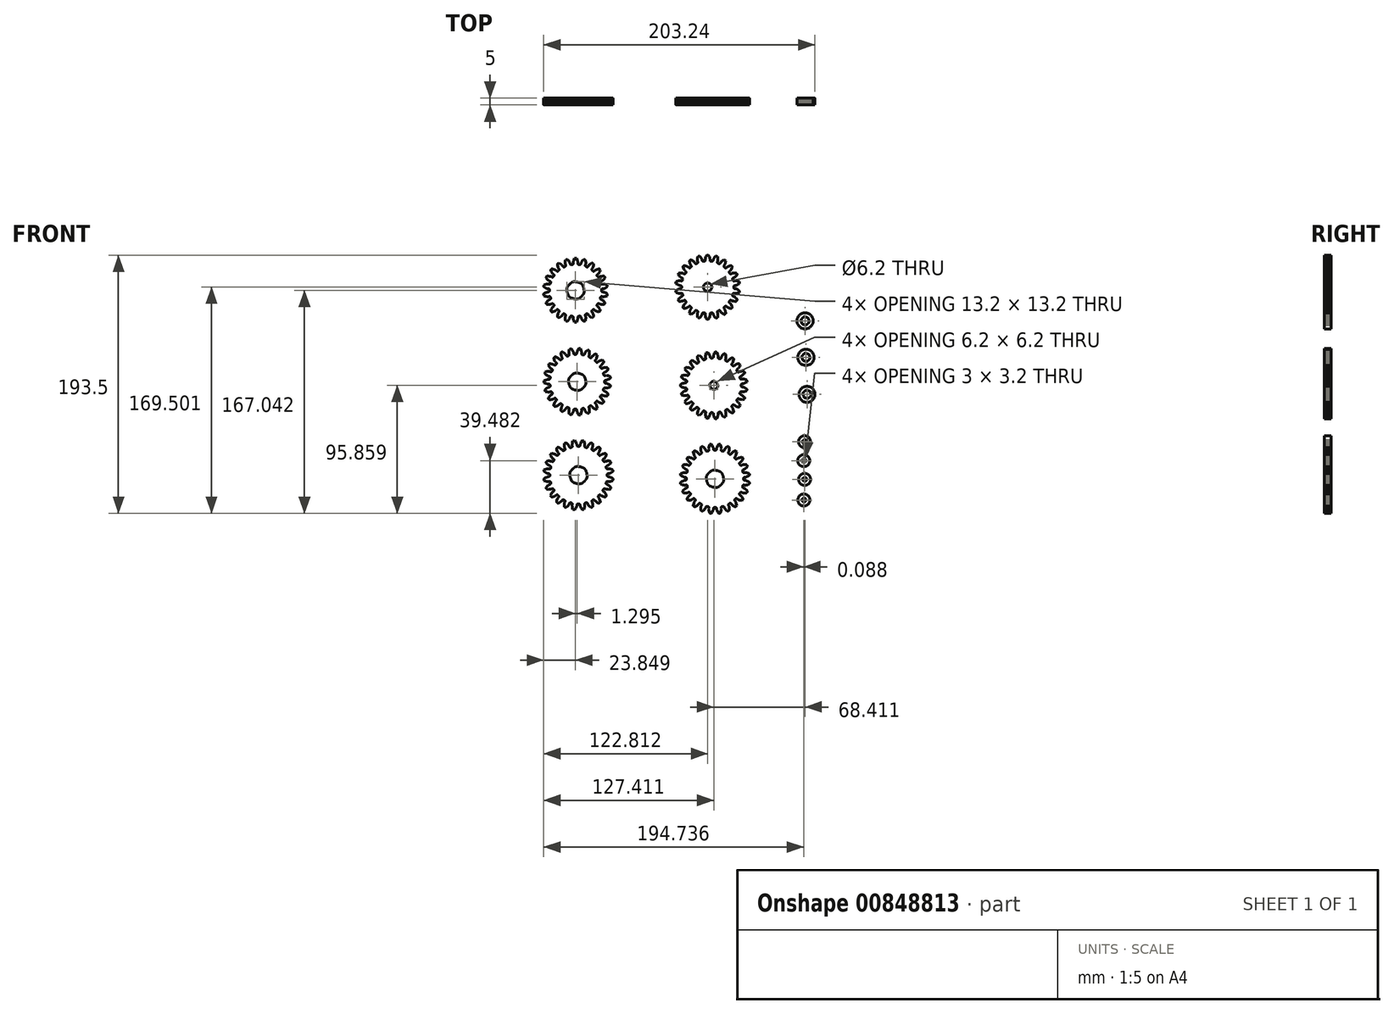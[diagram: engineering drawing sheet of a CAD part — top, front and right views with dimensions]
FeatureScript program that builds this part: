
annotation { "Feature Type Name" : "Feature", "Feature Type Description" : "" }
export const myFeature = defineFeature(function(context is Context, id is Id, definition is map)
    precondition{}
    {
        {
            var Q0;
            Q0=qCreatedBy(makeId("Front.planeOp"),FACE);
            var sketch = newSketch(context, id + "F0", { "sketchPlane" : qUnion([Q0])});
            skArc(sketch, "E0", {"start": v(8.16, 58.25) * mm, "mid": v(8.42, 58.01) * mm, "end": v(8.7, 57.79) * mm});
            skArc(sketch, "E1", {"start": v(8.16, 58.25) * mm, "mid": v(7.61, 58.45) * mm, "end": v(7.08, 58.2) * mm});
            skLineSegment(sketch, "E2", {"start": v(4.56, 56.78) * mm, "end": v(3.52, 56.5) * mm});
            skLineSegment(sketch, "E3", {"start": v(5.47, 57.12) * mm, "end": v(4.56, 56.78) * mm});
            skLineSegment(sketch, "E4", {"start": v(5.8, 57.28) * mm, "end": v(5.47, 57.12) * mm});
            skLineSegment(sketch, "E5", {"start": v(6.11, 57.44) * mm, "end": v(5.8, 57.28) * mm});
            skLineSegment(sketch, "E6", {"start": v(6.38, 57.6) * mm, "end": v(6.11, 57.44) * mm});
            skLineSegment(sketch, "E7", {"start": v(6.6, 57.75) * mm, "end": v(6.38, 57.6) * mm});
            skLineSegment(sketch, "E8", {"start": v(6.75, 57.88) * mm, "end": v(6.6, 57.75) * mm});
            skLineSegment(sketch, "E9", {"start": v(7.08, 58.2) * mm, "end": v(6.75, 57.88) * mm});
            skArc(sketch, "E10", {"start": v(2.6, 57.57) * mm, "mid": v(3.05, 57.03) * mm, "end": v(3.52, 56.5) * mm});
            skLineSegment(sketch, "E11", {"start": v(3.02, 58.56) * mm, "end": v(2.6, 57.57) * mm});
            skLineSegment(sketch, "E12", {"start": v(3.48, 59.41) * mm, "end": v(3.02, 58.56) * mm});
            skLineSegment(sketch, "E13", {"start": v(3.69, 59.72) * mm, "end": v(3.48, 59.41) * mm});
            skLineSegment(sketch, "E14", {"start": v(3.89, 60) * mm, "end": v(3.69, 59.72) * mm});
            skLineSegment(sketch, "E15", {"start": v(4.09, 60.24) * mm, "end": v(3.89, 60) * mm});
            skLineSegment(sketch, "E16", {"start": v(4.27, 60.44) * mm, "end": v(4.09, 60.24) * mm});
            skLineSegment(sketch, "E17", {"start": v(4.42, 60.58) * mm, "end": v(4.27, 60.44) * mm});
            skLineSegment(sketch, "E18", {"start": v(4.8, 60.85) * mm, "end": v(4.42, 60.58) * mm});
            skArc(sketch, "E19", {"start": v(4.8, 60.85) * mm, "mid": v(5.1, 61.35) * mm, "end": v(4.98, 61.91) * mm});
            skArc(sketch, "E20", {"start": v(4.6, 62.5) * mm, "mid": v(4.79, 62.2) * mm, "end": v(4.98, 61.92) * mm});
            skArc(sketch, "E21", {"start": v(4.6, 62.5) * mm, "mid": v(4.13, 62.85) * mm, "end": v(3.56, 62.77) * mm});
            skLineSegment(sketch, "E22", {"start": v(0.74, 62.11) * mm, "end": v(-0.34, 62.15) * mm});
            skLineSegment(sketch, "E23", {"start": v(1.7, 62.18) * mm, "end": v(0.74, 62.11) * mm});
            skLineSegment(sketch, "E24", {"start": v(2.07, 62.24) * mm, "end": v(1.7, 62.18) * mm});
            skLineSegment(sketch, "E25", {"start": v(2.4, 62.3) * mm, "end": v(2.07, 62.24) * mm});
            skLineSegment(sketch, "E26", {"start": v(2.7, 62.39) * mm, "end": v(2.4, 62.3) * mm});
            skLineSegment(sketch, "E27", {"start": v(2.97, 62.47) * mm, "end": v(2.7, 62.39) * mm});
            skLineSegment(sketch, "E28", {"start": v(3.15, 62.55) * mm, "end": v(2.97, 62.47) * mm});
            skLineSegment(sketch, "E29", {"start": v(3.56, 62.77) * mm, "end": v(3.15, 62.55) * mm});
            skArc(sketch, "E30", {"start": v(-0.92, 63.43) * mm, "mid": v(-0.64, 62.78) * mm, "end": v(-0.34, 62.15) * mm});
            skLineSegment(sketch, "E31", {"start": v(-0.24, 64.26) * mm, "end": v(-0.92, 63.43) * mm});
            skLineSegment(sketch, "E32", {"start": v(0.44, 64.94) * mm, "end": v(-0.24, 64.26) * mm});
            skLineSegment(sketch, "E33", {"start": v(0.73, 65.18) * mm, "end": v(0.44, 64.94) * mm});
            skLineSegment(sketch, "E34", {"start": v(1, 65.4) * mm, "end": v(0.73, 65.18) * mm});
            skLineSegment(sketch, "E35", {"start": v(1.26, 65.57) * mm, "end": v(1, 65.4) * mm});
            skLineSegment(sketch, "E36", {"start": v(1.49, 65.7) * mm, "end": v(1.26, 65.57) * mm});
            skLineSegment(sketch, "E37", {"start": v(1.67, 65.8) * mm, "end": v(1.49, 65.7) * mm});
            skLineSegment(sketch, "E38", {"start": v(2.1, 65.96) * mm, "end": v(1.67, 65.8) * mm});
            skArc(sketch, "E39", {"start": v(2.1, 65.96) * mm, "mid": v(2.54, 66.34) * mm, "end": v(2.58, 66.92) * mm});
            skArc(sketch, "E40", {"start": v(2.39, 67.6) * mm, "mid": v(2.48, 67.26) * mm, "end": v(2.58, 66.92) * mm});
            skArc(sketch, "E41", {"start": v(2.39, 67.6) * mm, "mid": v(2.03, 68.06) * mm, "end": v(1.46, 68.15) * mm});
            skLineSegment(sketch, "E42", {"start": v(-1.43, 68.3) * mm, "end": v(-2.45, 68.64) * mm});
            skLineSegment(sketch, "E43", {"start": v(-0.49, 68.1) * mm, "end": v(-1.43, 68.3) * mm});
            skLineSegment(sketch, "E44", {"start": v(-0.12, 68.05) * mm, "end": v(-0.49, 68.1) * mm});
            skLineSegment(sketch, "E45", {"start": v(0.23, 68.02) * mm, "end": v(-0.12, 68.05) * mm});
            skLineSegment(sketch, "E46", {"start": v(0.54, 68.02) * mm, "end": v(0.23, 68.02) * mm});
            skLineSegment(sketch, "E47", {"start": v(0.8, 68.02) * mm, "end": v(0.54, 68.02) * mm});
            skLineSegment(sketch, "E48", {"start": v(1, 68.05) * mm, "end": v(0.8, 68.02) * mm});
            skLineSegment(sketch, "E49", {"start": v(1.46, 68.15) * mm, "end": v(1, 68.05) * mm});
            skArc(sketch, "E50", {"start": v(-2.65, 70.03) * mm, "mid": v(-2.56, 69.34) * mm, "end": v(-2.45, 68.64) * mm});
            skLineSegment(sketch, "E51", {"start": v(-1.77, 70.64) * mm, "end": v(-2.65, 70.03) * mm});
            skLineSegment(sketch, "E52", {"start": v(-0.92, 71.1) * mm, "end": v(-1.77, 70.64) * mm});
            skLineSegment(sketch, "E53", {"start": v(-0.58, 71.26) * mm, "end": v(-0.92, 71.1) * mm});
            skLineSegment(sketch, "E54", {"start": v(-0.26, 71.38) * mm, "end": v(-0.58, 71.26) * mm});
            skLineSegment(sketch, "E55", {"start": v(0.04, 71.48) * mm, "end": v(-0.26, 71.38) * mm});
            skLineSegment(sketch, "E56", {"start": v(0.3, 71.54) * mm, "end": v(0.04, 71.48) * mm});
            skLineSegment(sketch, "E57", {"start": v(0.5, 71.58) * mm, "end": v(0.3, 71.54) * mm});
            skLineSegment(sketch, "E58", {"start": v(0.96, 71.6) * mm, "end": v(0.5, 71.58) * mm});
            skArc(sketch, "E59", {"start": v(0.96, 71.6) * mm, "mid": v(1.49, 71.86) * mm, "end": v(1.7, 72.4) * mm});
            skArc(sketch, "E60", {"start": v(1.7, 73.1) * mm, "mid": v(1.7, 72.75) * mm, "end": v(1.7, 72.4) * mm});
            skArc(sketch, "E61", {"start": v(1.7, 73.1) * mm, "mid": v(1.49, 73.65) * mm, "end": v(0.96, 73.9) * mm});
            skLineSegment(sketch, "E62", {"start": v(-1.77, 74.86) * mm, "end": v(-2.65, 75.47) * mm});
            skLineSegment(sketch, "E63", {"start": v(-0.92, 74.4) * mm, "end": v(-1.77, 74.86) * mm});
            skLineSegment(sketch, "E64", {"start": v(-0.58, 74.25) * mm, "end": v(-0.92, 74.4) * mm});
            skLineSegment(sketch, "E65", {"start": v(-0.26, 74.12) * mm, "end": v(-0.58, 74.25) * mm});
            skLineSegment(sketch, "E66", {"start": v(0.04, 74.03) * mm, "end": v(-0.26, 74.12) * mm});
            skLineSegment(sketch, "E67", {"start": v(0.3, 73.96) * mm, "end": v(0.04, 74.03) * mm});
            skLineSegment(sketch, "E68", {"start": v(0.5, 73.92) * mm, "end": v(0.3, 73.96) * mm});
            skLineSegment(sketch, "E69", {"start": v(0.96, 73.9) * mm, "end": v(0.5, 73.92) * mm});
            skArc(sketch, "E70", {"start": v(-2.45, 76.86) * mm, "mid": v(-2.56, 76.17) * mm, "end": v(-2.65, 75.47) * mm});
            skLineSegment(sketch, "E71", {"start": v(-1.43, 77.2) * mm, "end": v(-2.45, 76.86) * mm});
            skLineSegment(sketch, "E72", {"start": v(-0.49, 77.4) * mm, "end": v(-1.43, 77.2) * mm});
            skLineSegment(sketch, "E73", {"start": v(-0.12, 77.45) * mm, "end": v(-0.49, 77.4) * mm});
            skLineSegment(sketch, "E74", {"start": v(0.23, 77.48) * mm, "end": v(-0.12, 77.45) * mm});
            skLineSegment(sketch, "E75", {"start": v(0.54, 77.49) * mm, "end": v(0.23, 77.48) * mm});
            skLineSegment(sketch, "E76", {"start": v(0.8, 77.48) * mm, "end": v(0.54, 77.49) * mm});
            skLineSegment(sketch, "E77", {"start": v(1, 77.46) * mm, "end": v(0.8, 77.48) * mm});
            skLineSegment(sketch, "E78", {"start": v(1.46, 77.36) * mm, "end": v(1, 77.46) * mm});
            skArc(sketch, "E79", {"start": v(1.46, 77.36) * mm, "mid": v(2.03, 77.44) * mm, "end": v(2.39, 77.9) * mm});
            skArc(sketch, "E80", {"start": v(2.58, 78.58) * mm, "mid": v(2.48, 78.25) * mm, "end": v(2.39, 77.9) * mm});
            skArc(sketch, "E81", {"start": v(2.58, 78.58) * mm, "mid": v(2.54, 79.16) * mm, "end": v(2.1, 79.55) * mm});
            skLineSegment(sketch, "E82", {"start": v(-0.24, 81.24) * mm, "end": v(-0.92, 82.08) * mm});
            skLineSegment(sketch, "E83", {"start": v(0.44, 80.56) * mm, "end": v(-0.24, 81.24) * mm});
            skLineSegment(sketch, "E84", {"start": v(0.73, 80.32) * mm, "end": v(0.44, 80.56) * mm});
            skLineSegment(sketch, "E85", {"start": v(1, 80.1) * mm, "end": v(0.73, 80.32) * mm});
            skLineSegment(sketch, "E86", {"start": v(1.26, 79.93) * mm, "end": v(1, 80.1) * mm});
            skLineSegment(sketch, "E87", {"start": v(1.49, 79.8) * mm, "end": v(1.26, 79.93) * mm});
            skLineSegment(sketch, "E88", {"start": v(1.67, 79.7) * mm, "end": v(1.49, 79.8) * mm});
            skLineSegment(sketch, "E89", {"start": v(2.1, 79.55) * mm, "end": v(1.67, 79.7) * mm});
            skArc(sketch, "E90", {"start": v(-0.34, 83.36) * mm, "mid": v(-0.64, 82.72) * mm, "end": v(-0.92, 82.08) * mm});
            skLineSegment(sketch, "E91", {"start": v(0.74, 83.39) * mm, "end": v(-0.34, 83.36) * mm});
            skLineSegment(sketch, "E92", {"start": v(1.7, 83.32) * mm, "end": v(0.74, 83.39) * mm});
            skLineSegment(sketch, "E93", {"start": v(2.07, 83.26) * mm, "end": v(1.7, 83.32) * mm});
            skLineSegment(sketch, "E94", {"start": v(2.4, 83.2) * mm, "end": v(2.07, 83.26) * mm});
            skLineSegment(sketch, "E95", {"start": v(2.7, 83.11) * mm, "end": v(2.4, 83.2) * mm});
            skLineSegment(sketch, "E96", {"start": v(2.97, 83.03) * mm, "end": v(2.7, 83.11) * mm});
            skLineSegment(sketch, "E97", {"start": v(3.15, 82.95) * mm, "end": v(2.97, 83.03) * mm});
            skLineSegment(sketch, "E98", {"start": v(3.56, 82.73) * mm, "end": v(3.15, 82.95) * mm});
            skArc(sketch, "E99", {"start": v(3.56, 82.73) * mm, "mid": v(4.13, 82.65) * mm, "end": v(4.6, 83) * mm});
            skArc(sketch, "E100", {"start": v(4.98, 83.59) * mm, "mid": v(4.79, 83.3) * mm, "end": v(4.6, 83) * mm});
            skArc(sketch, "E101", {"start": v(4.98, 83.59) * mm, "mid": v(5.1, 84.16) * mm, "end": v(4.8, 84.65) * mm});
            skLineSegment(sketch, "E102", {"start": v(3.02, 86.94) * mm, "end": v(2.6, 87.93) * mm});
            skLineSegment(sketch, "E103", {"start": v(3.48, 86.1) * mm, "end": v(3.02, 86.94) * mm});
            skLineSegment(sketch, "E104", {"start": v(3.69, 85.78) * mm, "end": v(3.48, 86.1) * mm});
            skLineSegment(sketch, "E105", {"start": v(3.89, 85.5) * mm, "end": v(3.69, 85.78) * mm});
            skLineSegment(sketch, "E106", {"start": v(4.09, 85.26) * mm, "end": v(3.89, 85.5) * mm});
            skLineSegment(sketch, "E107", {"start": v(4.27, 85.06) * mm, "end": v(4.09, 85.26) * mm});
            skLineSegment(sketch, "E108", {"start": v(4.42, 84.93) * mm, "end": v(4.27, 85.06) * mm});
            skLineSegment(sketch, "E109", {"start": v(4.8, 84.65) * mm, "end": v(4.42, 84.93) * mm});
            skArc(sketch, "E110", {"start": v(3.52, 89) * mm, "mid": v(3.05, 88.47) * mm, "end": v(2.6, 87.93) * mm});
            skLineSegment(sketch, "E111", {"start": v(4.56, 88.72) * mm, "end": v(3.52, 89) * mm});
            skLineSegment(sketch, "E112", {"start": v(5.47, 88.38) * mm, "end": v(4.56, 88.72) * mm});
            skLineSegment(sketch, "E113", {"start": v(5.8, 88.23) * mm, "end": v(5.47, 88.38) * mm});
            skLineSegment(sketch, "E114", {"start": v(6.11, 88.06) * mm, "end": v(5.8, 88.23) * mm});
            skLineSegment(sketch, "E115", {"start": v(6.38, 87.9) * mm, "end": v(6.11, 88.06) * mm});
            skLineSegment(sketch, "E116", {"start": v(6.6, 87.75) * mm, "end": v(6.38, 87.9) * mm});
            skLineSegment(sketch, "E117", {"start": v(6.75, 87.62) * mm, "end": v(6.6, 87.75) * mm});
            skLineSegment(sketch, "E118", {"start": v(7.08, 87.3) * mm, "end": v(6.75, 87.62) * mm});
            skArc(sketch, "E119", {"start": v(7.08, 87.3) * mm, "mid": v(7.61, 87.06) * mm, "end": v(8.16, 87.26) * mm});
            skArc(sketch, "E120", {"start": v(8.7, 87.72) * mm, "mid": v(8.42, 87.49) * mm, "end": v(8.16, 87.26) * mm});
            skArc(sketch, "E121", {"start": v(8.7, 87.72) * mm, "mid": v(8.96, 88.23) * mm, "end": v(8.8, 88.79) * mm});
            skLineSegment(sketch, "E122", {"start": v(7.75, 91.49) * mm, "end": v(7.63, 92.55) * mm});
            skLineSegment(sketch, "E123", {"start": v(7.96, 90.54) * mm, "end": v(7.75, 91.49) * mm});
            skLineSegment(sketch, "E124", {"start": v(8.07, 90.18) * mm, "end": v(7.96, 90.54) * mm});
            skLineSegment(sketch, "E125", {"start": v(8.18, 89.86) * mm, "end": v(8.07, 90.18) * mm});
            skLineSegment(sketch, "E126", {"start": v(8.3, 89.57) * mm, "end": v(8.18, 89.86) * mm});
            skLineSegment(sketch, "E127", {"start": v(8.42, 89.33) * mm, "end": v(8.3, 89.57) * mm});
            skLineSegment(sketch, "E128", {"start": v(8.53, 89.16) * mm, "end": v(8.42, 89.33) * mm});
            skLineSegment(sketch, "E129", {"start": v(8.8, 88.79) * mm, "end": v(8.53, 89.16) * mm});
            skArc(sketch, "E130", {"start": v(8.82, 93.31) * mm, "mid": v(8.22, 92.94) * mm, "end": v(7.63, 92.55) * mm});
            skLineSegment(sketch, "E131", {"start": v(9.74, 92.76) * mm, "end": v(8.82, 93.31) * mm});
            skLineSegment(sketch, "E132", {"start": v(10.5, 92.18) * mm, "end": v(9.74, 92.76) * mm});
            skLineSegment(sketch, "E133", {"start": v(10.79, 91.93) * mm, "end": v(10.5, 92.18) * mm});
            skLineSegment(sketch, "E134", {"start": v(11.04, 91.7) * mm, "end": v(10.79, 91.93) * mm});
            skLineSegment(sketch, "E135", {"start": v(11.25, 91.46) * mm, "end": v(11.04, 91.7) * mm});
            skLineSegment(sketch, "E136", {"start": v(11.42, 91.25) * mm, "end": v(11.25, 91.46) * mm});
            skLineSegment(sketch, "E137", {"start": v(11.53, 91.09) * mm, "end": v(11.42, 91.25) * mm});
            skLineSegment(sketch, "E138", {"start": v(11.75, 90.68) * mm, "end": v(11.53, 91.09) * mm});
            skArc(sketch, "E139", {"start": v(11.75, 90.68) * mm, "mid": v(12.2, 90.3) * mm, "end": v(12.77, 90.34) * mm});
            skArc(sketch, "E140", {"start": v(13.41, 90.63) * mm, "mid": v(13.1, 90.49) * mm, "end": v(12.77, 90.34) * mm});
            skArc(sketch, "E141", {"start": v(13.41, 90.63) * mm, "mid": v(13.82, 91.05) * mm, "end": v(13.83, 91.63) * mm});
            skLineSegment(sketch, "E142", {"start": v(13.57, 94.51) * mm, "end": v(13.76, 95.57) * mm});
            skLineSegment(sketch, "E143", {"start": v(13.5, 93.55) * mm, "end": v(13.57, 94.51) * mm});
            skLineSegment(sketch, "E144", {"start": v(13.5, 93.18) * mm, "end": v(13.5, 93.55) * mm});
            skLineSegment(sketch, "E145", {"start": v(13.53, 92.83) * mm, "end": v(13.5, 93.18) * mm});
            skLineSegment(sketch, "E146", {"start": v(13.57, 92.52) * mm, "end": v(13.53, 92.83) * mm});
            skLineSegment(sketch, "E147", {"start": v(13.61, 92.26) * mm, "end": v(13.57, 92.52) * mm});
            skLineSegment(sketch, "E148", {"start": v(13.66, 92.06) * mm, "end": v(13.61, 92.26) * mm});
            skLineSegment(sketch, "E149", {"start": v(13.83, 91.63) * mm, "end": v(13.66, 92.06) * mm});
            skArc(sketch, "E150", {"start": v(15.1, 95.97) * mm, "mid": v(14.43, 95.78) * mm, "end": v(13.76, 95.57) * mm});
            skLineSegment(sketch, "E151", {"start": v(15.84, 95.18) * mm, "end": v(15.1, 95.97) * mm});
            skLineSegment(sketch, "E152", {"start": v(16.42, 94.4) * mm, "end": v(15.84, 95.18) * mm});
            skLineSegment(sketch, "E153", {"start": v(16.61, 94.09) * mm, "end": v(16.42, 94.4) * mm});
            skLineSegment(sketch, "E154", {"start": v(16.78, 93.79) * mm, "end": v(16.61, 94.09) * mm});
            skLineSegment(sketch, "E155", {"start": v(16.92, 93.5) * mm, "end": v(16.78, 93.79) * mm});
            skLineSegment(sketch, "E156", {"start": v(17.02, 93.26) * mm, "end": v(16.92, 93.5) * mm});
            skLineSegment(sketch, "E157", {"start": v(17.09, 93.07) * mm, "end": v(17.02, 93.26) * mm});
            skLineSegment(sketch, "E158", {"start": v(17.18, 92.61) * mm, "end": v(17.09, 93.07) * mm});
            skArc(sketch, "E159", {"start": v(17.18, 92.61) * mm, "mid": v(17.5, 92.13) * mm, "end": v(18.07, 92) * mm});
            skArc(sketch, "E160", {"start": v(18.77, 92.1) * mm, "mid": v(18.42, 92.05) * mm, "end": v(18.07, 92) * mm});
            skArc(sketch, "E161", {"start": v(18.77, 92.1) * mm, "mid": v(19.27, 92.38) * mm, "end": v(19.44, 92.94) * mm});
            skLineSegment(sketch, "E162", {"start": v(20.01, 95.78) * mm, "end": v(20.49, 96.74) * mm});
            skLineSegment(sketch, "E163", {"start": v(19.68, 94.87) * mm, "end": v(20.01, 95.78) * mm});
            skLineSegment(sketch, "E164", {"start": v(19.57, 94.51) * mm, "end": v(19.68, 94.87) * mm});
            skLineSegment(sketch, "E165", {"start": v(19.5, 94.18) * mm, "end": v(19.57, 94.51) * mm});
            skLineSegment(sketch, "E166", {"start": v(19.44, 93.87) * mm, "end": v(19.5, 94.18) * mm});
            skLineSegment(sketch, "E167", {"start": v(19.42, 93.6) * mm, "end": v(19.44, 93.87) * mm});
            skLineSegment(sketch, "E168", {"start": v(19.4, 93.4) * mm, "end": v(19.42, 93.6) * mm});
            skLineSegment(sketch, "E169", {"start": v(19.44, 92.94) * mm, "end": v(19.4, 93.4) * mm});
            skArc(sketch, "E170", {"start": v(21.9, 96.74) * mm, "mid": v(21.2, 96.75) * mm, "end": v(20.49, 96.74) * mm});
            skLineSegment(sketch, "E171", {"start": v(22.37, 95.78) * mm, "end": v(21.9, 96.74) * mm});
            skLineSegment(sketch, "E172", {"start": v(22.7, 94.87) * mm, "end": v(22.37, 95.78) * mm});
            skLineSegment(sketch, "E173", {"start": v(22.81, 94.51) * mm, "end": v(22.7, 94.87) * mm});
            skLineSegment(sketch, "E174", {"start": v(22.89, 94.18) * mm, "end": v(22.81, 94.51) * mm});
            skLineSegment(sketch, "E175", {"start": v(22.94, 93.87) * mm, "end": v(22.89, 94.18) * mm});
            skLineSegment(sketch, "E176", {"start": v(22.97, 93.6) * mm, "end": v(22.94, 93.87) * mm});
            skLineSegment(sketch, "E177", {"start": v(22.98, 93.4) * mm, "end": v(22.97, 93.6) * mm});
            skLineSegment(sketch, "E178", {"start": v(22.94, 92.94) * mm, "end": v(22.98, 93.4) * mm});
            skArc(sketch, "E179", {"start": v(22.94, 92.94) * mm, "mid": v(23.11, 92.38) * mm, "end": v(23.62, 92.1) * mm});
            skArc(sketch, "E180", {"start": v(24.32, 92) * mm, "mid": v(23.97, 92.05) * mm, "end": v(23.62, 92.1) * mm});
            skArc(sketch, "E181", {"start": v(24.32, 92) * mm, "mid": v(24.88, 92.13) * mm, "end": v(25.2, 92.61) * mm});
            skLineSegment(sketch, "E182", {"start": v(26.55, 95.18) * mm, "end": v(27.28, 95.97) * mm});
            skLineSegment(sketch, "E183", {"start": v(25.97, 94.4) * mm, "end": v(26.55, 95.18) * mm});
            skLineSegment(sketch, "E184", {"start": v(25.77, 94.09) * mm, "end": v(25.97, 94.4) * mm});
            skLineSegment(sketch, "E185", {"start": v(25.6, 93.79) * mm, "end": v(25.77, 94.09) * mm});
            skLineSegment(sketch, "E186", {"start": v(25.46, 93.5) * mm, "end": v(25.6, 93.79) * mm});
            skLineSegment(sketch, "E187", {"start": v(25.36, 93.26) * mm, "end": v(25.46, 93.5) * mm});
            skLineSegment(sketch, "E188", {"start": v(25.3, 93.07) * mm, "end": v(25.36, 93.26) * mm});
            skLineSegment(sketch, "E189", {"start": v(25.2, 92.61) * mm, "end": v(25.3, 93.07) * mm});
            skArc(sketch, "E190", {"start": v(28.63, 95.57) * mm, "mid": v(27.95, 95.78) * mm, "end": v(27.28, 95.97) * mm});
            skLineSegment(sketch, "E191", {"start": v(28.81, 94.51) * mm, "end": v(28.63, 95.57) * mm});
            skLineSegment(sketch, "E192", {"start": v(28.88, 93.55) * mm, "end": v(28.81, 94.51) * mm});
            skLineSegment(sketch, "E193", {"start": v(28.88, 93.18) * mm, "end": v(28.88, 93.55) * mm});
            skLineSegment(sketch, "E194", {"start": v(28.86, 92.83) * mm, "end": v(28.88, 93.18) * mm});
            skLineSegment(sketch, "E195", {"start": v(28.82, 92.52) * mm, "end": v(28.86, 92.83) * mm});
            skLineSegment(sketch, "E196", {"start": v(28.77, 92.26) * mm, "end": v(28.82, 92.52) * mm});
            skLineSegment(sketch, "E197", {"start": v(28.72, 92.06) * mm, "end": v(28.77, 92.26) * mm});
            skLineSegment(sketch, "E198", {"start": v(28.56, 91.63) * mm, "end": v(28.72, 92.06) * mm});
            skArc(sketch, "E199", {"start": v(28.56, 91.63) * mm, "mid": v(28.56, 91.05) * mm, "end": v(28.97, 90.63) * mm});
            skArc(sketch, "E200", {"start": v(29.61, 90.34) * mm, "mid": v(29.3, 90.49) * mm, "end": v(28.97, 90.63) * mm});
            skArc(sketch, "E201", {"start": v(29.61, 90.34) * mm, "mid": v(30.2, 90.3) * mm, "end": v(30.64, 90.68) * mm});
            skLineSegment(sketch, "E202", {"start": v(32.65, 92.76) * mm, "end": v(33.57, 93.31) * mm});
            skLineSegment(sketch, "E203", {"start": v(31.88, 92.18) * mm, "end": v(32.65, 92.76) * mm});
            skLineSegment(sketch, "E204", {"start": v(31.6, 91.93) * mm, "end": v(31.88, 92.18) * mm});
            skLineSegment(sketch, "E205", {"start": v(31.35, 91.7) * mm, "end": v(31.6, 91.93) * mm});
            skLineSegment(sketch, "E206", {"start": v(31.14, 91.46) * mm, "end": v(31.35, 91.7) * mm});
            skLineSegment(sketch, "E207", {"start": v(30.97, 91.25) * mm, "end": v(31.14, 91.46) * mm});
            skLineSegment(sketch, "E208", {"start": v(30.86, 91.09) * mm, "end": v(30.97, 91.25) * mm});
            skLineSegment(sketch, "E209", {"start": v(30.64, 90.68) * mm, "end": v(30.86, 91.09) * mm});
            skArc(sketch, "E210", {"start": v(34.75, 92.55) * mm, "mid": v(34.17, 92.94) * mm, "end": v(33.57, 93.31) * mm});
            skLineSegment(sketch, "E211", {"start": v(34.63, 91.49) * mm, "end": v(34.75, 92.55) * mm});
            skLineSegment(sketch, "E212", {"start": v(34.43, 90.54) * mm, "end": v(34.63, 91.49) * mm});
            skLineSegment(sketch, "E213", {"start": v(34.32, 90.18) * mm, "end": v(34.43, 90.54) * mm});
            skLineSegment(sketch, "E214", {"start": v(34.2, 89.86) * mm, "end": v(34.32, 90.18) * mm});
            skLineSegment(sketch, "E215", {"start": v(34.08, 89.57) * mm, "end": v(34.2, 89.86) * mm});
            skLineSegment(sketch, "E216", {"start": v(33.96, 89.33) * mm, "end": v(34.08, 89.57) * mm});
            skLineSegment(sketch, "E217", {"start": v(33.86, 89.16) * mm, "end": v(33.96, 89.33) * mm});
            skLineSegment(sketch, "E218", {"start": v(33.58, 88.79) * mm, "end": v(33.86, 89.16) * mm});
            skArc(sketch, "E219", {"start": v(33.58, 88.79) * mm, "mid": v(33.42, 88.23) * mm, "end": v(33.7, 87.72) * mm});
            skArc(sketch, "E220", {"start": v(34.23, 87.26) * mm, "mid": v(33.96, 87.49) * mm, "end": v(33.7, 87.72) * mm});
            skArc(sketch, "E221", {"start": v(34.23, 87.26) * mm, "mid": v(34.77, 87.06) * mm, "end": v(35.3, 87.3) * mm});
            skLineSegment(sketch, "E222", {"start": v(37.82, 88.72) * mm, "end": v(38.86, 89) * mm});
            skLineSegment(sketch, "E223", {"start": v(36.92, 88.38) * mm, "end": v(37.82, 88.72) * mm});
            skLineSegment(sketch, "E224", {"start": v(36.58, 88.23) * mm, "end": v(36.92, 88.38) * mm});
            skLineSegment(sketch, "E225", {"start": v(36.27, 88.06) * mm, "end": v(36.58, 88.23) * mm});
            skLineSegment(sketch, "E226", {"start": v(36, 87.9) * mm, "end": v(36.27, 88.06) * mm});
            skLineSegment(sketch, "E227", {"start": v(35.79, 87.75) * mm, "end": v(36, 87.9) * mm});
            skLineSegment(sketch, "E228", {"start": v(35.63, 87.62) * mm, "end": v(35.79, 87.75) * mm});
            skLineSegment(sketch, "E229", {"start": v(35.3, 87.3) * mm, "end": v(35.63, 87.62) * mm});
            skArc(sketch, "E230", {"start": v(39.78, 87.93) * mm, "mid": v(39.33, 88.47) * mm, "end": v(38.86, 89) * mm});
            skLineSegment(sketch, "E231", {"start": v(39.37, 86.94) * mm, "end": v(39.78, 87.93) * mm});
            skLineSegment(sketch, "E232", {"start": v(38.9, 86.1) * mm, "end": v(39.37, 86.94) * mm});
            skLineSegment(sketch, "E233", {"start": v(38.7, 85.78) * mm, "end": v(38.9, 86.1) * mm});
            skLineSegment(sketch, "E234", {"start": v(38.5, 85.5) * mm, "end": v(38.7, 85.78) * mm});
            skLineSegment(sketch, "E235", {"start": v(38.3, 85.26) * mm, "end": v(38.5, 85.5) * mm});
            skLineSegment(sketch, "E236", {"start": v(38.11, 85.06) * mm, "end": v(38.3, 85.26) * mm});
            skLineSegment(sketch, "E237", {"start": v(37.97, 84.93) * mm, "end": v(38.11, 85.06) * mm});
            skLineSegment(sketch, "E238", {"start": v(37.6, 84.65) * mm, "end": v(37.97, 84.93) * mm});
            skArc(sketch, "E239", {"start": v(37.6, 84.65) * mm, "mid": v(37.29, 84.16) * mm, "end": v(37.4, 83.59) * mm});
            skArc(sketch, "E240", {"start": v(37.78, 83) * mm, "mid": v(37.6, 83.3) * mm, "end": v(37.4, 83.59) * mm});
            skArc(sketch, "E241", {"start": v(37.78, 83) * mm, "mid": v(38.25, 82.65) * mm, "end": v(38.83, 82.73) * mm});
            skLineSegment(sketch, "E242", {"start": v(41.65, 83.39) * mm, "end": v(42.72, 83.36) * mm});
            skLineSegment(sketch, "E243", {"start": v(40.68, 83.32) * mm, "end": v(41.65, 83.39) * mm});
            skLineSegment(sketch, "E244", {"start": v(40.31, 83.26) * mm, "end": v(40.68, 83.32) * mm});
            skLineSegment(sketch, "E245", {"start": v(39.98, 83.2) * mm, "end": v(40.31, 83.26) * mm});
            skLineSegment(sketch, "E246", {"start": v(39.68, 83.11) * mm, "end": v(39.98, 83.2) * mm});
            skLineSegment(sketch, "E247", {"start": v(39.42, 83.03) * mm, "end": v(39.68, 83.11) * mm});
            skLineSegment(sketch, "E248", {"start": v(39.24, 82.95) * mm, "end": v(39.42, 83.03) * mm});
            skLineSegment(sketch, "E249", {"start": v(38.83, 82.73) * mm, "end": v(39.24, 82.95) * mm});
            skArc(sketch, "E250", {"start": v(43.3, 82.08) * mm, "mid": v(43.02, 82.72) * mm, "end": v(42.72, 83.36) * mm});
            skLineSegment(sketch, "E251", {"start": v(42.63, 81.24) * mm, "end": v(43.3, 82.08) * mm});
            skLineSegment(sketch, "E252", {"start": v(41.94, 80.56) * mm, "end": v(42.63, 81.24) * mm});
            skLineSegment(sketch, "E253", {"start": v(41.66, 80.32) * mm, "end": v(41.94, 80.56) * mm});
            skLineSegment(sketch, "E254", {"start": v(41.39, 80.1) * mm, "end": v(41.66, 80.32) * mm});
            skLineSegment(sketch, "E255", {"start": v(41.13, 79.93) * mm, "end": v(41.39, 80.1) * mm});
            skLineSegment(sketch, "E256", {"start": v(40.9, 79.8) * mm, "end": v(41.13, 79.93) * mm});
            skLineSegment(sketch, "E257", {"start": v(40.72, 79.7) * mm, "end": v(40.9, 79.8) * mm});
            skLineSegment(sketch, "E258", {"start": v(40.28, 79.55) * mm, "end": v(40.72, 79.7) * mm});
            skArc(sketch, "E259", {"start": v(40.28, 79.55) * mm, "mid": v(39.85, 79.16) * mm, "end": v(39.8, 78.58) * mm});
            skArc(sketch, "E260", {"start": v(40, 77.9) * mm, "mid": v(39.9, 78.25) * mm, "end": v(39.8, 78.58) * mm});
            skArc(sketch, "E261", {"start": v(40, 77.9) * mm, "mid": v(40.35, 77.44) * mm, "end": v(40.93, 77.36) * mm});
            skLineSegment(sketch, "E262", {"start": v(43.82, 77.2) * mm, "end": v(44.84, 76.86) * mm});
            skLineSegment(sketch, "E263", {"start": v(42.87, 77.4) * mm, "end": v(43.82, 77.2) * mm});
            skLineSegment(sketch, "E264", {"start": v(42.5, 77.45) * mm, "end": v(42.87, 77.4) * mm});
            skLineSegment(sketch, "E265", {"start": v(42.16, 77.48) * mm, "end": v(42.5, 77.45) * mm});
            skLineSegment(sketch, "E266", {"start": v(41.85, 77.49) * mm, "end": v(42.16, 77.48) * mm});
            skLineSegment(sketch, "E267", {"start": v(41.58, 77.48) * mm, "end": v(41.85, 77.49) * mm});
            skLineSegment(sketch, "E268", {"start": v(41.38, 77.46) * mm, "end": v(41.58, 77.48) * mm});
            skLineSegment(sketch, "E269", {"start": v(40.93, 77.36) * mm, "end": v(41.38, 77.46) * mm});
            skArc(sketch, "E270", {"start": v(45.04, 75.47) * mm, "mid": v(44.95, 76.17) * mm, "end": v(44.84, 76.86) * mm});
            skLineSegment(sketch, "E271", {"start": v(44.15, 74.86) * mm, "end": v(45.04, 75.47) * mm});
            skLineSegment(sketch, "E272", {"start": v(43.3, 74.4) * mm, "end": v(44.15, 74.86) * mm});
            skLineSegment(sketch, "E273", {"start": v(42.96, 74.25) * mm, "end": v(43.3, 74.4) * mm});
            skLineSegment(sketch, "E274", {"start": v(42.64, 74.12) * mm, "end": v(42.96, 74.25) * mm});
            skLineSegment(sketch, "E275", {"start": v(42.34, 74.03) * mm, "end": v(42.64, 74.12) * mm});
            skLineSegment(sketch, "E276", {"start": v(42.08, 73.96) * mm, "end": v(42.34, 74.03) * mm});
            skLineSegment(sketch, "E277", {"start": v(41.89, 73.92) * mm, "end": v(42.08, 73.96) * mm});
            skLineSegment(sketch, "E278", {"start": v(41.42, 73.9) * mm, "end": v(41.89, 73.92) * mm});
            skArc(sketch, "E279", {"start": v(41.42, 73.9) * mm, "mid": v(40.9, 73.65) * mm, "end": v(40.69, 73.1) * mm});
            skArc(sketch, "E280", {"start": v(40.69, 72.4) * mm, "mid": v(40.7, 72.75) * mm, "end": v(40.69, 73.1) * mm});
            skArc(sketch, "E281", {"start": v(40.69, 72.4) * mm, "mid": v(40.9, 71.86) * mm, "end": v(41.42, 71.6) * mm});
            skLineSegment(sketch, "E282", {"start": v(44.15, 70.64) * mm, "end": v(45.04, 70.03) * mm});
            skLineSegment(sketch, "E283", {"start": v(43.3, 71.1) * mm, "end": v(44.15, 70.64) * mm});
            skLineSegment(sketch, "E284", {"start": v(42.96, 71.26) * mm, "end": v(43.3, 71.1) * mm});
            skLineSegment(sketch, "E285", {"start": v(42.64, 71.38) * mm, "end": v(42.96, 71.26) * mm});
            skLineSegment(sketch, "E286", {"start": v(42.08, 71.54) * mm, "end": v(42.34, 71.48) * mm});
            skLineSegment(sketch, "E287", {"start": v(41.89, 71.58) * mm, "end": v(42.08, 71.54) * mm});
            skLineSegment(sketch, "E288", {"start": v(41.42, 71.6) * mm, "end": v(41.89, 71.58) * mm});
            skArc(sketch, "E289", {"start": v(44.84, 68.64) * mm, "mid": v(44.95, 69.34) * mm, "end": v(45.04, 70.03) * mm});
            skLineSegment(sketch, "E290", {"start": v(43.82, 68.3) * mm, "end": v(44.84, 68.64) * mm});
            skLineSegment(sketch, "E291", {"start": v(42.87, 68.1) * mm, "end": v(43.82, 68.3) * mm});
            skLineSegment(sketch, "E292", {"start": v(42.5, 68.05) * mm, "end": v(42.87, 68.1) * mm});
            skLineSegment(sketch, "E293", {"start": v(42.16, 68.02) * mm, "end": v(42.5, 68.05) * mm});
            skLineSegment(sketch, "E294", {"start": v(41.85, 68.02) * mm, "end": v(42.16, 68.02) * mm});
            skLineSegment(sketch, "E295", {"start": v(41.58, 68.02) * mm, "end": v(41.85, 68.02) * mm});
            skLineSegment(sketch, "E296", {"start": v(41.38, 68.05) * mm, "end": v(41.58, 68.02) * mm});
            skLineSegment(sketch, "E297", {"start": v(40.93, 68.15) * mm, "end": v(41.38, 68.05) * mm});
            skArc(sketch, "E298", {"start": v(40.93, 68.15) * mm, "mid": v(40.35, 68.06) * mm, "end": v(40, 67.6) * mm});
            skArc(sketch, "E299", {"start": v(39.8, 66.92) * mm, "mid": v(39.9, 67.26) * mm, "end": v(40, 67.6) * mm});
            skArc(sketch, "E300", {"start": v(39.8, 66.92) * mm, "mid": v(39.85, 66.34) * mm, "end": v(40.28, 65.96) * mm});
            skLineSegment(sketch, "E301", {"start": v(42.63, 64.26) * mm, "end": v(43.3, 63.43) * mm});
            skLineSegment(sketch, "E302", {"start": v(41.94, 64.94) * mm, "end": v(42.63, 64.26) * mm});
            skLineSegment(sketch, "E303", {"start": v(41.66, 65.18) * mm, "end": v(41.94, 64.94) * mm});
            skLineSegment(sketch, "E304", {"start": v(41.39, 65.4) * mm, "end": v(41.66, 65.18) * mm});
            skLineSegment(sketch, "E305", {"start": v(41.13, 65.57) * mm, "end": v(41.39, 65.4) * mm});
            skLineSegment(sketch, "E306", {"start": v(40.9, 65.7) * mm, "end": v(41.13, 65.57) * mm});
            skLineSegment(sketch, "E307", {"start": v(40.72, 65.8) * mm, "end": v(40.9, 65.7) * mm});
            skLineSegment(sketch, "E308", {"start": v(40.28, 65.96) * mm, "end": v(40.72, 65.8) * mm});
            skArc(sketch, "E309", {"start": v(42.72, 62.15) * mm, "mid": v(43.02, 62.78) * mm, "end": v(43.3, 63.43) * mm});
            skLineSegment(sketch, "E310", {"start": v(41.65, 62.11) * mm, "end": v(42.72, 62.15) * mm});
            skLineSegment(sketch, "E311", {"start": v(40.68, 62.18) * mm, "end": v(41.65, 62.11) * mm});
            skLineSegment(sketch, "E312", {"start": v(40.31, 62.24) * mm, "end": v(40.68, 62.18) * mm});
            skLineSegment(sketch, "E313", {"start": v(39.98, 62.3) * mm, "end": v(40.31, 62.24) * mm});
            skLineSegment(sketch, "E314", {"start": v(39.68, 62.39) * mm, "end": v(39.98, 62.3) * mm});
            skLineSegment(sketch, "E315", {"start": v(39.42, 62.47) * mm, "end": v(39.68, 62.39) * mm});
            skLineSegment(sketch, "E316", {"start": v(39.24, 62.55) * mm, "end": v(39.42, 62.47) * mm});
            skLineSegment(sketch, "E317", {"start": v(38.83, 62.77) * mm, "end": v(39.24, 62.55) * mm});
            skArc(sketch, "E318", {"start": v(38.83, 62.77) * mm, "mid": v(38.25, 62.85) * mm, "end": v(37.78, 62.5) * mm});
            skArc(sketch, "E319", {"start": v(37.4, 61.91) * mm, "mid": v(37.6, 62.2) * mm, "end": v(37.78, 62.5) * mm});
            skArc(sketch, "E320", {"start": v(37.4, 61.91) * mm, "mid": v(37.29, 61.35) * mm, "end": v(37.6, 60.85) * mm});
            skLineSegment(sketch, "E321", {"start": v(39.37, 58.56) * mm, "end": v(39.78, 57.57) * mm});
            skLineSegment(sketch, "E322", {"start": v(38.9, 59.41) * mm, "end": v(39.37, 58.56) * mm});
            skLineSegment(sketch, "E323", {"start": v(38.7, 59.72) * mm, "end": v(38.9, 59.41) * mm});
            skLineSegment(sketch, "E324", {"start": v(38.5, 60) * mm, "end": v(38.7, 59.72) * mm});
            skLineSegment(sketch, "E325", {"start": v(38.3, 60.24) * mm, "end": v(38.5, 60) * mm});
            skLineSegment(sketch, "E326", {"start": v(38.11, 60.44) * mm, "end": v(38.3, 60.24) * mm});
            skLineSegment(sketch, "E327", {"start": v(37.97, 60.58) * mm, "end": v(38.11, 60.44) * mm});
            skLineSegment(sketch, "E328", {"start": v(37.6, 60.85) * mm, "end": v(37.97, 60.58) * mm});
            skArc(sketch, "E329", {"start": v(38.86, 56.5) * mm, "mid": v(39.33, 57.03) * mm, "end": v(39.78, 57.57) * mm});
            skLineSegment(sketch, "E330", {"start": v(37.82, 56.78) * mm, "end": v(38.86, 56.5) * mm});
            skLineSegment(sketch, "E331", {"start": v(36.92, 57.12) * mm, "end": v(37.82, 56.78) * mm});
            skLineSegment(sketch, "E332", {"start": v(36.58, 57.28) * mm, "end": v(36.92, 57.12) * mm});
            skLineSegment(sketch, "E333", {"start": v(36.27, 57.44) * mm, "end": v(36.58, 57.28) * mm});
            skLineSegment(sketch, "E334", {"start": v(36, 57.6) * mm, "end": v(36.27, 57.44) * mm});
            skLineSegment(sketch, "E335", {"start": v(35.79, 57.75) * mm, "end": v(36, 57.6) * mm});
            skLineSegment(sketch, "E336", {"start": v(35.63, 57.88) * mm, "end": v(35.79, 57.75) * mm});
            skLineSegment(sketch, "E337", {"start": v(35.3, 58.2) * mm, "end": v(35.63, 57.88) * mm});
            skArc(sketch, "E338", {"start": v(35.3, 58.2) * mm, "mid": v(34.77, 58.45) * mm, "end": v(34.23, 58.25) * mm});
            skArc(sketch, "E339", {"start": v(33.7, 57.79) * mm, "mid": v(33.96, 58.01) * mm, "end": v(34.23, 58.25) * mm});
            skArc(sketch, "E340", {"start": v(33.7, 57.79) * mm, "mid": v(33.42, 57.27) * mm, "end": v(33.58, 56.71) * mm});
            skLineSegment(sketch, "E341", {"start": v(34.63, 54.02) * mm, "end": v(34.75, 52.95) * mm});
            skLineSegment(sketch, "E342", {"start": v(34.43, 54.96) * mm, "end": v(34.63, 54.02) * mm});
            skLineSegment(sketch, "E343", {"start": v(34.32, 55.32) * mm, "end": v(34.43, 54.96) * mm});
            skLineSegment(sketch, "E344", {"start": v(34.2, 55.64) * mm, "end": v(34.32, 55.32) * mm});
            skLineSegment(sketch, "E345", {"start": v(34.08, 55.93) * mm, "end": v(34.2, 55.64) * mm});
            skLineSegment(sketch, "E346", {"start": v(33.96, 56.17) * mm, "end": v(34.08, 55.93) * mm});
            skLineSegment(sketch, "E347", {"start": v(33.86, 56.34) * mm, "end": v(33.96, 56.17) * mm});
            skLineSegment(sketch, "E348", {"start": v(33.58, 56.71) * mm, "end": v(33.86, 56.34) * mm});
            skArc(sketch, "E349", {"start": v(33.57, 52.19) * mm, "mid": v(34.17, 52.56) * mm, "end": v(34.75, 52.95) * mm});
            skLineSegment(sketch, "E350", {"start": v(32.65, 52.74) * mm, "end": v(33.57, 52.19) * mm});
            skLineSegment(sketch, "E351", {"start": v(31.88, 53.32) * mm, "end": v(32.65, 52.74) * mm});
            skLineSegment(sketch, "E352", {"start": v(31.6, 53.57) * mm, "end": v(31.88, 53.32) * mm});
            skLineSegment(sketch, "E353", {"start": v(31.35, 53.81) * mm, "end": v(31.6, 53.57) * mm});
            skLineSegment(sketch, "E354", {"start": v(31.14, 54.04) * mm, "end": v(31.35, 53.81) * mm});
            skLineSegment(sketch, "E355", {"start": v(30.97, 54.25) * mm, "end": v(31.14, 54.04) * mm});
            skLineSegment(sketch, "E356", {"start": v(30.86, 54.41) * mm, "end": v(30.97, 54.25) * mm});
            skLineSegment(sketch, "E357", {"start": v(30.64, 54.82) * mm, "end": v(30.86, 54.41) * mm});
            skArc(sketch, "E358", {"start": v(30.64, 54.82) * mm, "mid": v(30.2, 55.2) * mm, "end": v(29.61, 55.16) * mm});
            skArc(sketch, "E359", {"start": v(28.97, 54.87) * mm, "mid": v(29.3, 55.01) * mm, "end": v(29.61, 55.16) * mm});
            skArc(sketch, "E360", {"start": v(28.97, 54.87) * mm, "mid": v(28.56, 54.46) * mm, "end": v(28.56, 53.87) * mm});
            skLineSegment(sketch, "E361", {"start": v(28.81, 50.99) * mm, "end": v(28.63, 49.93) * mm});
            skLineSegment(sketch, "E362", {"start": v(28.88, 51.96) * mm, "end": v(28.81, 50.99) * mm});
            skLineSegment(sketch, "E363", {"start": v(28.88, 52.33) * mm, "end": v(28.88, 51.96) * mm});
            skLineSegment(sketch, "E364", {"start": v(28.86, 52.67) * mm, "end": v(28.88, 52.33) * mm});
            skLineSegment(sketch, "E365", {"start": v(28.82, 52.98) * mm, "end": v(28.86, 52.67) * mm});
            skLineSegment(sketch, "E366", {"start": v(28.77, 53.25) * mm, "end": v(28.82, 52.98) * mm});
            skLineSegment(sketch, "E367", {"start": v(28.72, 53.44) * mm, "end": v(28.77, 53.25) * mm});
            skLineSegment(sketch, "E368", {"start": v(28.56, 53.87) * mm, "end": v(28.72, 53.44) * mm});
            skArc(sketch, "E369", {"start": v(27.28, 49.54) * mm, "mid": v(27.95, 49.72) * mm, "end": v(28.63, 49.93) * mm});
            skLineSegment(sketch, "E370", {"start": v(26.55, 50.33) * mm, "end": v(27.28, 49.54) * mm});
            skLineSegment(sketch, "E371", {"start": v(25.97, 51.1) * mm, "end": v(26.55, 50.33) * mm});
            skLineSegment(sketch, "E372", {"start": v(25.77, 51.42) * mm, "end": v(25.97, 51.1) * mm});
            skLineSegment(sketch, "E373", {"start": v(25.6, 51.72) * mm, "end": v(25.77, 51.42) * mm});
            skLineSegment(sketch, "E374", {"start": v(25.46, 52) * mm, "end": v(25.6, 51.72) * mm});
            skLineSegment(sketch, "E375", {"start": v(25.36, 52.25) * mm, "end": v(25.46, 52) * mm});
            skLineSegment(sketch, "E376", {"start": v(25.3, 52.43) * mm, "end": v(25.36, 52.25) * mm});
            skLineSegment(sketch, "E377", {"start": v(25.2, 52.89) * mm, "end": v(25.3, 52.43) * mm});
            skArc(sketch, "E378", {"start": v(25.2, 52.89) * mm, "mid": v(24.88, 53.37) * mm, "end": v(24.32, 53.5) * mm});
            skArc(sketch, "E379", {"start": v(23.62, 53.4) * mm, "mid": v(23.97, 53.45) * mm, "end": v(24.32, 53.5) * mm});
            skArc(sketch, "E380", {"start": v(23.62, 53.4) * mm, "mid": v(23.11, 53.12) * mm, "end": v(22.94, 52.56) * mm});
            skLineSegment(sketch, "E381", {"start": v(22.37, 49.72) * mm, "end": v(21.9, 48.76) * mm});
            skLineSegment(sketch, "E382", {"start": v(22.7, 50.63) * mm, "end": v(22.37, 49.72) * mm});
            skLineSegment(sketch, "E383", {"start": v(22.81, 51) * mm, "end": v(22.7, 50.63) * mm});
            skLineSegment(sketch, "E384", {"start": v(22.89, 51.33) * mm, "end": v(22.81, 51) * mm});
            skLineSegment(sketch, "E385", {"start": v(22.94, 51.63) * mm, "end": v(22.89, 51.33) * mm});
            skLineSegment(sketch, "E386", {"start": v(22.97, 51.9) * mm, "end": v(22.94, 51.63) * mm});
            skLineSegment(sketch, "E387", {"start": v(22.98, 52.1) * mm, "end": v(22.97, 51.9) * mm});
            skLineSegment(sketch, "E388", {"start": v(22.94, 52.56) * mm, "end": v(22.98, 52.1) * mm});
            skArc(sketch, "E389", {"start": v(20.49, 48.76) * mm, "mid": v(21.2, 48.75) * mm, "end": v(21.9, 48.76) * mm});
            skLineSegment(sketch, "E390", {"start": v(20.01, 49.72) * mm, "end": v(20.49, 48.76) * mm});
            skLineSegment(sketch, "E391", {"start": v(19.68, 50.63) * mm, "end": v(20.01, 49.72) * mm});
            skLineSegment(sketch, "E392", {"start": v(19.57, 51) * mm, "end": v(19.68, 50.63) * mm});
            skLineSegment(sketch, "E393", {"start": v(19.5, 51.33) * mm, "end": v(19.57, 51) * mm});
            skLineSegment(sketch, "E394", {"start": v(19.44, 51.63) * mm, "end": v(19.5, 51.33) * mm});
            skLineSegment(sketch, "E395", {"start": v(19.42, 51.9) * mm, "end": v(19.44, 51.63) * mm});
            skLineSegment(sketch, "E396", {"start": v(19.4, 52.1) * mm, "end": v(19.42, 51.9) * mm});
            skLineSegment(sketch, "E397", {"start": v(19.44, 52.56) * mm, "end": v(19.4, 52.1) * mm});
            skArc(sketch, "E398", {"start": v(19.44, 52.56) * mm, "mid": v(19.27, 53.12) * mm, "end": v(18.77, 53.4) * mm});
            skArc(sketch, "E399", {"start": v(18.07, 53.5) * mm, "mid": v(18.42, 53.45) * mm, "end": v(18.77, 53.4) * mm});
            skArc(sketch, "E400", {"start": v(18.07, 53.5) * mm, "mid": v(17.5, 53.37) * mm, "end": v(17.18, 52.89) * mm});
            skLineSegment(sketch, "E401", {"start": v(15.84, 50.33) * mm, "end": v(15.1, 49.54) * mm});
            skLineSegment(sketch, "E402", {"start": v(16.42, 51.1) * mm, "end": v(15.84, 50.33) * mm});
            skLineSegment(sketch, "E403", {"start": v(16.61, 51.42) * mm, "end": v(16.42, 51.1) * mm});
            skLineSegment(sketch, "E404", {"start": v(16.78, 51.72) * mm, "end": v(16.61, 51.42) * mm});
            skLineSegment(sketch, "E405", {"start": v(16.92, 52) * mm, "end": v(16.78, 51.72) * mm});
            skLineSegment(sketch, "E406", {"start": v(17.02, 52.25) * mm, "end": v(16.92, 52) * mm});
            skLineSegment(sketch, "E407", {"start": v(17.09, 52.43) * mm, "end": v(17.02, 52.25) * mm});
            skLineSegment(sketch, "E408", {"start": v(17.18, 52.89) * mm, "end": v(17.09, 52.43) * mm});
            skArc(sketch, "E409", {"start": v(13.76, 49.93) * mm, "mid": v(14.43, 49.72) * mm, "end": v(15.1, 49.54) * mm});
            skLineSegment(sketch, "E410", {"start": v(13.57, 50.99) * mm, "end": v(13.76, 49.93) * mm});
            skLineSegment(sketch, "E411", {"start": v(13.5, 51.96) * mm, "end": v(13.57, 50.99) * mm});
            skLineSegment(sketch, "E412", {"start": v(13.5, 52.33) * mm, "end": v(13.5, 51.96) * mm});
            skLineSegment(sketch, "E413", {"start": v(13.53, 52.67) * mm, "end": v(13.5, 52.33) * mm});
            skLineSegment(sketch, "E414", {"start": v(13.57, 52.98) * mm, "end": v(13.53, 52.67) * mm});
            skLineSegment(sketch, "E415", {"start": v(13.61, 53.25) * mm, "end": v(13.57, 52.98) * mm});
            skLineSegment(sketch, "E416", {"start": v(13.66, 53.44) * mm, "end": v(13.61, 53.25) * mm});
            skLineSegment(sketch, "E417", {"start": v(13.83, 53.87) * mm, "end": v(13.66, 53.44) * mm});
            skArc(sketch, "E418", {"start": v(13.83, 53.87) * mm, "mid": v(13.82, 54.46) * mm, "end": v(13.41, 54.87) * mm});
            skArc(sketch, "E419", {"start": v(12.77, 55.16) * mm, "mid": v(13.1, 55.01) * mm, "end": v(13.41, 54.87) * mm});
            skArc(sketch, "E420", {"start": v(12.77, 55.16) * mm, "mid": v(12.2, 55.2) * mm, "end": v(11.75, 54.82) * mm});
            skLineSegment(sketch, "E421", {"start": v(9.74, 52.74) * mm, "end": v(8.82, 52.19) * mm});
            skLineSegment(sketch, "E422", {"start": v(10.5, 53.32) * mm, "end": v(9.74, 52.74) * mm});
            skLineSegment(sketch, "E423", {"start": v(10.79, 53.57) * mm, "end": v(10.5, 53.32) * mm});
            skLineSegment(sketch, "E424", {"start": v(11.04, 53.81) * mm, "end": v(10.79, 53.57) * mm});
            skLineSegment(sketch, "E425", {"start": v(11.25, 54.04) * mm, "end": v(11.04, 53.81) * mm});
            skLineSegment(sketch, "E426", {"start": v(11.42, 54.25) * mm, "end": v(11.25, 54.04) * mm});
            skLineSegment(sketch, "E427", {"start": v(11.53, 54.41) * mm, "end": v(11.42, 54.25) * mm});
            skLineSegment(sketch, "E428", {"start": v(11.75, 54.82) * mm, "end": v(11.53, 54.41) * mm});
            skArc(sketch, "E429", {"start": v(7.63, 52.95) * mm, "mid": v(8.22, 52.56) * mm, "end": v(8.82, 52.19) * mm});
            skLineSegment(sketch, "E430", {"start": v(7.75, 54.02) * mm, "end": v(7.63, 52.95) * mm});
            skLineSegment(sketch, "E431", {"start": v(7.96, 54.96) * mm, "end": v(7.75, 54.02) * mm});
            skLineSegment(sketch, "E432", {"start": v(8.07, 55.32) * mm, "end": v(7.96, 54.96) * mm});
            skLineSegment(sketch, "E433", {"start": v(8.18, 55.64) * mm, "end": v(8.07, 55.32) * mm});
            skLineSegment(sketch, "E434", {"start": v(8.3, 55.93) * mm, "end": v(8.18, 55.64) * mm});
            skLineSegment(sketch, "E435", {"start": v(8.42, 56.17) * mm, "end": v(8.3, 55.93) * mm});
            skLineSegment(sketch, "E436", {"start": v(8.53, 56.34) * mm, "end": v(8.42, 56.17) * mm});
            skLineSegment(sketch, "E437", {"start": v(8.8, 56.71) * mm, "end": v(8.53, 56.34) * mm});
            skArc(sketch, "E438", {"start": v(8.8, 56.71) * mm, "mid": v(8.96, 57.27) * mm, "end": v(8.7, 57.79) * mm});
            skArc(sketch, "E439", {"start": v(94.83, 23.2) * mm, "mid": v(94.03, 23.09) * mm, "end": v(93.28, 22.78) * mm});
            skArc(sketch, "E440", {"start": v(97.52, 21.64) * mm, "mid": v(97.03, 22.29) * mm, "end": v(96.38, 22.78) * mm});
            skArc(sketch, "E441", {"start": v(97.52, 18.54) * mm, "mid": v(97.83, 19.3) * mm, "end": v(97.93, 20.1) * mm});
            skArc(sketch, "E442", {"start": v(94.83, 17) * mm, "mid": v(95.64, 17.1) * mm, "end": v(96.38, 17.41) * mm});
            skArc(sketch, "E443", {"start": v(92.15, 18.54) * mm, "mid": v(92.64, 17.9) * mm, "end": v(93.28, 17.41) * mm});
            skArc(sketch, "E444", {"start": v(91.93, 20.1) * mm, "mid": v(92.03, 19.34) * mm, "end": v(92.32, 18.64) * mm});
            skArc(sketch, "E445", {"start": v(93.38, 17.58) * mm, "mid": v(94.08, 17.3) * mm, "end": v(94.83, 17.2) * mm});
            skArc(sketch, "E446", {"start": v(96.28, 17.58) * mm, "mid": v(96.88, 18.04) * mm, "end": v(97.35, 18.64) * mm});
            skArc(sketch, "E447", {"start": v(97.73, 20.1) * mm, "mid": v(97.64, 20.85) * mm, "end": v(97.35, 21.54) * mm});
            skArc(sketch, "E448", {"start": v(96.28, 22.6) * mm, "mid": v(95.58, 22.9) * mm, "end": v(94.83, 23) * mm});
            skLineSegment(sketch, "E449", {"start": v(96.28, 22.6) * mm, "end": v(96.38, 22.78) * mm});
            skLineSegment(sketch, "E450", {"start": v(97.35, 21.54) * mm, "end": v(97.52, 21.64) * mm});
            skLineSegment(sketch, "E451", {"start": v(97.73, 20.1) * mm, "end": v(97.93, 20.1) * mm});
            skLineSegment(sketch, "E452", {"start": v(97.35, 18.64) * mm, "end": v(97.52, 18.54) * mm});
            skLineSegment(sketch, "E453", {"start": v(96.28, 17.58) * mm, "end": v(96.38, 17.41) * mm});
            skLineSegment(sketch, "E454", {"start": v(94.83, 17.2) * mm, "end": v(94.83, 17) * mm});
            skLineSegment(sketch, "E455", {"start": v(93.38, 17.58) * mm, "end": v(93.28, 17.41) * mm});
            skLineSegment(sketch, "E456", {"start": v(92.32, 18.64) * mm, "end": v(92.15, 18.54) * mm});
            skLineSegment(sketch, "E457", {"start": v(91.93, 20.1) * mm, "end": v(91.73, 20.1) * mm});
            skLineSegment(sketch, "E458", {"start": v(92.32, 21.54) * mm, "end": v(92.15, 21.64) * mm});
            skLineSegment(sketch, "E459", {"start": v(93.38, 22.6) * mm, "end": v(93.28, 22.78) * mm});
            skLineSegment(sketch, "E460", {"start": v(94.83, 23) * mm, "end": v(94.83, 23.2) * mm});
            skArc(sketch, "E461", {"start": v(93.38, 22.6) * mm, "mid": v(92.78, 22.15) * mm, "end": v(92.32, 21.54) * mm});
            skArc(sketch, "E462", {"start": v(92.15, 21.64) * mm, "mid": v(91.84, 20.9) * mm, "end": v(91.73, 20.1) * mm});
            skLineSegment(sketch, "E463", {"start": v(42.34, 71.48) * mm, "end": v(42.64, 71.38) * mm});
            skCircle(sketch, "E464", {"center": v(94.83, 20.1) * mm, "radius": 6 * mm});
            skArc(sketch, "E465", {"start": v(95.62, -4.48) * mm, "mid": v(94.81, -4.58) * mm, "end": v(94.07, -4.9) * mm});
            skArc(sketch, "E466", {"start": v(98.3, -6.03) * mm, "mid": v(97.8, -5.38) * mm, "end": v(97.17, -4.9) * mm});
            skArc(sketch, "E467", {"start": v(98.3, -9.13) * mm, "mid": v(98.61, -8.38) * mm, "end": v(98.72, -7.58) * mm});
            skArc(sketch, "E468", {"start": v(95.62, -10.68) * mm, "mid": v(96.42, -10.57) * mm, "end": v(97.17, -10.26) * mm});
            skArc(sketch, "E469", {"start": v(92.93, -9.13) * mm, "mid": v(93.43, -9.77) * mm, "end": v(94.07, -10.26) * mm});
            skArc(sketch, "E470", {"start": v(92.72, -7.58) * mm, "mid": v(92.82, -8.33) * mm, "end": v(93.1, -9.03) * mm});
            skArc(sketch, "E471", {"start": v(94.17, -10.09) * mm, "mid": v(94.87, -10.38) * mm, "end": v(95.62, -10.48) * mm});
            skArc(sketch, "E472", {"start": v(97.07, -10.09) * mm, "mid": v(97.67, -9.63) * mm, "end": v(98.13, -9.03) * mm});
            skArc(sketch, "E473", {"start": v(98.52, -7.58) * mm, "mid": v(98.42, -6.83) * mm, "end": v(98.13, -6.13) * mm});
            skArc(sketch, "E474", {"start": v(97.07, -5.07) * mm, "mid": v(96.37, -4.78) * mm, "end": v(95.62, -4.68) * mm});
            skLineSegment(sketch, "E475", {"start": v(97.07, -5.07) * mm, "end": v(97.17, -4.9) * mm});
            skLineSegment(sketch, "E476", {"start": v(98.13, -6.13) * mm, "end": v(98.3, -6.03) * mm});
            skLineSegment(sketch, "E477", {"start": v(98.52, -7.58) * mm, "end": v(98.72, -7.58) * mm});
            skLineSegment(sketch, "E478", {"start": v(98.13, -9.03) * mm, "end": v(98.3, -9.13) * mm});
            skLineSegment(sketch, "E479", {"start": v(97.07, -10.09) * mm, "end": v(97.17, -10.26) * mm});
            skLineSegment(sketch, "E480", {"start": v(95.62, -10.48) * mm, "end": v(95.62, -10.68) * mm});
            skLineSegment(sketch, "E481", {"start": v(94.17, -10.09) * mm, "end": v(94.07, -10.26) * mm});
            skLineSegment(sketch, "E482", {"start": v(93.1, -9.03) * mm, "end": v(92.93, -9.13) * mm});
            skLineSegment(sketch, "E483", {"start": v(92.72, -7.58) * mm, "end": v(92.52, -7.58) * mm});
            skLineSegment(sketch, "E484", {"start": v(93.1, -6.13) * mm, "end": v(92.93, -6.03) * mm});
            skLineSegment(sketch, "E485", {"start": v(94.17, -5.07) * mm, "end": v(94.07, -4.9) * mm});
            skLineSegment(sketch, "E486", {"start": v(95.62, -4.68) * mm, "end": v(95.62, -4.48) * mm});
            skArc(sketch, "E487", {"start": v(94.17, -5.07) * mm, "mid": v(93.57, -5.53) * mm, "end": v(93.1, -6.13) * mm});
            skArc(sketch, "E488", {"start": v(92.93, -6.03) * mm, "mid": v(92.62, -6.77) * mm, "end": v(92.52, -7.58) * mm});
            skCircle(sketch, "E489", {"center": v(95.62, -7.58) * mm, "radius": 6 * mm});
            skArc(sketch, "E490", {"start": v(26.72, -64.3) * mm, "mid": v(25.01, -64.52) * mm, "end": v(23.42, -65.17) * mm});
            skArc(sketch, "E491", {"start": v(32.43, -67.6) * mm, "mid": v(31.39, -66.22) * mm, "end": v(30.02, -65.17) * mm});
            skArc(sketch, "E492", {"start": v(32.43, -74.2) * mm, "mid": v(33.1, -72.6) * mm, "end": v(33.32, -70.9) * mm});
            skArc(sketch, "E493", {"start": v(26.72, -77.5) * mm, "mid": v(28.43, -77.27) * mm, "end": v(30.02, -76.6) * mm});
            skArc(sketch, "E494", {"start": v(21, -74.2) * mm, "mid": v(22.05, -75.56) * mm, "end": v(23.42, -76.6) * mm});
            skArc(sketch, "E495", {"start": v(20.32, -70.9) * mm, "mid": v(20.54, -72.55) * mm, "end": v(21.18, -74.1) * mm});
            skArc(sketch, "E496", {"start": v(23.52, -76.43) * mm, "mid": v(25.06, -77.07) * mm, "end": v(26.72, -77.3) * mm});
            skArc(sketch, "E497", {"start": v(29.92, -76.43) * mm, "mid": v(31.24, -75.42) * mm, "end": v(32.26, -74.1) * mm});
            skArc(sketch, "E498", {"start": v(33.12, -70.9) * mm, "mid": v(32.9, -69.23) * mm, "end": v(32.26, -67.7) * mm});
            skArc(sketch, "E499", {"start": v(29.92, -65.35) * mm, "mid": v(28.37, -64.7) * mm, "end": v(26.72, -64.5) * mm});
            skLineSegment(sketch, "E500", {"start": v(29.92, -65.35) * mm, "end": v(30.02, -65.17) * mm});
            skLineSegment(sketch, "E501", {"start": v(32.26, -67.7) * mm, "end": v(32.43, -67.6) * mm});
            skLineSegment(sketch, "E502", {"start": v(33.12, -70.9) * mm, "end": v(33.32, -70.9) * mm});
            skLineSegment(sketch, "E503", {"start": v(32.26, -74.1) * mm, "end": v(32.43, -74.2) * mm});
            skLineSegment(sketch, "E504", {"start": v(29.92, -76.43) * mm, "end": v(30.02, -76.6) * mm});
            skLineSegment(sketch, "E505", {"start": v(26.72, -77.3) * mm, "end": v(26.72, -77.5) * mm});
            skLineSegment(sketch, "E506", {"start": v(23.52, -76.43) * mm, "end": v(23.42, -76.6) * mm});
            skLineSegment(sketch, "E507", {"start": v(21.18, -74.1) * mm, "end": v(21, -74.2) * mm});
            skLineSegment(sketch, "E508", {"start": v(20.32, -70.9) * mm, "end": v(20.12, -70.9) * mm});
            skLineSegment(sketch, "E509", {"start": v(21.18, -67.7) * mm, "end": v(21, -67.6) * mm});
            skLineSegment(sketch, "E510", {"start": v(23.52, -65.35) * mm, "end": v(23.42, -65.17) * mm});
            skLineSegment(sketch, "E511", {"start": v(26.72, -64.5) * mm, "end": v(26.72, -64.3) * mm});
            skArc(sketch, "E512", {"start": v(23.52, -65.35) * mm, "mid": v(22.2, -66.37) * mm, "end": v(21.18, -67.7) * mm});
            skArc(sketch, "E513", {"start": v(21, -67.6) * mm, "mid": v(20.34, -69.18) * mm, "end": v(20.12, -70.9) * mm});
            skArc(sketch, "E514", {"start": v(-75.55, -61.56) * mm, "mid": v(-77.26, -61.78) * mm, "end": v(-78.85, -62.44) * mm});
            skArc(sketch, "E515", {"start": v(-69.83, -64.86) * mm, "mid": v(-70.88, -63.5) * mm, "end": v(-72.25, -62.44) * mm});
            skArc(sketch, "E516", {"start": v(-69.83, -71.46) * mm, "mid": v(-69.17, -69.87) * mm, "end": v(-68.95, -68.16) * mm});
            skArc(sketch, "E517", {"start": v(-75.55, -74.76) * mm, "mid": v(-73.84, -74.53) * mm, "end": v(-72.25, -73.87) * mm});
            skArc(sketch, "E518", {"start": v(-81.27, -71.46) * mm, "mid": v(-80.22, -72.82) * mm, "end": v(-78.85, -73.87) * mm});
            skArc(sketch, "E519", {"start": v(-81.95, -68.16) * mm, "mid": v(-81.73, -69.81) * mm, "end": v(-81.1, -71.36) * mm});
            skArc(sketch, "E520", {"start": v(-78.75, -73.7) * mm, "mid": v(-77.2, -74.34) * mm, "end": v(-75.55, -74.56) * mm});
            skArc(sketch, "E521", {"start": v(-72.35, -73.7) * mm, "mid": v(-71.02, -72.68) * mm, "end": v(-70, -71.36) * mm});
            skArc(sketch, "E522", {"start": v(-69.15, -68.16) * mm, "mid": v(-69.37, -66.5) * mm, "end": v(-70, -64.96) * mm});
            skArc(sketch, "E523", {"start": v(-72.35, -62.62) * mm, "mid": v(-73.9, -61.98) * mm, "end": v(-75.55, -61.76) * mm});
            skLineSegment(sketch, "E524", {"start": v(-72.35, -62.62) * mm, "end": v(-72.25, -62.44) * mm});
            skLineSegment(sketch, "E525", {"start": v(-70, -64.96) * mm, "end": v(-69.83, -64.86) * mm});
            skLineSegment(sketch, "E526", {"start": v(-69.15, -68.16) * mm, "end": v(-68.95, -68.16) * mm});
            skLineSegment(sketch, "E527", {"start": v(-70, -71.36) * mm, "end": v(-69.83, -71.46) * mm});
            skLineSegment(sketch, "E528", {"start": v(-72.35, -73.7) * mm, "end": v(-72.25, -73.87) * mm});
            skLineSegment(sketch, "E529", {"start": v(-75.55, -74.56) * mm, "end": v(-75.55, -74.76) * mm});
            skLineSegment(sketch, "E530", {"start": v(-78.75, -73.7) * mm, "end": v(-78.85, -73.87) * mm});
            skLineSegment(sketch, "E531", {"start": v(-81.1, -71.36) * mm, "end": v(-81.27, -71.46) * mm});
            skLineSegment(sketch, "E532", {"start": v(-81.95, -68.16) * mm, "end": v(-82.15, -68.16) * mm});
            skLineSegment(sketch, "E533", {"start": v(-81.1, -64.96) * mm, "end": v(-81.27, -64.86) * mm});
            skLineSegment(sketch, "E534", {"start": v(-78.75, -62.62) * mm, "end": v(-78.85, -62.44) * mm});
            skLineSegment(sketch, "E535", {"start": v(-75.55, -61.76) * mm, "end": v(-75.55, -61.56) * mm});
            skArc(sketch, "E536", {"start": v(-78.75, -62.62) * mm, "mid": v(-80.08, -63.63) * mm, "end": v(-81.1, -64.96) * mm});
            skArc(sketch, "E537", {"start": v(-81.27, -64.86) * mm, "mid": v(-81.92, -66.45) * mm, "end": v(-82.15, -68.16) * mm});
            skArc(sketch, "E538", {"start": v(25.8, 2.2) * mm, "mid": v(24.99, 2.1) * mm, "end": v(24.24, 1.8) * mm});
            skArc(sketch, "E539", {"start": v(28.48, 0.66) * mm, "mid": v(27.98, 1.3) * mm, "end": v(27.34, 1.8) * mm});
            skArc(sketch, "E540", {"start": v(28.48, -2.44) * mm, "mid": v(28.79, -1.7) * mm, "end": v(28.9, -0.9) * mm});
            skArc(sketch, "E541", {"start": v(25.8, -4) * mm, "mid": v(26.6, -3.88) * mm, "end": v(27.34, -3.58) * mm});
            skArc(sketch, "E542", {"start": v(23.1, -2.44) * mm, "mid": v(23.6, -3.08) * mm, "end": v(24.24, -3.58) * mm});
            skArc(sketch, "E543", {"start": v(22.9, -0.9) * mm, "mid": v(23, -1.64) * mm, "end": v(23.28, -2.34) * mm});
            skArc(sketch, "E544", {"start": v(24.34, -3.4) * mm, "mid": v(25.04, -3.7) * mm, "end": v(25.8, -3.8) * mm});
            skArc(sketch, "E545", {"start": v(27.24, -3.4) * mm, "mid": v(27.84, -2.94) * mm, "end": v(28.3, -2.34) * mm});
            skArc(sketch, "E546", {"start": v(28.7, -0.9) * mm, "mid": v(28.6, -0.14) * mm, "end": v(28.3, 0.56) * mm});
            skArc(sketch, "E547", {"start": v(27.24, 1.62) * mm, "mid": v(26.54, 1.91) * mm, "end": v(25.8, 2) * mm});
            skLineSegment(sketch, "E548", {"start": v(27.24, 1.62) * mm, "end": v(27.34, 1.8) * mm});
            skLineSegment(sketch, "E549", {"start": v(28.3, 0.56) * mm, "end": v(28.48, 0.66) * mm});
            skLineSegment(sketch, "E550", {"start": v(28.7, -0.9) * mm, "end": v(28.9, -0.9) * mm});
            skLineSegment(sketch, "E551", {"start": v(28.3, -2.34) * mm, "end": v(28.48, -2.44) * mm});
            skLineSegment(sketch, "E552", {"start": v(27.24, -3.4) * mm, "end": v(27.34, -3.58) * mm});
            skLineSegment(sketch, "E553", {"start": v(25.8, -3.8) * mm, "end": v(25.8, -4) * mm});
            skLineSegment(sketch, "E554", {"start": v(24.34, -3.4) * mm, "end": v(24.24, -3.58) * mm});
            skLineSegment(sketch, "E555", {"start": v(23.28, -2.34) * mm, "end": v(23.1, -2.44) * mm});
            skLineSegment(sketch, "E556", {"start": v(22.9, -0.9) * mm, "end": v(22.7, -0.9) * mm});
            skLineSegment(sketch, "E557", {"start": v(23.28, 0.56) * mm, "end": v(23.1, 0.66) * mm});
            skLineSegment(sketch, "E558", {"start": v(24.34, 1.62) * mm, "end": v(24.24, 1.8) * mm});
            skLineSegment(sketch, "E559", {"start": v(25.8, 2) * mm, "end": v(25.8, 2.2) * mm});
            skArc(sketch, "E560", {"start": v(24.34, 1.62) * mm, "mid": v(23.74, 1.16) * mm, "end": v(23.28, 0.56) * mm});
            skArc(sketch, "E561", {"start": v(23.1, 0.66) * mm, "mid": v(22.8, -0.09) * mm, "end": v(22.7, -0.9) * mm});
            skArc(sketch, "E562", {"start": v(-76.48, 8.44) * mm, "mid": v(-78.18, 8.22) * mm, "end": v(-79.78, 7.56) * mm});
            skArc(sketch, "E563", {"start": v(-70.76, 5.14) * mm, "mid": v(-71.8, 6.5) * mm, "end": v(-73.18, 7.56) * mm});
            skArc(sketch, "E564", {"start": v(-70.76, -1.46) * mm, "mid": v(-70.1, 0.13) * mm, "end": v(-69.88, 1.84) * mm});
            skArc(sketch, "E565", {"start": v(-76.48, -4.76) * mm, "mid": v(-74.77, -4.53) * mm, "end": v(-73.18, -3.87) * mm});
            skArc(sketch, "E566", {"start": v(-82.2, -1.46) * mm, "mid": v(-81.14, -2.82) * mm, "end": v(-79.78, -3.87) * mm});
            skArc(sketch, "E567", {"start": v(-82.88, 1.84) * mm, "mid": v(-82.66, 0.19) * mm, "end": v(-82.02, -1.36) * mm});
            skArc(sketch, "E568", {"start": v(-79.68, -3.7) * mm, "mid": v(-78.13, -4.34) * mm, "end": v(-76.48, -4.56) * mm});
            skArc(sketch, "E569", {"start": v(-73.28, -3.7) * mm, "mid": v(-71.95, -2.68) * mm, "end": v(-70.93, -1.36) * mm});
            skArc(sketch, "E570", {"start": v(-70.08, 1.84) * mm, "mid": v(-70.3, 3.5) * mm, "end": v(-70.93, 5.04) * mm});
            skArc(sketch, "E571", {"start": v(-73.28, 7.38) * mm, "mid": v(-74.82, 8.02) * mm, "end": v(-76.48, 8.24) * mm});
            skLineSegment(sketch, "E572", {"start": v(-73.28, 7.38) * mm, "end": v(-73.18, 7.56) * mm});
            skLineSegment(sketch, "E573", {"start": v(-70.93, 5.04) * mm, "end": v(-70.76, 5.14) * mm});
            skLineSegment(sketch, "E574", {"start": v(-70.08, 1.84) * mm, "end": v(-69.88, 1.84) * mm});
            skCircle(sketch, "E575", {"center": v(21.2, 72.75) * mm, "radius": 3.1 * mm});
            skLineSegment(sketch, "E576", {"start": v(-70.93, -1.36) * mm, "end": v(-70.76, -1.46) * mm});
            skLineSegment(sketch, "E577", {"start": v(-73.28, -3.7) * mm, "end": v(-73.18, -3.87) * mm});
            skLineSegment(sketch, "E578", {"start": v(-76.48, -4.56) * mm, "end": v(-76.48, -4.76) * mm});
            skLineSegment(sketch, "E579", {"start": v(-79.68, -3.7) * mm, "end": v(-79.78, -3.87) * mm});
            skLineSegment(sketch, "E580", {"start": v(-82.02, -1.36) * mm, "end": v(-82.2, -1.46) * mm});
            skLineSegment(sketch, "E581", {"start": v(-82.88, 1.84) * mm, "end": v(-83.08, 1.84) * mm});
            skLineSegment(sketch, "E582", {"start": v(-82.02, 5.04) * mm, "end": v(-82.2, 5.14) * mm});
            skLineSegment(sketch, "E583", {"start": v(-79.68, 7.38) * mm, "end": v(-79.78, 7.56) * mm});
            skLineSegment(sketch, "E584", {"start": v(-76.48, 8.24) * mm, "end": v(-76.48, 8.44) * mm});
            skArc(sketch, "E585", {"start": v(-79.68, 7.38) * mm, "mid": v(-81, 6.37) * mm, "end": v(-82.02, 5.04) * mm});
            skArc(sketch, "E586", {"start": v(-82.2, 5.14) * mm, "mid": v(-82.85, 3.55) * mm, "end": v(-83.08, 1.84) * mm});
            skArc(sketch, "E587", {"start": v(-77.77, 76.9) * mm, "mid": v(-79.48, 76.67) * mm, "end": v(-81.07, 76) * mm});
            skArc(sketch, "E588", {"start": v(-72.06, 73.6) * mm, "mid": v(-73.1, 74.96) * mm, "end": v(-74.47, 76) * mm});
            skArc(sketch, "E589", {"start": v(-72.06, 67) * mm, "mid": v(-71.4, 68.58) * mm, "end": v(-71.17, 70.3) * mm});
            skArc(sketch, "E590", {"start": v(-77.77, 63.7) * mm, "mid": v(-76.06, 63.92) * mm, "end": v(-74.47, 64.58) * mm});
            skArc(sketch, "E591", {"start": v(-83.49, 67) * mm, "mid": v(-82.44, 65.63) * mm, "end": v(-81.07, 64.58) * mm});
            skArc(sketch, "E592", {"start": v(-84.17, 70.3) * mm, "mid": v(-83.95, 68.64) * mm, "end": v(-83.31, 67.1) * mm});
            skArc(sketch, "E593", {"start": v(-80.97, 64.75) * mm, "mid": v(-79.43, 64.11) * mm, "end": v(-77.77, 63.9) * mm});
            skArc(sketch, "E594", {"start": v(-74.57, 64.75) * mm, "mid": v(-73.25, 65.77) * mm, "end": v(-72.23, 67.1) * mm});
            skArc(sketch, "E595", {"start": v(-71.37, 70.3) * mm, "mid": v(-71.59, 71.95) * mm, "end": v(-72.23, 73.5) * mm});
            skArc(sketch, "E596", {"start": v(-74.57, 75.83) * mm, "mid": v(-76.11, 76.47) * mm, "end": v(-77.77, 76.7) * mm});
            skLineSegment(sketch, "E597", {"start": v(-74.57, 75.83) * mm, "end": v(-74.47, 76) * mm});
            skLineSegment(sketch, "E598", {"start": v(-72.23, 73.5) * mm, "end": v(-72.06, 73.6) * mm});
            skLineSegment(sketch, "E599", {"start": v(-71.37, 70.3) * mm, "end": v(-71.17, 70.3) * mm});
            skLineSegment(sketch, "E600", {"start": v(-72.23, 67.1) * mm, "end": v(-72.06, 67) * mm});
            skLineSegment(sketch, "E601", {"start": v(-74.57, 64.75) * mm, "end": v(-74.47, 64.58) * mm});
            skLineSegment(sketch, "E602", {"start": v(-77.77, 63.9) * mm, "end": v(-77.77, 63.7) * mm});
            skLineSegment(sketch, "E603", {"start": v(-80.97, 64.75) * mm, "end": v(-81.07, 64.58) * mm});
            skLineSegment(sketch, "E604", {"start": v(-83.31, 67.1) * mm, "end": v(-83.49, 67) * mm});
            skLineSegment(sketch, "E605", {"start": v(-84.17, 70.3) * mm, "end": v(-84.37, 70.3) * mm});
            skLineSegment(sketch, "E606", {"start": v(-83.31, 73.5) * mm, "end": v(-83.49, 73.6) * mm});
            skLineSegment(sketch, "E607", {"start": v(-80.97, 75.83) * mm, "end": v(-81.07, 76) * mm});
            skLineSegment(sketch, "E608", {"start": v(-77.77, 76.7) * mm, "end": v(-77.77, 76.9) * mm});
            skArc(sketch, "E609", {"start": v(-80.97, 75.83) * mm, "mid": v(-82.3, 74.82) * mm, "end": v(-83.31, 73.5) * mm});
            skArc(sketch, "E610", {"start": v(-83.49, 73.6) * mm, "mid": v(-84.15, 72) * mm, "end": v(-84.37, 70.3) * mm});
            skArc(sketch, "E611", {"start": v(5.86, -76.12) * mm, "mid": v(5.95, -76.46) * mm, "end": v(6.04, -76.79) * mm});
            skArc(sketch, "E612", {"start": v(5.86, -76.12) * mm, "mid": v(5.53, -75.66) * mm, "end": v(4.96, -75.56) * mm});
            skLineSegment(sketch, "E613", {"start": v(2.08, -75.33) * mm, "end": v(1.04, -75) * mm});
            skLineSegment(sketch, "E614", {"start": v(3.04, -75.55) * mm, "end": v(2.08, -75.33) * mm});
            skLineSegment(sketch, "E615", {"start": v(3.5, -75.61) * mm, "end": v(3.04, -75.55) * mm});
            skLineSegment(sketch, "E616", {"start": v(3.9, -75.65) * mm, "end": v(3.5, -75.61) * mm});
            skLineSegment(sketch, "E617", {"start": v(4.27, -75.65) * mm, "end": v(3.9, -75.65) * mm});
            skLineSegment(sketch, "E618", {"start": v(4.56, -75.64) * mm, "end": v(4.27, -75.65) * mm});
            skLineSegment(sketch, "E619", {"start": v(4.96, -75.56) * mm, "end": v(4.56, -75.64) * mm});
            skArc(sketch, "E620", {"start": v(0.86, -73.58) * mm, "mid": v(0.94, -74.28) * mm, "end": v(1.04, -75) * mm});
            skLineSegment(sketch, "E621", {"start": v(1.77, -72.98) * mm, "end": v(0.86, -73.58) * mm});
            skLineSegment(sketch, "E622", {"start": v(2.64, -72.52) * mm, "end": v(1.77, -72.98) * mm});
            skLineSegment(sketch, "E623", {"start": v(3.06, -72.34) * mm, "end": v(2.64, -72.52) * mm});
            skLineSegment(sketch, "E624", {"start": v(3.45, -72.2) * mm, "end": v(3.06, -72.34) * mm});
            skLineSegment(sketch, "E625", {"start": v(3.8, -72.1) * mm, "end": v(3.45, -72.2) * mm});
            skLineSegment(sketch, "E626", {"start": v(4.08, -72.04) * mm, "end": v(3.8, -72.1) * mm});
            skLineSegment(sketch, "E627", {"start": v(4.5, -72.01) * mm, "end": v(4.08, -72.04) * mm});
            skArc(sketch, "E628", {"start": v(4.5, -72.01) * mm, "mid": v(5.02, -71.77) * mm, "end": v(5.22, -71.24) * mm});
            skArc(sketch, "E629", {"start": v(5.22, -70.54) * mm, "mid": v(5.22, -70.9) * mm, "end": v(5.22, -71.24) * mm});
            skArc(sketch, "E630", {"start": v(5.22, -70.54) * mm, "mid": v(5.02, -70) * mm, "end": v(4.5, -69.77) * mm});
            skLineSegment(sketch, "E631", {"start": v(1.77, -68.8) * mm, "end": v(0.86, -68.2) * mm});
            skLineSegment(sketch, "E632", {"start": v(2.64, -69.26) * mm, "end": v(1.77, -68.8) * mm});
            skLineSegment(sketch, "E633", {"start": v(3.06, -69.44) * mm, "end": v(2.64, -69.26) * mm});
            skLineSegment(sketch, "E634", {"start": v(3.45, -69.58) * mm, "end": v(3.06, -69.44) * mm});
            skLineSegment(sketch, "E635", {"start": v(3.8, -69.68) * mm, "end": v(3.45, -69.58) * mm});
            skLineSegment(sketch, "E636", {"start": v(4.08, -69.74) * mm, "end": v(3.8, -69.68) * mm});
            skLineSegment(sketch, "E637", {"start": v(4.5, -69.77) * mm, "end": v(4.08, -69.74) * mm});
            skArc(sketch, "E638", {"start": v(1.04, -66.8) * mm, "mid": v(0.94, -67.5) * mm, "end": v(0.86, -68.2) * mm});
            skLineSegment(sketch, "E639", {"start": v(2.08, -66.45) * mm, "end": v(1.04, -66.8) * mm});
            skLineSegment(sketch, "E640", {"start": v(3.04, -66.23) * mm, "end": v(2.08, -66.45) * mm});
            skLineSegment(sketch, "E641", {"start": v(3.5, -66.17) * mm, "end": v(3.04, -66.23) * mm});
            skLineSegment(sketch, "E642", {"start": v(3.9, -66.13) * mm, "end": v(3.5, -66.17) * mm});
            skLineSegment(sketch, "E643", {"start": v(4.27, -66.13) * mm, "end": v(3.9, -66.13) * mm});
            skLineSegment(sketch, "E644", {"start": v(4.56, -66.15) * mm, "end": v(4.27, -66.13) * mm});
            skLineSegment(sketch, "E645", {"start": v(4.96, -66.22) * mm, "end": v(4.56, -66.15) * mm});
            skArc(sketch, "E646", {"start": v(4.96, -66.22) * mm, "mid": v(5.53, -66.12) * mm, "end": v(5.86, -65.66) * mm});
            skArc(sketch, "E647", {"start": v(6.04, -65) * mm, "mid": v(5.95, -65.33) * mm, "end": v(5.86, -65.66) * mm});
            skArc(sketch, "E648", {"start": v(6.04, -65) * mm, "mid": v(5.98, -64.42) * mm, "end": v(5.54, -64.06) * mm});
            skLineSegment(sketch, "E649", {"start": v(3.16, -62.42) * mm, "end": v(2.43, -61.6) * mm});
            skLineSegment(sketch, "E650", {"start": v(3.89, -63.09) * mm, "end": v(3.16, -62.42) * mm});
            skLineSegment(sketch, "E651", {"start": v(4.24, -63.37) * mm, "end": v(3.89, -63.09) * mm});
            skLineSegment(sketch, "E652", {"start": v(4.58, -63.6) * mm, "end": v(4.24, -63.37) * mm});
            skLineSegment(sketch, "E653", {"start": v(4.9, -63.79) * mm, "end": v(4.58, -63.6) * mm});
            skLineSegment(sketch, "E654", {"start": v(5.15, -63.92) * mm, "end": v(4.9, -63.79) * mm});
            skLineSegment(sketch, "E655", {"start": v(5.54, -64.06) * mm, "end": v(5.15, -63.92) * mm});
            skArc(sketch, "E656", {"start": v(2.98, -60.29) * mm, "mid": v(2.7, -60.94) * mm, "end": v(2.43, -61.6) * mm});
            skLineSegment(sketch, "E657", {"start": v(4.07, -60.22) * mm, "end": v(2.98, -60.29) * mm});
            skLineSegment(sketch, "E658", {"start": v(5.06, -60.26) * mm, "end": v(4.07, -60.22) * mm});
            skLineSegment(sketch, "E659", {"start": v(5.5, -60.32) * mm, "end": v(5.06, -60.26) * mm});
            skLineSegment(sketch, "E660", {"start": v(5.91, -60.4) * mm, "end": v(5.5, -60.32) * mm});
            skLineSegment(sketch, "E661", {"start": v(6.26, -60.48) * mm, "end": v(5.91, -60.4) * mm});
            skLineSegment(sketch, "E662", {"start": v(6.54, -60.57) * mm, "end": v(6.26, -60.48) * mm});
            skLineSegment(sketch, "E663", {"start": v(6.91, -60.75) * mm, "end": v(6.54, -60.57) * mm});
            skArc(sketch, "E664", {"start": v(6.91, -60.75) * mm, "mid": v(7.48, -60.8) * mm, "end": v(7.93, -60.44) * mm});
            skArc(sketch, "E665", {"start": v(8.27, -59.84) * mm, "mid": v(8.1, -60.14) * mm, "end": v(7.93, -60.44) * mm});
            skArc(sketch, "E666", {"start": v(8.27, -59.84) * mm, "mid": v(8.36, -59.28) * mm, "end": v(8.03, -58.8) * mm});
            skLineSegment(sketch, "E667", {"start": v(6.16, -56.61) * mm, "end": v(5.66, -55.63) * mm});
            skLineSegment(sketch, "E668", {"start": v(6.68, -57.45) * mm, "end": v(6.16, -56.61) * mm});
            skLineSegment(sketch, "E669", {"start": v(6.96, -57.8) * mm, "end": v(6.68, -57.45) * mm});
            skLineSegment(sketch, "E670", {"start": v(7.22, -58.12) * mm, "end": v(6.96, -57.8) * mm});
            skLineSegment(sketch, "E671", {"start": v(7.47, -58.38) * mm, "end": v(7.22, -58.12) * mm});
            skLineSegment(sketch, "E672", {"start": v(7.7, -58.58) * mm, "end": v(7.47, -58.38) * mm});
            skLineSegment(sketch, "E673", {"start": v(8.03, -58.8) * mm, "end": v(7.7, -58.58) * mm});
            skArc(sketch, "E674", {"start": v(6.53, -54.5) * mm, "mid": v(6.1, -55.06) * mm, "end": v(5.66, -55.63) * mm});
            skLineSegment(sketch, "E675", {"start": v(7.6, -54.72) * mm, "end": v(6.53, -54.5) * mm});
            skLineSegment(sketch, "E676", {"start": v(8.55, -55.02) * mm, "end": v(7.6, -54.72) * mm});
            skLineSegment(sketch, "E677", {"start": v(8.97, -55.19) * mm, "end": v(8.55, -55.02) * mm});
            skLineSegment(sketch, "E678", {"start": v(9.34, -55.36) * mm, "end": v(8.97, -55.19) * mm});
            skLineSegment(sketch, "E679", {"start": v(9.66, -55.54) * mm, "end": v(9.34, -55.36) * mm});
            skLineSegment(sketch, "E680", {"start": v(9.9, -55.7) * mm, "end": v(9.66, -55.54) * mm});
            skLineSegment(sketch, "E681", {"start": v(10.21, -55.97) * mm, "end": v(9.9, -55.7) * mm});
            skArc(sketch, "E682", {"start": v(10.21, -55.97) * mm, "mid": v(10.75, -56.17) * mm, "end": v(11.27, -55.93) * mm});
            skArc(sketch, "E683", {"start": v(11.76, -55.44) * mm, "mid": v(11.52, -55.69) * mm, "end": v(11.27, -55.93) * mm});
            skArc(sketch, "E684", {"start": v(11.76, -55.44) * mm, "mid": v(12, -54.92) * mm, "end": v(11.8, -54.38) * mm});
            skLineSegment(sketch, "E685", {"start": v(10.55, -51.78) * mm, "end": v(10.33, -50.7) * mm});
            skLineSegment(sketch, "E686", {"start": v(10.85, -52.72) * mm, "end": v(10.55, -51.78) * mm});
            skLineSegment(sketch, "E687", {"start": v(11.01, -53.14) * mm, "end": v(10.85, -52.72) * mm});
            skLineSegment(sketch, "E688", {"start": v(11.2, -53.51) * mm, "end": v(11.01, -53.14) * mm});
            skLineSegment(sketch, "E689", {"start": v(11.37, -53.83) * mm, "end": v(11.2, -53.51) * mm});
            skLineSegment(sketch, "E690", {"start": v(11.53, -54.07) * mm, "end": v(11.37, -53.83) * mm});
            skLineSegment(sketch, "E691", {"start": v(11.8, -54.38) * mm, "end": v(11.53, -54.07) * mm});
            skArc(sketch, "E692", {"start": v(11.46, -49.84) * mm, "mid": v(10.9, -50.26) * mm, "end": v(10.33, -50.7) * mm});
            skLineSegment(sketch, "E693", {"start": v(12.44, -50.33) * mm, "end": v(11.46, -49.84) * mm});
            skLineSegment(sketch, "E694", {"start": v(13.27, -50.85) * mm, "end": v(12.44, -50.33) * mm});
            skLineSegment(sketch, "E695", {"start": v(13.64, -51.13) * mm, "end": v(13.27, -50.85) * mm});
            skLineSegment(sketch, "E696", {"start": v(13.95, -51.4) * mm, "end": v(13.64, -51.13) * mm});
            skLineSegment(sketch, "E697", {"start": v(14.21, -51.65) * mm, "end": v(13.95, -51.4) * mm});
            skLineSegment(sketch, "E698", {"start": v(14.4, -51.87) * mm, "end": v(14.21, -51.65) * mm});
            skLineSegment(sketch, "E699", {"start": v(14.64, -52.2) * mm, "end": v(14.4, -51.87) * mm});
            skArc(sketch, "E700", {"start": v(14.64, -52.2) * mm, "mid": v(15.1, -52.54) * mm, "end": v(15.67, -52.45) * mm});
            skArc(sketch, "E701", {"start": v(16.27, -52.1) * mm, "mid": v(15.97, -52.27) * mm, "end": v(15.67, -52.45) * mm});
            skArc(sketch, "E702", {"start": v(16.27, -52.1) * mm, "mid": v(16.63, -51.65) * mm, "end": v(16.58, -51.09) * mm});
            skLineSegment(sketch, "E703", {"start": v(16.05, -48.24) * mm, "end": v(16.11, -47.15) * mm});
            skLineSegment(sketch, "E704", {"start": v(16.09, -49.23) * mm, "end": v(16.05, -48.24) * mm});
            skLineSegment(sketch, "E705", {"start": v(16.14, -49.68) * mm, "end": v(16.09, -49.23) * mm});
            skLineSegment(sketch, "E706", {"start": v(16.22, -50.09) * mm, "end": v(16.14, -49.68) * mm});
            skLineSegment(sketch, "E707", {"start": v(16.3, -50.44) * mm, "end": v(16.22, -50.09) * mm});
            skLineSegment(sketch, "E708", {"start": v(16.4, -50.71) * mm, "end": v(16.3, -50.44) * mm});
            skLineSegment(sketch, "E709", {"start": v(16.58, -51.09) * mm, "end": v(16.4, -50.71) * mm});
            skArc(sketch, "E710", {"start": v(17.43, -46.6) * mm, "mid": v(16.77, -46.87) * mm, "end": v(16.11, -47.15) * mm});
            skLineSegment(sketch, "E711", {"start": v(18.25, -47.33) * mm, "end": v(17.43, -46.6) * mm});
            skLineSegment(sketch, "E712", {"start": v(18.92, -48.06) * mm, "end": v(18.25, -47.33) * mm});
            skLineSegment(sketch, "E713", {"start": v(19.2, -48.41) * mm, "end": v(18.92, -48.06) * mm});
            skLineSegment(sketch, "E714", {"start": v(19.43, -48.75) * mm, "end": v(19.2, -48.41) * mm});
            skLineSegment(sketch, "E715", {"start": v(19.62, -49.07) * mm, "end": v(19.43, -48.75) * mm});
            skLineSegment(sketch, "E716", {"start": v(19.75, -49.33) * mm, "end": v(19.62, -49.07) * mm});
            skLineSegment(sketch, "E717", {"start": v(19.88, -49.72) * mm, "end": v(19.75, -49.33) * mm});
            skArc(sketch, "E718", {"start": v(19.88, -49.72) * mm, "mid": v(20.25, -50.16) * mm, "end": v(20.82, -50.22) * mm});
            skArc(sketch, "E719", {"start": v(21.49, -50.04) * mm, "mid": v(21.15, -50.12) * mm, "end": v(20.82, -50.22) * mm});
            skArc(sketch, "E720", {"start": v(21.49, -50.04) * mm, "mid": v(21.95, -49.7) * mm, "end": v(22.05, -49.14) * mm});
            skLineSegment(sketch, "E721", {"start": v(22.28, -46.25) * mm, "end": v(22.62, -45.22) * mm});
            skLineSegment(sketch, "E722", {"start": v(22.06, -47.22) * mm, "end": v(22.28, -46.25) * mm});
            skLineSegment(sketch, "E723", {"start": v(22, -47.67) * mm, "end": v(22.06, -47.22) * mm});
            skLineSegment(sketch, "E724", {"start": v(21.96, -48.08) * mm, "end": v(22, -47.67) * mm});
            skLineSegment(sketch, "E725", {"start": v(21.95, -48.44) * mm, "end": v(21.96, -48.08) * mm});
            skLineSegment(sketch, "E726", {"start": v(21.97, -48.73) * mm, "end": v(21.95, -48.44) * mm});
            skLineSegment(sketch, "E727", {"start": v(22.05, -49.14) * mm, "end": v(21.97, -48.73) * mm});
            skArc(sketch, "E728", {"start": v(24.03, -45.03) * mm, "mid": v(23.32, -45.11) * mm, "end": v(22.62, -45.22) * mm});
            skLineSegment(sketch, "E729", {"start": v(24.63, -45.94) * mm, "end": v(24.03, -45.03) * mm});
            skLineSegment(sketch, "E730", {"start": v(25.1, -46.82) * mm, "end": v(24.63, -45.94) * mm});
            skLineSegment(sketch, "E731", {"start": v(25.27, -47.23) * mm, "end": v(25.1, -46.82) * mm});
            skLineSegment(sketch, "E732", {"start": v(25.4, -47.62) * mm, "end": v(25.27, -47.23) * mm});
            skLineSegment(sketch, "E733", {"start": v(25.5, -47.97) * mm, "end": v(25.4, -47.62) * mm});
            skLineSegment(sketch, "E734", {"start": v(25.57, -48.26) * mm, "end": v(25.5, -47.97) * mm});
            skLineSegment(sketch, "E735", {"start": v(25.6, -48.67) * mm, "end": v(25.57, -48.26) * mm});
            skArc(sketch, "E736", {"start": v(25.6, -48.67) * mm, "mid": v(25.84, -49.19) * mm, "end": v(26.37, -49.4) * mm});
            skArc(sketch, "E737", {"start": v(27.07, -49.4) * mm, "mid": v(26.72, -49.4) * mm, "end": v(26.37, -49.4) * mm});
            skArc(sketch, "E738", {"start": v(27.07, -49.4) * mm, "mid": v(27.6, -49.19) * mm, "end": v(27.84, -48.67) * mm});
            skLineSegment(sketch, "E739", {"start": v(28.8, -45.94) * mm, "end": v(29.4, -45.03) * mm});
            skLineSegment(sketch, "E740", {"start": v(28.34, -46.82) * mm, "end": v(28.8, -45.94) * mm});
            skLineSegment(sketch, "E741", {"start": v(28.17, -47.23) * mm, "end": v(28.34, -46.82) * mm});
            skLineSegment(sketch, "E742", {"start": v(28.03, -47.62) * mm, "end": v(28.17, -47.23) * mm});
            skLineSegment(sketch, "E743", {"start": v(27.93, -47.97) * mm, "end": v(28.03, -47.62) * mm});
            skLineSegment(sketch, "E744", {"start": v(27.87, -48.26) * mm, "end": v(27.93, -47.97) * mm});
            skLineSegment(sketch, "E745", {"start": v(27.84, -48.67) * mm, "end": v(27.87, -48.26) * mm});
            skArc(sketch, "E746", {"start": v(30.82, -45.22) * mm, "mid": v(30.11, -45.11) * mm, "end": v(29.4, -45.03) * mm});
            skLineSegment(sketch, "E747", {"start": v(31.16, -46.25) * mm, "end": v(30.82, -45.22) * mm});
            skLineSegment(sketch, "E748", {"start": v(31.38, -47.22) * mm, "end": v(31.16, -46.25) * mm});
            skLineSegment(sketch, "E749", {"start": v(31.44, -47.67) * mm, "end": v(31.38, -47.22) * mm});
            skLineSegment(sketch, "E750", {"start": v(31.48, -48.08) * mm, "end": v(31.44, -47.67) * mm});
            skLineSegment(sketch, "E751", {"start": v(31.48, -48.44) * mm, "end": v(31.48, -48.08) * mm});
            skLineSegment(sketch, "E752", {"start": v(31.46, -48.73) * mm, "end": v(31.48, -48.44) * mm});
            skLineSegment(sketch, "E753", {"start": v(31.39, -49.14) * mm, "end": v(31.46, -48.73) * mm});
            skArc(sketch, "E754", {"start": v(31.39, -49.14) * mm, "mid": v(31.48, -49.7) * mm, "end": v(31.95, -50.04) * mm});
            skArc(sketch, "E755", {"start": v(32.62, -50.22) * mm, "mid": v(32.28, -50.12) * mm, "end": v(31.95, -50.04) * mm});
            skArc(sketch, "E756", {"start": v(32.62, -50.22) * mm, "mid": v(33.19, -50.16) * mm, "end": v(33.55, -49.72) * mm});
            skLineSegment(sketch, "E757", {"start": v(35.19, -47.33) * mm, "end": v(36, -46.6) * mm});
            skLineSegment(sketch, "E758", {"start": v(34.52, -48.06) * mm, "end": v(35.19, -47.33) * mm});
            skLineSegment(sketch, "E759", {"start": v(34.24, -48.41) * mm, "end": v(34.52, -48.06) * mm});
            skLineSegment(sketch, "E760", {"start": v(34, -48.75) * mm, "end": v(34.24, -48.41) * mm});
            skLineSegment(sketch, "E761", {"start": v(33.82, -49.07) * mm, "end": v(34, -48.75) * mm});
            skLineSegment(sketch, "E762", {"start": v(33.69, -49.33) * mm, "end": v(33.82, -49.07) * mm});
            skLineSegment(sketch, "E763", {"start": v(33.55, -49.72) * mm, "end": v(33.69, -49.33) * mm});
            skArc(sketch, "E764", {"start": v(37.32, -47.15) * mm, "mid": v(36.67, -46.87) * mm, "end": v(36, -46.6) * mm});
            skLineSegment(sketch, "E765", {"start": v(37.39, -48.24) * mm, "end": v(37.32, -47.15) * mm});
            skLineSegment(sketch, "E766", {"start": v(37.35, -49.23) * mm, "end": v(37.39, -48.24) * mm});
            skLineSegment(sketch, "E767", {"start": v(37.3, -49.68) * mm, "end": v(37.35, -49.23) * mm});
            skLineSegment(sketch, "E768", {"start": v(37.22, -50.09) * mm, "end": v(37.3, -49.68) * mm});
            skLineSegment(sketch, "E769", {"start": v(37.13, -50.44) * mm, "end": v(37.22, -50.09) * mm});
            skLineSegment(sketch, "E770", {"start": v(37.04, -50.71) * mm, "end": v(37.13, -50.44) * mm});
            skLineSegment(sketch, "E771", {"start": v(36.86, -51.09) * mm, "end": v(37.04, -50.71) * mm});
            skArc(sketch, "E772", {"start": v(36.86, -51.09) * mm, "mid": v(36.8, -51.65) * mm, "end": v(37.17, -52.1) * mm});
            skArc(sketch, "E773", {"start": v(37.77, -52.45) * mm, "mid": v(37.47, -52.27) * mm, "end": v(37.17, -52.1) * mm});
            skArc(sketch, "E774", {"start": v(37.77, -52.45) * mm, "mid": v(38.33, -52.54) * mm, "end": v(38.8, -52.2) * mm});
            skLineSegment(sketch, "E775", {"start": v(41, -50.33) * mm, "end": v(41.97, -49.84) * mm});
            skLineSegment(sketch, "E776", {"start": v(40.16, -50.85) * mm, "end": v(41, -50.33) * mm});
            skLineSegment(sketch, "E777", {"start": v(39.8, -51.13) * mm, "end": v(40.16, -50.85) * mm});
            skLineSegment(sketch, "E778", {"start": v(39.49, -51.4) * mm, "end": v(39.8, -51.13) * mm});
            skLineSegment(sketch, "E779", {"start": v(39.23, -51.65) * mm, "end": v(39.49, -51.4) * mm});
            skLineSegment(sketch, "E780", {"start": v(39.03, -51.87) * mm, "end": v(39.23, -51.65) * mm});
            skLineSegment(sketch, "E781", {"start": v(38.8, -52.2) * mm, "end": v(39.03, -51.87) * mm});
            skArc(sketch, "E782", {"start": v(43.1, -50.7) * mm, "mid": v(42.55, -50.26) * mm, "end": v(41.97, -49.84) * mm});
            skLineSegment(sketch, "E783", {"start": v(42.88, -51.78) * mm, "end": v(43.1, -50.7) * mm});
            skLineSegment(sketch, "E784", {"start": v(42.6, -52.72) * mm, "end": v(42.88, -51.78) * mm});
            skLineSegment(sketch, "E785", {"start": v(42.42, -53.14) * mm, "end": v(42.6, -52.72) * mm});
            skLineSegment(sketch, "E786", {"start": v(42.25, -53.51) * mm, "end": v(42.42, -53.14) * mm});
            skLineSegment(sketch, "E787", {"start": v(42.07, -53.83) * mm, "end": v(42.25, -53.51) * mm});
            skLineSegment(sketch, "E788", {"start": v(41.9, -54.07) * mm, "end": v(42.07, -53.83) * mm});
            skLineSegment(sketch, "E789", {"start": v(41.64, -54.38) * mm, "end": v(41.9, -54.07) * mm});
            skArc(sketch, "E790", {"start": v(41.64, -54.38) * mm, "mid": v(41.44, -54.92) * mm, "end": v(41.67, -55.44) * mm});
            skArc(sketch, "E791", {"start": v(42.16, -55.93) * mm, "mid": v(41.92, -55.69) * mm, "end": v(41.67, -55.44) * mm});
            skArc(sketch, "E792", {"start": v(42.16, -55.93) * mm, "mid": v(42.69, -56.17) * mm, "end": v(43.22, -55.97) * mm});
            skLineSegment(sketch, "E793", {"start": v(45.83, -54.72) * mm, "end": v(46.9, -54.5) * mm});
            skLineSegment(sketch, "E794", {"start": v(44.9, -55.02) * mm, "end": v(45.83, -54.72) * mm});
            skLineSegment(sketch, "E795", {"start": v(44.47, -55.19) * mm, "end": v(44.9, -55.02) * mm});
            skLineSegment(sketch, "E796", {"start": v(44.1, -55.36) * mm, "end": v(44.47, -55.19) * mm});
            skLineSegment(sketch, "E797", {"start": v(43.78, -55.54) * mm, "end": v(44.1, -55.36) * mm});
            skLineSegment(sketch, "E798", {"start": v(43.54, -55.7) * mm, "end": v(43.78, -55.54) * mm});
            skLineSegment(sketch, "E799", {"start": v(43.22, -55.97) * mm, "end": v(43.54, -55.7) * mm});
            skArc(sketch, "E800", {"start": v(47.77, -55.63) * mm, "mid": v(47.35, -55.06) * mm, "end": v(46.9, -54.5) * mm});
            skLineSegment(sketch, "E801", {"start": v(47.28, -56.61) * mm, "end": v(47.77, -55.63) * mm});
            skLineSegment(sketch, "E802", {"start": v(46.75, -57.45) * mm, "end": v(47.28, -56.61) * mm});
            skLineSegment(sketch, "E803", {"start": v(46.48, -57.8) * mm, "end": v(46.75, -57.45) * mm});
            skLineSegment(sketch, "E804", {"start": v(46.21, -58.12) * mm, "end": v(46.48, -57.8) * mm});
            skLineSegment(sketch, "E805", {"start": v(45.96, -58.38) * mm, "end": v(46.21, -58.12) * mm});
            skLineSegment(sketch, "E806", {"start": v(45.74, -58.58) * mm, "end": v(45.96, -58.38) * mm});
            skLineSegment(sketch, "E807", {"start": v(45.4, -58.8) * mm, "end": v(45.74, -58.58) * mm});
            skArc(sketch, "E808", {"start": v(45.4, -58.8) * mm, "mid": v(45.07, -59.28) * mm, "end": v(45.16, -59.84) * mm});
            skArc(sketch, "E809", {"start": v(45.5, -60.44) * mm, "mid": v(45.34, -60.14) * mm, "end": v(45.16, -59.84) * mm});
            skArc(sketch, "E810", {"start": v(45.5, -60.44) * mm, "mid": v(45.95, -60.8) * mm, "end": v(46.52, -60.75) * mm});
            skLineSegment(sketch, "E811", {"start": v(49.37, -60.22) * mm, "end": v(50.46, -60.29) * mm});
            skLineSegment(sketch, "E812", {"start": v(48.38, -60.26) * mm, "end": v(49.37, -60.22) * mm});
            skLineSegment(sketch, "E813", {"start": v(47.93, -60.32) * mm, "end": v(48.38, -60.26) * mm});
            skLineSegment(sketch, "E814", {"start": v(47.52, -60.4) * mm, "end": v(47.93, -60.32) * mm});
            skLineSegment(sketch, "E815", {"start": v(47.17, -60.48) * mm, "end": v(47.52, -60.4) * mm});
            skLineSegment(sketch, "E816", {"start": v(46.9, -60.57) * mm, "end": v(47.17, -60.48) * mm});
            skLineSegment(sketch, "E817", {"start": v(46.52, -60.75) * mm, "end": v(46.9, -60.57) * mm});
            skArc(sketch, "E818", {"start": v(51, -61.6) * mm, "mid": v(50.74, -60.94) * mm, "end": v(50.46, -60.29) * mm});
            skLineSegment(sketch, "E819", {"start": v(50.28, -62.42) * mm, "end": v(51, -61.6) * mm});
            skLineSegment(sketch, "E820", {"start": v(49.55, -63.09) * mm, "end": v(50.28, -62.42) * mm});
            skLineSegment(sketch, "E821", {"start": v(49.2, -63.37) * mm, "end": v(49.55, -63.09) * mm});
            skLineSegment(sketch, "E822", {"start": v(48.85, -63.6) * mm, "end": v(49.2, -63.37) * mm});
            skLineSegment(sketch, "E823", {"start": v(48.54, -63.79) * mm, "end": v(48.85, -63.6) * mm});
            skLineSegment(sketch, "E824", {"start": v(48.28, -63.92) * mm, "end": v(48.54, -63.79) * mm});
            skLineSegment(sketch, "E825", {"start": v(47.9, -64.06) * mm, "end": v(48.28, -63.92) * mm});
            skArc(sketch, "E826", {"start": v(47.9, -64.06) * mm, "mid": v(47.45, -64.42) * mm, "end": v(47.4, -65) * mm});
            skArc(sketch, "E827", {"start": v(47.57, -65.66) * mm, "mid": v(47.49, -65.33) * mm, "end": v(47.4, -65) * mm});
            skArc(sketch, "E828", {"start": v(47.57, -65.66) * mm, "mid": v(47.9, -66.12) * mm, "end": v(48.47, -66.22) * mm});
            skLineSegment(sketch, "E829", {"start": v(51.36, -66.45) * mm, "end": v(52.4, -66.8) * mm});
            skLineSegment(sketch, "E830", {"start": v(50.4, -66.23) * mm, "end": v(51.36, -66.45) * mm});
            skLineSegment(sketch, "E831", {"start": v(49.94, -66.17) * mm, "end": v(50.4, -66.23) * mm});
            skLineSegment(sketch, "E832", {"start": v(49.53, -66.13) * mm, "end": v(49.94, -66.17) * mm});
            skLineSegment(sketch, "E833", {"start": v(49.17, -66.13) * mm, "end": v(49.53, -66.13) * mm});
            skLineSegment(sketch, "E834", {"start": v(48.88, -66.15) * mm, "end": v(49.17, -66.13) * mm});
            skLineSegment(sketch, "E835", {"start": v(48.47, -66.22) * mm, "end": v(48.88, -66.15) * mm});
            skArc(sketch, "E836", {"start": v(52.58, -68.2) * mm, "mid": v(52.5, -67.5) * mm, "end": v(52.4, -66.8) * mm});
            skLineSegment(sketch, "E837", {"start": v(51.67, -68.8) * mm, "end": v(52.58, -68.2) * mm});
            skLineSegment(sketch, "E838", {"start": v(50.8, -69.26) * mm, "end": v(51.67, -68.8) * mm});
            skLineSegment(sketch, "E839", {"start": v(50.37, -69.44) * mm, "end": v(50.8, -69.26) * mm});
            skLineSegment(sketch, "E840", {"start": v(49.99, -69.58) * mm, "end": v(50.37, -69.44) * mm});
            skLineSegment(sketch, "E841", {"start": v(49.64, -69.68) * mm, "end": v(49.99, -69.58) * mm});
            skLineSegment(sketch, "E842", {"start": v(49.35, -69.74) * mm, "end": v(49.64, -69.68) * mm});
            skLineSegment(sketch, "E843", {"start": v(48.94, -69.77) * mm, "end": v(49.35, -69.74) * mm});
            skArc(sketch, "E844", {"start": v(48.94, -69.77) * mm, "mid": v(48.42, -70) * mm, "end": v(48.22, -70.54) * mm});
            skArc(sketch, "E845", {"start": v(48.22, -71.24) * mm, "mid": v(48.22, -70.9) * mm, "end": v(48.22, -70.54) * mm});
            skArc(sketch, "E846", {"start": v(48.22, -71.24) * mm, "mid": v(48.42, -71.77) * mm, "end": v(48.94, -72.01) * mm});
            skLineSegment(sketch, "E847", {"start": v(51.67, -72.98) * mm, "end": v(52.58, -73.58) * mm});
            skLineSegment(sketch, "E848", {"start": v(50.8, -72.52) * mm, "end": v(51.67, -72.98) * mm});
            skLineSegment(sketch, "E849", {"start": v(50.37, -72.34) * mm, "end": v(50.8, -72.52) * mm});
            skLineSegment(sketch, "E850", {"start": v(49.99, -72.2) * mm, "end": v(50.37, -72.34) * mm});
            skLineSegment(sketch, "E851", {"start": v(49.64, -72.1) * mm, "end": v(49.99, -72.2) * mm});
            skLineSegment(sketch, "E852", {"start": v(49.35, -72.04) * mm, "end": v(49.64, -72.1) * mm});
            skLineSegment(sketch, "E853", {"start": v(48.94, -72.01) * mm, "end": v(49.35, -72.04) * mm});
            skArc(sketch, "E854", {"start": v(52.4, -75) * mm, "mid": v(52.5, -74.28) * mm, "end": v(52.58, -73.58) * mm});
            skLineSegment(sketch, "E855", {"start": v(51.36, -75.33) * mm, "end": v(52.4, -75) * mm});
            skLineSegment(sketch, "E856", {"start": v(50.4, -75.55) * mm, "end": v(51.36, -75.33) * mm});
            skLineSegment(sketch, "E857", {"start": v(49.94, -75.61) * mm, "end": v(50.4, -75.55) * mm});
            skLineSegment(sketch, "E858", {"start": v(49.53, -75.65) * mm, "end": v(49.94, -75.61) * mm});
            skLineSegment(sketch, "E859", {"start": v(49.17, -75.65) * mm, "end": v(49.53, -75.65) * mm});
            skLineSegment(sketch, "E860", {"start": v(48.88, -75.64) * mm, "end": v(49.17, -75.65) * mm});
            skLineSegment(sketch, "E861", {"start": v(48.47, -75.56) * mm, "end": v(48.88, -75.64) * mm});
            skArc(sketch, "E862", {"start": v(48.47, -75.56) * mm, "mid": v(47.9, -75.66) * mm, "end": v(47.57, -76.12) * mm});
            skArc(sketch, "E863", {"start": v(47.4, -76.79) * mm, "mid": v(47.49, -76.46) * mm, "end": v(47.57, -76.12) * mm});
            skArc(sketch, "E864", {"start": v(47.4, -76.79) * mm, "mid": v(47.45, -77.36) * mm, "end": v(47.9, -77.73) * mm});
            skLineSegment(sketch, "E865", {"start": v(50.28, -79.36) * mm, "end": v(51, -80.18) * mm});
            skLineSegment(sketch, "E866", {"start": v(49.55, -78.7) * mm, "end": v(50.28, -79.36) * mm});
            skLineSegment(sketch, "E867", {"start": v(49.2, -78.41) * mm, "end": v(49.55, -78.7) * mm});
            skLineSegment(sketch, "E868", {"start": v(48.85, -78.18) * mm, "end": v(49.2, -78.41) * mm});
            skLineSegment(sketch, "E869", {"start": v(48.54, -78) * mm, "end": v(48.85, -78.18) * mm});
            skLineSegment(sketch, "E870", {"start": v(48.28, -77.86) * mm, "end": v(48.54, -78) * mm});
            skLineSegment(sketch, "E871", {"start": v(47.9, -77.73) * mm, "end": v(48.28, -77.86) * mm});
            skArc(sketch, "E872", {"start": v(50.46, -81.5) * mm, "mid": v(50.74, -80.84) * mm, "end": v(51, -80.18) * mm});
            skLineSegment(sketch, "E873", {"start": v(49.37, -81.56) * mm, "end": v(50.46, -81.5) * mm});
            skLineSegment(sketch, "E874", {"start": v(48.38, -81.52) * mm, "end": v(49.37, -81.56) * mm});
            skLineSegment(sketch, "E875", {"start": v(47.93, -81.46) * mm, "end": v(48.38, -81.52) * mm});
            skLineSegment(sketch, "E876", {"start": v(47.52, -81.4) * mm, "end": v(47.93, -81.46) * mm});
            skLineSegment(sketch, "E877", {"start": v(47.17, -81.3) * mm, "end": v(47.52, -81.4) * mm});
            skLineSegment(sketch, "E878", {"start": v(46.9, -81.2) * mm, "end": v(47.17, -81.3) * mm});
            skLineSegment(sketch, "E879", {"start": v(46.52, -81.03) * mm, "end": v(46.9, -81.2) * mm});
            skArc(sketch, "E880", {"start": v(46.52, -81.03) * mm, "mid": v(45.95, -80.98) * mm, "end": v(45.5, -81.34) * mm});
            skArc(sketch, "E881", {"start": v(45.16, -81.94) * mm, "mid": v(45.34, -81.64) * mm, "end": v(45.5, -81.34) * mm});
            skArc(sketch, "E882", {"start": v(45.16, -81.94) * mm, "mid": v(45.07, -82.5) * mm, "end": v(45.4, -82.97) * mm});
            skLineSegment(sketch, "E883", {"start": v(47.28, -85.17) * mm, "end": v(47.77, -86.15) * mm});
            skLineSegment(sketch, "E884", {"start": v(46.75, -84.34) * mm, "end": v(47.28, -85.17) * mm});
            skLineSegment(sketch, "E885", {"start": v(46.48, -83.97) * mm, "end": v(46.75, -84.34) * mm});
            skLineSegment(sketch, "E886", {"start": v(46.21, -83.66) * mm, "end": v(46.48, -83.97) * mm});
            skLineSegment(sketch, "E887", {"start": v(45.96, -83.4) * mm, "end": v(46.21, -83.66) * mm});
            skLineSegment(sketch, "E888", {"start": v(45.74, -83.2) * mm, "end": v(45.96, -83.4) * mm});
            skLineSegment(sketch, "E889", {"start": v(45.4, -82.97) * mm, "end": v(45.74, -83.2) * mm});
            skArc(sketch, "E890", {"start": v(46.9, -87.28) * mm, "mid": v(47.35, -86.72) * mm, "end": v(47.77, -86.15) * mm});
            skLineSegment(sketch, "E891", {"start": v(45.83, -87.06) * mm, "end": v(46.9, -87.28) * mm});
            skLineSegment(sketch, "E892", {"start": v(44.9, -86.76) * mm, "end": v(45.83, -87.06) * mm});
            skLineSegment(sketch, "E893", {"start": v(44.47, -86.6) * mm, "end": v(44.9, -86.76) * mm});
            skLineSegment(sketch, "E894", {"start": v(44.1, -86.42) * mm, "end": v(44.47, -86.6) * mm});
            skLineSegment(sketch, "E895", {"start": v(43.78, -86.24) * mm, "end": v(44.1, -86.42) * mm});
            skLineSegment(sketch, "E896", {"start": v(43.54, -86.08) * mm, "end": v(43.78, -86.24) * mm});
            skLineSegment(sketch, "E897", {"start": v(43.22, -85.81) * mm, "end": v(43.54, -86.08) * mm});
            skArc(sketch, "E898", {"start": v(43.22, -85.81) * mm, "mid": v(42.69, -85.61) * mm, "end": v(42.16, -85.85) * mm});
            skArc(sketch, "E899", {"start": v(41.67, -86.34) * mm, "mid": v(41.92, -86.1) * mm, "end": v(42.16, -85.85) * mm});
            skArc(sketch, "E900", {"start": v(41.67, -86.34) * mm, "mid": v(41.44, -86.86) * mm, "end": v(41.64, -87.4) * mm});
            skLineSegment(sketch, "E901", {"start": v(42.88, -90) * mm, "end": v(43.1, -91.08) * mm});
            skLineSegment(sketch, "E902", {"start": v(42.6, -89.06) * mm, "end": v(42.88, -90) * mm});
            skLineSegment(sketch, "E903", {"start": v(42.42, -88.64) * mm, "end": v(42.6, -89.06) * mm});
            skLineSegment(sketch, "E904", {"start": v(42.25, -88.27) * mm, "end": v(42.42, -88.64) * mm});
            skLineSegment(sketch, "E905", {"start": v(42.07, -87.95) * mm, "end": v(42.25, -88.27) * mm});
            skLineSegment(sketch, "E906", {"start": v(41.9, -87.7) * mm, "end": v(42.07, -87.95) * mm});
            skLineSegment(sketch, "E907", {"start": v(41.64, -87.4) * mm, "end": v(41.9, -87.7) * mm});
            skArc(sketch, "E908", {"start": v(41.97, -91.94) * mm, "mid": v(42.55, -91.52) * mm, "end": v(43.1, -91.08) * mm});
            skLineSegment(sketch, "E909", {"start": v(41, -91.45) * mm, "end": v(41.97, -91.94) * mm});
            skLineSegment(sketch, "E910", {"start": v(40.16, -90.93) * mm, "end": v(41, -91.45) * mm});
            skLineSegment(sketch, "E911", {"start": v(39.8, -90.65) * mm, "end": v(40.16, -90.93) * mm});
            skLineSegment(sketch, "E912", {"start": v(39.49, -90.39) * mm, "end": v(39.8, -90.65) * mm});
            skLineSegment(sketch, "E913", {"start": v(39.23, -90.13) * mm, "end": v(39.49, -90.39) * mm});
            skLineSegment(sketch, "E914", {"start": v(39.03, -89.92) * mm, "end": v(39.23, -90.13) * mm});
            skLineSegment(sketch, "E915", {"start": v(38.8, -89.57) * mm, "end": v(39.03, -89.92) * mm});
            skArc(sketch, "E916", {"start": v(38.8, -89.57) * mm, "mid": v(38.33, -89.25) * mm, "end": v(37.77, -89.33) * mm});
            skArc(sketch, "E917", {"start": v(37.17, -89.68) * mm, "mid": v(37.47, -89.51) * mm, "end": v(37.77, -89.33) * mm});
            skArc(sketch, "E918", {"start": v(37.17, -89.68) * mm, "mid": v(36.8, -90.13) * mm, "end": v(36.86, -90.7) * mm});
            skLineSegment(sketch, "E919", {"start": v(37.39, -93.54) * mm, "end": v(37.32, -94.63) * mm});
            skLineSegment(sketch, "E920", {"start": v(37.35, -92.55) * mm, "end": v(37.39, -93.54) * mm});
            skLineSegment(sketch, "E921", {"start": v(37.3, -92.1) * mm, "end": v(37.35, -92.55) * mm});
            skLineSegment(sketch, "E922", {"start": v(37.22, -91.7) * mm, "end": v(37.3, -92.1) * mm});
            skLineSegment(sketch, "E923", {"start": v(37.13, -91.34) * mm, "end": v(37.22, -91.7) * mm});
            skLineSegment(sketch, "E924", {"start": v(37.04, -91.07) * mm, "end": v(37.13, -91.34) * mm});
            skLineSegment(sketch, "E925", {"start": v(36.86, -90.7) * mm, "end": v(37.04, -91.07) * mm});
            skArc(sketch, "E926", {"start": v(36, -95.18) * mm, "mid": v(36.67, -94.91) * mm, "end": v(37.32, -94.63) * mm});
            skLineSegment(sketch, "E927", {"start": v(35.19, -94.45) * mm, "end": v(36, -95.18) * mm});
            skLineSegment(sketch, "E928", {"start": v(34.52, -93.72) * mm, "end": v(35.19, -94.45) * mm});
            skLineSegment(sketch, "E929", {"start": v(34.24, -93.37) * mm, "end": v(34.52, -93.72) * mm});
            skLineSegment(sketch, "E930", {"start": v(34, -93.03) * mm, "end": v(34.24, -93.37) * mm});
            skLineSegment(sketch, "E931", {"start": v(33.82, -92.72) * mm, "end": v(34, -93.03) * mm});
            skLineSegment(sketch, "E932", {"start": v(33.69, -92.45) * mm, "end": v(33.82, -92.72) * mm});
            skLineSegment(sketch, "E933", {"start": v(33.55, -92.06) * mm, "end": v(33.69, -92.45) * mm});
            skArc(sketch, "E934", {"start": v(33.55, -92.06) * mm, "mid": v(33.19, -91.63) * mm, "end": v(32.62, -91.57) * mm});
            skArc(sketch, "E935", {"start": v(31.95, -91.74) * mm, "mid": v(32.28, -91.66) * mm, "end": v(32.62, -91.57) * mm});
            skArc(sketch, "E936", {"start": v(31.95, -91.74) * mm, "mid": v(31.48, -92.08) * mm, "end": v(31.39, -92.65) * mm});
            skLineSegment(sketch, "E937", {"start": v(31.16, -95.53) * mm, "end": v(30.82, -96.57) * mm});
            skLineSegment(sketch, "E938", {"start": v(31.38, -94.57) * mm, "end": v(31.16, -95.53) * mm});
            skLineSegment(sketch, "E939", {"start": v(31.44, -94.12) * mm, "end": v(31.38, -94.57) * mm});
            skLineSegment(sketch, "E940", {"start": v(31.48, -93.7) * mm, "end": v(31.44, -94.12) * mm});
            skLineSegment(sketch, "E941", {"start": v(31.48, -93.34) * mm, "end": v(31.48, -93.7) * mm});
            skLineSegment(sketch, "E942", {"start": v(31.46, -93.05) * mm, "end": v(31.48, -93.34) * mm});
            skLineSegment(sketch, "E943", {"start": v(31.39, -92.65) * mm, "end": v(31.46, -93.05) * mm});
            skArc(sketch, "E944", {"start": v(29.4, -96.75) * mm, "mid": v(30.11, -96.67) * mm, "end": v(30.82, -96.57) * mm});
            skLineSegment(sketch, "E945", {"start": v(28.8, -95.84) * mm, "end": v(29.4, -96.75) * mm});
            skLineSegment(sketch, "E946", {"start": v(28.34, -94.96) * mm, "end": v(28.8, -95.84) * mm});
            skLineSegment(sketch, "E947", {"start": v(28.17, -94.55) * mm, "end": v(28.34, -94.96) * mm});
            skLineSegment(sketch, "E948", {"start": v(28.03, -94.16) * mm, "end": v(28.17, -94.55) * mm});
            skLineSegment(sketch, "E949", {"start": v(27.93, -93.8) * mm, "end": v(28.03, -94.16) * mm});
            skLineSegment(sketch, "E950", {"start": v(27.87, -93.52) * mm, "end": v(27.93, -93.8) * mm});
            skLineSegment(sketch, "E951", {"start": v(27.84, -93.11) * mm, "end": v(27.87, -93.52) * mm});
            skArc(sketch, "E952", {"start": v(27.84, -93.11) * mm, "mid": v(27.6, -92.6) * mm, "end": v(27.07, -92.39) * mm});
            skArc(sketch, "E953", {"start": v(26.37, -92.39) * mm, "mid": v(26.72, -92.4) * mm, "end": v(27.07, -92.39) * mm});
            skArc(sketch, "E954", {"start": v(26.37, -92.39) * mm, "mid": v(25.84, -92.6) * mm, "end": v(25.6, -93.11) * mm});
            skLineSegment(sketch, "E955", {"start": v(24.63, -95.84) * mm, "end": v(24.03, -96.75) * mm});
            skLineSegment(sketch, "E956", {"start": v(25.1, -94.96) * mm, "end": v(24.63, -95.84) * mm});
            skLineSegment(sketch, "E957", {"start": v(25.27, -94.55) * mm, "end": v(25.1, -94.96) * mm});
            skLineSegment(sketch, "E958", {"start": v(25.4, -94.16) * mm, "end": v(25.27, -94.55) * mm});
            skLineSegment(sketch, "E959", {"start": v(25.5, -93.8) * mm, "end": v(25.4, -94.16) * mm});
            skLineSegment(sketch, "E960", {"start": v(25.57, -93.52) * mm, "end": v(25.5, -93.8) * mm});
            skLineSegment(sketch, "E961", {"start": v(25.6, -93.11) * mm, "end": v(25.57, -93.52) * mm});
            skArc(sketch, "E962", {"start": v(22.62, -96.57) * mm, "mid": v(23.32, -96.67) * mm, "end": v(24.03, -96.75) * mm});
            skLineSegment(sketch, "E963", {"start": v(22.28, -95.53) * mm, "end": v(22.62, -96.57) * mm});
            skLineSegment(sketch, "E964", {"start": v(22.06, -94.57) * mm, "end": v(22.28, -95.53) * mm});
            skLineSegment(sketch, "E965", {"start": v(22, -94.12) * mm, "end": v(22.06, -94.57) * mm});
            skLineSegment(sketch, "E966", {"start": v(21.96, -93.7) * mm, "end": v(22, -94.12) * mm});
            skLineSegment(sketch, "E967", {"start": v(21.95, -93.34) * mm, "end": v(21.96, -93.7) * mm});
            skLineSegment(sketch, "E968", {"start": v(21.97, -93.05) * mm, "end": v(21.95, -93.34) * mm});
            skLineSegment(sketch, "E969", {"start": v(22.05, -92.65) * mm, "end": v(21.97, -93.05) * mm});
            skArc(sketch, "E970", {"start": v(22.05, -92.65) * mm, "mid": v(21.95, -92.08) * mm, "end": v(21.49, -91.74) * mm});
            skArc(sketch, "E971", {"start": v(20.82, -91.57) * mm, "mid": v(21.15, -91.66) * mm, "end": v(21.49, -91.74) * mm});
            skArc(sketch, "E972", {"start": v(20.82, -91.57) * mm, "mid": v(20.25, -91.63) * mm, "end": v(19.88, -92.06) * mm});
            skLineSegment(sketch, "E973", {"start": v(18.25, -94.45) * mm, "end": v(17.43, -95.18) * mm});
            skLineSegment(sketch, "E974", {"start": v(18.92, -93.72) * mm, "end": v(18.25, -94.45) * mm});
            skLineSegment(sketch, "E975", {"start": v(19.2, -93.37) * mm, "end": v(18.92, -93.72) * mm});
            skLineSegment(sketch, "E976", {"start": v(19.43, -93.03) * mm, "end": v(19.2, -93.37) * mm});
            skLineSegment(sketch, "E977", {"start": v(19.62, -92.72) * mm, "end": v(19.43, -93.03) * mm});
            skLineSegment(sketch, "E978", {"start": v(19.75, -92.45) * mm, "end": v(19.62, -92.72) * mm});
            skLineSegment(sketch, "E979", {"start": v(19.88, -92.06) * mm, "end": v(19.75, -92.45) * mm});
            skArc(sketch, "E980", {"start": v(16.11, -94.63) * mm, "mid": v(16.77, -94.91) * mm, "end": v(17.43, -95.18) * mm});
            skLineSegment(sketch, "E981", {"start": v(16.05, -93.54) * mm, "end": v(16.11, -94.63) * mm});
            skLineSegment(sketch, "E982", {"start": v(16.09, -92.55) * mm, "end": v(16.05, -93.54) * mm});
            skLineSegment(sketch, "E983", {"start": v(16.14, -92.1) * mm, "end": v(16.09, -92.55) * mm});
            skLineSegment(sketch, "E984", {"start": v(16.22, -91.7) * mm, "end": v(16.14, -92.1) * mm});
            skLineSegment(sketch, "E985", {"start": v(16.3, -91.34) * mm, "end": v(16.22, -91.7) * mm});
            skLineSegment(sketch, "E986", {"start": v(16.4, -91.07) * mm, "end": v(16.3, -91.34) * mm});
            skLineSegment(sketch, "E987", {"start": v(16.58, -90.7) * mm, "end": v(16.4, -91.07) * mm});
            skArc(sketch, "E988", {"start": v(16.58, -90.7) * mm, "mid": v(16.63, -90.13) * mm, "end": v(16.27, -89.68) * mm});
            skArc(sketch, "E989", {"start": v(15.67, -89.33) * mm, "mid": v(15.97, -89.51) * mm, "end": v(16.27, -89.68) * mm});
            skArc(sketch, "E990", {"start": v(15.67, -89.33) * mm, "mid": v(15.1, -89.25) * mm, "end": v(14.64, -89.57) * mm});
            skLineSegment(sketch, "E991", {"start": v(12.44, -91.45) * mm, "end": v(11.46, -91.94) * mm});
            skLineSegment(sketch, "E992", {"start": v(13.27, -90.93) * mm, "end": v(12.44, -91.45) * mm});
            skLineSegment(sketch, "E993", {"start": v(13.64, -90.65) * mm, "end": v(13.27, -90.93) * mm});
            skLineSegment(sketch, "E994", {"start": v(13.95, -90.39) * mm, "end": v(13.64, -90.65) * mm});
            skLineSegment(sketch, "E995", {"start": v(14.21, -90.13) * mm, "end": v(13.95, -90.39) * mm});
            skLineSegment(sketch, "E996", {"start": v(14.4, -89.92) * mm, "end": v(14.21, -90.13) * mm});
            skLineSegment(sketch, "E997", {"start": v(14.64, -89.57) * mm, "end": v(14.4, -89.92) * mm});
            skArc(sketch, "E998", {"start": v(10.33, -91.08) * mm, "mid": v(10.9, -91.52) * mm, "end": v(11.46, -91.94) * mm});
            skLineSegment(sketch, "E999", {"start": v(10.55, -90) * mm, "end": v(10.33, -91.08) * mm});
            skLineSegment(sketch, "E1000", {"start": v(10.85, -89.06) * mm, "end": v(10.55, -90) * mm});
            skLineSegment(sketch, "E1001", {"start": v(11.01, -88.64) * mm, "end": v(10.85, -89.06) * mm});
            skLineSegment(sketch, "E1002", {"start": v(11.2, -88.27) * mm, "end": v(11.01, -88.64) * mm});
            skLineSegment(sketch, "E1003", {"start": v(11.37, -87.95) * mm, "end": v(11.2, -88.27) * mm});
            skLineSegment(sketch, "E1004", {"start": v(11.53, -87.7) * mm, "end": v(11.37, -87.95) * mm});
            skLineSegment(sketch, "E1005", {"start": v(11.8, -87.4) * mm, "end": v(11.53, -87.7) * mm});
            skArc(sketch, "E1006", {"start": v(11.8, -87.4) * mm, "mid": v(12, -86.86) * mm, "end": v(11.76, -86.34) * mm});
            skArc(sketch, "E1007", {"start": v(11.27, -85.85) * mm, "mid": v(11.52, -86.1) * mm, "end": v(11.76, -86.34) * mm});
            skArc(sketch, "E1008", {"start": v(11.27, -85.85) * mm, "mid": v(10.75, -85.61) * mm, "end": v(10.21, -85.81) * mm});
            skLineSegment(sketch, "E1009", {"start": v(7.6, -87.06) * mm, "end": v(6.53, -87.28) * mm});
            skLineSegment(sketch, "E1010", {"start": v(8.55, -86.76) * mm, "end": v(7.6, -87.06) * mm});
            skLineSegment(sketch, "E1011", {"start": v(8.97, -86.6) * mm, "end": v(8.55, -86.76) * mm});
            skLineSegment(sketch, "E1012", {"start": v(9.34, -86.42) * mm, "end": v(8.97, -86.6) * mm});
            skLineSegment(sketch, "E1013", {"start": v(9.66, -86.24) * mm, "end": v(9.34, -86.42) * mm});
            skLineSegment(sketch, "E1014", {"start": v(9.9, -86.08) * mm, "end": v(9.66, -86.24) * mm});
            skLineSegment(sketch, "E1015", {"start": v(10.21, -85.81) * mm, "end": v(9.9, -86.08) * mm});
            skArc(sketch, "E1016", {"start": v(5.66, -86.15) * mm, "mid": v(6.1, -86.72) * mm, "end": v(6.53, -87.28) * mm});
            skLineSegment(sketch, "E1017", {"start": v(6.16, -85.17) * mm, "end": v(5.66, -86.15) * mm});
            skLineSegment(sketch, "E1018", {"start": v(6.68, -84.34) * mm, "end": v(6.16, -85.17) * mm});
            skLineSegment(sketch, "E1019", {"start": v(6.96, -83.97) * mm, "end": v(6.68, -84.34) * mm});
            skLineSegment(sketch, "E1020", {"start": v(7.22, -83.66) * mm, "end": v(6.96, -83.97) * mm});
            skLineSegment(sketch, "E1021", {"start": v(7.47, -83.4) * mm, "end": v(7.22, -83.66) * mm});
            skLineSegment(sketch, "E1022", {"start": v(7.7, -83.2) * mm, "end": v(7.47, -83.4) * mm});
            skLineSegment(sketch, "E1023", {"start": v(8.03, -82.97) * mm, "end": v(7.7, -83.2) * mm});
            skArc(sketch, "E1024", {"start": v(8.03, -82.97) * mm, "mid": v(8.36, -82.5) * mm, "end": v(8.27, -81.94) * mm});
            skArc(sketch, "E1025", {"start": v(7.93, -81.34) * mm, "mid": v(8.1, -81.64) * mm, "end": v(8.27, -81.94) * mm});
            skArc(sketch, "E1026", {"start": v(7.93, -81.34) * mm, "mid": v(7.48, -80.98) * mm, "end": v(6.91, -81.03) * mm});
            skLineSegment(sketch, "E1027", {"start": v(4.07, -81.56) * mm, "end": v(2.98, -81.5) * mm});
            skLineSegment(sketch, "E1028", {"start": v(5.06, -81.52) * mm, "end": v(4.07, -81.56) * mm});
            skLineSegment(sketch, "E1029", {"start": v(5.5, -81.46) * mm, "end": v(5.06, -81.52) * mm});
            skLineSegment(sketch, "E1030", {"start": v(5.91, -81.4) * mm, "end": v(5.5, -81.46) * mm});
            skLineSegment(sketch, "E1031", {"start": v(6.26, -81.3) * mm, "end": v(5.91, -81.4) * mm});
            skLineSegment(sketch, "E1032", {"start": v(6.54, -81.2) * mm, "end": v(6.26, -81.3) * mm});
            skLineSegment(sketch, "E1033", {"start": v(6.91, -81.03) * mm, "end": v(6.54, -81.2) * mm});
            skArc(sketch, "E1034", {"start": v(2.43, -80.18) * mm, "mid": v(2.7, -80.84) * mm, "end": v(2.98, -81.5) * mm});
            skLineSegment(sketch, "E1035", {"start": v(3.16, -79.36) * mm, "end": v(2.43, -80.18) * mm});
            skLineSegment(sketch, "E1036", {"start": v(3.89, -78.7) * mm, "end": v(3.16, -79.36) * mm});
            skLineSegment(sketch, "E1037", {"start": v(4.24, -78.41) * mm, "end": v(3.89, -78.7) * mm});
            skLineSegment(sketch, "E1038", {"start": v(4.58, -78.18) * mm, "end": v(4.24, -78.41) * mm});
            skLineSegment(sketch, "E1039", {"start": v(4.9, -78) * mm, "end": v(4.58, -78.18) * mm});
            skLineSegment(sketch, "E1040", {"start": v(5.15, -77.86) * mm, "end": v(4.9, -78) * mm});
            skLineSegment(sketch, "E1041", {"start": v(5.54, -77.73) * mm, "end": v(5.15, -77.86) * mm});
            skArc(sketch, "E1042", {"start": v(5.54, -77.73) * mm, "mid": v(5.98, -77.36) * mm, "end": v(6.04, -76.79) * mm});
            skArc(sketch, "E1043", {"start": v(9.67, -13.55) * mm, "mid": v(9.89, -13.83) * mm, "end": v(10.11, -14.1) * mm});
            skArc(sketch, "E1044", {"start": v(9.67, -13.55) * mm, "mid": v(9.17, -13.27) * mm, "end": v(8.61, -13.4) * mm});
            skLineSegment(sketch, "E1045", {"start": v(5.89, -14.38) * mm, "end": v(4.8, -14.48) * mm});
            skLineSegment(sketch, "E1046", {"start": v(6.85, -14.2) * mm, "end": v(5.89, -14.38) * mm});
            skLineSegment(sketch, "E1047", {"start": v(7.2, -14.1) * mm, "end": v(6.85, -14.2) * mm});
            skLineSegment(sketch, "E1048", {"start": v(7.54, -13.98) * mm, "end": v(7.2, -14.1) * mm});
            skLineSegment(sketch, "E1049", {"start": v(7.84, -13.87) * mm, "end": v(7.54, -13.98) * mm});
            skLineSegment(sketch, "E1050", {"start": v(8.09, -13.75) * mm, "end": v(7.84, -13.87) * mm});
            skLineSegment(sketch, "E1051", {"start": v(8.27, -13.65) * mm, "end": v(8.09, -13.75) * mm});
            skLineSegment(sketch, "E1052", {"start": v(8.61, -13.4) * mm, "end": v(8.27, -13.65) * mm});
            skArc(sketch, "E1053", {"start": v(4.07, -13.27) * mm, "mid": v(4.43, -13.88) * mm, "end": v(4.8, -14.48) * mm});
            skLineSegment(sketch, "E1054", {"start": v(4.66, -12.36) * mm, "end": v(4.07, -13.27) * mm});
            skLineSegment(sketch, "E1055", {"start": v(5.26, -11.6) * mm, "end": v(4.66, -12.36) * mm});
            skLineSegment(sketch, "E1056", {"start": v(5.52, -11.31) * mm, "end": v(5.26, -11.6) * mm});
            skLineSegment(sketch, "E1057", {"start": v(5.77, -11.07) * mm, "end": v(5.52, -11.31) * mm});
            skLineSegment(sketch, "E1058", {"start": v(6, -10.86) * mm, "end": v(5.77, -11.07) * mm});
            skLineSegment(sketch, "E1059", {"start": v(6.22, -10.7) * mm, "end": v(6, -10.86) * mm});
            skLineSegment(sketch, "E1060", {"start": v(6.4, -10.58) * mm, "end": v(6.22, -10.7) * mm});
            skLineSegment(sketch, "E1061", {"start": v(6.77, -10.39) * mm, "end": v(6.4, -10.58) * mm});
            skArc(sketch, "E1062", {"start": v(6.77, -10.39) * mm, "mid": v(7.16, -9.95) * mm, "end": v(7.13, -9.38) * mm});
            skArc(sketch, "E1063", {"start": v(6.85, -8.74) * mm, "mid": v(6.99, -9.06) * mm, "end": v(7.13, -9.38) * mm});
            skArc(sketch, "E1064", {"start": v(6.85, -8.74) * mm, "mid": v(6.45, -8.32) * mm, "end": v(5.87, -8.3) * mm});
            skLineSegment(sketch, "E1065", {"start": v(2.99, -8.51) * mm, "end": v(1.92, -8.32) * mm});
            skLineSegment(sketch, "E1066", {"start": v(3.96, -8.59) * mm, "end": v(2.99, -8.51) * mm});
            skLineSegment(sketch, "E1067", {"start": v(4.34, -8.6) * mm, "end": v(3.96, -8.59) * mm});
            skLineSegment(sketch, "E1068", {"start": v(4.69, -8.58) * mm, "end": v(4.34, -8.6) * mm});
            skLineSegment(sketch, "E1069", {"start": v(5, -8.54) * mm, "end": v(4.69, -8.58) * mm});
            skLineSegment(sketch, "E1070", {"start": v(5.27, -8.5) * mm, "end": v(5, -8.54) * mm});
            skLineSegment(sketch, "E1071", {"start": v(5.47, -8.45) * mm, "end": v(5.27, -8.5) * mm});
            skLineSegment(sketch, "E1072", {"start": v(5.87, -8.3) * mm, "end": v(5.47, -8.45) * mm});
            skArc(sketch, "E1073", {"start": v(1.54, -6.95) * mm, "mid": v(1.72, -7.64) * mm, "end": v(1.92, -8.32) * mm});
            skLineSegment(sketch, "E1074", {"start": v(2.35, -6.23) * mm, "end": v(1.54, -6.95) * mm});
            skLineSegment(sketch, "E1075", {"start": v(3.14, -5.66) * mm, "end": v(2.35, -6.23) * mm});
            skLineSegment(sketch, "E1076", {"start": v(3.46, -5.46) * mm, "end": v(3.14, -5.66) * mm});
            skLineSegment(sketch, "E1077", {"start": v(3.77, -5.3) * mm, "end": v(3.46, -5.46) * mm});
            skLineSegment(sketch, "E1078", {"start": v(4.05, -5.15) * mm, "end": v(3.77, -5.3) * mm});
            skLineSegment(sketch, "E1079", {"start": v(4.3, -5.05) * mm, "end": v(4.05, -5.15) * mm});
            skLineSegment(sketch, "E1080", {"start": v(4.5, -4.99) * mm, "end": v(4.3, -5.05) * mm});
            skLineSegment(sketch, "E1081", {"start": v(4.92, -4.9) * mm, "end": v(4.5, -4.99) * mm});
            skArc(sketch, "E1082", {"start": v(4.92, -4.9) * mm, "mid": v(5.4, -4.59) * mm, "end": v(5.53, -4.03) * mm});
            skArc(sketch, "E1083", {"start": v(5.44, -3.34) * mm, "mid": v(5.48, -3.68) * mm, "end": v(5.53, -4.03) * mm});
            skArc(sketch, "E1084", {"start": v(5.44, -3.34) * mm, "mid": v(5.16, -2.83) * mm, "end": v(4.6, -2.66) * mm});
            skLineSegment(sketch, "E1085", {"start": v(1.78, -2.07) * mm, "end": v(0.8, -1.6) * mm});
            skLineSegment(sketch, "E1086", {"start": v(2.7, -2.41) * mm, "end": v(1.78, -2.07) * mm});
            skLineSegment(sketch, "E1087", {"start": v(3.05, -2.52) * mm, "end": v(2.7, -2.41) * mm});
            skLineSegment(sketch, "E1088", {"start": v(3.4, -2.6) * mm, "end": v(3.05, -2.52) * mm});
            skLineSegment(sketch, "E1089", {"start": v(3.7, -2.65) * mm, "end": v(3.4, -2.6) * mm});
            skLineSegment(sketch, "E1090", {"start": v(3.98, -2.68) * mm, "end": v(3.7, -2.65) * mm});
            skLineSegment(sketch, "E1091", {"start": v(4.19, -2.69) * mm, "end": v(3.98, -2.68) * mm});
            skLineSegment(sketch, "E1092", {"start": v(4.6, -2.66) * mm, "end": v(4.19, -2.69) * mm});
            skArc(sketch, "E1093", {"start": v(0.8, -0.18) * mm, "mid": v(0.8, -0.9) * mm, "end": v(0.8, -1.6) * mm});
            skLineSegment(sketch, "E1094", {"start": v(1.78, 0.3) * mm, "end": v(0.8, -0.18) * mm});
            skLineSegment(sketch, "E1095", {"start": v(-58.58, 14.08) * mm, "end": v(-58.43, 14.22) * mm});
            skLineSegment(sketch, "E1096", {"start": v(-58.43, 14.22) * mm, "end": v(-58.24, 14.41) * mm});
            skLineSegment(sketch, "E1097", {"start": v(-58.24, 14.41) * mm, "end": v(-58.03, 14.65) * mm});
            skLineSegment(sketch, "E1098", {"start": v(-58.03, 14.65) * mm, "end": v(-57.81, 14.93) * mm});
            skLineSegment(sketch, "E1099", {"start": v(-57.81, 14.93) * mm, "end": v(-57.6, 15.24) * mm});
            skLineSegment(sketch, "E1100", {"start": v(-57.6, 15.24) * mm, "end": v(-57.1, 16.08) * mm});
            skLineSegment(sketch, "E1101", {"start": v(-57.1, 16.08) * mm, "end": v(-56.64, 17.06) * mm});
            skArc(sketch, "E1102", {"start": v(-56.64, 17.06) * mm, "mid": v(-57.08, 17.62) * mm, "end": v(-57.54, 18.16) * mm});
            skLineSegment(sketch, "E1103", {"start": v(-61.16, 16.58) * mm, "end": v(-60.85, 16.87) * mm});
            skLineSegment(sketch, "E1104", {"start": v(-60.85, 16.87) * mm, "end": v(-60.69, 17) * mm});
            skLineSegment(sketch, "E1105", {"start": v(-60.69, 17) * mm, "end": v(-60.46, 17.14) * mm});
            skLineSegment(sketch, "E1106", {"start": v(-60.46, 17.14) * mm, "end": v(-60.18, 17.3) * mm});
            skLineSegment(sketch, "E1107", {"start": v(-60.18, 17.3) * mm, "end": v(-59.87, 17.45) * mm});
            skLineSegment(sketch, "E1108", {"start": v(-59.87, 17.45) * mm, "end": v(-59.52, 17.6) * mm});
            skLineSegment(sketch, "E1109", {"start": v(-59.52, 17.6) * mm, "end": v(-58.6, 17.92) * mm});
            skLineSegment(sketch, "E1110", {"start": v(-58.6, 17.92) * mm, "end": v(-57.54, 18.16) * mm});
            skArc(sketch, "E1111", {"start": v(-62.23, 16.58) * mm, "mid": v(-61.7, 16.37) * mm, "end": v(-61.16, 16.58) * mm});
            skArc(sketch, "E1112", {"start": v(-62.23, 16.58) * mm, "mid": v(-62.48, 16.82) * mm, "end": v(-62.74, 17.06) * mm});
            skArc(sketch, "E1113", {"start": v(-62.82, 18.13) * mm, "mid": v(-63, 17.58) * mm, "end": v(-62.74, 17.06) * mm});
            skLineSegment(sketch, "E1114", {"start": v(-62.82, 18.13) * mm, "end": v(-62.55, 18.46) * mm});
            skLineSegment(sketch, "E1115", {"start": v(-62.55, 18.46) * mm, "end": v(-62.44, 18.63) * mm});
            skLineSegment(sketch, "E1116", {"start": v(-62.44, 18.63) * mm, "end": v(-62.3, 18.87) * mm});
            skLineSegment(sketch, "E1117", {"start": v(-62.3, 18.87) * mm, "end": v(-62.17, 19.16) * mm});
            skLineSegment(sketch, "E1118", {"start": v(-91.13, 19.76) * mm, "end": v(-92, 20.2) * mm});
            skLineSegment(sketch, "E1119", {"start": v(-92, 20.2) * mm, "end": v(-93.02, 20.59) * mm});
            skArc(sketch, "E1120", {"start": v(-93.02, 20.59) * mm, "mid": v(-93.54, 20.11) * mm, "end": v(-94.05, 19.62) * mm});
            skLineSegment(sketch, "E1121", {"start": v(-92.23, 16.12) * mm, "end": v(-92.54, 16.4) * mm});
            skLineSegment(sketch, "E1122", {"start": v(-92.54, 16.4) * mm, "end": v(-92.67, 16.56) * mm});
            skLineSegment(sketch, "E1123", {"start": v(-92.67, 16.56) * mm, "end": v(-92.84, 16.78) * mm});
            skLineSegment(sketch, "E1124", {"start": v(-92.84, 16.78) * mm, "end": v(-93, 17.05) * mm});
            skLineSegment(sketch, "E1125", {"start": v(-93, 17.05) * mm, "end": v(-93.18, 17.35) * mm});
            skLineSegment(sketch, "E1126", {"start": v(-93.18, 17.35) * mm, "end": v(-93.36, 17.68) * mm});
            skLineSegment(sketch, "E1127", {"start": v(-93.36, 17.68) * mm, "end": v(-93.73, 18.59) * mm});
            skLineSegment(sketch, "E1128", {"start": v(-93.73, 18.59) * mm, "end": v(-94.05, 19.62) * mm});
            skArc(sketch, "E1129", {"start": v(-92.16, 15.05) * mm, "mid": v(-91.98, 15.6) * mm, "end": v(-92.23, 16.12) * mm});
            skArc(sketch, "E1130", {"start": v(-92.16, 15.05) * mm, "mid": v(-92.38, 14.78) * mm, "end": v(-92.6, 14.5) * mm});
            skArc(sketch, "E1131", {"start": v(-93.66, 14.36) * mm, "mid": v(-93.1, 14.22) * mm, "end": v(-92.6, 14.5) * mm});
            skLineSegment(sketch, "E1132", {"start": v(-93.66, 14.36) * mm, "end": v(-94, 14.6) * mm});
            skLineSegment(sketch, "E1133", {"start": v(-94, 14.6) * mm, "end": v(-94.18, 14.7) * mm});
            skLineSegment(sketch, "E1134", {"start": v(-94.18, 14.7) * mm, "end": v(-94.43, 14.82) * mm});
            skLineSegment(sketch, "E1135", {"start": v(-94.43, 14.82) * mm, "end": v(-94.73, 14.94) * mm});
            skLineSegment(sketch, "E1136", {"start": v(-94.73, 14.94) * mm, "end": v(-95.06, 15.05) * mm});
            skLineSegment(sketch, "E1137", {"start": v(-95.06, 15.05) * mm, "end": v(-95.42, 15.15) * mm});
            skLineSegment(sketch, "E1138", {"start": v(-95.42, 15.15) * mm, "end": v(-96.38, 15.33) * mm});
            skLineSegment(sketch, "E1139", {"start": v(-96.38, 15.33) * mm, "end": v(-97.46, 15.43) * mm});
            skArc(sketch, "E1140", {"start": v(-97.46, 15.43) * mm, "mid": v(-97.84, 14.83) * mm, "end": v(-98.2, 14.22) * mm});
            skLineSegment(sketch, "E1141", {"start": v(-95.5, 11.34) * mm, "end": v(-95.87, 11.53) * mm});
            skLineSegment(sketch, "E1142", {"start": v(-95.87, 11.53) * mm, "end": v(-96.04, 11.65) * mm});
            skLineSegment(sketch, "E1143", {"start": v(-96.04, 11.65) * mm, "end": v(-96.26, 11.81) * mm});
            skLineSegment(sketch, "E1144", {"start": v(-96.26, 11.81) * mm, "end": v(-96.5, 12.02) * mm});
            skLineSegment(sketch, "E1145", {"start": v(-96.5, 12.02) * mm, "end": v(-96.75, 12.27) * mm});
            skLineSegment(sketch, "E1146", {"start": v(-96.75, 12.27) * mm, "end": v(-97, 12.54) * mm});
            skLineSegment(sketch, "E1147", {"start": v(-97, 12.54) * mm, "end": v(-97.61, 13.3) * mm});
            skLineSegment(sketch, "E1148", {"start": v(-97.61, 13.3) * mm, "end": v(-98.2, 14.22) * mm});
            skArc(sketch, "E1149", {"start": v(-95.14, 10.33) * mm, "mid": v(-95.11, 10.9) * mm, "end": v(-95.5, 11.34) * mm});
            skArc(sketch, "E1150", {"start": v(-95.14, 10.33) * mm, "mid": v(-95.28, 10) * mm, "end": v(-95.42, 9.69) * mm});
            skArc(sketch, "E1151", {"start": v(-96.4, 9.26) * mm, "mid": v(-95.82, 9.28) * mm, "end": v(-95.42, 9.69) * mm});
            skLineSegment(sketch, "E1152", {"start": v(-96.4, 9.26) * mm, "end": v(-96.8, 9.4) * mm});
            skLineSegment(sketch, "E1153", {"start": v(-96.8, 9.4) * mm, "end": v(-97, 9.45) * mm});
            skLineSegment(sketch, "E1154", {"start": v(-97, 9.45) * mm, "end": v(-97.27, 9.5) * mm});
            skArc(sketch, "E1155", {"start": v(-90.16, 54.26) * mm, "mid": v(-90, 54.81) * mm, "end": v(-90.27, 55.33) * mm});
            skLineSegment(sketch, "E1156", {"start": v(-97.27, 9.5) * mm, "end": v(-97.58, 9.53) * mm});
            skLineSegment(sketch, "E1157", {"start": v(-90.16, 54.26) * mm, "end": v(-90.44, 53.88) * mm});
            skLineSegment(sketch, "E1158", {"start": v(-97.58, 9.53) * mm, "end": v(-97.93, 9.54) * mm});
            skLineSegment(sketch, "E1159", {"start": v(-90.44, 53.88) * mm, "end": v(-90.54, 53.71) * mm});
            skLineSegment(sketch, "E1160", {"start": v(-97.93, 9.54) * mm, "end": v(-98.3, 9.54) * mm});
            skLineSegment(sketch, "E1161", {"start": v(-90.54, 53.71) * mm, "end": v(-90.66, 53.47) * mm});
            skLineSegment(sketch, "E1162", {"start": v(-98.3, 9.54) * mm, "end": v(-99.28, 9.46) * mm});
            skLineSegment(sketch, "E1163", {"start": v(-90.66, 53.47) * mm, "end": v(-90.78, 53.19) * mm});
            skLineSegment(sketch, "E1164", {"start": v(-99.28, 9.46) * mm, "end": v(-100.35, 9.27) * mm});
            skLineSegment(sketch, "E1165", {"start": v(-90.78, 53.19) * mm, "end": v(-90.9, 52.86) * mm});
            skArc(sketch, "E1166", {"start": v(-100.35, 9.27) * mm, "mid": v(-100.55, 8.59) * mm, "end": v(-100.73, 7.9) * mm});
            skLineSegment(sketch, "E1167", {"start": v(-90.9, 52.86) * mm, "end": v(-91, 52.5) * mm});
            skLineSegment(sketch, "E1168", {"start": v(-97.35, 5.85) * mm, "end": v(-97.77, 5.94) * mm});
            skLineSegment(sketch, "E1169", {"start": v(-91, 52.5) * mm, "end": v(-91.21, 51.56) * mm});
            skLineSegment(sketch, "E1170", {"start": v(-97.77, 5.94) * mm, "end": v(-97.96, 6) * mm});
            skLineSegment(sketch, "E1171", {"start": v(-91.21, 51.56) * mm, "end": v(-91.33, 50.5) * mm});
            skLineSegment(sketch, "E1172", {"start": v(-97.96, 6) * mm, "end": v(-98.22, 6.1) * mm});
            skArc(sketch, "E1173", {"start": v(-91.33, 50.5) * mm, "mid": v(-90.75, 50.1) * mm, "end": v(-90.15, 49.73) * mm});
            skLineSegment(sketch, "E1174", {"start": v(-98.22, 6.1) * mm, "end": v(-98.5, 6.24) * mm});
            skLineSegment(sketch, "E1175", {"start": v(-87.21, 52.36) * mm, "end": v(-87.43, 51.96) * mm});
            skLineSegment(sketch, "E1176", {"start": v(-98.5, 6.24) * mm, "end": v(-98.8, 6.41) * mm});
            skLineSegment(sketch, "E1177", {"start": v(-87.43, 51.96) * mm, "end": v(-87.55, 51.8) * mm});
            skLineSegment(sketch, "E1178", {"start": v(-98.8, 6.41) * mm, "end": v(-99.13, 6.6) * mm});
            skLineSegment(sketch, "E1179", {"start": v(-87.55, 51.8) * mm, "end": v(-87.72, 51.58) * mm});
            skLineSegment(sketch, "E1180", {"start": v(-99.13, 6.6) * mm, "end": v(-99.92, 7.18) * mm});
            skLineSegment(sketch, "E1181", {"start": v(-87.72, 51.58) * mm, "end": v(-87.93, 51.35) * mm});
            skLineSegment(sketch, "E1182", {"start": v(-99.92, 7.18) * mm, "end": v(-100.73, 7.9) * mm});
            skLineSegment(sketch, "E1183", {"start": v(-87.93, 51.35) * mm, "end": v(-88.17, 51.11) * mm});
            skArc(sketch, "E1184", {"start": v(-96.74, 4.98) * mm, "mid": v(-96.87, 5.54) * mm, "end": v(-97.35, 5.85) * mm});
            skLineSegment(sketch, "E1185", {"start": v(-88.17, 51.11) * mm, "end": v(-88.45, 50.86) * mm});
            skArc(sketch, "E1186", {"start": v(-96.74, 4.98) * mm, "mid": v(-96.79, 4.63) * mm, "end": v(-96.83, 4.29) * mm});
            skLineSegment(sketch, "E1187", {"start": v(-88.45, 50.86) * mm, "end": v(-89.23, 50.28) * mm});
            skArc(sketch, "E1188", {"start": v(-97.66, 3.61) * mm, "mid": v(-97.1, 3.78) * mm, "end": v(-96.83, 4.29) * mm});
            skLineSegment(sketch, "E1189", {"start": v(-89.23, 50.28) * mm, "end": v(-90.15, 49.73) * mm});
            skLineSegment(sketch, "E1190", {"start": v(-97.66, 3.61) * mm, "end": v(-98.08, 3.64) * mm});
            skArc(sketch, "E1191", {"start": v(-86.2, 52.7) * mm, "mid": v(-86.77, 52.74) * mm, "end": v(-87.21, 52.36) * mm});
            skLineSegment(sketch, "E1192", {"start": v(-98.08, 3.64) * mm, "end": v(-98.29, 3.63) * mm});
            skArc(sketch, "E1193", {"start": v(-86.2, 52.7) * mm, "mid": v(-85.87, 52.55) * mm, "end": v(-85.55, 52.41) * mm});
            skLineSegment(sketch, "E1194", {"start": v(-98.29, 3.63) * mm, "end": v(-98.56, 3.6) * mm});
            skArc(sketch, "E1195", {"start": v(-85.14, 51.42) * mm, "mid": v(-85.14, 52) * mm, "end": v(-85.55, 52.41) * mm});
            skLineSegment(sketch, "E1196", {"start": v(-98.56, 3.6) * mm, "end": v(-98.87, 3.55) * mm});
            skLineSegment(sketch, "E1197", {"start": v(-85.14, 51.42) * mm, "end": v(-85.3, 50.98) * mm});
            skLineSegment(sketch, "E1198", {"start": v(-98.87, 3.55) * mm, "end": v(-99.21, 3.47) * mm});
            skLineSegment(sketch, "E1199", {"start": v(-85.3, 50.98) * mm, "end": v(-85.35, 50.79) * mm});
            skLineSegment(sketch, "E1200", {"start": v(-99.21, 3.47) * mm, "end": v(-99.58, 3.37) * mm});
            skLineSegment(sketch, "E1201", {"start": v(-85.35, 50.79) * mm, "end": v(-85.4, 50.52) * mm});
            skLineSegment(sketch, "E1202", {"start": v(-99.58, 3.37) * mm, "end": v(-100.5, 3.03) * mm});
            skLineSegment(sketch, "E1203", {"start": v(-85.4, 50.52) * mm, "end": v(-85.44, 50.21) * mm});
            skLineSegment(sketch, "E1204", {"start": v(-100.5, 3.03) * mm, "end": v(-101.47, 2.55) * mm});
            skLineSegment(sketch, "E1205", {"start": v(-85.44, 50.21) * mm, "end": v(-85.46, 49.87) * mm});
            skArc(sketch, "E1206", {"start": v(-101.47, 2.55) * mm, "mid": v(-101.48, 1.84) * mm, "end": v(-101.47, 1.13) * mm});
            skLineSegment(sketch, "E1207", {"start": v(-85.46, 49.87) * mm, "end": v(-85.46, 49.5) * mm});
            skLineSegment(sketch, "E1208", {"start": v(-97.66, 0.07) * mm, "end": v(-98.08, 0.04) * mm});
            skLineSegment(sketch, "E1209", {"start": v(-85.46, 49.5) * mm, "end": v(-85.4, 48.53) * mm});
            skLineSegment(sketch, "E1210", {"start": v(-98.08, 0.04) * mm, "end": v(-98.29, 0.05) * mm});
            skLineSegment(sketch, "E1211", {"start": v(-85.4, 48.53) * mm, "end": v(-85.2, 47.47) * mm});
            skLineSegment(sketch, "E1212", {"start": v(-98.29, 0.05) * mm, "end": v(-98.56, 0.08) * mm});
            skArc(sketch, "E1213", {"start": v(-85.2, 47.47) * mm, "mid": v(-84.53, 47.26) * mm, "end": v(-83.85, 47.08) * mm});
            skLineSegment(sketch, "E1214", {"start": v(-98.56, 0.08) * mm, "end": v(-98.87, 0.14) * mm});
            skLineSegment(sketch, "E1215", {"start": v(-81.78, 50.43) * mm, "end": v(-81.88, 49.98) * mm});
            skLineSegment(sketch, "E1216", {"start": v(-98.87, 0.14) * mm, "end": v(-99.21, 0.22) * mm});
            skLineSegment(sketch, "E1217", {"start": v(-81.88, 49.98) * mm, "end": v(-81.94, 49.79) * mm});
            skLineSegment(sketch, "E1218", {"start": v(-99.21, 0.22) * mm, "end": v(-99.58, 0.32) * mm});
            skLineSegment(sketch, "E1219", {"start": v(-81.94, 49.79) * mm, "end": v(-82.04, 49.54) * mm});
            skLineSegment(sketch, "E1220", {"start": v(-99.58, 0.32) * mm, "end": v(-100.5, 0.66) * mm});
            skLineSegment(sketch, "E1221", {"start": v(-82.04, 49.54) * mm, "end": v(-82.18, 49.26) * mm});
            skLineSegment(sketch, "E1222", {"start": v(-100.5, 0.66) * mm, "end": v(-101.47, 1.13) * mm});
            skLineSegment(sketch, "E1223", {"start": v(-82.18, 49.26) * mm, "end": v(-82.35, 48.96) * mm});
            skArc(sketch, "E1224", {"start": v(-96.83, -0.6) * mm, "mid": v(-97.1, -0.1) * mm, "end": v(-97.66, 0.07) * mm});
            skLineSegment(sketch, "E1225", {"start": v(-82.35, 48.96) * mm, "end": v(-82.55, 48.64) * mm});
            skArc(sketch, "E1226", {"start": v(-96.83, -0.6) * mm, "mid": v(-96.79, -0.95) * mm, "end": v(-96.74, -1.3) * mm});
            skLineSegment(sketch, "E1227", {"start": v(-82.55, 48.64) * mm, "end": v(-83.13, 47.87) * mm});
            skArc(sketch, "E1228", {"start": v(-97.35, -2.17) * mm, "mid": v(-96.87, -1.86) * mm, "end": v(-96.74, -1.3) * mm});
            skLineSegment(sketch, "E1229", {"start": v(-83.13, 47.87) * mm, "end": v(-83.85, 47.08) * mm});
            skLineSegment(sketch, "E1230", {"start": v(-97.35, -2.17) * mm, "end": v(-97.77, -2.25) * mm});
            skArc(sketch, "E1231", {"start": v(-80.9, 51.04) * mm, "mid": v(-81.46, 50.92) * mm, "end": v(-81.78, 50.43) * mm});
            skLineSegment(sketch, "E1232", {"start": v(-97.77, -2.25) * mm, "end": v(-97.96, -2.32) * mm});
            skArc(sketch, "E1233", {"start": v(-80.9, 51.04) * mm, "mid": v(-80.55, 51) * mm, "end": v(-80.2, 50.94) * mm});
            skLineSegment(sketch, "E1234", {"start": v(-97.96, -2.32) * mm, "end": v(-98.22, -2.42) * mm});
            skArc(sketch, "E1235", {"start": v(-79.52, 50.1) * mm, "mid": v(-79.7, 50.66) * mm, "end": v(-80.2, 50.94) * mm});
            skLineSegment(sketch, "E1236", {"start": v(-98.22, -2.42) * mm, "end": v(-98.5, -2.56) * mm});
            skLineSegment(sketch, "E1237", {"start": v(-79.52, 50.1) * mm, "end": v(-79.56, 49.64) * mm});
            skLineSegment(sketch, "E1238", {"start": v(-98.5, -2.56) * mm, "end": v(-98.8, -2.73) * mm});
            skLineSegment(sketch, "E1239", {"start": v(-79.56, 49.64) * mm, "end": v(-79.55, 49.44) * mm});
            skLineSegment(sketch, "E1240", {"start": v(-98.8, -2.73) * mm, "end": v(-99.13, -2.92) * mm});
            skLineSegment(sketch, "E1241", {"start": v(-79.55, 49.44) * mm, "end": v(-79.52, 49.18) * mm});
            skLineSegment(sketch, "E1242", {"start": v(-99.13, -2.92) * mm, "end": v(-99.92, -3.5) * mm});
            skLineSegment(sketch, "E1243", {"start": v(-79.52, 49.18) * mm, "end": v(-79.47, 48.87) * mm});
            skLineSegment(sketch, "E1244", {"start": v(-99.92, -3.5) * mm, "end": v(-100.73, -4.22) * mm});
            skLineSegment(sketch, "E1245", {"start": v(-79.47, 48.87) * mm, "end": v(-79.4, 48.53) * mm});
            skArc(sketch, "E1246", {"start": v(-100.73, -4.22) * mm, "mid": v(-100.55, -4.9) * mm, "end": v(-100.35, -5.58) * mm});
            skLineSegment(sketch, "E1247", {"start": v(-79.4, 48.53) * mm, "end": v(-79.29, 48.17) * mm});
            skLineSegment(sketch, "E1248", {"start": v(-96.4, -5.58) * mm, "end": v(-96.8, -5.72) * mm});
            skLineSegment(sketch, "E1249", {"start": v(-79.29, 48.17) * mm, "end": v(-78.95, 47.27) * mm});
            skLineSegment(sketch, "E1250", {"start": v(-96.8, -5.72) * mm, "end": v(-97, -5.77) * mm});
            skLineSegment(sketch, "E1251", {"start": v(-78.95, 47.27) * mm, "end": v(-78.48, 46.3) * mm});
            skLineSegment(sketch, "E1252", {"start": v(-97, -5.77) * mm, "end": v(-97.27, -5.81) * mm});
            skArc(sketch, "E1253", {"start": v(-78.48, 46.3) * mm, "mid": v(-77.77, 46.3) * mm, "end": v(-77.07, 46.3) * mm});
            skLineSegment(sketch, "E1254", {"start": v(-97.27, -5.81) * mm, "end": v(-97.58, -5.84) * mm});
            skLineSegment(sketch, "E1255", {"start": v(-76.02, 50.1) * mm, "end": v(-75.99, 49.64) * mm});
            skLineSegment(sketch, "E1256", {"start": v(-97.58, -5.84) * mm, "end": v(-97.93, -5.86) * mm});
            skLineSegment(sketch, "E1257", {"start": v(-75.99, 49.64) * mm, "end": v(-76, 49.44) * mm});
            skLineSegment(sketch, "E1258", {"start": v(-97.93, -5.86) * mm, "end": v(-98.3, -5.86) * mm});
            skLineSegment(sketch, "E1259", {"start": v(-76, 49.44) * mm, "end": v(-76.02, 49.18) * mm});
            skLineSegment(sketch, "E1260", {"start": v(-98.3, -5.86) * mm, "end": v(-99.28, -5.78) * mm});
            skLineSegment(sketch, "E1261", {"start": v(-76.02, 49.18) * mm, "end": v(-76.08, 48.87) * mm});
            skLineSegment(sketch, "E1262", {"start": v(-99.28, -5.78) * mm, "end": v(-100.35, -5.58) * mm});
            skLineSegment(sketch, "E1263", {"start": v(-76.08, 48.87) * mm, "end": v(-76.15, 48.53) * mm});
            skArc(sketch, "E1264", {"start": v(-95.42, -6) * mm, "mid": v(-95.82, -5.6) * mm, "end": v(-96.4, -5.58) * mm});
            skLineSegment(sketch, "E1265", {"start": v(-76.15, 48.53) * mm, "end": v(-76.25, 48.17) * mm});
            skArc(sketch, "E1266", {"start": v(-95.42, -6) * mm, "mid": v(-95.28, -6.33) * mm, "end": v(-95.14, -6.64) * mm});
            skLineSegment(sketch, "E1267", {"start": v(-76.25, 48.17) * mm, "end": v(-76.6, 47.27) * mm});
            skArc(sketch, "E1268", {"start": v(-95.5, -7.65) * mm, "mid": v(-95.11, -7.22) * mm, "end": v(-95.14, -6.64) * mm});
            skLineSegment(sketch, "E1269", {"start": v(-76.6, 47.27) * mm, "end": v(-77.07, 46.3) * mm});
            skLineSegment(sketch, "E1270", {"start": v(-95.5, -7.65) * mm, "end": v(-95.87, -7.85) * mm});
            skArc(sketch, "E1271", {"start": v(-75.34, 50.94) * mm, "mid": v(-75.85, 50.66) * mm, "end": v(-76.02, 50.1) * mm});
            skLineSegment(sketch, "E1272", {"start": v(-95.87, -7.85) * mm, "end": v(-96.04, -7.96) * mm});
            skArc(sketch, "E1273", {"start": v(-75.34, 50.94) * mm, "mid": v(-75, 51) * mm, "end": v(-74.65, 51.04) * mm});
            skLineSegment(sketch, "E1274", {"start": v(-96.04, -7.96) * mm, "end": v(-96.26, -8.13) * mm});
            skArc(sketch, "E1275", {"start": v(-73.76, 50.43) * mm, "mid": v(-74.08, 50.92) * mm, "end": v(-74.65, 51.04) * mm});
            skLineSegment(sketch, "E1276", {"start": v(-96.26, -8.13) * mm, "end": v(-96.5, -8.34) * mm});
            skLineSegment(sketch, "E1277", {"start": v(-73.76, 50.43) * mm, "end": v(-73.67, 49.98) * mm});
            skLineSegment(sketch, "E1278", {"start": v(-96.5, -8.34) * mm, "end": v(-96.75, -8.58) * mm});
            skLineSegment(sketch, "E1279", {"start": v(-73.67, 49.98) * mm, "end": v(-73.6, 49.79) * mm});
            skLineSegment(sketch, "E1280", {"start": v(-96.75, -8.58) * mm, "end": v(-97, -8.86) * mm});
            skLineSegment(sketch, "E1281", {"start": v(-73.6, 49.79) * mm, "end": v(-73.5, 49.54) * mm});
            skLineSegment(sketch, "E1282", {"start": v(-97, -8.86) * mm, "end": v(-97.61, -9.62) * mm});
            skLineSegment(sketch, "E1283", {"start": v(-73.5, 49.54) * mm, "end": v(-73.36, 49.26) * mm});
            skLineSegment(sketch, "E1284", {"start": v(-97.61, -9.62) * mm, "end": v(-98.2, -10.54) * mm});
            skLineSegment(sketch, "E1285", {"start": v(-73.36, 49.26) * mm, "end": v(-73.2, 48.96) * mm});
            skArc(sketch, "E1286", {"start": v(-98.2, -10.54) * mm, "mid": v(-97.84, -11.15) * mm, "end": v(-97.46, -11.75) * mm});
            skLineSegment(sketch, "E1287", {"start": v(-73.2, 48.96) * mm, "end": v(-73, 48.64) * mm});
            skLineSegment(sketch, "E1288", {"start": v(-93.66, -10.68) * mm, "end": v(-94, -10.92) * mm});
            skLineSegment(sketch, "E1289", {"start": v(-73, 48.64) * mm, "end": v(-72.42, 47.87) * mm});
            skLineSegment(sketch, "E1290", {"start": v(-94, -10.92) * mm, "end": v(-94.18, -11.02) * mm});
            skLineSegment(sketch, "E1291", {"start": v(-72.42, 47.87) * mm, "end": v(-71.69, 47.08) * mm});
            skLineSegment(sketch, "E1292", {"start": v(-94.18, -11.02) * mm, "end": v(-94.43, -11.14) * mm});
            skArc(sketch, "E1293", {"start": v(-71.69, 47.08) * mm, "mid": v(-71, 47.26) * mm, "end": v(-70.34, 47.47) * mm});
            skLineSegment(sketch, "E1294", {"start": v(-94.43, -11.14) * mm, "end": v(-94.73, -11.25) * mm});
            skLineSegment(sketch, "E1295", {"start": v(-70.4, 51.42) * mm, "end": v(-70.24, 50.98) * mm});
            skLineSegment(sketch, "E1296", {"start": v(-94.73, -11.25) * mm, "end": v(-95.06, -11.36) * mm});
            skLineSegment(sketch, "E1297", {"start": v(-70.24, 50.98) * mm, "end": v(-70.2, 50.79) * mm});
            skLineSegment(sketch, "E1298", {"start": v(-95.06, -11.36) * mm, "end": v(-95.42, -11.46) * mm});
            skLineSegment(sketch, "E1299", {"start": v(-70.2, 50.79) * mm, "end": v(-70.14, 50.52) * mm});
            skLineSegment(sketch, "E1300", {"start": v(-95.42, -11.46) * mm, "end": v(-96.38, -11.65) * mm});
            skLineSegment(sketch, "E1301", {"start": v(-70.14, 50.52) * mm, "end": v(-70.1, 50.21) * mm});
            skLineSegment(sketch, "E1302", {"start": v(-96.38, -11.65) * mm, "end": v(-97.46, -11.75) * mm});
            skLineSegment(sketch, "E1303", {"start": v(-70.1, 50.21) * mm, "end": v(-70.09, 49.87) * mm});
            skArc(sketch, "E1304", {"start": v(-92.6, -10.82) * mm, "mid": v(-93.1, -10.53) * mm, "end": v(-93.66, -10.68) * mm});
            skLineSegment(sketch, "E1305", {"start": v(-70.09, 49.87) * mm, "end": v(-70.08, 49.5) * mm});
            skArc(sketch, "E1306", {"start": v(-92.6, -10.82) * mm, "mid": v(-92.38, -11.1) * mm, "end": v(-92.16, -11.36) * mm});
            skLineSegment(sketch, "E1307", {"start": v(-70.08, 49.5) * mm, "end": v(-70.15, 48.53) * mm});
            skArc(sketch, "E1308", {"start": v(-96.72, -75) * mm, "mid": v(-96.29, -74.63) * mm, "end": v(-96.22, -74.06) * mm});
            skLineSegment(sketch, "E1309", {"start": v(-70.15, 48.53) * mm, "end": v(-70.34, 47.47) * mm});
            skLineSegment(sketch, "E1310", {"start": v(-96.72, -75) * mm, "end": v(-97.11, -75.13) * mm});
            skArc(sketch, "E1311", {"start": v(-70, 52.41) * mm, "mid": v(-70.4, 52) * mm, "end": v(-70.4, 51.42) * mm});
            skLineSegment(sketch, "E1312", {"start": v(-97.11, -75.13) * mm, "end": v(-97.37, -75.26) * mm});
            skArc(sketch, "E1313", {"start": v(-70, 52.41) * mm, "mid": v(-69.67, 52.55) * mm, "end": v(-69.35, 52.7) * mm});
            skLineSegment(sketch, "E1314", {"start": v(-97.37, -75.26) * mm, "end": v(-97.69, -75.44) * mm});
            skArc(sketch, "E1315", {"start": v(-68.33, 52.36) * mm, "mid": v(-68.77, 52.74) * mm, "end": v(-69.35, 52.7) * mm});
            skLineSegment(sketch, "E1316", {"start": v(-97.69, -75.44) * mm, "end": v(-98.03, -75.68) * mm});
            skLineSegment(sketch, "E1317", {"start": v(-68.33, 52.36) * mm, "end": v(-68.1, 51.96) * mm});
            skLineSegment(sketch, "E1318", {"start": v(-98.03, -75.68) * mm, "end": v(-98.38, -75.96) * mm});
            skLineSegment(sketch, "E1319", {"start": v(-68.1, 51.96) * mm, "end": v(-68, 51.8) * mm});
            skLineSegment(sketch, "E1320", {"start": v(-98.38, -75.96) * mm, "end": v(-99.1, -76.63) * mm});
            skLineSegment(sketch, "E1321", {"start": v(-68, 51.8) * mm, "end": v(-67.83, 51.58) * mm});
            skLineSegment(sketch, "E1322", {"start": v(-99.1, -76.63) * mm, "end": v(-99.83, -77.44) * mm});
            skLineSegment(sketch, "E1323", {"start": v(-67.83, 51.58) * mm, "end": v(-67.61, 51.35) * mm});
            skArc(sketch, "E1324", {"start": v(-99.83, -77.44) * mm, "mid": v(-99.57, -78.1) * mm, "end": v(-99.29, -78.76) * mm});
            skLineSegment(sketch, "E1325", {"start": v(-67.61, 51.35) * mm, "end": v(-67.37, 51.11) * mm});
            skLineSegment(sketch, "E1326", {"start": v(-95.36, -78.3) * mm, "end": v(-95.73, -78.48) * mm});
            skLineSegment(sketch, "E1327", {"start": v(-67.37, 51.11) * mm, "end": v(-67.09, 50.86) * mm});
            skLineSegment(sketch, "E1328", {"start": v(-95.73, -78.48) * mm, "end": v(-96, -78.57) * mm});
            skLineSegment(sketch, "E1329", {"start": v(-67.09, 50.86) * mm, "end": v(-66.31, 50.28) * mm});
            skLineSegment(sketch, "E1330", {"start": v(-96, -78.57) * mm, "end": v(-96.35, -78.66) * mm});
            skLineSegment(sketch, "E1331", {"start": v(-66.31, 50.28) * mm, "end": v(-65.4, 49.73) * mm});
            skLineSegment(sketch, "E1332", {"start": v(-96.35, -78.66) * mm, "end": v(-96.76, -78.73) * mm});
            skArc(sketch, "E1333", {"start": v(-65.4, 49.73) * mm, "mid": v(-64.8, 50.1) * mm, "end": v(-64.2, 50.5) * mm});
            skLineSegment(sketch, "E1334", {"start": v(-96.76, -78.73) * mm, "end": v(-97.21, -78.79) * mm});
            skLineSegment(sketch, "E1335", {"start": v(-65.39, 54.26) * mm, "end": v(-65.1, 53.88) * mm});
            skLineSegment(sketch, "E1336", {"start": v(-97.21, -78.79) * mm, "end": v(-98.2, -78.83) * mm});
            skLineSegment(sketch, "E1337", {"start": v(-65.1, 53.88) * mm, "end": v(-65, 53.71) * mm});
            skLineSegment(sketch, "E1338", {"start": v(-98.2, -78.83) * mm, "end": v(-99.29, -78.76) * mm});
            skLineSegment(sketch, "E1339", {"start": v(-65, 53.71) * mm, "end": v(-64.88, 53.47) * mm});
            skArc(sketch, "E1340", {"start": v(-94.34, -78.6) * mm, "mid": v(-94.79, -78.25) * mm, "end": v(-95.36, -78.3) * mm});
            skLineSegment(sketch, "E1341", {"start": v(-64.88, 53.47) * mm, "end": v(-64.76, 53.19) * mm});
            skArc(sketch, "E1342", {"start": v(-94.34, -78.6) * mm, "mid": v(-94.17, -78.9) * mm, "end": v(-94, -79.2) * mm});
            skLineSegment(sketch, "E1343", {"start": v(-64.76, 53.19) * mm, "end": v(-64.64, 52.86) * mm});
            skArc(sketch, "E1344", {"start": v(-94.23, -80.24) * mm, "mid": v(-93.9, -79.77) * mm, "end": v(-94, -79.2) * mm});
            skLineSegment(sketch, "E1345", {"start": v(-64.64, 52.86) * mm, "end": v(-64.54, 52.5) * mm});
            skLineSegment(sketch, "E1346", {"start": v(-94.23, -80.24) * mm, "end": v(-94.58, -80.47) * mm});
            skLineSegment(sketch, "E1347", {"start": v(-64.54, 52.5) * mm, "end": v(-64.33, 51.56) * mm});
            skLineSegment(sketch, "E1348", {"start": v(-94.58, -80.47) * mm, "end": v(-94.8, -80.67) * mm});
            skLineSegment(sketch, "E1349", {"start": v(-64.33, 51.56) * mm, "end": v(-64.2, 50.5) * mm});
            skLineSegment(sketch, "E1350", {"start": v(-94.8, -80.67) * mm, "end": v(-95.05, -80.93) * mm});
            skArc(sketch, "E1351", {"start": v(-65.27, 55.33) * mm, "mid": v(-65.54, 54.81) * mm, "end": v(-65.39, 54.26) * mm});
            skLineSegment(sketch, "E1352", {"start": v(-95.05, -80.93) * mm, "end": v(-95.31, -81.24) * mm});
            skArc(sketch, "E1353", {"start": v(-65.27, 55.33) * mm, "mid": v(-65, 55.56) * mm, "end": v(-64.74, 55.79) * mm});
            skLineSegment(sketch, "E1354", {"start": v(-95.31, -81.24) * mm, "end": v(-95.59, -81.6) * mm});
            skArc(sketch, "E1355", {"start": v(-63.66, 55.75) * mm, "mid": v(-64.2, 55.99) * mm, "end": v(-64.74, 55.79) * mm});
            skLineSegment(sketch, "E1356", {"start": v(-95.59, -81.6) * mm, "end": v(-96.11, -82.44) * mm});
            skLineSegment(sketch, "E1357", {"start": v(-63.66, 55.75) * mm, "end": v(-63.33, 55.42) * mm});
            skLineSegment(sketch, "E1358", {"start": v(-96.11, -82.44) * mm, "end": v(-96.6, -83.41) * mm});
            skLineSegment(sketch, "E1359", {"start": v(-63.33, 55.42) * mm, "end": v(-63.18, 55.3) * mm});
            skArc(sketch, "E1360", {"start": v(-96.6, -83.41) * mm, "mid": v(-96.18, -83.99) * mm, "end": v(-95.73, -84.55) * mm});
            skLineSegment(sketch, "E1361", {"start": v(-63.18, 55.3) * mm, "end": v(-62.96, 55.14) * mm});
            skLineSegment(sketch, "E1362", {"start": v(-92.06, -83.08) * mm, "end": v(-92.37, -83.35) * mm});
            skLineSegment(sketch, "E1363", {"start": v(-62.96, 55.14) * mm, "end": v(-62.69, 54.98) * mm});
            skLineSegment(sketch, "E1364", {"start": v(-92.37, -83.35) * mm, "end": v(-92.61, -83.5) * mm});
            skLineSegment(sketch, "E1365", {"start": v(-62.69, 54.98) * mm, "end": v(-62.39, 54.82) * mm});
            skLineSegment(sketch, "E1366", {"start": v(-92.61, -83.5) * mm, "end": v(-92.93, -83.68) * mm});
            skLineSegment(sketch, "E1367", {"start": v(-62.39, 54.82) * mm, "end": v(-62.05, 54.66) * mm});
            skLineSegment(sketch, "E1368", {"start": v(-92.93, -83.68) * mm, "end": v(-93.3, -83.86) * mm});
            skLineSegment(sketch, "E1369", {"start": v(-62.05, 54.66) * mm, "end": v(-61.14, 54.32) * mm});
            skLineSegment(sketch, "E1370", {"start": v(-93.3, -83.86) * mm, "end": v(-93.72, -84.03) * mm});
            skLineSegment(sketch, "E1371", {"start": v(-61.14, 54.32) * mm, "end": v(-60.1, 54.05) * mm});
            skLineSegment(sketch, "E1372", {"start": v(-93.72, -84.03) * mm, "end": v(-94.66, -84.32) * mm});
            skArc(sketch, "E1373", {"start": v(-60.1, 54.05) * mm, "mid": v(-59.63, 54.58) * mm, "end": v(-59.18, 55.11) * mm});
            skLineSegment(sketch, "E1374", {"start": v(-94.66, -84.32) * mm, "end": v(-95.73, -84.55) * mm});
            skLineSegment(sketch, "E1375", {"start": v(-61.37, 58.4) * mm, "end": v(-61, 58.12) * mm});
            skArc(sketch, "E1376", {"start": v(-91, -83.11) * mm, "mid": v(-91.52, -82.88) * mm, "end": v(-92.06, -83.08) * mm});
            skLineSegment(sketch, "E1377", {"start": v(-61, 58.12) * mm, "end": v(-60.85, 57.98) * mm});
            skArc(sketch, "E1378", {"start": v(-91, -83.11) * mm, "mid": v(-90.75, -83.36) * mm, "end": v(-90.5, -83.6) * mm});
            skLineSegment(sketch, "E1379", {"start": v(-60.85, 57.98) * mm, "end": v(-60.67, 57.78) * mm});
            skArc(sketch, "E1380", {"start": v(-90.47, -84.66) * mm, "mid": v(-90.27, -84.13) * mm, "end": v(-90.5, -83.6) * mm});
            skLineSegment(sketch, "E1381", {"start": v(-60.67, 57.78) * mm, "end": v(-60.47, 57.54) * mm});
            skLineSegment(sketch, "E1382", {"start": v(-90.47, -84.66) * mm, "end": v(-90.74, -84.98) * mm});
            skLineSegment(sketch, "E1383", {"start": v(-60.47, 57.54) * mm, "end": v(-60.27, 57.27) * mm});
            skLineSegment(sketch, "E1384", {"start": v(-90.74, -84.98) * mm, "end": v(-90.9, -85.22) * mm});
            skLineSegment(sketch, "E1385", {"start": v(-60.27, 57.27) * mm, "end": v(-60.06, 56.95) * mm});
            skLineSegment(sketch, "E1386", {"start": v(-90.9, -85.22) * mm, "end": v(-91.08, -85.54) * mm});
            skLineSegment(sketch, "E1387", {"start": v(-60.06, 56.95) * mm, "end": v(-59.6, 56.1) * mm});
            skLineSegment(sketch, "E1388", {"start": v(-91.08, -85.54) * mm, "end": v(-91.25, -85.9) * mm});
            skLineSegment(sketch, "E1389", {"start": v(-59.6, 56.1) * mm, "end": v(-59.18, 55.11) * mm});
            skLineSegment(sketch, "E1390", {"start": v(-91.25, -85.9) * mm, "end": v(-91.42, -86.33) * mm});
            skArc(sketch, "E1391", {"start": v(-61.56, 59.46) * mm, "mid": v(-61.68, 58.89) * mm, "end": v(-61.37, 58.4) * mm});
            skLineSegment(sketch, "E1392", {"start": v(-91.42, -86.33) * mm, "end": v(-91.72, -87.27) * mm});
            skArc(sketch, "E1393", {"start": v(-61.56, 59.46) * mm, "mid": v(-61.37, 59.75) * mm, "end": v(-61.18, 60.05) * mm});
            skLineSegment(sketch, "E1394", {"start": v(-91.72, -87.27) * mm, "end": v(-91.94, -88.34) * mm});
            skArc(sketch, "E1395", {"start": v(-60.14, 60.32) * mm, "mid": v(-60.71, 60.4) * mm, "end": v(-61.18, 60.05) * mm});
            skArc(sketch, "E1396", {"start": v(-91.94, -88.34) * mm, "mid": v(-91.38, -88.78) * mm, "end": v(-90.8, -89.21) * mm});
            skLineSegment(sketch, "E1397", {"start": v(-60.14, 60.32) * mm, "end": v(-59.73, 60.1) * mm});
            skLineSegment(sketch, "E1398", {"start": v(-87.63, -86.84) * mm, "end": v(-87.86, -87.18) * mm});
            skLineSegment(sketch, "E1399", {"start": v(-59.73, 60.1) * mm, "end": v(-59.54, 60.01) * mm});
            skLineSegment(sketch, "E1400", {"start": v(-87.86, -87.18) * mm, "end": v(-88.06, -87.4) * mm});
            skLineSegment(sketch, "E1401", {"start": v(-59.54, 60.01) * mm, "end": v(-59.29, 59.93) * mm});
            skLineSegment(sketch, "E1402", {"start": v(-88.06, -87.4) * mm, "end": v(-88.32, -87.65) * mm});
            skLineSegment(sketch, "E1403", {"start": v(-59.29, 59.93) * mm, "end": v(-58.99, 59.85) * mm});
            skLineSegment(sketch, "E1404", {"start": v(-88.32, -87.65) * mm, "end": v(-88.63, -87.92) * mm});
            skLineSegment(sketch, "E1405", {"start": v(-58.99, 59.85) * mm, "end": v(-58.65, 59.78) * mm});
            skLineSegment(sketch, "E1406", {"start": v(-88.63, -87.92) * mm, "end": v(-89, -88.2) * mm});
            skLineSegment(sketch, "E1407", {"start": v(-58.65, 59.78) * mm, "end": v(-58.28, 59.72) * mm});
            skLineSegment(sketch, "E1408", {"start": v(-89, -88.2) * mm, "end": v(-89.83, -88.72) * mm});
            skLineSegment(sketch, "E1409", {"start": v(-58.28, 59.72) * mm, "end": v(-57.32, 59.65) * mm});
            skLineSegment(sketch, "E1410", {"start": v(-89.83, -88.72) * mm, "end": v(-90.8, -89.21) * mm});
            skLineSegment(sketch, "E1411", {"start": v(-57.32, 59.65) * mm, "end": v(-56.24, 59.69) * mm});
            skArc(sketch, "E1412", {"start": v(-86.6, -86.6) * mm, "mid": v(-87.16, -86.51) * mm, "end": v(-87.63, -86.84) * mm});
            skArc(sketch, "E1413", {"start": v(-56.24, 59.69) * mm, "mid": v(-55.94, 60.32) * mm, "end": v(-55.66, 60.97) * mm});
            skArc(sketch, "E1414", {"start": v(-86.6, -86.6) * mm, "mid": v(-86.3, -86.78) * mm, "end": v(-86, -86.95) * mm});
            skLineSegment(sketch, "E1415", {"start": v(-58.68, 63.5) * mm, "end": v(-58.25, 63.34) * mm});
            skArc(sketch, "E1416", {"start": v(-85.69, -87.96) * mm, "mid": v(-85.64, -87.4) * mm, "end": v(-86, -86.95) * mm});
            skLineSegment(sketch, "E1417", {"start": v(-58.25, 63.34) * mm, "end": v(-58.07, 63.25) * mm});
            skLineSegment(sketch, "E1418", {"start": v(-85.69, -87.96) * mm, "end": v(-85.87, -88.34) * mm});
            skLineSegment(sketch, "E1419", {"start": v(-58.07, 63.25) * mm, "end": v(-57.84, 63.11) * mm});
            skLineSegment(sketch, "E1420", {"start": v(-85.87, -88.34) * mm, "end": v(-85.96, -88.61) * mm});
            skLineSegment(sketch, "E1421", {"start": v(-57.84, 63.11) * mm, "end": v(-57.58, 62.93) * mm});
            skLineSegment(sketch, "E1422", {"start": v(-85.96, -88.61) * mm, "end": v(-86.05, -88.96) * mm});
            skLineSegment(sketch, "E1423", {"start": v(-57.58, 62.93) * mm, "end": v(-57.3, 62.72) * mm});
            skLineSegment(sketch, "E1424", {"start": v(-86.05, -88.96) * mm, "end": v(-86.12, -89.37) * mm});
            skLineSegment(sketch, "E1425", {"start": v(-57.3, 62.72) * mm, "end": v(-57.02, 62.48) * mm});
            skLineSegment(sketch, "E1426", {"start": v(-86.12, -89.37) * mm, "end": v(-86.18, -89.82) * mm});
            skLineSegment(sketch, "E1427", {"start": v(-57.02, 62.48) * mm, "end": v(-56.34, 61.8) * mm});
            skLineSegment(sketch, "E1428", {"start": v(-86.18, -89.82) * mm, "end": v(-86.22, -90.8) * mm});
            skLineSegment(sketch, "E1429", {"start": v(-56.34, 61.8) * mm, "end": v(-55.66, 60.97) * mm});
            skLineSegment(sketch, "E1430", {"start": v(-86.22, -90.8) * mm, "end": v(-86.16, -91.9) * mm});
            skArc(sketch, "E1431", {"start": v(-59.16, 64.46) * mm, "mid": v(-59.12, 63.88) * mm, "end": v(-58.68, 63.5) * mm});
            skArc(sketch, "E1432", {"start": v(-86.16, -91.9) * mm, "mid": v(-85.5, -92.18) * mm, "end": v(-84.84, -92.44) * mm});
            skArc(sketch, "E1433", {"start": v(-59.16, 64.46) * mm, "mid": v(-59.06, 64.8) * mm, "end": v(-58.97, 65.14) * mm});
            skLineSegment(sketch, "E1434", {"start": v(-82.38, -89.33) * mm, "end": v(-82.52, -89.72) * mm});
            skArc(sketch, "E1435", {"start": v(-58.04, 65.69) * mm, "mid": v(-58.61, 65.6) * mm, "end": v(-58.97, 65.14) * mm});
            skLineSegment(sketch, "E1436", {"start": v(-82.52, -89.72) * mm, "end": v(-82.65, -89.98) * mm});
            skLineSegment(sketch, "E1437", {"start": v(-58.04, 65.69) * mm, "end": v(-57.59, 65.59) * mm});
            skLineSegment(sketch, "E1438", {"start": v(-82.65, -89.98) * mm, "end": v(-82.84, -90.3) * mm});
            skLineSegment(sketch, "E1439", {"start": v(-57.59, 65.59) * mm, "end": v(-57.39, 65.57) * mm});
            skLineSegment(sketch, "E1440", {"start": v(-82.84, -90.3) * mm, "end": v(-83.07, -90.63) * mm});
            skLineSegment(sketch, "E1441", {"start": v(-57.39, 65.57) * mm, "end": v(-57.12, 65.56) * mm});
            skLineSegment(sketch, "E1442", {"start": v(-83.07, -90.63) * mm, "end": v(-83.35, -91) * mm});
            skLineSegment(sketch, "E1443", {"start": v(-57.12, 65.56) * mm, "end": v(-56.8, 65.56) * mm});
            skLineSegment(sketch, "E1444", {"start": v(-83.35, -91) * mm, "end": v(-84.02, -91.72) * mm});
            skLineSegment(sketch, "E1445", {"start": v(-56.8, 65.56) * mm, "end": v(-56.46, 65.6) * mm});
            skLineSegment(sketch, "E1446", {"start": v(-84.02, -91.72) * mm, "end": v(-84.84, -92.44) * mm});
            skLineSegment(sketch, "E1447", {"start": v(-56.46, 65.6) * mm, "end": v(-56.1, 65.64) * mm});
            skArc(sketch, "E1448", {"start": v(-81.45, -88.83) * mm, "mid": v(-82.02, -88.9) * mm, "end": v(-82.38, -89.33) * mm});
            skLineSegment(sketch, "E1449", {"start": v(-56.1, 65.64) * mm, "end": v(-55.15, 65.85) * mm});
            skArc(sketch, "E1450", {"start": v(-81.45, -88.83) * mm, "mid": v(-81.11, -88.93) * mm, "end": v(-80.78, -89.01) * mm});
            skLineSegment(sketch, "E1451", {"start": v(-55.15, 65.85) * mm, "end": v(-54.13, 66.18) * mm});
            skArc(sketch, "E1452", {"start": v(-80.22, -89.91) * mm, "mid": v(-80.32, -89.35) * mm, "end": v(-80.78, -89.01) * mm});
            skArc(sketch, "E1453", {"start": v(-54.13, 66.18) * mm, "mid": v(-54.02, 66.88) * mm, "end": v(-53.93, 67.58) * mm});
            skLineSegment(sketch, "E1454", {"start": v(-80.22, -89.91) * mm, "end": v(-80.3, -90.32) * mm});
            skLineSegment(sketch, "E1455", {"start": v(-57.54, 69.15) * mm, "end": v(-57.08, 69.12) * mm});
            skLineSegment(sketch, "E1456", {"start": v(-80.3, -90.32) * mm, "end": v(-80.31, -90.6) * mm});
            skLineSegment(sketch, "E1457", {"start": v(-57.08, 69.12) * mm, "end": v(-56.88, 69.08) * mm});
            skLineSegment(sketch, "E1458", {"start": v(-80.31, -90.6) * mm, "end": v(-80.3, -90.97) * mm});
            skLineSegment(sketch, "E1459", {"start": v(-56.88, 69.08) * mm, "end": v(-56.62, 69.02) * mm});
            skLineSegment(sketch, "E1460", {"start": v(-80.3, -90.97) * mm, "end": v(-80.27, -91.38) * mm});
            skLineSegment(sketch, "E1461", {"start": v(-56.62, 69.02) * mm, "end": v(-56.32, 68.92) * mm});
            skLineSegment(sketch, "E1462", {"start": v(-80.27, -91.38) * mm, "end": v(-80.2, -91.83) * mm});
            skLineSegment(sketch, "E1463", {"start": v(-56.32, 68.92) * mm, "end": v(-56, 68.8) * mm});
            skLineSegment(sketch, "E1464", {"start": v(-80.2, -91.83) * mm, "end": v(-80, -92.8) * mm});
            skLineSegment(sketch, "E1465", {"start": v(-56, 68.8) * mm, "end": v(-55.66, 68.65) * mm});
            skLineSegment(sketch, "E1466", {"start": v(-80, -92.8) * mm, "end": v(-79.65, -93.83) * mm});
            skLineSegment(sketch, "E1467", {"start": v(-55.66, 68.65) * mm, "end": v(-54.81, 68.18) * mm});
            skArc(sketch, "E1468", {"start": v(-79.65, -93.83) * mm, "mid": v(-78.94, -93.94) * mm, "end": v(-78.23, -94.02) * mm});
            skLineSegment(sketch, "E1469", {"start": v(-54.81, 68.18) * mm, "end": v(-53.93, 67.58) * mm});
            skLineSegment(sketch, "E1470", {"start": v(-76.67, -90.38) * mm, "end": v(-76.7, -90.8) * mm});
            skArc(sketch, "E1471", {"start": v(-58.27, 69.94) * mm, "mid": v(-58.07, 69.4) * mm, "end": v(-57.54, 69.15) * mm});
            skLineSegment(sketch, "E1472", {"start": v(-76.7, -90.8) * mm, "end": v(-76.76, -91.08) * mm});
            skArc(sketch, "E1473", {"start": v(-58.27, 69.94) * mm, "mid": v(-58.27, 70.3) * mm, "end": v(-58.27, 70.64) * mm});
            skLineSegment(sketch, "E1474", {"start": v(-76.76, -91.08) * mm, "end": v(-76.86, -91.43) * mm});
            skArc(sketch, "E1475", {"start": v(-57.54, 71.43) * mm, "mid": v(-58.07, 71.19) * mm, "end": v(-58.27, 70.64) * mm});
            skLineSegment(sketch, "E1476", {"start": v(-76.86, -91.43) * mm, "end": v(-77, -91.81) * mm});
            skLineSegment(sketch, "E1477", {"start": v(-57.54, 71.43) * mm, "end": v(-57.08, 71.46) * mm});
            skLineSegment(sketch, "E1478", {"start": v(-77, -91.81) * mm, "end": v(-77.18, -92.23) * mm});
            skLineSegment(sketch, "E1479", {"start": v(-57.08, 71.46) * mm, "end": v(-56.88, 71.5) * mm});
            skLineSegment(sketch, "E1480", {"start": v(-77.18, -92.23) * mm, "end": v(-77.63, -93.1) * mm});
            skLineSegment(sketch, "E1481", {"start": v(-56.88, 71.5) * mm, "end": v(-56.62, 71.57) * mm});
            skLineSegment(sketch, "E1482", {"start": v(-77.63, -93.1) * mm, "end": v(-78.23, -94.02) * mm});
            skLineSegment(sketch, "E1483", {"start": v(-56.62, 71.57) * mm, "end": v(-56.32, 71.66) * mm});
            skArc(sketch, "E1484", {"start": v(-75.9, -89.66) * mm, "mid": v(-76.43, -89.86) * mm, "end": v(-76.67, -90.38) * mm});
            skLineSegment(sketch, "E1485", {"start": v(-56.32, 71.66) * mm, "end": v(-56, 71.79) * mm});
            skArc(sketch, "E1486", {"start": v(-75.9, -89.66) * mm, "mid": v(-75.55, -89.66) * mm, "end": v(-75.2, -89.66) * mm});
            skLineSegment(sketch, "E1487", {"start": v(-56, 71.79) * mm, "end": v(-55.66, 71.94) * mm});
            skArc(sketch, "E1488", {"start": v(-74.43, -90.38) * mm, "mid": v(-74.67, -89.86) * mm, "end": v(-75.2, -89.66) * mm});
            skLineSegment(sketch, "E1489", {"start": v(-55.66, 71.94) * mm, "end": v(-54.81, 72.4) * mm});
            skLineSegment(sketch, "E1490", {"start": v(-74.43, -90.38) * mm, "end": v(-74.4, -90.8) * mm});
            skLineSegment(sketch, "E1491", {"start": v(-54.81, 72.4) * mm, "end": v(-53.93, 73) * mm});
            skLineSegment(sketch, "E1492", {"start": v(-74.4, -90.8) * mm, "end": v(-74.34, -91.08) * mm});
            skArc(sketch, "E1493", {"start": v(-53.93, 73) * mm, "mid": v(-54.02, 73.7) * mm, "end": v(-54.13, 74.4) * mm});
            skLineSegment(sketch, "E1494", {"start": v(-74.34, -91.08) * mm, "end": v(-74.24, -91.43) * mm});
            skLineSegment(sketch, "E1495", {"start": v(-58.04, 74.9) * mm, "end": v(-57.59, 75) * mm});
            skLineSegment(sketch, "E1496", {"start": v(-74.24, -91.43) * mm, "end": v(-74.1, -91.81) * mm});
            skLineSegment(sketch, "E1497", {"start": v(-57.59, 75) * mm, "end": v(-57.39, 75.02) * mm});
            skLineSegment(sketch, "E1498", {"start": v(-74.1, -91.81) * mm, "end": v(-73.92, -92.23) * mm});
            skLineSegment(sketch, "E1499", {"start": v(-57.39, 75.02) * mm, "end": v(-57.12, 75.03) * mm});
            skLineSegment(sketch, "E1500", {"start": v(-73.92, -92.23) * mm, "end": v(-73.46, -93.1) * mm});
            skLineSegment(sketch, "E1501", {"start": v(-57.12, 75.03) * mm, "end": v(-56.8, 75.02) * mm});
            skLineSegment(sketch, "E1502", {"start": v(-56.8, 75.02) * mm, "end": v(-56.46, 75) * mm});
            skLineSegment(sketch, "E1503", {"start": v(-56.46, 75) * mm, "end": v(-56.1, 74.94) * mm});
            skLineSegment(sketch, "E1504", {"start": v(-56.1, 74.94) * mm, "end": v(-55.15, 74.74) * mm});
            skLineSegment(sketch, "E1505", {"start": v(-55.15, 74.74) * mm, "end": v(-54.13, 74.4) * mm});
            skArc(sketch, "E1506", {"start": v(-58.97, 75.45) * mm, "mid": v(-58.61, 74.99) * mm, "end": v(-58.04, 74.9) * mm});
            skArc(sketch, "E1507", {"start": v(-58.97, 75.45) * mm, "mid": v(-59.06, 75.79) * mm, "end": v(-59.16, 76.12) * mm});
            skArc(sketch, "E1508", {"start": v(-58.68, 77.09) * mm, "mid": v(-59.12, 76.7) * mm, "end": v(-59.16, 76.12) * mm});
            skLineSegment(sketch, "E1509", {"start": v(-97.96, 65.59) * mm, "end": v(-98.16, 65.57) * mm});
            skLineSegment(sketch, "E1510", {"start": v(-98.16, 65.57) * mm, "end": v(-98.42, 65.56) * mm});
            skLineSegment(sketch, "E1511", {"start": v(-98.42, 65.56) * mm, "end": v(-98.74, 65.56) * mm});
            skLineSegment(sketch, "E1512", {"start": v(-98.74, 65.56) * mm, "end": v(-99.08, 65.6) * mm});
            skLineSegment(sketch, "E1513", {"start": v(-99.08, 65.6) * mm, "end": v(-99.45, 65.64) * mm});
            skLineSegment(sketch, "E1514", {"start": v(-99.45, 65.64) * mm, "end": v(-100.4, 65.85) * mm});
            skLineSegment(sketch, "E1515", {"start": v(-100.4, 65.85) * mm, "end": v(-101.42, 66.18) * mm});
            skArc(sketch, "E1516", {"start": v(-96.58, 65.14) * mm, "mid": v(-96.93, 65.6) * mm, "end": v(-97.5, 65.69) * mm});
            skArc(sketch, "E1517", {"start": v(-96.58, 65.14) * mm, "mid": v(-96.48, 64.8) * mm, "end": v(-96.38, 64.46) * mm});
            skArc(sketch, "E1518", {"start": v(-96.86, 63.5) * mm, "mid": v(-96.43, 63.88) * mm, "end": v(-96.38, 64.46) * mm});
            skLineSegment(sketch, "E1519", {"start": v(-96.86, 63.5) * mm, "end": v(-97.3, 63.34) * mm});
            skLineSegment(sketch, "E1520", {"start": v(-97.3, 63.34) * mm, "end": v(-97.48, 63.25) * mm});
            skLineSegment(sketch, "E1521", {"start": v(-97.48, 63.25) * mm, "end": v(-97.7, 63.11) * mm});
            skLineSegment(sketch, "E1522", {"start": v(-97.7, 63.11) * mm, "end": v(-97.97, 62.93) * mm});
            skLineSegment(sketch, "E1523", {"start": v(-97.97, 62.93) * mm, "end": v(-98.24, 62.72) * mm});
            skLineSegment(sketch, "E1524", {"start": v(-98.24, 62.72) * mm, "end": v(-98.52, 62.48) * mm});
            skLineSegment(sketch, "E1525", {"start": v(-98.52, 62.48) * mm, "end": v(-99.2, 61.8) * mm});
            skLineSegment(sketch, "E1526", {"start": v(-99.2, 61.8) * mm, "end": v(-99.89, 60.97) * mm});
            skArc(sketch, "E1527", {"start": v(-99.89, 60.97) * mm, "mid": v(-99.6, 60.32) * mm, "end": v(-99.3, 59.69) * mm});
            skLineSegment(sketch, "E1528", {"start": v(-95.4, 60.32) * mm, "end": v(-95.81, 60.1) * mm});
            skLineSegment(sketch, "E1529", {"start": v(-95.81, 60.1) * mm, "end": v(-96, 60.01) * mm});
            skLineSegment(sketch, "E1530", {"start": v(-96, 60.01) * mm, "end": v(-96.25, 59.93) * mm});
            skLineSegment(sketch, "E1531", {"start": v(-96.25, 59.93) * mm, "end": v(-96.56, 59.85) * mm});
            skLineSegment(sketch, "E1532", {"start": v(-96.56, 59.85) * mm, "end": v(-96.9, 59.78) * mm});
            skLineSegment(sketch, "E1533", {"start": v(-96.9, 59.78) * mm, "end": v(-97.26, 59.72) * mm});
            skLineSegment(sketch, "E1534", {"start": v(-97.26, 59.72) * mm, "end": v(-98.23, 59.65) * mm});
            skLineSegment(sketch, "E1535", {"start": v(-98.23, 59.65) * mm, "end": v(-99.3, 59.69) * mm});
            skArc(sketch, "E1536", {"start": v(-94.36, 60.05) * mm, "mid": v(-94.83, 60.4) * mm, "end": v(-95.4, 60.32) * mm});
            skArc(sketch, "E1537", {"start": v(-94.36, 60.05) * mm, "mid": v(-94.18, 59.75) * mm, "end": v(-93.98, 59.46) * mm});
            skArc(sketch, "E1538", {"start": v(-94.17, 58.4) * mm, "mid": v(-93.86, 58.89) * mm, "end": v(-93.98, 59.46) * mm});
            skLineSegment(sketch, "E1539", {"start": v(-94.17, 58.4) * mm, "end": v(-94.55, 58.12) * mm});
            skLineSegment(sketch, "E1540", {"start": v(-94.55, 58.12) * mm, "end": v(-94.7, 57.98) * mm});
            skLineSegment(sketch, "E1541", {"start": v(-94.7, 57.98) * mm, "end": v(-94.88, 57.78) * mm});
            skLineSegment(sketch, "E1542", {"start": v(-94.88, 57.78) * mm, "end": v(-95.07, 57.54) * mm});
            skLineSegment(sketch, "E1543", {"start": v(-95.07, 57.54) * mm, "end": v(-95.28, 57.27) * mm});
            skLineSegment(sketch, "E1544", {"start": v(-95.28, 57.27) * mm, "end": v(-95.48, 56.95) * mm});
            skLineSegment(sketch, "E1545", {"start": v(-95.48, 56.95) * mm, "end": v(-95.95, 56.1) * mm});
            skLineSegment(sketch, "E1546", {"start": v(-95.95, 56.1) * mm, "end": v(-96.36, 55.11) * mm});
            skArc(sketch, "E1547", {"start": v(-96.36, 55.11) * mm, "mid": v(-95.9, 54.58) * mm, "end": v(-95.44, 54.05) * mm});
            skLineSegment(sketch, "E1548", {"start": v(-91.88, 55.75) * mm, "end": v(-92.2, 55.42) * mm});
            skLineSegment(sketch, "E1549", {"start": v(-92.2, 55.42) * mm, "end": v(-92.36, 55.3) * mm});
            skLineSegment(sketch, "E1550", {"start": v(-92.36, 55.3) * mm, "end": v(-92.59, 55.14) * mm});
            skLineSegment(sketch, "E1551", {"start": v(-92.59, 55.14) * mm, "end": v(-92.85, 54.98) * mm});
            skLineSegment(sketch, "E1552", {"start": v(-92.85, 54.98) * mm, "end": v(-93.16, 54.82) * mm});
            skLineSegment(sketch, "E1553", {"start": v(-93.16, 54.82) * mm, "end": v(-93.5, 54.66) * mm});
            skLineSegment(sketch, "E1554", {"start": v(-93.5, 54.66) * mm, "end": v(-94.4, 54.32) * mm});
            skLineSegment(sketch, "E1555", {"start": v(-94.4, 54.32) * mm, "end": v(-95.44, 54.05) * mm});
            skArc(sketch, "E1556", {"start": v(-90.8, 55.79) * mm, "mid": v(-91.35, 55.99) * mm, "end": v(-91.88, 55.75) * mm});
            skArc(sketch, "E1557", {"start": v(-90.8, 55.79) * mm, "mid": v(-90.54, 55.56) * mm, "end": v(-90.27, 55.33) * mm});
            skArc(sketch, "E1558", {"start": v(-92.23, -12.43) * mm, "mid": v(-91.98, -11.91) * mm, "end": v(-92.16, -11.36) * mm});
            skLineSegment(sketch, "E1559", {"start": v(-92.23, -12.43) * mm, "end": v(-92.54, -12.72) * mm});
            skLineSegment(sketch, "E1560", {"start": v(-92.54, -12.72) * mm, "end": v(-92.67, -12.88) * mm});
            skLineSegment(sketch, "E1561", {"start": v(-92.67, -12.88) * mm, "end": v(-92.84, -13.1) * mm});
            skLineSegment(sketch, "E1562", {"start": v(-92.84, -13.1) * mm, "end": v(-93, -13.36) * mm});
            skLineSegment(sketch, "E1563", {"start": v(-93, -13.36) * mm, "end": v(-93.18, -13.66) * mm});
            skLineSegment(sketch, "E1564", {"start": v(-93.18, -13.66) * mm, "end": v(-93.36, -14) * mm});
            skLineSegment(sketch, "E1565", {"start": v(-93.36, -14) * mm, "end": v(-93.73, -14.9) * mm});
            skLineSegment(sketch, "E1566", {"start": v(-93.73, -14.9) * mm, "end": v(-94.05, -15.94) * mm});
            skArc(sketch, "E1567", {"start": v(-94.05, -15.94) * mm, "mid": v(-93.54, -16.43) * mm, "end": v(-93.02, -16.9) * mm});
            skLineSegment(sketch, "E1568", {"start": v(-89.64, -14.85) * mm, "end": v(-89.9, -15.18) * mm});
            skLineSegment(sketch, "E1569", {"start": v(-89.9, -15.18) * mm, "end": v(-90.06, -15.32) * mm});
            skLineSegment(sketch, "E1570", {"start": v(-90.06, -15.32) * mm, "end": v(-90.26, -15.5) * mm});
            skLineSegment(sketch, "E1571", {"start": v(-90.26, -15.5) * mm, "end": v(-90.52, -15.7) * mm});
            skLineSegment(sketch, "E1572", {"start": v(-90.52, -15.7) * mm, "end": v(-90.8, -15.89) * mm});
            skLineSegment(sketch, "E1573", {"start": v(-90.8, -15.89) * mm, "end": v(-91.13, -16.08) * mm});
            skLineSegment(sketch, "E1574", {"start": v(-91.13, -16.08) * mm, "end": v(-92, -16.52) * mm});
            skLineSegment(sketch, "E1575", {"start": v(-92, -16.52) * mm, "end": v(-93.02, -16.9) * mm});
            skArc(sketch, "E1576", {"start": v(-88.58, -14.7) * mm, "mid": v(-89.14, -14.56) * mm, "end": v(-89.64, -14.85) * mm});
            skArc(sketch, "E1577", {"start": v(-88.58, -14.7) * mm, "mid": v(-88.3, -14.9) * mm, "end": v(-88.01, -15.1) * mm});
            skArc(sketch, "E1578", {"start": v(-87.8, -16.15) * mm, "mid": v(-87.7, -15.58) * mm, "end": v(-88.01, -15.1) * mm});
            skLineSegment(sketch, "E1579", {"start": v(-87.8, -16.15) * mm, "end": v(-88.01, -16.51) * mm});
            skLineSegment(sketch, "E1580", {"start": v(-88.01, -16.51) * mm, "end": v(-88.1, -16.7) * mm});
            skLineSegment(sketch, "E1581", {"start": v(-88.1, -16.7) * mm, "end": v(-88.2, -16.96) * mm});
            skLineSegment(sketch, "E1582", {"start": v(-88.2, -16.96) * mm, "end": v(-88.3, -17.26) * mm});
            skLineSegment(sketch, "E1583", {"start": v(-88.3, -17.26) * mm, "end": v(-88.38, -17.6) * mm});
            skLineSegment(sketch, "E1584", {"start": v(-88.38, -17.6) * mm, "end": v(-88.46, -17.97) * mm});
            skLineSegment(sketch, "E1585", {"start": v(-88.46, -17.97) * mm, "end": v(-88.58, -18.94) * mm});
            skLineSegment(sketch, "E1586", {"start": v(-88.58, -18.94) * mm, "end": v(-88.6, -20.02) * mm});
            skArc(sketch, "E1587", {"start": v(-88.6, -20.02) * mm, "mid": v(-87.98, -20.35) * mm, "end": v(-87.34, -20.67) * mm});
            skLineSegment(sketch, "E1588", {"start": v(-84.65, -17.78) * mm, "end": v(-84.82, -18.17) * mm});
            skLineSegment(sketch, "E1589", {"start": v(-84.82, -18.17) * mm, "end": v(-84.92, -18.35) * mm});
            skLineSegment(sketch, "E1590", {"start": v(-84.92, -18.35) * mm, "end": v(-85.07, -18.58) * mm});
            skLineSegment(sketch, "E1591", {"start": v(-85.07, -18.58) * mm, "end": v(-85.27, -18.83) * mm});
            skLineSegment(sketch, "E1592", {"start": v(-85.27, -18.83) * mm, "end": v(-85.5, -19.1) * mm});
            skLineSegment(sketch, "E1593", {"start": v(-85.5, -19.1) * mm, "end": v(-85.75, -19.37) * mm});
            skLineSegment(sketch, "E1594", {"start": v(-85.75, -19.37) * mm, "end": v(-86.47, -20.03) * mm});
            skLineSegment(sketch, "E1595", {"start": v(-86.47, -20.03) * mm, "end": v(-87.34, -20.67) * mm});
            skArc(sketch, "E1596", {"start": v(-83.67, -17.35) * mm, "mid": v(-84.25, -17.37) * mm, "end": v(-84.65, -17.78) * mm});
            skArc(sketch, "E1597", {"start": v(-83.67, -17.35) * mm, "mid": v(-83.34, -17.47) * mm, "end": v(-83.01, -17.59) * mm});
            skArc(sketch, "E1598", {"start": v(-82.52, -18.54) * mm, "mid": v(-82.57, -17.96) * mm, "end": v(-83.01, -17.59) * mm});
            skLineSegment(sketch, "E1599", {"start": v(-82.52, -18.54) * mm, "end": v(-82.63, -18.95) * mm});
            skLineSegment(sketch, "E1600", {"start": v(-82.63, -18.95) * mm, "end": v(-82.67, -19.15) * mm});
            skLineSegment(sketch, "E1601", {"start": v(-82.67, -19.15) * mm, "end": v(-82.7, -19.42) * mm});
            skLineSegment(sketch, "E1602", {"start": v(-82.7, -19.42) * mm, "end": v(-82.7, -19.74) * mm});
            skLineSegment(sketch, "E1603", {"start": v(-82.7, -19.74) * mm, "end": v(-82.7, -20.09) * mm});
            skLineSegment(sketch, "E1604", {"start": v(-82.7, -20.09) * mm, "end": v(-82.67, -20.46) * mm});
            skLineSegment(sketch, "E1605", {"start": v(-82.67, -20.46) * mm, "end": v(-82.52, -21.43) * mm});
            skLineSegment(sketch, "E1606", {"start": v(-82.52, -21.43) * mm, "end": v(-82.26, -22.48) * mm});
            skArc(sketch, "E1607", {"start": v(-82.26, -22.48) * mm, "mid": v(-81.56, -22.63) * mm, "end": v(-80.87, -22.77) * mm});
            skLineSegment(sketch, "E1608", {"start": v(-79.05, -19.26) * mm, "end": v(-79.11, -19.68) * mm});
            skLineSegment(sketch, "E1609", {"start": v(-79.11, -19.68) * mm, "end": v(-79.16, -19.88) * mm});
            skLineSegment(sketch, "E1610", {"start": v(-79.16, -19.88) * mm, "end": v(-79.25, -20.14) * mm});
            skLineSegment(sketch, "E1611", {"start": v(-65.36, -17) * mm, "end": v(-65.18, -17.21) * mm});
            skLineSegment(sketch, "E1612", {"start": v(-65.18, -17.21) * mm, "end": v(-64.95, -17.44) * mm});
            skLineSegment(sketch, "E1613", {"start": v(-64.95, -17.44) * mm, "end": v(-64.7, -17.67) * mm});
            skLineSegment(sketch, "E1614", {"start": v(-64.7, -17.67) * mm, "end": v(-64.4, -17.9) * mm});
            skLineSegment(sketch, "E1615", {"start": v(-64.4, -17.9) * mm, "end": v(-63.6, -18.46) * mm});
            skLineSegment(sketch, "E1616", {"start": v(-63.6, -18.46) * mm, "end": v(-62.64, -18.98) * mm});
            skArc(sketch, "E1617", {"start": v(-62.64, -18.98) * mm, "mid": v(-62.06, -18.58) * mm, "end": v(-61.49, -18.16) * mm});
            skLineSegment(sketch, "E1618", {"start": v(-62.82, -14.44) * mm, "end": v(-62.55, -14.77) * mm});
            skLineSegment(sketch, "E1619", {"start": v(-62.55, -14.77) * mm, "end": v(-62.44, -14.95) * mm});
            skLineSegment(sketch, "E1620", {"start": v(-62.44, -14.95) * mm, "end": v(-62.3, -15.19) * mm});
            skLineSegment(sketch, "E1621", {"start": v(-62.3, -15.19) * mm, "end": v(-62.17, -15.47) * mm});
            skLineSegment(sketch, "E1622", {"start": v(-62.17, -15.47) * mm, "end": v(-62.04, -15.8) * mm});
            skLineSegment(sketch, "E1623", {"start": v(-62.04, -15.8) * mm, "end": v(-61.91, -16.15) * mm});
            skLineSegment(sketch, "E1624", {"start": v(-61.91, -16.15) * mm, "end": v(-61.66, -17.1) * mm});
            skLineSegment(sketch, "E1625", {"start": v(-61.66, -17.1) * mm, "end": v(-61.49, -18.16) * mm});
            skArc(sketch, "E1626", {"start": v(-62.74, -13.38) * mm, "mid": v(-63, -13.9) * mm, "end": v(-62.82, -14.44) * mm});
            skArc(sketch, "E1627", {"start": v(-62.74, -13.38) * mm, "mid": v(-62.48, -13.14) * mm, "end": v(-62.23, -12.9) * mm});
            skArc(sketch, "E1628", {"start": v(-61.16, -12.9) * mm, "mid": v(-61.7, -12.68) * mm, "end": v(-62.23, -12.9) * mm});
            skLineSegment(sketch, "E1629", {"start": v(-61.16, -12.9) * mm, "end": v(-60.85, -13.19) * mm});
            skLineSegment(sketch, "E1630", {"start": v(-60.85, -13.19) * mm, "end": v(-60.69, -13.31) * mm});
            skLineSegment(sketch, "E1631", {"start": v(-60.69, -13.31) * mm, "end": v(-60.46, -13.46) * mm});
            skLineSegment(sketch, "E1632", {"start": v(-60.46, -13.46) * mm, "end": v(-60.18, -13.61) * mm});
            skLineSegment(sketch, "E1633", {"start": v(-60.18, -13.61) * mm, "end": v(-59.87, -13.77) * mm});
            skLineSegment(sketch, "E1634", {"start": v(-59.87, -13.77) * mm, "end": v(-59.52, -13.92) * mm});
            skArc(sketch, "E1635", {"start": v(-59.15, -9.1) * mm, "mid": v(-58.96, -8.8) * mm, "end": v(-58.78, -8.5) * mm});
            skArc(sketch, "E1636", {"start": v(-57.75, -8.22) * mm, "mid": v(-58.33, -8.16) * mm, "end": v(-58.78, -8.5) * mm});
            skLineSegment(sketch, "E1637", {"start": v(-57.75, -8.22) * mm, "end": v(-57.38, -8.42) * mm});
            skLineSegment(sketch, "E1638", {"start": v(-57.38, -8.42) * mm, "end": v(-57.18, -8.49) * mm});
            skLineSegment(sketch, "E1639", {"start": v(-57.18, -8.49) * mm, "end": v(-56.92, -8.57) * mm});
            skLineSegment(sketch, "E1640", {"start": v(-56.92, -8.57) * mm, "end": v(-56.61, -8.64) * mm});
            skLineSegment(sketch, "E1641", {"start": v(-54.92, -8.81) * mm, "end": v(-53.84, -8.76) * mm});
            skLineSegment(sketch, "E1642", {"start": v(-55.9, -8.76) * mm, "end": v(-54.92, -8.81) * mm});
            skLineSegment(sketch, "E1643", {"start": v(-56.27, -8.7) * mm, "end": v(-55.9, -8.76) * mm});
            skLineSegment(sketch, "E1644", {"start": v(-56.61, -8.64) * mm, "end": v(-56.27, -8.7) * mm});
            skArc(sketch, "E1645", {"start": v(-59.15, -9.1) * mm, "mid": v(-59.25, -9.67) * mm, "end": v(-58.93, -10.15) * mm});
            skLineSegment(sketch, "E1646", {"start": v(-57.1, -12.4) * mm, "end": v(-56.64, -13.38) * mm});
            skLineSegment(sketch, "E1647", {"start": v(-57.6, -11.55) * mm, "end": v(-57.1, -12.4) * mm});
            skLineSegment(sketch, "E1648", {"start": v(-57.81, -11.24) * mm, "end": v(-57.6, -11.55) * mm});
            skLineSegment(sketch, "E1649", {"start": v(-58.03, -10.97) * mm, "end": v(-57.81, -11.24) * mm});
            skLineSegment(sketch, "E1650", {"start": v(-58.24, -10.73) * mm, "end": v(-58.03, -10.97) * mm});
            skLineSegment(sketch, "E1651", {"start": v(-58.43, -10.53) * mm, "end": v(-58.24, -10.73) * mm});
            skLineSegment(sketch, "E1652", {"start": v(-58.58, -10.4) * mm, "end": v(-58.43, -10.53) * mm});
            skLineSegment(sketch, "E1653", {"start": v(-58.93, -10.15) * mm, "end": v(-58.58, -10.4) * mm});
            skArc(sketch, "E1654", {"start": v(-57.54, -14.48) * mm, "mid": v(-57.08, -13.93) * mm, "end": v(-56.64, -13.38) * mm});
            skLineSegment(sketch, "E1655", {"start": v(-58.6, -14.23) * mm, "end": v(-57.54, -14.48) * mm});
            skLineSegment(sketch, "E1656", {"start": v(-59.52, -13.92) * mm, "end": v(-58.6, -14.23) * mm});
            skLineSegment(sketch, "E1657", {"start": v(-65.49, -16.85) * mm, "end": v(-65.36, -17) * mm});
            skLineSegment(sketch, "E1658", {"start": v(-65.7, -16.48) * mm, "end": v(-65.49, -16.85) * mm});
            skArc(sketch, "E1659", {"start": v(-65.7, -16.48) * mm, "mid": v(-66.16, -16.13) * mm, "end": v(-66.74, -16.2) * mm});
            skArc(sketch, "E1660", {"start": v(-67.36, -16.52) * mm, "mid": v(-67.05, -16.36) * mm, "end": v(-66.74, -16.2) * mm});
            skArc(sketch, "E1661", {"start": v(-67.36, -16.52) * mm, "mid": v(-67.74, -16.95) * mm, "end": v(-67.72, -17.53) * mm});
            skLineSegment(sketch, "E1662", {"start": v(-67.32, -20.4) * mm, "end": v(-67.44, -21.47) * mm});
            skLineSegment(sketch, "E1663", {"start": v(-67.3, -19.41) * mm, "end": v(-67.32, -20.4) * mm});
            skLineSegment(sketch, "E1664", {"start": v(-67.33, -19.04) * mm, "end": v(-67.3, -19.41) * mm});
            skLineSegment(sketch, "E1665", {"start": v(-67.37, -18.7) * mm, "end": v(-67.33, -19.04) * mm});
            skLineSegment(sketch, "E1666", {"start": v(-67.42, -18.38) * mm, "end": v(-67.37, -18.7) * mm});
            skLineSegment(sketch, "E1667", {"start": v(-67.49, -18.11) * mm, "end": v(-67.42, -18.38) * mm});
            skLineSegment(sketch, "E1668", {"start": v(-67.55, -17.91) * mm, "end": v(-67.49, -18.11) * mm});
            skLineSegment(sketch, "E1669", {"start": v(-67.72, -17.53) * mm, "end": v(-67.55, -17.91) * mm});
            skArc(sketch, "E1670", {"start": v(-68.78, -21.94) * mm, "mid": v(-68.1, -21.71) * mm, "end": v(-67.44, -21.47) * mm});
            skLineSegment(sketch, "E1671", {"start": v(-69.55, -21.18) * mm, "end": v(-68.78, -21.94) * mm});
            skLineSegment(sketch, "E1672", {"start": v(-70.18, -20.43) * mm, "end": v(-69.55, -21.18) * mm});
            skLineSegment(sketch, "E1673", {"start": v(-70.4, -20.13) * mm, "end": v(-70.18, -20.43) * mm});
            skLineSegment(sketch, "E1674", {"start": v(-70.58, -19.83) * mm, "end": v(-70.4, -20.13) * mm});
            skLineSegment(sketch, "E1675", {"start": v(-70.74, -19.56) * mm, "end": v(-70.58, -19.83) * mm});
            skLineSegment(sketch, "E1676", {"start": v(-70.86, -19.3) * mm, "end": v(-70.74, -19.56) * mm});
            skLineSegment(sketch, "E1677", {"start": v(-70.94, -19.12) * mm, "end": v(-70.86, -19.3) * mm});
            skLineSegment(sketch, "E1678", {"start": v(-71.05, -18.7) * mm, "end": v(-70.94, -19.12) * mm});
            skArc(sketch, "E1679", {"start": v(-71.05, -18.7) * mm, "mid": v(-71.4, -18.25) * mm, "end": v(-71.96, -18.15) * mm});
            skArc(sketch, "E1680", {"start": v(-72.65, -18.3) * mm, "mid": v(-72.3, -18.23) * mm, "end": v(-71.96, -18.15) * mm});
            skArc(sketch, "E1681", {"start": v(-72.65, -18.3) * mm, "mid": v(-73.13, -18.6) * mm, "end": v(-73.27, -19.17) * mm});
            skLineSegment(sketch, "E1682", {"start": v(-73.66, -22.04) * mm, "end": v(-74.06, -23.04) * mm});
            skLineSegment(sketch, "E1683", {"start": v(-73.38, -21.1) * mm, "end": v(-73.66, -22.04) * mm});
            skLineSegment(sketch, "E1684", {"start": v(-73.3, -20.73) * mm, "end": v(-73.38, -21.1) * mm});
            skLineSegment(sketch, "E1685", {"start": v(-73.25, -20.39) * mm, "end": v(-73.3, -20.73) * mm});
            skLineSegment(sketch, "E1686", {"start": v(-73.21, -20.07) * mm, "end": v(-73.25, -20.39) * mm});
            skLineSegment(sketch, "E1687", {"start": v(-73.2, -19.8) * mm, "end": v(-73.21, -20.07) * mm});
            skLineSegment(sketch, "E1688", {"start": v(-73.2, -19.6) * mm, "end": v(-73.2, -19.8) * mm});
            skLineSegment(sketch, "E1689", {"start": v(-73.27, -19.17) * mm, "end": v(-73.2, -19.6) * mm});
            skArc(sketch, "E1690", {"start": v(-75.48, -23.14) * mm, "mid": v(-74.77, -23.1) * mm, "end": v(-74.06, -23.04) * mm});
            skLineSegment(sketch, "E1691", {"start": v(-76.02, -22.2) * mm, "end": v(-75.48, -23.14) * mm});
            skLineSegment(sketch, "E1692", {"start": v(-76.42, -21.3) * mm, "end": v(-76.02, -22.2) * mm});
            skLineSegment(sketch, "E1693", {"start": v(-76.55, -20.95) * mm, "end": v(-76.42, -21.3) * mm});
            skLineSegment(sketch, "E1694", {"start": v(-76.65, -20.62) * mm, "end": v(-76.55, -20.95) * mm});
            skLineSegment(sketch, "E1695", {"start": v(-76.72, -20.31) * mm, "end": v(-76.65, -20.62) * mm});
            skLineSegment(sketch, "E1696", {"start": v(-76.77, -20.04) * mm, "end": v(-76.72, -20.31) * mm});
            skLineSegment(sketch, "E1697", {"start": v(-76.8, -19.84) * mm, "end": v(-76.77, -20.04) * mm});
            skLineSegment(sketch, "E1698", {"start": v(-76.8, -19.41) * mm, "end": v(-76.8, -19.84) * mm});
            skArc(sketch, "E1699", {"start": v(-76.8, -19.41) * mm, "mid": v(-77, -18.87) * mm, "end": v(-77.53, -18.63) * mm});
            skArc(sketch, "E1700", {"start": v(-78.22, -18.58) * mm, "mid": v(-77.88, -18.6) * mm, "end": v(-77.53, -18.63) * mm});
            skArc(sketch, "E1701", {"start": v(-78.22, -18.58) * mm, "mid": v(-78.78, -18.75) * mm, "end": v(-79.05, -19.26) * mm});
            skLineSegment(sketch, "E1702", {"start": v(-80.2, -21.91) * mm, "end": v(-80.87, -22.77) * mm});
            skLineSegment(sketch, "E1703", {"start": v(-79.68, -21.08) * mm, "end": v(-80.2, -21.91) * mm});
            skLineSegment(sketch, "E1704", {"start": v(-79.5, -20.75) * mm, "end": v(-79.68, -21.08) * mm});
            skLineSegment(sketch, "E1705", {"start": v(-79.36, -20.43) * mm, "end": v(-79.5, -20.75) * mm});
            skLineSegment(sketch, "E1706", {"start": v(-79.25, -20.14) * mm, "end": v(-79.36, -20.43) * mm});
            skLineSegment(sketch, "E1707", {"start": v(-97.5, 65.69) * mm, "end": v(-97.96, 65.59) * mm});
            skArc(sketch, "E1708", {"start": v(-101.62, 67.58) * mm, "mid": v(-101.53, 66.88) * mm, "end": v(-101.42, 66.18) * mm});
            skLineSegment(sketch, "E1709", {"start": v(-100.73, 68.18) * mm, "end": v(-101.62, 67.58) * mm});
            skLineSegment(sketch, "E1710", {"start": v(-99.88, 68.65) * mm, "end": v(-100.73, 68.18) * mm});
            skLineSegment(sketch, "E1711", {"start": v(-99.54, 68.8) * mm, "end": v(-99.88, 68.65) * mm});
            skLineSegment(sketch, "E1712", {"start": v(-99.22, 68.92) * mm, "end": v(-99.54, 68.8) * mm});
            skLineSegment(sketch, "E1713", {"start": v(-98.92, 69.02) * mm, "end": v(-99.22, 68.92) * mm});
            skLineSegment(sketch, "E1714", {"start": v(-98.66, 69.08) * mm, "end": v(-98.92, 69.02) * mm});
            skLineSegment(sketch, "E1715", {"start": v(-98.47, 69.12) * mm, "end": v(-98.66, 69.08) * mm});
            skLineSegment(sketch, "E1716", {"start": v(-98, 69.15) * mm, "end": v(-98.47, 69.12) * mm});
            skArc(sketch, "E1717", {"start": v(-98, 69.15) * mm, "mid": v(-97.48, 69.4) * mm, "end": v(-97.27, 69.94) * mm});
            skArc(sketch, "E1718", {"start": v(-97.27, 70.64) * mm, "mid": v(-97.27, 70.3) * mm, "end": v(-97.27, 69.94) * mm});
            skArc(sketch, "E1719", {"start": v(-97.27, 70.64) * mm, "mid": v(-97.48, 71.19) * mm, "end": v(-98, 71.43) * mm});
            skLineSegment(sketch, "E1720", {"start": v(-100.73, 72.4) * mm, "end": v(-101.62, 73) * mm});
            skLineSegment(sketch, "E1721", {"start": v(-99.88, 71.94) * mm, "end": v(-100.73, 72.4) * mm});
            skLineSegment(sketch, "E1722", {"start": v(-99.54, 71.79) * mm, "end": v(-99.88, 71.94) * mm});
            skLineSegment(sketch, "E1723", {"start": v(-99.22, 71.66) * mm, "end": v(-99.54, 71.79) * mm});
            skLineSegment(sketch, "E1724", {"start": v(-98.92, 71.57) * mm, "end": v(-99.22, 71.66) * mm});
            skLineSegment(sketch, "E1725", {"start": v(-98.66, 71.5) * mm, "end": v(-98.92, 71.57) * mm});
            skLineSegment(sketch, "E1726", {"start": v(-98.47, 71.46) * mm, "end": v(-98.66, 71.5) * mm});
            skLineSegment(sketch, "E1727", {"start": v(-98, 71.43) * mm, "end": v(-98.47, 71.46) * mm});
            skArc(sketch, "E1728", {"start": v(-101.42, 74.4) * mm, "mid": v(-101.53, 73.7) * mm, "end": v(-101.62, 73) * mm});
            skLineSegment(sketch, "E1729", {"start": v(-100.4, 74.74) * mm, "end": v(-101.42, 74.4) * mm});
            skLineSegment(sketch, "E1730", {"start": v(-99.45, 74.94) * mm, "end": v(-100.4, 74.74) * mm});
            skLineSegment(sketch, "E1731", {"start": v(-99.08, 75) * mm, "end": v(-99.45, 74.94) * mm});
            skLineSegment(sketch, "E1732", {"start": v(-98.74, 75.02) * mm, "end": v(-99.08, 75) * mm});
            skLineSegment(sketch, "E1733", {"start": v(-98.42, 75.03) * mm, "end": v(-98.74, 75.02) * mm});
            skLineSegment(sketch, "E1734", {"start": v(-98.16, 75.02) * mm, "end": v(-98.42, 75.03) * mm});
            skLineSegment(sketch, "E1735", {"start": v(-97.96, 75) * mm, "end": v(-98.16, 75.02) * mm});
            skLineSegment(sketch, "E1736", {"start": v(-97.5, 74.9) * mm, "end": v(-97.96, 75) * mm});
            skArc(sketch, "E1737", {"start": v(-97.5, 74.9) * mm, "mid": v(-96.93, 74.99) * mm, "end": v(-96.58, 75.45) * mm});
            skArc(sketch, "E1738", {"start": v(-96.38, 76.12) * mm, "mid": v(-96.48, 75.79) * mm, "end": v(-96.58, 75.45) * mm});
            skArc(sketch, "E1739", {"start": v(-96.38, 76.12) * mm, "mid": v(-96.43, 76.7) * mm, "end": v(-96.86, 77.09) * mm});
            skLineSegment(sketch, "E1740", {"start": v(-99.2, 78.79) * mm, "end": v(-99.89, 79.62) * mm});
            skLineSegment(sketch, "E1741", {"start": v(-98.52, 78.1) * mm, "end": v(-99.2, 78.79) * mm});
            skLineSegment(sketch, "E1742", {"start": v(-98.24, 77.86) * mm, "end": v(-98.52, 78.1) * mm});
            skLineSegment(sketch, "E1743", {"start": v(-97.97, 77.65) * mm, "end": v(-98.24, 77.86) * mm});
            skLineSegment(sketch, "E1744", {"start": v(-97.7, 77.47) * mm, "end": v(-97.97, 77.65) * mm});
            skLineSegment(sketch, "E1745", {"start": v(-97.48, 77.34) * mm, "end": v(-97.7, 77.47) * mm});
            skLineSegment(sketch, "E1746", {"start": v(-97.3, 77.25) * mm, "end": v(-97.48, 77.34) * mm});
            skLineSegment(sketch, "E1747", {"start": v(-96.86, 77.09) * mm, "end": v(-97.3, 77.25) * mm});
            skArc(sketch, "E1748", {"start": v(-99.3, 80.9) * mm, "mid": v(-99.6, 80.26) * mm, "end": v(-99.89, 79.62) * mm});
            skLineSegment(sketch, "E1749", {"start": v(-98.23, 80.93) * mm, "end": v(-99.3, 80.9) * mm});
            skLineSegment(sketch, "E1750", {"start": v(-97.26, 80.86) * mm, "end": v(-98.23, 80.93) * mm});
            skLineSegment(sketch, "E1751", {"start": v(-96.9, 80.8) * mm, "end": v(-97.26, 80.86) * mm});
            skLineSegment(sketch, "E1752", {"start": v(-96.56, 80.74) * mm, "end": v(-96.9, 80.8) * mm});
            skLineSegment(sketch, "E1753", {"start": v(-96.25, 80.66) * mm, "end": v(-96.56, 80.74) * mm});
            skLineSegment(sketch, "E1754", {"start": v(-96, 80.57) * mm, "end": v(-96.25, 80.66) * mm});
            skLineSegment(sketch, "E1755", {"start": v(-95.81, 80.5) * mm, "end": v(-96, 80.57) * mm});
            skLineSegment(sketch, "E1756", {"start": v(-95.4, 80.27) * mm, "end": v(-95.81, 80.5) * mm});
            skArc(sketch, "E1757", {"start": v(-95.4, 80.27) * mm, "mid": v(-94.83, 80.2) * mm, "end": v(-94.36, 80.54) * mm});
            skArc(sketch, "E1758", {"start": v(-93.98, 81.13) * mm, "mid": v(-94.18, 80.83) * mm, "end": v(-94.36, 80.54) * mm});
            skArc(sketch, "E1759", {"start": v(-93.98, 81.13) * mm, "mid": v(-93.86, 81.7) * mm, "end": v(-94.17, 82.2) * mm});
            skLineSegment(sketch, "E1760", {"start": v(-95.95, 84.48) * mm, "end": v(-96.36, 85.47) * mm});
            skLineSegment(sketch, "E1761", {"start": v(-95.48, 83.63) * mm, "end": v(-95.95, 84.48) * mm});
            skLineSegment(sketch, "E1762", {"start": v(-95.28, 83.32) * mm, "end": v(-95.48, 83.63) * mm});
            skLineSegment(sketch, "E1763", {"start": v(-95.07, 83.04) * mm, "end": v(-95.28, 83.32) * mm});
            skLineSegment(sketch, "E1764", {"start": v(-94.88, 82.8) * mm, "end": v(-95.07, 83.04) * mm});
            skLineSegment(sketch, "E1765", {"start": v(-94.7, 82.6) * mm, "end": v(-94.88, 82.8) * mm});
            skLineSegment(sketch, "E1766", {"start": v(-94.55, 82.47) * mm, "end": v(-94.7, 82.6) * mm});
            skLineSegment(sketch, "E1767", {"start": v(-94.17, 82.2) * mm, "end": v(-94.55, 82.47) * mm});
            skArc(sketch, "E1768", {"start": v(-95.44, 86.53) * mm, "mid": v(-95.9, 86) * mm, "end": v(-96.36, 85.47) * mm});
            skLineSegment(sketch, "E1769", {"start": v(-94.4, 86.26) * mm, "end": v(-95.44, 86.53) * mm});
            skLineSegment(sketch, "E1770", {"start": v(-93.5, 85.92) * mm, "end": v(-94.4, 86.26) * mm});
            skLineSegment(sketch, "E1771", {"start": v(-93.16, 85.77) * mm, "end": v(-93.5, 85.92) * mm});
            skLineSegment(sketch, "E1772", {"start": v(-92.85, 85.6) * mm, "end": v(-93.16, 85.77) * mm});
            skLineSegment(sketch, "E1773", {"start": v(-92.59, 85.44) * mm, "end": v(-92.85, 85.6) * mm});
            skLineSegment(sketch, "E1774", {"start": v(-92.36, 85.29) * mm, "end": v(-92.59, 85.44) * mm});
            skLineSegment(sketch, "E1775", {"start": v(-92.2, 85.16) * mm, "end": v(-92.36, 85.29) * mm});
            skLineSegment(sketch, "E1776", {"start": v(-91.88, 84.83) * mm, "end": v(-92.2, 85.16) * mm});
            skArc(sketch, "E1777", {"start": v(-91.88, 84.83) * mm, "mid": v(-91.35, 84.6) * mm, "end": v(-90.8, 84.8) * mm});
            skArc(sketch, "E1778", {"start": v(-90.27, 85.26) * mm, "mid": v(-90.54, 85.03) * mm, "end": v(-90.8, 84.8) * mm});
            skArc(sketch, "E1779", {"start": v(-90.27, 85.26) * mm, "mid": v(-90, 85.77) * mm, "end": v(-90.16, 86.33) * mm});
            skLineSegment(sketch, "E1780", {"start": v(-91.21, 89.03) * mm, "end": v(-91.33, 90.1) * mm});
            skLineSegment(sketch, "E1781", {"start": v(-91, 88.08) * mm, "end": v(-91.21, 89.03) * mm});
            skLineSegment(sketch, "E1782", {"start": v(-90.9, 87.72) * mm, "end": v(-91, 88.08) * mm});
            skLineSegment(sketch, "E1783", {"start": v(-90.78, 87.4) * mm, "end": v(-90.9, 87.72) * mm});
            skLineSegment(sketch, "E1784", {"start": v(-90.66, 87.11) * mm, "end": v(-90.78, 87.4) * mm});
            skLineSegment(sketch, "E1785", {"start": v(-90.54, 86.87) * mm, "end": v(-90.66, 87.11) * mm});
            skLineSegment(sketch, "E1786", {"start": v(-90.44, 86.7) * mm, "end": v(-90.54, 86.87) * mm});
            skLineSegment(sketch, "E1787", {"start": v(-90.16, 86.33) * mm, "end": v(-90.44, 86.7) * mm});
            skArc(sketch, "E1788", {"start": v(-90.15, 90.85) * mm, "mid": v(-90.75, 90.48) * mm, "end": v(-91.33, 90.1) * mm});
            skLineSegment(sketch, "E1789", {"start": v(-89.23, 90.3) * mm, "end": v(-90.15, 90.85) * mm});
            skLineSegment(sketch, "E1790", {"start": v(-88.45, 89.72) * mm, "end": v(-89.23, 90.3) * mm});
            skLineSegment(sketch, "E1791", {"start": v(-88.17, 89.47) * mm, "end": v(-88.45, 89.72) * mm});
            skLineSegment(sketch, "E1792", {"start": v(-87.93, 89.23) * mm, "end": v(-88.17, 89.47) * mm});
            skLineSegment(sketch, "E1793", {"start": v(-87.72, 89) * mm, "end": v(-87.93, 89.23) * mm});
            skLineSegment(sketch, "E1794", {"start": v(-87.55, 88.8) * mm, "end": v(-87.72, 89) * mm});
            skLineSegment(sketch, "E1795", {"start": v(-87.43, 88.63) * mm, "end": v(-87.55, 88.8) * mm});
            skLineSegment(sketch, "E1796", {"start": v(-87.21, 88.22) * mm, "end": v(-87.43, 88.63) * mm});
            skArc(sketch, "E1797", {"start": v(-87.21, 88.22) * mm, "mid": v(-86.77, 87.84) * mm, "end": v(-86.2, 87.88) * mm});
            skArc(sketch, "E1798", {"start": v(-85.55, 88.17) * mm, "mid": v(-85.87, 88.03) * mm, "end": v(-86.2, 87.88) * mm});
            skArc(sketch, "E1799", {"start": v(-85.55, 88.17) * mm, "mid": v(-85.14, 88.59) * mm, "end": v(-85.14, 89.17) * mm});
            skLineSegment(sketch, "E1800", {"start": v(-85.4, 92.05) * mm, "end": v(-85.2, 93.11) * mm});
            skLineSegment(sketch, "E1801", {"start": v(-85.46, 91.09) * mm, "end": v(-85.4, 92.05) * mm});
            skLineSegment(sketch, "E1802", {"start": v(-85.46, 90.72) * mm, "end": v(-85.46, 91.09) * mm});
            skLineSegment(sketch, "E1803", {"start": v(-85.44, 90.37) * mm, "end": v(-85.46, 90.72) * mm});
            skLineSegment(sketch, "E1804", {"start": v(-85.4, 90.06) * mm, "end": v(-85.44, 90.37) * mm});
            skLineSegment(sketch, "E1805", {"start": v(-85.35, 89.8) * mm, "end": v(-85.4, 90.06) * mm});
            skLineSegment(sketch, "E1806", {"start": v(-85.3, 89.6) * mm, "end": v(-85.35, 89.8) * mm});
            skLineSegment(sketch, "E1807", {"start": v(-85.14, 89.17) * mm, "end": v(-85.3, 89.6) * mm});
            skArc(sketch, "E1808", {"start": v(-83.85, 93.5) * mm, "mid": v(-84.53, 93.32) * mm, "end": v(-85.2, 93.11) * mm});
            skLineSegment(sketch, "E1809", {"start": v(-83.13, 92.72) * mm, "end": v(-83.85, 93.5) * mm});
            skLineSegment(sketch, "E1810", {"start": v(-82.55, 91.94) * mm, "end": v(-83.13, 92.72) * mm});
            skLineSegment(sketch, "E1811", {"start": v(-82.35, 91.63) * mm, "end": v(-82.55, 91.94) * mm});
            skLineSegment(sketch, "E1812", {"start": v(-82.18, 91.33) * mm, "end": v(-82.35, 91.63) * mm});
            skLineSegment(sketch, "E1813", {"start": v(-82.04, 91.05) * mm, "end": v(-82.18, 91.33) * mm});
            skLineSegment(sketch, "E1814", {"start": v(-81.94, 90.8) * mm, "end": v(-82.04, 91.05) * mm});
            skLineSegment(sketch, "E1815", {"start": v(-81.88, 90.6) * mm, "end": v(-81.94, 90.8) * mm});
            skLineSegment(sketch, "E1816", {"start": v(-81.78, 90.15) * mm, "end": v(-81.88, 90.6) * mm});
            skArc(sketch, "E1817", {"start": v(-81.78, 90.15) * mm, "mid": v(-81.46, 89.67) * mm, "end": v(-80.9, 89.54) * mm});
            skArc(sketch, "E1818", {"start": v(-80.2, 89.64) * mm, "mid": v(-80.55, 89.6) * mm, "end": v(-80.9, 89.54) * mm});
            skArc(sketch, "E1819", {"start": v(-80.2, 89.64) * mm, "mid": v(-79.7, 89.92) * mm, "end": v(-79.52, 90.48) * mm});
            skLineSegment(sketch, "E1820", {"start": v(-78.95, 93.32) * mm, "end": v(-78.48, 94.28) * mm});
            skLineSegment(sketch, "E1821", {"start": v(-79.29, 92.41) * mm, "end": v(-78.95, 93.32) * mm});
            skLineSegment(sketch, "E1822", {"start": v(-79.4, 92.05) * mm, "end": v(-79.29, 92.41) * mm});
            skLineSegment(sketch, "E1823", {"start": v(-79.47, 91.72) * mm, "end": v(-79.4, 92.05) * mm});
            skLineSegment(sketch, "E1824", {"start": v(-79.52, 91.4) * mm, "end": v(-79.47, 91.72) * mm});
            skLineSegment(sketch, "E1825", {"start": v(-79.55, 91.14) * mm, "end": v(-79.52, 91.4) * mm});
            skLineSegment(sketch, "E1826", {"start": v(-79.56, 90.94) * mm, "end": v(-79.55, 91.14) * mm});
            skLineSegment(sketch, "E1827", {"start": v(-79.52, 90.48) * mm, "end": v(-79.56, 90.94) * mm});
            skArc(sketch, "E1828", {"start": v(-77.07, 94.28) * mm, "mid": v(-77.77, 94.3) * mm, "end": v(-78.48, 94.28) * mm});
            skLineSegment(sketch, "E1829", {"start": v(-76.6, 93.32) * mm, "end": v(-77.07, 94.28) * mm});
            skLineSegment(sketch, "E1830", {"start": v(-76.25, 92.41) * mm, "end": v(-76.6, 93.32) * mm});
            skLineSegment(sketch, "E1831", {"start": v(-76.15, 92.05) * mm, "end": v(-76.25, 92.41) * mm});
            skLineSegment(sketch, "E1832", {"start": v(-76.08, 91.72) * mm, "end": v(-76.15, 92.05) * mm});
            skLineSegment(sketch, "E1833", {"start": v(-76.02, 91.4) * mm, "end": v(-76.08, 91.72) * mm});
            skLineSegment(sketch, "E1834", {"start": v(-76, 91.14) * mm, "end": v(-76.02, 91.4) * mm});
            skLineSegment(sketch, "E1835", {"start": v(-75.99, 90.94) * mm, "end": v(-76, 91.14) * mm});
            skLineSegment(sketch, "E1836", {"start": v(-76.02, 90.48) * mm, "end": v(-75.99, 90.94) * mm});
            skArc(sketch, "E1837", {"start": v(-76.02, 90.48) * mm, "mid": v(-75.85, 89.92) * mm, "end": v(-75.34, 89.64) * mm});
            skArc(sketch, "E1838", {"start": v(-74.65, 89.54) * mm, "mid": v(-75, 89.6) * mm, "end": v(-75.34, 89.64) * mm});
            skArc(sketch, "E1839", {"start": v(-74.65, 89.54) * mm, "mid": v(-74.08, 89.67) * mm, "end": v(-73.76, 90.15) * mm});
            skLineSegment(sketch, "E1840", {"start": v(-72.42, 92.72) * mm, "end": v(-71.69, 93.5) * mm});
            skLineSegment(sketch, "E1841", {"start": v(-73, 91.94) * mm, "end": v(-72.42, 92.72) * mm});
            skLineSegment(sketch, "E1842", {"start": v(-73.2, 91.63) * mm, "end": v(-73, 91.94) * mm});
            skLineSegment(sketch, "E1843", {"start": v(-73.36, 91.33) * mm, "end": v(-73.2, 91.63) * mm});
            skLineSegment(sketch, "E1844", {"start": v(-73.5, 91.05) * mm, "end": v(-73.36, 91.33) * mm});
            skLineSegment(sketch, "E1845", {"start": v(-73.6, 90.8) * mm, "end": v(-73.5, 91.05) * mm});
            skLineSegment(sketch, "E1846", {"start": v(-73.67, 90.6) * mm, "end": v(-73.6, 90.8) * mm});
            skLineSegment(sketch, "E1847", {"start": v(-73.76, 90.15) * mm, "end": v(-73.67, 90.6) * mm});
            skArc(sketch, "E1848", {"start": v(-70.34, 93.11) * mm, "mid": v(-71, 93.32) * mm, "end": v(-71.69, 93.5) * mm});
            skLineSegment(sketch, "E1849", {"start": v(-70.15, 92.05) * mm, "end": v(-70.34, 93.11) * mm});
            skLineSegment(sketch, "E1850", {"start": v(-70.08, 91.09) * mm, "end": v(-70.15, 92.05) * mm});
            skLineSegment(sketch, "E1851", {"start": v(-70.09, 90.72) * mm, "end": v(-70.08, 91.09) * mm});
            skLineSegment(sketch, "E1852", {"start": v(-70.1, 90.37) * mm, "end": v(-70.09, 90.72) * mm});
            skLineSegment(sketch, "E1853", {"start": v(-70.14, 90.06) * mm, "end": v(-70.1, 90.37) * mm});
            skLineSegment(sketch, "E1854", {"start": v(-70.2, 89.8) * mm, "end": v(-70.14, 90.06) * mm});
            skLineSegment(sketch, "E1855", {"start": v(-70.24, 89.6) * mm, "end": v(-70.2, 89.8) * mm});
            skLineSegment(sketch, "E1856", {"start": v(-70.4, 89.17) * mm, "end": v(-70.24, 89.6) * mm});
            skArc(sketch, "E1857", {"start": v(-70.4, 89.17) * mm, "mid": v(-70.4, 88.59) * mm, "end": v(-70, 88.17) * mm});
            skArc(sketch, "E1858", {"start": v(-69.35, 87.88) * mm, "mid": v(-69.67, 88.03) * mm, "end": v(-70, 88.17) * mm});
            skArc(sketch, "E1859", {"start": v(-69.35, 87.88) * mm, "mid": v(-68.77, 87.84) * mm, "end": v(-68.33, 88.22) * mm});
            skLineSegment(sketch, "E1860", {"start": v(-66.31, 90.3) * mm, "end": v(-65.4, 90.85) * mm});
            skLineSegment(sketch, "E1861", {"start": v(-67.09, 89.72) * mm, "end": v(-66.31, 90.3) * mm});
            skLineSegment(sketch, "E1862", {"start": v(-67.37, 89.47) * mm, "end": v(-67.09, 89.72) * mm});
            skLineSegment(sketch, "E1863", {"start": v(-67.61, 89.23) * mm, "end": v(-67.37, 89.47) * mm});
            skLineSegment(sketch, "E1864", {"start": v(-67.83, 89) * mm, "end": v(-67.61, 89.23) * mm});
            skLineSegment(sketch, "E1865", {"start": v(-68, 88.8) * mm, "end": v(-67.83, 89) * mm});
            skLineSegment(sketch, "E1866", {"start": v(-68.1, 88.63) * mm, "end": v(-68, 88.8) * mm});
            skLineSegment(sketch, "E1867", {"start": v(-68.33, 88.22) * mm, "end": v(-68.1, 88.63) * mm});
            skArc(sketch, "E1868", {"start": v(-64.2, 90.1) * mm, "mid": v(-64.8, 90.48) * mm, "end": v(-65.4, 90.85) * mm});
            skLineSegment(sketch, "E1869", {"start": v(-64.33, 89.03) * mm, "end": v(-64.2, 90.1) * mm});
            skLineSegment(sketch, "E1870", {"start": v(-64.54, 88.08) * mm, "end": v(-64.33, 89.03) * mm});
            skLineSegment(sketch, "E1871", {"start": v(-64.64, 87.72) * mm, "end": v(-64.54, 88.08) * mm});
            skLineSegment(sketch, "E1872", {"start": v(-64.76, 87.4) * mm, "end": v(-64.64, 87.72) * mm});
            skLineSegment(sketch, "E1873", {"start": v(-64.88, 87.11) * mm, "end": v(-64.76, 87.4) * mm});
            skLineSegment(sketch, "E1874", {"start": v(-65, 86.87) * mm, "end": v(-64.88, 87.11) * mm});
            skLineSegment(sketch, "E1875", {"start": v(-65.1, 86.7) * mm, "end": v(-65, 86.87) * mm});
            skLineSegment(sketch, "E1876", {"start": v(-65.39, 86.33) * mm, "end": v(-65.1, 86.7) * mm});
            skArc(sketch, "E1877", {"start": v(-65.39, 86.33) * mm, "mid": v(-65.54, 85.77) * mm, "end": v(-65.27, 85.26) * mm});
            skArc(sketch, "E1878", {"start": v(-64.74, 84.8) * mm, "mid": v(-65, 85.03) * mm, "end": v(-65.27, 85.26) * mm});
            skArc(sketch, "E1879", {"start": v(-64.74, 84.8) * mm, "mid": v(-64.2, 84.6) * mm, "end": v(-63.66, 84.83) * mm});
            skLineSegment(sketch, "E1880", {"start": v(-61.14, 86.26) * mm, "end": v(-60.1, 86.53) * mm});
            skLineSegment(sketch, "E1881", {"start": v(-62.05, 85.92) * mm, "end": v(-61.14, 86.26) * mm});
            skLineSegment(sketch, "E1882", {"start": v(-62.39, 85.77) * mm, "end": v(-62.05, 85.92) * mm});
            skLineSegment(sketch, "E1883", {"start": v(-62.69, 85.6) * mm, "end": v(-62.39, 85.77) * mm});
            skLineSegment(sketch, "E1884", {"start": v(-62.96, 85.44) * mm, "end": v(-62.69, 85.6) * mm});
            skLineSegment(sketch, "E1885", {"start": v(-63.18, 85.29) * mm, "end": v(-62.96, 85.44) * mm});
            skLineSegment(sketch, "E1886", {"start": v(-63.33, 85.16) * mm, "end": v(-63.18, 85.29) * mm});
            skLineSegment(sketch, "E1887", {"start": v(-63.66, 84.83) * mm, "end": v(-63.33, 85.16) * mm});
            skArc(sketch, "E1888", {"start": v(-59.18, 85.47) * mm, "mid": v(-59.63, 86) * mm, "end": v(-60.1, 86.53) * mm});
            skLineSegment(sketch, "E1889", {"start": v(-59.6, 84.48) * mm, "end": v(-59.18, 85.47) * mm});
            skLineSegment(sketch, "E1890", {"start": v(-60.06, 83.63) * mm, "end": v(-59.6, 84.48) * mm});
            skLineSegment(sketch, "E1891", {"start": v(-60.27, 83.32) * mm, "end": v(-60.06, 83.63) * mm});
            skLineSegment(sketch, "E1892", {"start": v(-60.47, 83.04) * mm, "end": v(-60.27, 83.32) * mm});
            skLineSegment(sketch, "E1893", {"start": v(-60.67, 82.8) * mm, "end": v(-60.47, 83.04) * mm});
            skLineSegment(sketch, "E1894", {"start": v(-60.85, 82.6) * mm, "end": v(-60.67, 82.8) * mm});
            skLineSegment(sketch, "E1895", {"start": v(-61, 82.47) * mm, "end": v(-60.85, 82.6) * mm});
            skLineSegment(sketch, "E1896", {"start": v(-61.37, 82.2) * mm, "end": v(-61, 82.47) * mm});
            skArc(sketch, "E1897", {"start": v(-61.37, 82.2) * mm, "mid": v(-61.68, 81.7) * mm, "end": v(-61.56, 81.13) * mm});
            skArc(sketch, "E1898", {"start": v(-61.18, 80.54) * mm, "mid": v(-61.37, 80.83) * mm, "end": v(-61.56, 81.13) * mm});
            skArc(sketch, "E1899", {"start": v(-61.18, 80.54) * mm, "mid": v(-60.71, 80.2) * mm, "end": v(-60.14, 80.27) * mm});
            skLineSegment(sketch, "E1900", {"start": v(-57.32, 80.93) * mm, "end": v(-56.24, 80.9) * mm});
            skLineSegment(sketch, "E1901", {"start": v(-58.28, 80.86) * mm, "end": v(-57.32, 80.93) * mm});
            skLineSegment(sketch, "E1902", {"start": v(-58.65, 80.8) * mm, "end": v(-58.28, 80.86) * mm});
            skLineSegment(sketch, "E1903", {"start": v(-58.99, 80.74) * mm, "end": v(-58.65, 80.8) * mm});
            skLineSegment(sketch, "E1904", {"start": v(-59.29, 80.66) * mm, "end": v(-58.99, 80.74) * mm});
            skLineSegment(sketch, "E1905", {"start": v(-59.54, 80.57) * mm, "end": v(-59.29, 80.66) * mm});
            skLineSegment(sketch, "E1906", {"start": v(-59.73, 80.5) * mm, "end": v(-59.54, 80.57) * mm});
            skLineSegment(sketch, "E1907", {"start": v(-60.14, 80.27) * mm, "end": v(-59.73, 80.5) * mm});
            skArc(sketch, "E1908", {"start": v(-55.66, 79.62) * mm, "mid": v(-55.94, 80.26) * mm, "end": v(-56.24, 80.9) * mm});
            skLineSegment(sketch, "E1909", {"start": v(-56.34, 78.79) * mm, "end": v(-55.66, 79.62) * mm});
            skLineSegment(sketch, "E1910", {"start": v(-57.02, 78.1) * mm, "end": v(-56.34, 78.79) * mm});
            skLineSegment(sketch, "E1911", {"start": v(-57.3, 77.86) * mm, "end": v(-57.02, 78.1) * mm});
            skLineSegment(sketch, "E1912", {"start": v(-57.58, 77.65) * mm, "end": v(-57.3, 77.86) * mm});
            skLineSegment(sketch, "E1913", {"start": v(-57.84, 77.47) * mm, "end": v(-57.58, 77.65) * mm});
            skLineSegment(sketch, "E1914", {"start": v(-58.07, 77.34) * mm, "end": v(-57.84, 77.47) * mm});
            skLineSegment(sketch, "E1915", {"start": v(-58.25, 77.25) * mm, "end": v(-58.07, 77.34) * mm});
            skLineSegment(sketch, "E1916", {"start": v(-58.68, 77.09) * mm, "end": v(-58.25, 77.25) * mm});
            skLineSegment(sketch, "E1917", {"start": v(-58.93, 13.84) * mm, "end": v(-58.58, 14.08) * mm});
            skArc(sketch, "E1918", {"start": v(-58.93, 13.84) * mm, "mid": v(-59.25, 13.36) * mm, "end": v(-59.15, 12.8) * mm});
            skArc(sketch, "E1919", {"start": v(-58.78, 12.2) * mm, "mid": v(-58.96, 12.5) * mm, "end": v(-59.15, 12.8) * mm});
            skArc(sketch, "E1920", {"start": v(-58.78, 12.2) * mm, "mid": v(-58.33, 11.84) * mm, "end": v(-57.75, 11.9) * mm});
            skLineSegment(sketch, "E1921", {"start": v(-54.92, 12.5) * mm, "end": v(-53.84, 12.45) * mm});
            skLineSegment(sketch, "E1922", {"start": v(-55.9, 12.44) * mm, "end": v(-54.92, 12.5) * mm});
            skLineSegment(sketch, "E1923", {"start": v(-56.27, 12.4) * mm, "end": v(-55.9, 12.44) * mm});
            skLineSegment(sketch, "E1924", {"start": v(-56.61, 12.33) * mm, "end": v(-56.27, 12.4) * mm});
            skLineSegment(sketch, "E1925", {"start": v(-56.92, 12.25) * mm, "end": v(-56.61, 12.33) * mm});
            skLineSegment(sketch, "E1926", {"start": v(-57.18, 12.17) * mm, "end": v(-56.92, 12.25) * mm});
            skLineSegment(sketch, "E1927", {"start": v(-57.38, 12.1) * mm, "end": v(-57.18, 12.17) * mm});
            skLineSegment(sketch, "E1928", {"start": v(-57.75, 11.9) * mm, "end": v(-57.38, 12.1) * mm});
            skArc(sketch, "E1929", {"start": v(-53.27, 11.15) * mm, "mid": v(-53.55, 11.8) * mm, "end": v(-53.84, 12.45) * mm});
            skLineSegment(sketch, "E1930", {"start": v(-53.98, 10.32) * mm, "end": v(-53.27, 11.15) * mm});
            skLineSegment(sketch, "E1931", {"start": v(-54.68, 9.65) * mm, "end": v(-53.98, 10.32) * mm});
            skLineSegment(sketch, "E1932", {"start": v(-54.97, 9.4) * mm, "end": v(-54.68, 9.65) * mm});
            skLineSegment(sketch, "E1933", {"start": v(-55.25, 9.2) * mm, "end": v(-54.97, 9.4) * mm});
            skLineSegment(sketch, "E1934", {"start": v(-55.52, 9.03) * mm, "end": v(-55.25, 9.2) * mm});
            skLineSegment(sketch, "E1935", {"start": v(-55.76, 8.9) * mm, "end": v(-55.52, 9.03) * mm});
            skLineSegment(sketch, "E1936", {"start": v(-55.94, 8.8) * mm, "end": v(-55.76, 8.9) * mm});
            skLineSegment(sketch, "E1937", {"start": v(-56.34, 8.66) * mm, "end": v(-55.94, 8.8) * mm});
            skArc(sketch, "E1938", {"start": v(-56.34, 8.66) * mm, "mid": v(-56.78, 8.28) * mm, "end": v(-56.83, 7.7) * mm});
            skArc(sketch, "E1939", {"start": v(-56.65, 7.04) * mm, "mid": v(-56.74, 7.37) * mm, "end": v(-56.83, 7.7) * mm});
            skArc(sketch, "E1940", {"start": v(-56.65, 7.04) * mm, "mid": v(-56.3, 6.57) * mm, "end": v(-55.73, 6.48) * mm});
            skLineSegment(sketch, "E1941", {"start": v(-52.85, 6.29) * mm, "end": v(-51.82, 5.95) * mm});
            skLineSegment(sketch, "E1942", {"start": v(-53.8, 6.5) * mm, "end": v(-52.85, 6.29) * mm});
            skLineSegment(sketch, "E1943", {"start": v(-54.17, 6.55) * mm, "end": v(-53.8, 6.5) * mm});
            skLineSegment(sketch, "E1944", {"start": v(-55.25, 0.71) * mm, "end": v(-54.83, 0.68) * mm});
            skArc(sketch, "E1945", {"start": v(-51.82, -2.26) * mm, "mid": v(-51.7, -1.56) * mm, "end": v(-51.62, -0.86) * mm});
            skLineSegment(sketch, "E1946", {"start": v(-52.85, -2.6) * mm, "end": v(-51.82, -2.26) * mm});
            skLineSegment(sketch, "E1947", {"start": v(-53.8, -2.81) * mm, "end": v(-52.85, -2.6) * mm});
            skLineSegment(sketch, "E1948", {"start": v(-54.17, -2.87) * mm, "end": v(-53.8, -2.81) * mm});
            skLineSegment(sketch, "E1949", {"start": v(-54.52, -2.9) * mm, "end": v(-54.17, -2.87) * mm});
            skLineSegment(sketch, "E1950", {"start": v(-54.84, -2.9) * mm, "end": v(-54.52, -2.9) * mm});
            skLineSegment(sketch, "E1951", {"start": v(-55.11, -2.9) * mm, "end": v(-54.84, -2.9) * mm});
            skLineSegment(sketch, "E1952", {"start": v(-55.32, -2.88) * mm, "end": v(-55.11, -2.9) * mm});
            skLineSegment(sketch, "E1953", {"start": v(-55.73, -2.8) * mm, "end": v(-55.32, -2.88) * mm});
            skArc(sketch, "E1954", {"start": v(-55.73, -2.8) * mm, "mid": v(-56.3, -2.89) * mm, "end": v(-56.65, -3.35) * mm});
            skArc(sketch, "E1955", {"start": v(-56.83, -4.02) * mm, "mid": v(-56.74, -3.69) * mm, "end": v(-56.65, -3.35) * mm});
            skLineSegment(sketch, "E1956", {"start": v(-55.76, -5.2) * mm, "end": v(-55.52, -5.34) * mm});
            skLineSegment(sketch, "E1957", {"start": v(-55.94, -5.12) * mm, "end": v(-55.76, -5.2) * mm});
            skLineSegment(sketch, "E1958", {"start": v(-56.34, -4.97) * mm, "end": v(-55.94, -5.12) * mm});
            skArc(sketch, "E1959", {"start": v(-53.84, -8.76) * mm, "mid": v(-53.55, -8.12) * mm, "end": v(-53.27, -7.46) * mm});
            skLineSegment(sketch, "E1960", {"start": v(-55.52, -5.34) * mm, "end": v(-55.25, -5.52) * mm});
            skLineSegment(sketch, "E1961", {"start": v(-55.25, -5.52) * mm, "end": v(-54.97, -5.72) * mm});
            skLineSegment(sketch, "E1962", {"start": v(-54.97, -5.72) * mm, "end": v(-54.68, -5.96) * mm});
            skLineSegment(sketch, "E1963", {"start": v(-54.68, -5.96) * mm, "end": v(-53.98, -6.64) * mm});
            skLineSegment(sketch, "E1964", {"start": v(-53.98, -6.64) * mm, "end": v(-53.27, -7.46) * mm});
            skArc(sketch, "E1965", {"start": v(-56.83, -4.02) * mm, "mid": v(-56.78, -4.6) * mm, "end": v(-56.34, -4.97) * mm});
            skLineSegment(sketch, "E1966", {"start": v(-54.83, 0.68) * mm, "end": v(-54.62, 0.65) * mm});
            skLineSegment(sketch, "E1967", {"start": v(-54.62, 0.65) * mm, "end": v(-54.36, 0.58) * mm});
            skLineSegment(sketch, "E1968", {"start": v(-54.36, 0.58) * mm, "end": v(-54.06, 0.48) * mm});
            skLineSegment(sketch, "E1969", {"start": v(-54.06, 0.48) * mm, "end": v(-53.73, 0.36) * mm});
            skLineSegment(sketch, "E1970", {"start": v(-53.73, 0.36) * mm, "end": v(-53.38, 0.2) * mm});
            skLineSegment(sketch, "E1971", {"start": v(-53.38, 0.2) * mm, "end": v(-52.52, -0.25) * mm});
            skLineSegment(sketch, "E1972", {"start": v(-52.52, -0.25) * mm, "end": v(-51.62, -0.86) * mm});
            skArc(sketch, "E1973", {"start": v(-55.98, 1.5) * mm, "mid": v(-55.77, 0.95) * mm, "end": v(-55.25, 0.71) * mm});
            skArc(sketch, "E1974", {"start": v(-55.98, 1.5) * mm, "mid": v(-55.98, 1.84) * mm, "end": v(-55.98, 2.2) * mm});
            skArc(sketch, "E1975", {"start": v(-55.25, 2.97) * mm, "mid": v(-55.77, 2.73) * mm, "end": v(-55.98, 2.2) * mm});
            skLineSegment(sketch, "E1976", {"start": v(-55.25, 2.97) * mm, "end": v(-54.83, 3) * mm});
            skLineSegment(sketch, "E1977", {"start": v(-54.83, 3) * mm, "end": v(-54.62, 3.04) * mm});
            skLineSegment(sketch, "E1978", {"start": v(-54.62, 3.04) * mm, "end": v(-54.36, 3.1) * mm});
            skLineSegment(sketch, "E1979", {"start": v(-54.36, 3.1) * mm, "end": v(-54.06, 3.2) * mm});
            skLineSegment(sketch, "E1980", {"start": v(-54.06, 3.2) * mm, "end": v(-53.73, 3.33) * mm});
            skLineSegment(sketch, "E1981", {"start": v(-53.73, 3.33) * mm, "end": v(-53.38, 3.48) * mm});
            skLineSegment(sketch, "E1982", {"start": v(-53.38, 3.48) * mm, "end": v(-52.52, 3.94) * mm});
            skLineSegment(sketch, "E1983", {"start": v(-52.52, 3.94) * mm, "end": v(-51.62, 4.54) * mm});
            skArc(sketch, "E1984", {"start": v(-51.62, 4.54) * mm, "mid": v(-51.7, 5.25) * mm, "end": v(-51.82, 5.95) * mm});
            skLineSegment(sketch, "E1985", {"start": v(-55.73, 6.48) * mm, "end": v(-55.32, 6.57) * mm});
            skLineSegment(sketch, "E1986", {"start": v(-55.32, 6.57) * mm, "end": v(-55.11, 6.59) * mm});
            skLineSegment(sketch, "E1987", {"start": v(-55.11, 6.59) * mm, "end": v(-54.84, 6.6) * mm});
            skLineSegment(sketch, "E1988", {"start": v(-54.84, 6.6) * mm, "end": v(-54.52, 6.58) * mm});
            skLineSegment(sketch, "E1989", {"start": v(-54.52, 6.58) * mm, "end": v(-54.17, 6.55) * mm});
            skLineSegment(sketch, "E1990", {"start": v(-62.17, 19.16) * mm, "end": v(-62.04, 19.48) * mm});
            skLineSegment(sketch, "E1991", {"start": v(-62.04, 19.48) * mm, "end": v(-61.91, 19.83) * mm});
            skLineSegment(sketch, "E1992", {"start": v(-61.91, 19.83) * mm, "end": v(-61.66, 20.78) * mm});
            skLineSegment(sketch, "E1993", {"start": v(-61.66, 20.78) * mm, "end": v(-61.49, 21.85) * mm});
            skArc(sketch, "E1994", {"start": v(-61.49, 21.85) * mm, "mid": v(-62.06, 22.27) * mm, "end": v(-62.64, 22.67) * mm});
            skLineSegment(sketch, "E1995", {"start": v(-65.7, 20.17) * mm, "end": v(-65.49, 20.53) * mm});
            skLineSegment(sketch, "E1996", {"start": v(-65.49, 20.53) * mm, "end": v(-65.36, 20.7) * mm});
            skLineSegment(sketch, "E1997", {"start": v(-65.36, 20.7) * mm, "end": v(-65.18, 20.9) * mm});
            skLineSegment(sketch, "E1998", {"start": v(-65.18, 20.9) * mm, "end": v(-64.95, 21.12) * mm});
            skLineSegment(sketch, "E1999", {"start": v(-64.95, 21.12) * mm, "end": v(-64.7, 21.36) * mm});
            skLineSegment(sketch, "E2000", {"start": v(-64.7, 21.36) * mm, "end": v(-64.4, 21.6) * mm});
            skLineSegment(sketch, "E2001", {"start": v(-64.4, 21.6) * mm, "end": v(-63.6, 22.15) * mm});
            skLineSegment(sketch, "E2002", {"start": v(-63.6, 22.15) * mm, "end": v(-62.64, 22.67) * mm});
            skArc(sketch, "E2003", {"start": v(-66.74, 19.88) * mm, "mid": v(-66.16, 19.82) * mm, "end": v(-65.7, 20.17) * mm});
            skArc(sketch, "E2004", {"start": v(-66.74, 19.88) * mm, "mid": v(-67.05, 20.04) * mm, "end": v(-67.36, 20.2) * mm});
            skArc(sketch, "E2005", {"start": v(-67.72, 21.2) * mm, "mid": v(-67.74, 20.63) * mm, "end": v(-67.36, 20.2) * mm});
            skLineSegment(sketch, "E2006", {"start": v(-67.72, 21.2) * mm, "end": v(-67.55, 21.6) * mm});
            skLineSegment(sketch, "E2007", {"start": v(-67.55, 21.6) * mm, "end": v(-67.49, 21.8) * mm});
            skLineSegment(sketch, "E2008", {"start": v(-67.49, 21.8) * mm, "end": v(-67.42, 22.06) * mm});
            skLineSegment(sketch, "E2009", {"start": v(-67.42, 22.06) * mm, "end": v(-67.37, 22.37) * mm});
            skLineSegment(sketch, "E2010", {"start": v(-67.37, 22.37) * mm, "end": v(-67.33, 22.72) * mm});
            skLineSegment(sketch, "E2011", {"start": v(-67.33, 22.72) * mm, "end": v(-67.3, 23.1) * mm});
            skLineSegment(sketch, "E2012", {"start": v(-67.3, 23.1) * mm, "end": v(-67.32, 24.08) * mm});
            skLineSegment(sketch, "E2013", {"start": v(-67.32, 24.08) * mm, "end": v(-67.44, 25.15) * mm});
            skArc(sketch, "E2014", {"start": v(-67.44, 25.15) * mm, "mid": v(-68.1, 25.4) * mm, "end": v(-68.78, 25.63) * mm});
            skLineSegment(sketch, "E2015", {"start": v(-71.05, 22.4) * mm, "end": v(-70.94, 22.8) * mm});
            skLineSegment(sketch, "E2016", {"start": v(-70.94, 22.8) * mm, "end": v(-70.86, 23) * mm});
            skLineSegment(sketch, "E2017", {"start": v(-70.86, 23) * mm, "end": v(-70.74, 23.24) * mm});
            skLineSegment(sketch, "E2018", {"start": v(-70.74, 23.24) * mm, "end": v(-70.58, 23.52) * mm});
            skLineSegment(sketch, "E2019", {"start": v(-70.58, 23.52) * mm, "end": v(-70.4, 23.81) * mm});
            skLineSegment(sketch, "E2020", {"start": v(-70.4, 23.81) * mm, "end": v(-70.18, 24.12) * mm});
            skLineSegment(sketch, "E2021", {"start": v(-70.18, 24.12) * mm, "end": v(-69.55, 24.87) * mm});
            skLineSegment(sketch, "E2022", {"start": v(-69.55, 24.87) * mm, "end": v(-68.78, 25.63) * mm});
            skArc(sketch, "E2023", {"start": v(-71.96, 21.84) * mm, "mid": v(-71.4, 21.93) * mm, "end": v(-71.05, 22.4) * mm});
            skArc(sketch, "E2024", {"start": v(-71.96, 21.84) * mm, "mid": v(-72.3, 21.91) * mm, "end": v(-72.65, 21.98) * mm});
            skArc(sketch, "E2025", {"start": v(-73.27, 22.85) * mm, "mid": v(-73.13, 22.3) * mm, "end": v(-72.65, 21.98) * mm});
            skLineSegment(sketch, "E2026", {"start": v(-73.27, 22.85) * mm, "end": v(-73.2, 23.27) * mm});
            skLineSegment(sketch, "E2027", {"start": v(-73.2, 23.27) * mm, "end": v(-73.2, 23.48) * mm});
            skLineSegment(sketch, "E2028", {"start": v(-73.2, 23.48) * mm, "end": v(-73.21, 23.75) * mm});
            skLineSegment(sketch, "E2029", {"start": v(-73.21, 23.75) * mm, "end": v(-73.25, 24.07) * mm});
            skLineSegment(sketch, "E2030", {"start": v(-73.25, 24.07) * mm, "end": v(-73.3, 24.42) * mm});
            skLineSegment(sketch, "E2031", {"start": v(-73.3, 24.42) * mm, "end": v(-73.38, 24.78) * mm});
            skLineSegment(sketch, "E2032", {"start": v(-73.38, 24.78) * mm, "end": v(-73.66, 25.72) * mm});
            skLineSegment(sketch, "E2033", {"start": v(-73.66, 25.72) * mm, "end": v(-74.06, 26.73) * mm});
            skArc(sketch, "E2034", {"start": v(-74.06, 26.73) * mm, "mid": v(-74.77, 26.78) * mm, "end": v(-75.48, 26.82) * mm});
            skLineSegment(sketch, "E2035", {"start": v(-76.8, 23.1) * mm, "end": v(-76.8, 23.52) * mm});
            skLineSegment(sketch, "E2036", {"start": v(-76.8, 23.52) * mm, "end": v(-76.77, 23.73) * mm});
            skLineSegment(sketch, "E2037", {"start": v(-76.77, 23.73) * mm, "end": v(-76.72, 24) * mm});
            skLineSegment(sketch, "E2038", {"start": v(-76.72, 24) * mm, "end": v(-76.65, 24.3) * mm});
            skLineSegment(sketch, "E2039", {"start": v(-76.65, 24.3) * mm, "end": v(-76.55, 24.64) * mm});
            skLineSegment(sketch, "E2040", {"start": v(-76.55, 24.64) * mm, "end": v(-76.42, 25) * mm});
            skLineSegment(sketch, "E2041", {"start": v(-76.42, 25) * mm, "end": v(-76.02, 25.88) * mm});
            skLineSegment(sketch, "E2042", {"start": v(-76.02, 25.88) * mm, "end": v(-75.48, 26.82) * mm});
            skArc(sketch, "E2043", {"start": v(-77.53, 22.32) * mm, "mid": v(-77, 22.56) * mm, "end": v(-76.8, 23.1) * mm});
            skArc(sketch, "E2044", {"start": v(-77.53, 22.32) * mm, "mid": v(-77.88, 22.3) * mm, "end": v(-78.22, 22.27) * mm});
            skArc(sketch, "E2045", {"start": v(-79.05, 22.94) * mm, "mid": v(-78.78, 22.44) * mm, "end": v(-78.22, 22.27) * mm});
            skLineSegment(sketch, "E2046", {"start": v(-79.05, 22.94) * mm, "end": v(-79.11, 23.36) * mm});
            skLineSegment(sketch, "E2047", {"start": v(-79.11, 23.36) * mm, "end": v(-79.16, 23.56) * mm});
            skLineSegment(sketch, "E2048", {"start": v(-79.16, 23.56) * mm, "end": v(-79.25, 23.82) * mm});
            skLineSegment(sketch, "E2049", {"start": v(-79.25, 23.82) * mm, "end": v(-79.36, 24.12) * mm});
            skLineSegment(sketch, "E2050", {"start": v(-79.36, 24.12) * mm, "end": v(-79.5, 24.43) * mm});
            skLineSegment(sketch, "E2051", {"start": v(-79.5, 24.43) * mm, "end": v(-79.68, 24.77) * mm});
            skLineSegment(sketch, "E2052", {"start": v(-79.68, 24.77) * mm, "end": v(-80.2, 25.6) * mm});
            skLineSegment(sketch, "E2053", {"start": v(-80.2, 25.6) * mm, "end": v(-80.87, 26.45) * mm});
            skArc(sketch, "E2054", {"start": v(-80.87, 26.45) * mm, "mid": v(-81.56, 26.32) * mm, "end": v(-82.26, 26.17) * mm});
            skLineSegment(sketch, "E2055", {"start": v(-82.52, 22.22) * mm, "end": v(-82.63, 22.63) * mm});
            skLineSegment(sketch, "E2056", {"start": v(-82.63, 22.63) * mm, "end": v(-82.67, 22.83) * mm});
            skLineSegment(sketch, "E2057", {"start": v(-82.67, 22.83) * mm, "end": v(-82.7, 23.1) * mm});
            skLineSegment(sketch, "E2058", {"start": v(-82.7, 23.1) * mm, "end": v(-82.7, 23.42) * mm});
            skLineSegment(sketch, "E2059", {"start": v(-82.7, 23.42) * mm, "end": v(-82.7, 23.77) * mm});
            skLineSegment(sketch, "E2060", {"start": v(-82.7, 23.77) * mm, "end": v(-82.67, 24.15) * mm});
            skLineSegment(sketch, "E2061", {"start": v(-82.67, 24.15) * mm, "end": v(-82.52, 25.12) * mm});
            skLineSegment(sketch, "E2062", {"start": v(-82.52, 25.12) * mm, "end": v(-82.26, 26.17) * mm});
            skArc(sketch, "E2063", {"start": v(-83.01, 21.27) * mm, "mid": v(-82.57, 21.65) * mm, "end": v(-82.52, 22.22) * mm});
            skArc(sketch, "E2064", {"start": v(-83.01, 21.27) * mm, "mid": v(-83.34, 21.16) * mm, "end": v(-83.67, 21.04) * mm});
            skArc(sketch, "E2065", {"start": v(-84.65, 21.46) * mm, "mid": v(-84.25, 21.05) * mm, "end": v(-83.67, 21.04) * mm});
            skLineSegment(sketch, "E2066", {"start": v(-84.65, 21.46) * mm, "end": v(-84.82, 21.85) * mm});
            skLineSegment(sketch, "E2067", {"start": v(-84.82, 21.85) * mm, "end": v(-84.92, 22.03) * mm});
            skLineSegment(sketch, "E2068", {"start": v(-84.92, 22.03) * mm, "end": v(-85.07, 22.26) * mm});
            skLineSegment(sketch, "E2069", {"start": v(-85.07, 22.26) * mm, "end": v(-85.27, 22.51) * mm});
            skLineSegment(sketch, "E2070", {"start": v(-85.27, 22.51) * mm, "end": v(-85.5, 22.78) * mm});
            skLineSegment(sketch, "E2071", {"start": v(-85.5, 22.78) * mm, "end": v(-85.75, 23.05) * mm});
            skLineSegment(sketch, "E2072", {"start": v(-85.75, 23.05) * mm, "end": v(-86.47, 23.71) * mm});
            skLineSegment(sketch, "E2073", {"start": v(-86.47, 23.71) * mm, "end": v(-87.34, 24.36) * mm});
            skArc(sketch, "E2074", {"start": v(-87.34, 24.36) * mm, "mid": v(-87.98, 24.04) * mm, "end": v(-88.6, 23.7) * mm});
            skLineSegment(sketch, "E2075", {"start": v(-87.8, 19.84) * mm, "end": v(-88.01, 20.2) * mm});
            skLineSegment(sketch, "E2076", {"start": v(-88.01, 20.2) * mm, "end": v(-88.1, 20.39) * mm});
            skLineSegment(sketch, "E2077", {"start": v(-88.1, 20.39) * mm, "end": v(-88.2, 20.64) * mm});
            skLineSegment(sketch, "E2078", {"start": v(-88.2, 20.64) * mm, "end": v(-88.3, 20.94) * mm});
            skLineSegment(sketch, "E2079", {"start": v(-88.3, 20.94) * mm, "end": v(-88.38, 21.28) * mm});
            skLineSegment(sketch, "E2080", {"start": v(-88.38, 21.28) * mm, "end": v(-88.46, 21.65) * mm});
            skLineSegment(sketch, "E2081", {"start": v(-88.46, 21.65) * mm, "end": v(-88.58, 22.62) * mm});
            skLineSegment(sketch, "E2082", {"start": v(-88.58, 22.62) * mm, "end": v(-88.6, 23.7) * mm});
            skArc(sketch, "E2083", {"start": v(-88.01, 18.79) * mm, "mid": v(-87.7, 19.27) * mm, "end": v(-87.8, 19.84) * mm});
            skArc(sketch, "E2084", {"start": v(-88.01, 18.79) * mm, "mid": v(-88.3, 18.6) * mm, "end": v(-88.58, 18.39) * mm});
            skArc(sketch, "E2085", {"start": v(-89.64, 18.53) * mm, "mid": v(-89.14, 18.24) * mm, "end": v(-88.58, 18.39) * mm});
            skLineSegment(sketch, "E2086", {"start": v(-89.64, 18.53) * mm, "end": v(-89.9, 18.86) * mm});
            skLineSegment(sketch, "E2087", {"start": v(-89.9, 18.86) * mm, "end": v(-90.06, 19) * mm});
            skLineSegment(sketch, "E2088", {"start": v(-90.06, 19) * mm, "end": v(-90.26, 19.18) * mm});
            skLineSegment(sketch, "E2089", {"start": v(-90.26, 19.18) * mm, "end": v(-90.52, 19.37) * mm});
            skLineSegment(sketch, "E2090", {"start": v(-90.52, 19.37) * mm, "end": v(-90.8, 19.57) * mm});
            skLineSegment(sketch, "E2091", {"start": v(-90.8, 19.57) * mm, "end": v(-91.13, 19.76) * mm});
            skLineSegment(sketch, "E2092", {"start": v(-73.46, -93.1) * mm, "end": v(-72.87, -94.02) * mm});
            skArc(sketch, "E2093", {"start": v(-72.87, -94.02) * mm, "mid": v(-72.16, -93.94) * mm, "end": v(-71.45, -93.83) * mm});
            skLineSegment(sketch, "E2094", {"start": v(-70.88, -89.91) * mm, "end": v(-70.8, -90.32) * mm});
            skLineSegment(sketch, "E2095", {"start": v(-70.8, -90.32) * mm, "end": v(-70.79, -90.6) * mm});
            skLineSegment(sketch, "E2096", {"start": v(-70.79, -90.6) * mm, "end": v(-70.8, -90.97) * mm});
            skLineSegment(sketch, "E2097", {"start": v(-70.8, -90.97) * mm, "end": v(-70.83, -91.38) * mm});
            skLineSegment(sketch, "E2098", {"start": v(-70.83, -91.38) * mm, "end": v(-70.89, -91.83) * mm});
            skLineSegment(sketch, "E2099", {"start": v(-70.89, -91.83) * mm, "end": v(-71.1, -92.8) * mm});
            skLineSegment(sketch, "E2100", {"start": v(-71.1, -92.8) * mm, "end": v(-71.45, -93.83) * mm});
            skArc(sketch, "E2101", {"start": v(-70.32, -89.01) * mm, "mid": v(-70.78, -89.35) * mm, "end": v(-70.88, -89.91) * mm});
            skArc(sketch, "E2102", {"start": v(-70.32, -89.01) * mm, "mid": v(-69.99, -88.93) * mm, "end": v(-69.65, -88.83) * mm});
            skArc(sketch, "E2103", {"start": v(-68.71, -89.33) * mm, "mid": v(-69.08, -88.9) * mm, "end": v(-69.65, -88.83) * mm});
            skLineSegment(sketch, "E2104", {"start": v(-68.71, -89.33) * mm, "end": v(-68.58, -89.72) * mm});
            skLineSegment(sketch, "E2105", {"start": v(-68.58, -89.72) * mm, "end": v(-68.45, -89.98) * mm});
            skLineSegment(sketch, "E2106", {"start": v(-68.45, -89.98) * mm, "end": v(-68.26, -90.3) * mm});
            skLineSegment(sketch, "E2107", {"start": v(-68.26, -90.3) * mm, "end": v(-68.03, -90.63) * mm});
            skLineSegment(sketch, "E2108", {"start": v(-68.03, -90.63) * mm, "end": v(-67.75, -91) * mm});
            skLineSegment(sketch, "E2109", {"start": v(-67.75, -91) * mm, "end": v(-67.08, -91.72) * mm});
            skLineSegment(sketch, "E2110", {"start": v(-67.08, -91.72) * mm, "end": v(-66.26, -92.44) * mm});
            skArc(sketch, "E2111", {"start": v(-66.26, -92.44) * mm, "mid": v(-65.6, -92.18) * mm, "end": v(-64.94, -91.9) * mm});
            skLineSegment(sketch, "E2112", {"start": v(-65.41, -87.96) * mm, "end": v(-65.23, -88.34) * mm});
            skLineSegment(sketch, "E2113", {"start": v(-65.23, -88.34) * mm, "end": v(-65.14, -88.61) * mm});
            skLineSegment(sketch, "E2114", {"start": v(-65.14, -88.61) * mm, "end": v(-65.05, -88.96) * mm});
            skLineSegment(sketch, "E2115", {"start": v(-65.05, -88.96) * mm, "end": v(-64.98, -89.37) * mm});
            skLineSegment(sketch, "E2116", {"start": v(-64.98, -89.37) * mm, "end": v(-64.92, -89.82) * mm});
            skLineSegment(sketch, "E2117", {"start": v(-64.92, -89.82) * mm, "end": v(-64.88, -90.8) * mm});
            skLineSegment(sketch, "E2118", {"start": v(-64.88, -90.8) * mm, "end": v(-64.94, -91.9) * mm});
            skArc(sketch, "E2119", {"start": v(-65.1, -86.95) * mm, "mid": v(-65.46, -87.4) * mm, "end": v(-65.41, -87.96) * mm});
            skArc(sketch, "E2120", {"start": v(-65.1, -86.95) * mm, "mid": v(-64.8, -86.78) * mm, "end": v(-64.5, -86.6) * mm});
            skArc(sketch, "E2121", {"start": v(-63.47, -86.84) * mm, "mid": v(-63.94, -86.51) * mm, "end": v(-64.5, -86.6) * mm});
            skLineSegment(sketch, "E2122", {"start": v(-63.47, -86.84) * mm, "end": v(-63.23, -87.18) * mm});
            skLineSegment(sketch, "E2123", {"start": v(-63.23, -87.18) * mm, "end": v(-63.04, -87.4) * mm});
            skLineSegment(sketch, "E2124", {"start": v(-63.04, -87.4) * mm, "end": v(-62.78, -87.65) * mm});
            skLineSegment(sketch, "E2125", {"start": v(-62.78, -87.65) * mm, "end": v(-62.47, -87.92) * mm});
            skLineSegment(sketch, "E2126", {"start": v(-62.47, -87.92) * mm, "end": v(-62.1, -88.2) * mm});
            skLineSegment(sketch, "E2127", {"start": v(-62.1, -88.2) * mm, "end": v(-61.27, -88.72) * mm});
            skLineSegment(sketch, "E2128", {"start": v(-61.27, -88.72) * mm, "end": v(-60.3, -89.21) * mm});
            skArc(sketch, "E2129", {"start": v(-60.3, -89.21) * mm, "mid": v(-59.72, -88.78) * mm, "end": v(-59.16, -88.34) * mm});
            skLineSegment(sketch, "E2130", {"start": v(-60.63, -84.66) * mm, "end": v(-60.36, -84.98) * mm});
            skLineSegment(sketch, "E2131", {"start": v(-60.36, -84.98) * mm, "end": v(-60.2, -85.22) * mm});
            skLineSegment(sketch, "E2132", {"start": v(-60.2, -85.22) * mm, "end": v(-60.02, -85.54) * mm});
            skLineSegment(sketch, "E2133", {"start": v(-60.02, -85.54) * mm, "end": v(-59.85, -85.9) * mm});
            skLineSegment(sketch, "E2134", {"start": v(-59.85, -85.9) * mm, "end": v(-59.68, -86.33) * mm});
            skLineSegment(sketch, "E2135", {"start": v(-59.68, -86.33) * mm, "end": v(-59.38, -87.27) * mm});
            skLineSegment(sketch, "E2136", {"start": v(-59.38, -87.27) * mm, "end": v(-59.16, -88.34) * mm});
            skArc(sketch, "E2137", {"start": v(-60.6, -83.6) * mm, "mid": v(-60.83, -84.13) * mm, "end": v(-60.63, -84.66) * mm});
            skArc(sketch, "E2138", {"start": v(-60.6, -83.6) * mm, "mid": v(-60.35, -83.36) * mm, "end": v(-60.1, -83.11) * mm});
            skArc(sketch, "E2139", {"start": v(-59.04, -83.08) * mm, "mid": v(-59.58, -82.88) * mm, "end": v(-60.1, -83.11) * mm});
            skLineSegment(sketch, "E2140", {"start": v(-59.04, -83.08) * mm, "end": v(-58.73, -83.35) * mm});
            skLineSegment(sketch, "E2141", {"start": v(-58.73, -83.35) * mm, "end": v(-58.49, -83.5) * mm});
            skLineSegment(sketch, "E2142", {"start": v(-58.49, -83.5) * mm, "end": v(-58.17, -83.68) * mm});
            skLineSegment(sketch, "E2143", {"start": v(-58.17, -83.68) * mm, "end": v(-57.8, -83.86) * mm});
            skLineSegment(sketch, "E2144", {"start": v(-57.8, -83.86) * mm, "end": v(-57.38, -84.03) * mm});
            skLineSegment(sketch, "E2145", {"start": v(-57.38, -84.03) * mm, "end": v(-56.43, -84.32) * mm});
            skLineSegment(sketch, "E2146", {"start": v(-56.43, -84.32) * mm, "end": v(-55.36, -84.55) * mm});
            skArc(sketch, "E2147", {"start": v(-55.36, -84.55) * mm, "mid": v(-54.92, -83.99) * mm, "end": v(-54.5, -83.41) * mm});
            skLineSegment(sketch, "E2148", {"start": v(-56.87, -80.24) * mm, "end": v(-56.52, -80.47) * mm});
            skLineSegment(sketch, "E2149", {"start": v(-56.52, -80.47) * mm, "end": v(-56.3, -80.67) * mm});
            skLineSegment(sketch, "E2150", {"start": v(-56.3, -80.67) * mm, "end": v(-56.05, -80.93) * mm});
            skLineSegment(sketch, "E2151", {"start": v(-56.05, -80.93) * mm, "end": v(-55.79, -81.24) * mm});
            skLineSegment(sketch, "E2152", {"start": v(-55.79, -81.24) * mm, "end": v(-55.51, -81.6) * mm});
            skLineSegment(sketch, "E2153", {"start": v(-55.51, -81.6) * mm, "end": v(-54.99, -82.44) * mm});
            skLineSegment(sketch, "E2154", {"start": v(-54.99, -82.44) * mm, "end": v(-54.5, -83.41) * mm});
            skArc(sketch, "E2155", {"start": v(-57.1, -79.2) * mm, "mid": v(-57.2, -79.77) * mm, "end": v(-56.87, -80.24) * mm});
            skArc(sketch, "E2156", {"start": v(-57.1, -79.2) * mm, "mid": v(-56.93, -78.9) * mm, "end": v(-56.76, -78.6) * mm});
            skArc(sketch, "E2157", {"start": v(-55.74, -78.3) * mm, "mid": v(-56.31, -78.25) * mm, "end": v(-56.76, -78.6) * mm});
            skLineSegment(sketch, "E2158", {"start": v(-55.74, -78.3) * mm, "end": v(-55.37, -78.48) * mm});
            skLineSegment(sketch, "E2159", {"start": v(-55.37, -78.48) * mm, "end": v(-55.1, -78.57) * mm});
            skLineSegment(sketch, "E2160", {"start": v(-55.1, -78.57) * mm, "end": v(-54.74, -78.66) * mm});
            skLineSegment(sketch, "E2161", {"start": v(-54.74, -78.66) * mm, "end": v(-54.34, -78.73) * mm});
            skLineSegment(sketch, "E2162", {"start": v(-54.34, -78.73) * mm, "end": v(-53.89, -78.79) * mm});
            skLineSegment(sketch, "E2163", {"start": v(-53.89, -78.79) * mm, "end": v(-52.9, -78.83) * mm});
            skLineSegment(sketch, "E2164", {"start": v(-52.9, -78.83) * mm, "end": v(-51.81, -78.76) * mm});
            skArc(sketch, "E2165", {"start": v(-51.81, -78.76) * mm, "mid": v(-51.53, -78.1) * mm, "end": v(-51.26, -77.44) * mm});
            skLineSegment(sketch, "E2166", {"start": v(-54.38, -75) * mm, "end": v(-53.99, -75.13) * mm});
            skLineSegment(sketch, "E2167", {"start": v(-53.99, -75.13) * mm, "end": v(-53.72, -75.26) * mm});
            skLineSegment(sketch, "E2168", {"start": v(-53.72, -75.26) * mm, "end": v(-53.41, -75.44) * mm});
            skLineSegment(sketch, "E2169", {"start": v(-53.41, -75.44) * mm, "end": v(-53.07, -75.68) * mm});
            skLineSegment(sketch, "E2170", {"start": v(-53.07, -75.68) * mm, "end": v(-52.72, -75.96) * mm});
            skLineSegment(sketch, "E2171", {"start": v(-52.72, -75.96) * mm, "end": v(-52, -76.63) * mm});
            skLineSegment(sketch, "E2172", {"start": v(-52, -76.63) * mm, "end": v(-51.26, -77.44) * mm});
            skArc(sketch, "E2173", {"start": v(-54.87, -74.06) * mm, "mid": v(-54.81, -74.63) * mm, "end": v(-54.38, -75) * mm});
            skArc(sketch, "E2174", {"start": v(-54.87, -74.06) * mm, "mid": v(-54.78, -73.72) * mm, "end": v(-54.7, -73.39) * mm});
            skArc(sketch, "E2175", {"start": v(-53.8, -72.83) * mm, "mid": v(-54.36, -72.92) * mm, "end": v(-54.7, -73.39) * mm});
            skLineSegment(sketch, "E2176", {"start": v(-53.8, -72.83) * mm, "end": v(-53.39, -72.9) * mm});
            skLineSegment(sketch, "E2177", {"start": v(-53.39, -72.9) * mm, "end": v(-53.1, -72.92) * mm});
            skLineSegment(sketch, "E2178", {"start": v(-53.1, -72.92) * mm, "end": v(-52.74, -72.92) * mm});
            skLineSegment(sketch, "E2179", {"start": v(-52.74, -72.92) * mm, "end": v(-52.32, -72.88) * mm});
            skLineSegment(sketch, "E2180", {"start": v(-52.32, -72.88) * mm, "end": v(-51.88, -72.82) * mm});
            skLineSegment(sketch, "E2181", {"start": v(-51.88, -72.82) * mm, "end": v(-50.91, -72.6) * mm});
            skLineSegment(sketch, "E2182", {"start": v(-50.91, -72.6) * mm, "end": v(-49.88, -72.26) * mm});
            skArc(sketch, "E2183", {"start": v(-49.88, -72.26) * mm, "mid": v(-49.77, -71.55) * mm, "end": v(-49.69, -70.84) * mm});
            skLineSegment(sketch, "E2184", {"start": v(-53.33, -69.28) * mm, "end": v(-52.92, -69.31) * mm});
            skLineSegment(sketch, "E2185", {"start": v(-52.92, -69.31) * mm, "end": v(-52.63, -69.37) * mm});
            skLineSegment(sketch, "E2186", {"start": v(-52.63, -69.37) * mm, "end": v(-52.28, -69.47) * mm});
            skLineSegment(sketch, "E2187", {"start": v(-52.28, -69.47) * mm, "end": v(-51.9, -69.6) * mm});
            skLineSegment(sketch, "E2188", {"start": v(-51.9, -69.6) * mm, "end": v(-51.48, -69.78) * mm});
            skLineSegment(sketch, "E2189", {"start": v(-51.48, -69.78) * mm, "end": v(-50.6, -70.24) * mm});
            skLineSegment(sketch, "E2190", {"start": v(-50.6, -70.24) * mm, "end": v(-49.69, -70.84) * mm});
            skArc(sketch, "E2191", {"start": v(-54.05, -68.5) * mm, "mid": v(-53.85, -69.04) * mm, "end": v(-53.33, -69.28) * mm});
            skArc(sketch, "E2192", {"start": v(-54.05, -68.5) * mm, "mid": v(-54.05, -68.16) * mm, "end": v(-54.05, -67.81) * mm});
            skArc(sketch, "E2193", {"start": v(-53.33, -67.04) * mm, "mid": v(-53.85, -67.28) * mm, "end": v(-54.05, -67.81) * mm});
            skLineSegment(sketch, "E2194", {"start": v(-53.33, -67.04) * mm, "end": v(-52.92, -67) * mm});
            skLineSegment(sketch, "E2195", {"start": v(-52.92, -67) * mm, "end": v(-52.63, -66.95) * mm});
            skLineSegment(sketch, "E2196", {"start": v(-52.63, -66.95) * mm, "end": v(-52.28, -66.85) * mm});
            skLineSegment(sketch, "E2197", {"start": v(-52.28, -66.85) * mm, "end": v(-51.9, -66.7) * mm});
            skLineSegment(sketch, "E2198", {"start": v(-51.9, -66.7) * mm, "end": v(-51.48, -66.53) * mm});
            skLineSegment(sketch, "E2199", {"start": v(-51.48, -66.53) * mm, "end": v(-50.6, -66.07) * mm});
            skLineSegment(sketch, "E2200", {"start": v(-50.6, -66.07) * mm, "end": v(-49.69, -65.47) * mm});
            skArc(sketch, "E2201", {"start": v(-49.69, -65.47) * mm, "mid": v(-49.77, -64.76) * mm, "end": v(-49.88, -64.06) * mm});
            skLineSegment(sketch, "E2202", {"start": v(-53.8, -63.5) * mm, "end": v(-53.39, -63.41) * mm});
            skLineSegment(sketch, "E2203", {"start": v(-53.39, -63.41) * mm, "end": v(-53.1, -63.4) * mm});
            skLineSegment(sketch, "E2204", {"start": v(-53.1, -63.4) * mm, "end": v(-52.74, -63.4) * mm});
            skLineSegment(sketch, "E2205", {"start": v(-52.74, -63.4) * mm, "end": v(-52.32, -63.43) * mm});
            skLineSegment(sketch, "E2206", {"start": v(-52.32, -63.43) * mm, "end": v(-51.88, -63.5) * mm});
            skLineSegment(sketch, "E2207", {"start": v(-51.88, -63.5) * mm, "end": v(-50.91, -63.71) * mm});
            skLineSegment(sketch, "E2208", {"start": v(-50.91, -63.71) * mm, "end": v(-49.88, -64.06) * mm});
            skArc(sketch, "E2209", {"start": v(-54.7, -62.93) * mm, "mid": v(-54.36, -63.4) * mm, "end": v(-53.8, -63.5) * mm});
            skArc(sketch, "E2210", {"start": v(-54.7, -62.93) * mm, "mid": v(-54.78, -62.6) * mm, "end": v(-54.87, -62.26) * mm});
            skArc(sketch, "E2211", {"start": v(-54.38, -61.32) * mm, "mid": v(-54.81, -61.7) * mm, "end": v(-54.87, -62.26) * mm});
            skLineSegment(sketch, "E2212", {"start": v(-54.38, -61.32) * mm, "end": v(-53.99, -61.19) * mm});
            skLineSegment(sketch, "E2213", {"start": v(-53.99, -61.19) * mm, "end": v(-53.72, -61.06) * mm});
            skLineSegment(sketch, "E2214", {"start": v(-53.72, -61.06) * mm, "end": v(-53.41, -60.87) * mm});
            skLineSegment(sketch, "E2215", {"start": v(-53.41, -60.87) * mm, "end": v(-53.07, -60.64) * mm});
            skLineSegment(sketch, "E2216", {"start": v(-53.07, -60.64) * mm, "end": v(-52.72, -60.36) * mm});
            skLineSegment(sketch, "E2217", {"start": v(-52.72, -60.36) * mm, "end": v(-52, -59.69) * mm});
            skLineSegment(sketch, "E2218", {"start": v(-52, -59.69) * mm, "end": v(-51.26, -58.87) * mm});
            skArc(sketch, "E2219", {"start": v(-51.26, -58.87) * mm, "mid": v(-51.53, -58.2) * mm, "end": v(-51.81, -57.55) * mm});
            skLineSegment(sketch, "E2220", {"start": v(-55.74, -58.02) * mm, "end": v(-55.37, -57.84) * mm});
            skLineSegment(sketch, "E2221", {"start": v(-55.37, -57.84) * mm, "end": v(-55.1, -57.75) * mm});
            skLineSegment(sketch, "E2222", {"start": v(-55.1, -57.75) * mm, "end": v(-54.74, -57.66) * mm});
            skLineSegment(sketch, "E2223", {"start": v(-54.74, -57.66) * mm, "end": v(-54.34, -57.58) * mm});
            skLineSegment(sketch, "E2224", {"start": v(-54.34, -57.58) * mm, "end": v(-53.89, -57.53) * mm});
            skLineSegment(sketch, "E2225", {"start": v(-53.89, -57.53) * mm, "end": v(-52.9, -57.49) * mm});
            skLineSegment(sketch, "E2226", {"start": v(-52.9, -57.49) * mm, "end": v(-51.81, -57.55) * mm});
            skArc(sketch, "E2227", {"start": v(-56.76, -57.7) * mm, "mid": v(-56.31, -58.07) * mm, "end": v(-55.74, -58.02) * mm});
            skArc(sketch, "E2228", {"start": v(-56.76, -57.7) * mm, "mid": v(-56.93, -57.4) * mm, "end": v(-57.1, -57.1) * mm});
            skArc(sketch, "E2229", {"start": v(-56.87, -56.08) * mm, "mid": v(-57.2, -56.54) * mm, "end": v(-57.1, -57.1) * mm});
            skLineSegment(sketch, "E2230", {"start": v(-56.87, -56.08) * mm, "end": v(-56.52, -55.84) * mm});
            skLineSegment(sketch, "E2231", {"start": v(-56.52, -55.84) * mm, "end": v(-56.3, -55.65) * mm});
            skLineSegment(sketch, "E2232", {"start": v(-56.3, -55.65) * mm, "end": v(-56.05, -55.4) * mm});
            skLineSegment(sketch, "E2233", {"start": v(-56.05, -55.4) * mm, "end": v(-55.79, -55.08) * mm});
            skLineSegment(sketch, "E2234", {"start": v(-55.79, -55.08) * mm, "end": v(-55.51, -54.71) * mm});
            skLineSegment(sketch, "E2235", {"start": v(-55.51, -54.71) * mm, "end": v(-54.99, -53.88) * mm});
            skLineSegment(sketch, "E2236", {"start": v(-54.99, -53.88) * mm, "end": v(-54.5, -52.9) * mm});
            skArc(sketch, "E2237", {"start": v(-54.5, -52.9) * mm, "mid": v(-54.92, -52.33) * mm, "end": v(-55.36, -51.77) * mm});
            skLineSegment(sketch, "E2238", {"start": v(-59.04, -53.24) * mm, "end": v(-58.73, -52.97) * mm});
            skLineSegment(sketch, "E2239", {"start": v(-58.73, -52.97) * mm, "end": v(-58.49, -52.8) * mm});
            skLineSegment(sketch, "E2240", {"start": v(-58.49, -52.8) * mm, "end": v(-58.17, -52.63) * mm});
            skLineSegment(sketch, "E2241", {"start": v(-58.17, -52.63) * mm, "end": v(-57.8, -52.45) * mm});
            skLineSegment(sketch, "E2242", {"start": v(-57.8, -52.45) * mm, "end": v(-57.38, -52.28) * mm});
            skLineSegment(sketch, "E2243", {"start": v(-57.38, -52.28) * mm, "end": v(-56.43, -52) * mm});
            skLineSegment(sketch, "E2244", {"start": v(-56.43, -52) * mm, "end": v(-55.36, -51.77) * mm});
            skArc(sketch, "E2245", {"start": v(-60.1, -53.2) * mm, "mid": v(-59.58, -53.43) * mm, "end": v(-59.04, -53.24) * mm});
            skArc(sketch, "E2246", {"start": v(-60.1, -53.2) * mm, "mid": v(-60.35, -52.96) * mm, "end": v(-60.6, -52.71) * mm});
            skArc(sketch, "E2247", {"start": v(-60.63, -51.65) * mm, "mid": v(-60.83, -52.19) * mm, "end": v(-60.6, -52.71) * mm});
            skLineSegment(sketch, "E2248", {"start": v(-60.63, -51.65) * mm, "end": v(-60.36, -51.34) * mm});
            skLineSegment(sketch, "E2249", {"start": v(-60.36, -51.34) * mm, "end": v(-60.2, -51.1) * mm});
            skLineSegment(sketch, "E2250", {"start": v(-60.2, -51.1) * mm, "end": v(-60.02, -50.78) * mm});
            skLineSegment(sketch, "E2251", {"start": v(-60.02, -50.78) * mm, "end": v(-59.85, -50.4) * mm});
            skLineSegment(sketch, "E2252", {"start": v(-59.85, -50.4) * mm, "end": v(-59.68, -49.99) * mm});
            skLineSegment(sketch, "E2253", {"start": v(-59.68, -49.99) * mm, "end": v(-59.38, -49.04) * mm});
            skLineSegment(sketch, "E2254", {"start": v(-59.38, -49.04) * mm, "end": v(-59.16, -47.97) * mm});
            skArc(sketch, "E2255", {"start": v(-59.16, -47.97) * mm, "mid": v(-59.72, -47.53) * mm, "end": v(-60.3, -47.1) * mm});
            skLineSegment(sketch, "E2256", {"start": v(-63.47, -49.47) * mm, "end": v(-63.23, -49.13) * mm});
            skLineSegment(sketch, "E2257", {"start": v(-63.23, -49.13) * mm, "end": v(-63.04, -48.91) * mm});
            skLineSegment(sketch, "E2258", {"start": v(-63.04, -48.91) * mm, "end": v(-62.78, -48.66) * mm});
            skLineSegment(sketch, "E2259", {"start": v(-62.78, -48.66) * mm, "end": v(-62.47, -48.4) * mm});
            skLineSegment(sketch, "E2260", {"start": v(-62.47, -48.4) * mm, "end": v(-62.1, -48.12) * mm});
            skLineSegment(sketch, "E2261", {"start": v(-62.1, -48.12) * mm, "end": v(-61.27, -47.6) * mm});
            skLineSegment(sketch, "E2262", {"start": v(-61.27, -47.6) * mm, "end": v(-60.3, -47.1) * mm});
            skArc(sketch, "E2263", {"start": v(-64.5, -49.71) * mm, "mid": v(-63.94, -49.8) * mm, "end": v(-63.47, -49.47) * mm});
            skArc(sketch, "E2264", {"start": v(-64.5, -49.71) * mm, "mid": v(-64.8, -49.54) * mm, "end": v(-65.1, -49.37) * mm});
            skArc(sketch, "E2265", {"start": v(-65.41, -48.35) * mm, "mid": v(-65.46, -48.92) * mm, "end": v(-65.1, -49.37) * mm});
            skLineSegment(sketch, "E2266", {"start": v(-65.41, -48.35) * mm, "end": v(-65.23, -47.98) * mm});
            skLineSegment(sketch, "E2267", {"start": v(-65.23, -47.98) * mm, "end": v(-65.14, -47.7) * mm});
            skLineSegment(sketch, "E2268", {"start": v(-65.14, -47.7) * mm, "end": v(-65.05, -47.35) * mm});
            skLineSegment(sketch, "E2269", {"start": v(-65.05, -47.35) * mm, "end": v(-64.98, -46.95) * mm});
            skLineSegment(sketch, "E2270", {"start": v(-64.98, -46.95) * mm, "end": v(-64.92, -46.5) * mm});
            skLineSegment(sketch, "E2271", {"start": v(-64.92, -46.5) * mm, "end": v(-64.88, -45.51) * mm});
            skLineSegment(sketch, "E2272", {"start": v(-64.88, -45.51) * mm, "end": v(-64.94, -44.42) * mm});
            skArc(sketch, "E2273", {"start": v(-64.94, -44.42) * mm, "mid": v(-65.6, -44.14) * mm, "end": v(-66.26, -43.87) * mm});
            skLineSegment(sketch, "E2274", {"start": v(-68.71, -46.98) * mm, "end": v(-68.58, -46.6) * mm});
            skLineSegment(sketch, "E2275", {"start": v(-68.58, -46.6) * mm, "end": v(-68.45, -46.33) * mm});
            skLineSegment(sketch, "E2276", {"start": v(-68.45, -46.33) * mm, "end": v(-68.26, -46.02) * mm});
            skLineSegment(sketch, "E2277", {"start": v(-68.26, -46.02) * mm, "end": v(-68.03, -45.68) * mm});
            skLineSegment(sketch, "E2278", {"start": v(-68.03, -45.68) * mm, "end": v(-67.75, -45.32) * mm});
            skLineSegment(sketch, "E2279", {"start": v(-67.75, -45.32) * mm, "end": v(-67.08, -44.6) * mm});
            skLineSegment(sketch, "E2280", {"start": v(-67.08, -44.6) * mm, "end": v(-66.26, -43.87) * mm});
            skArc(sketch, "E2281", {"start": v(-69.65, -47.48) * mm, "mid": v(-69.08, -47.42) * mm, "end": v(-68.71, -46.98) * mm});
            skArc(sketch, "E2282", {"start": v(-69.65, -47.48) * mm, "mid": v(-69.99, -47.4) * mm, "end": v(-70.32, -47.3) * mm});
            skArc(sketch, "E2283", {"start": v(-70.88, -46.4) * mm, "mid": v(-70.78, -46.97) * mm, "end": v(-70.32, -47.3) * mm});
            skLineSegment(sketch, "E2284", {"start": v(-70.88, -46.4) * mm, "end": v(-70.8, -46) * mm});
            skLineSegment(sketch, "E2285", {"start": v(-70.8, -46) * mm, "end": v(-70.79, -45.7) * mm});
            skLineSegment(sketch, "E2286", {"start": v(-70.79, -45.7) * mm, "end": v(-70.8, -45.34) * mm});
            skLineSegment(sketch, "E2287", {"start": v(-70.8, -45.34) * mm, "end": v(-70.83, -44.93) * mm});
            skLineSegment(sketch, "E2288", {"start": v(-70.83, -44.93) * mm, "end": v(-70.89, -44.48) * mm});
            skLineSegment(sketch, "E2289", {"start": v(-70.89, -44.48) * mm, "end": v(-71.1, -43.52) * mm});
            skLineSegment(sketch, "E2290", {"start": v(-71.1, -43.52) * mm, "end": v(-71.45, -42.48) * mm});
            skArc(sketch, "E2291", {"start": v(-71.45, -42.48) * mm, "mid": v(-72.16, -42.38) * mm, "end": v(-72.87, -42.3) * mm});
            skLineSegment(sketch, "E2292", {"start": v(-74.43, -45.94) * mm, "end": v(-74.4, -45.52) * mm});
            skLineSegment(sketch, "E2293", {"start": v(-74.4, -45.52) * mm, "end": v(-74.34, -45.24) * mm});
            skLineSegment(sketch, "E2294", {"start": v(-74.34, -45.24) * mm, "end": v(-74.24, -44.9) * mm});
            skLineSegment(sketch, "E2295", {"start": v(-74.24, -44.9) * mm, "end": v(-74.1, -44.5) * mm});
            skLineSegment(sketch, "E2296", {"start": v(-74.1, -44.5) * mm, "end": v(-73.92, -44.08) * mm});
            skLineSegment(sketch, "E2297", {"start": v(-73.92, -44.08) * mm, "end": v(-73.46, -43.21) * mm});
            skLineSegment(sketch, "E2298", {"start": v(-73.46, -43.21) * mm, "end": v(-72.87, -42.3) * mm});
            skArc(sketch, "E2299", {"start": v(-75.2, -46.66) * mm, "mid": v(-74.67, -46.45) * mm, "end": v(-74.43, -45.94) * mm});
            skArc(sketch, "E2300", {"start": v(-75.2, -46.66) * mm, "mid": v(-75.55, -46.66) * mm, "end": v(-75.9, -46.66) * mm});
            skArc(sketch, "E2301", {"start": v(-76.67, -45.94) * mm, "mid": v(-76.43, -46.45) * mm, "end": v(-75.9, -46.66) * mm});
            skLineSegment(sketch, "E2302", {"start": v(-76.67, -45.94) * mm, "end": v(-76.7, -45.52) * mm});
            skLineSegment(sketch, "E2303", {"start": v(-76.7, -45.52) * mm, "end": v(-76.76, -45.24) * mm});
            skLineSegment(sketch, "E2304", {"start": v(-76.76, -45.24) * mm, "end": v(-76.86, -44.9) * mm});
            skLineSegment(sketch, "E2305", {"start": v(-76.86, -44.9) * mm, "end": v(-77, -44.5) * mm});
            skLineSegment(sketch, "E2306", {"start": v(-77, -44.5) * mm, "end": v(-77.18, -44.08) * mm});
            skLineSegment(sketch, "E2307", {"start": v(-77.18, -44.08) * mm, "end": v(-77.63, -43.21) * mm});
            skLineSegment(sketch, "E2308", {"start": v(-77.63, -43.21) * mm, "end": v(-78.23, -42.3) * mm});
            skArc(sketch, "E2309", {"start": v(-78.23, -42.3) * mm, "mid": v(-78.94, -42.38) * mm, "end": v(-79.65, -42.48) * mm});
            skLineSegment(sketch, "E2310", {"start": v(-80.22, -46.4) * mm, "end": v(-80.3, -46) * mm});
            skLineSegment(sketch, "E2311", {"start": v(-80.3, -46) * mm, "end": v(-80.31, -45.7) * mm});
            skLineSegment(sketch, "E2312", {"start": v(-80.31, -45.7) * mm, "end": v(-80.3, -45.34) * mm});
            skLineSegment(sketch, "E2313", {"start": v(-80.3, -45.34) * mm, "end": v(-80.27, -44.93) * mm});
            skLineSegment(sketch, "E2314", {"start": v(-80.27, -44.93) * mm, "end": v(-80.2, -44.48) * mm});
            skLineSegment(sketch, "E2315", {"start": v(-80.2, -44.48) * mm, "end": v(-80, -43.52) * mm});
            skLineSegment(sketch, "E2316", {"start": v(-80, -43.52) * mm, "end": v(-79.65, -42.48) * mm});
            skArc(sketch, "E2317", {"start": v(-80.78, -47.3) * mm, "mid": v(-80.32, -46.97) * mm, "end": v(-80.22, -46.4) * mm});
            skArc(sketch, "E2318", {"start": v(-80.78, -47.3) * mm, "mid": v(-81.11, -47.4) * mm, "end": v(-81.45, -47.48) * mm});
            skArc(sketch, "E2319", {"start": v(-82.38, -46.98) * mm, "mid": v(-82.02, -47.42) * mm, "end": v(-81.45, -47.48) * mm});
            skLineSegment(sketch, "E2320", {"start": v(-82.38, -46.98) * mm, "end": v(-82.52, -46.6) * mm});
            skLineSegment(sketch, "E2321", {"start": v(-82.52, -46.6) * mm, "end": v(-82.65, -46.33) * mm});
            skLineSegment(sketch, "E2322", {"start": v(-82.65, -46.33) * mm, "end": v(-82.84, -46.02) * mm});
            skLineSegment(sketch, "E2323", {"start": v(-82.84, -46.02) * mm, "end": v(-83.07, -45.68) * mm});
            skLineSegment(sketch, "E2324", {"start": v(-83.07, -45.68) * mm, "end": v(-83.35, -45.32) * mm});
            skLineSegment(sketch, "E2325", {"start": v(-83.35, -45.32) * mm, "end": v(-84.02, -44.6) * mm});
            skLineSegment(sketch, "E2326", {"start": v(-84.02, -44.6) * mm, "end": v(-84.84, -43.87) * mm});
            skArc(sketch, "E2327", {"start": v(-84.84, -43.87) * mm, "mid": v(-85.5, -44.14) * mm, "end": v(-86.16, -44.42) * mm});
            skLineSegment(sketch, "E2328", {"start": v(-85.69, -48.35) * mm, "end": v(-85.87, -47.98) * mm});
            skLineSegment(sketch, "E2329", {"start": v(-85.87, -47.98) * mm, "end": v(-85.96, -47.7) * mm});
            skLineSegment(sketch, "E2330", {"start": v(-85.96, -47.7) * mm, "end": v(-86.05, -47.35) * mm});
            skLineSegment(sketch, "E2331", {"start": v(-86.05, -47.35) * mm, "end": v(-86.12, -46.95) * mm});
            skLineSegment(sketch, "E2332", {"start": v(-86.12, -46.95) * mm, "end": v(-86.18, -46.5) * mm});
            skLineSegment(sketch, "E2333", {"start": v(-86.18, -46.5) * mm, "end": v(-86.22, -45.51) * mm});
            skLineSegment(sketch, "E2334", {"start": v(-86.22, -45.51) * mm, "end": v(-86.16, -44.42) * mm});
            skArc(sketch, "E2335", {"start": v(-86, -49.37) * mm, "mid": v(-85.64, -48.92) * mm, "end": v(-85.69, -48.35) * mm});
            skArc(sketch, "E2336", {"start": v(-86, -49.37) * mm, "mid": v(-86.3, -49.54) * mm, "end": v(-86.6, -49.71) * mm});
            skArc(sketch, "E2337", {"start": v(-87.63, -49.47) * mm, "mid": v(-87.16, -49.8) * mm, "end": v(-86.6, -49.71) * mm});
            skLineSegment(sketch, "E2338", {"start": v(-87.63, -49.47) * mm, "end": v(-87.86, -49.13) * mm});
            skLineSegment(sketch, "E2339", {"start": v(-87.86, -49.13) * mm, "end": v(-88.06, -48.91) * mm});
            skLineSegment(sketch, "E2340", {"start": v(-88.06, -48.91) * mm, "end": v(-88.32, -48.66) * mm});
            skLineSegment(sketch, "E2341", {"start": v(-88.32, -48.66) * mm, "end": v(-88.63, -48.4) * mm});
            skLineSegment(sketch, "E2342", {"start": v(-88.63, -48.4) * mm, "end": v(-89, -48.12) * mm});
            skLineSegment(sketch, "E2343", {"start": v(-89, -48.12) * mm, "end": v(-89.83, -47.6) * mm});
            skLineSegment(sketch, "E2344", {"start": v(-89.83, -47.6) * mm, "end": v(-90.8, -47.1) * mm});
            skArc(sketch, "E2345", {"start": v(-90.8, -47.1) * mm, "mid": v(-91.38, -47.53) * mm, "end": v(-91.94, -47.97) * mm});
            skLineSegment(sketch, "E2346", {"start": v(-90.47, -51.65) * mm, "end": v(-90.74, -51.34) * mm});
            skLineSegment(sketch, "E2347", {"start": v(-90.74, -51.34) * mm, "end": v(-90.9, -51.1) * mm});
            skLineSegment(sketch, "E2348", {"start": v(-90.9, -51.1) * mm, "end": v(-91.08, -50.78) * mm});
            skLineSegment(sketch, "E2349", {"start": v(-91.08, -50.78) * mm, "end": v(-91.25, -50.4) * mm});
            skLineSegment(sketch, "E2350", {"start": v(-91.25, -50.4) * mm, "end": v(-91.42, -49.99) * mm});
            skLineSegment(sketch, "E2351", {"start": v(-91.42, -49.99) * mm, "end": v(-91.72, -49.04) * mm});
            skLineSegment(sketch, "E2352", {"start": v(-91.72, -49.04) * mm, "end": v(-91.94, -47.97) * mm});
            skArc(sketch, "E2353", {"start": v(-90.5, -52.71) * mm, "mid": v(-90.27, -52.19) * mm, "end": v(-90.47, -51.65) * mm});
            skArc(sketch, "E2354", {"start": v(-90.5, -52.71) * mm, "mid": v(-90.75, -52.96) * mm, "end": v(-91, -53.2) * mm});
            skArc(sketch, "E2355", {"start": v(-92.06, -53.24) * mm, "mid": v(-91.52, -53.43) * mm, "end": v(-91, -53.2) * mm});
            skLineSegment(sketch, "E2356", {"start": v(-92.06, -53.24) * mm, "end": v(-92.37, -52.97) * mm});
            skLineSegment(sketch, "E2357", {"start": v(-92.37, -52.97) * mm, "end": v(-92.61, -52.8) * mm});
            skLineSegment(sketch, "E2358", {"start": v(-92.61, -52.8) * mm, "end": v(-92.93, -52.63) * mm});
            skLineSegment(sketch, "E2359", {"start": v(-92.93, -52.63) * mm, "end": v(-93.3, -52.45) * mm});
            skLineSegment(sketch, "E2360", {"start": v(-93.3, -52.45) * mm, "end": v(-93.72, -52.28) * mm});
            skLineSegment(sketch, "E2361", {"start": v(-93.72, -52.28) * mm, "end": v(-94.66, -52) * mm});
            skLineSegment(sketch, "E2362", {"start": v(-94.66, -52) * mm, "end": v(-95.73, -51.77) * mm});
            skArc(sketch, "E2363", {"start": v(-95.73, -51.77) * mm, "mid": v(-96.18, -52.33) * mm, "end": v(-96.6, -52.9) * mm});
            skLineSegment(sketch, "E2364", {"start": v(-94.23, -56.08) * mm, "end": v(-94.58, -55.84) * mm});
            skLineSegment(sketch, "E2365", {"start": v(-94.58, -55.84) * mm, "end": v(-94.8, -55.65) * mm});
            skLineSegment(sketch, "E2366", {"start": v(-94.8, -55.65) * mm, "end": v(-95.05, -55.4) * mm});
            skLineSegment(sketch, "E2367", {"start": v(-95.05, -55.4) * mm, "end": v(-95.31, -55.08) * mm});
            skLineSegment(sketch, "E2368", {"start": v(-95.31, -55.08) * mm, "end": v(-95.59, -54.71) * mm});
            skLineSegment(sketch, "E2369", {"start": v(-95.59, -54.71) * mm, "end": v(-96.11, -53.88) * mm});
            skLineSegment(sketch, "E2370", {"start": v(-96.11, -53.88) * mm, "end": v(-96.6, -52.9) * mm});
            skArc(sketch, "E2371", {"start": v(-94, -57.1) * mm, "mid": v(-93.9, -56.54) * mm, "end": v(-94.23, -56.08) * mm});
            skArc(sketch, "E2372", {"start": v(-94, -57.1) * mm, "mid": v(-94.17, -57.4) * mm, "end": v(-94.34, -57.7) * mm});
            skArc(sketch, "E2373", {"start": v(-95.36, -58.02) * mm, "mid": v(-94.79, -58.07) * mm, "end": v(-94.34, -57.7) * mm});
            skLineSegment(sketch, "E2374", {"start": v(-95.36, -58.02) * mm, "end": v(-95.73, -57.84) * mm});
            skLineSegment(sketch, "E2375", {"start": v(-95.73, -57.84) * mm, "end": v(-96, -57.75) * mm});
            skLineSegment(sketch, "E2376", {"start": v(-96, -57.75) * mm, "end": v(-96.35, -57.66) * mm});
            skLineSegment(sketch, "E2377", {"start": v(-96.35, -57.66) * mm, "end": v(-96.76, -57.58) * mm});
            skLineSegment(sketch, "E2378", {"start": v(-96.76, -57.58) * mm, "end": v(-97.21, -57.53) * mm});
            skLineSegment(sketch, "E2379", {"start": v(-97.21, -57.53) * mm, "end": v(-98.2, -57.49) * mm});
            skLineSegment(sketch, "E2380", {"start": v(-98.2, -57.49) * mm, "end": v(-99.29, -57.55) * mm});
            skArc(sketch, "E2381", {"start": v(-99.29, -57.55) * mm, "mid": v(-99.57, -58.2) * mm, "end": v(-99.83, -58.87) * mm});
            skLineSegment(sketch, "E2382", {"start": v(-96.72, -61.32) * mm, "end": v(-97.11, -61.19) * mm});
            skLineSegment(sketch, "E2383", {"start": v(-97.11, -61.19) * mm, "end": v(-97.37, -61.06) * mm});
            skLineSegment(sketch, "E2384", {"start": v(-97.37, -61.06) * mm, "end": v(-97.69, -60.87) * mm});
            skLineSegment(sketch, "E2385", {"start": v(-97.69, -60.87) * mm, "end": v(-98.03, -60.64) * mm});
            skLineSegment(sketch, "E2386", {"start": v(-98.03, -60.64) * mm, "end": v(-98.38, -60.36) * mm});
            skLineSegment(sketch, "E2387", {"start": v(-98.38, -60.36) * mm, "end": v(-99.1, -59.69) * mm});
            skLineSegment(sketch, "E2388", {"start": v(-99.1, -59.69) * mm, "end": v(-99.83, -58.87) * mm});
            skArc(sketch, "E2389", {"start": v(-96.22, -62.26) * mm, "mid": v(-96.29, -61.7) * mm, "end": v(-96.72, -61.32) * mm});
            skArc(sketch, "E2390", {"start": v(-96.22, -62.26) * mm, "mid": v(-96.32, -62.6) * mm, "end": v(-96.4, -62.93) * mm});
            skArc(sketch, "E2391", {"start": v(-97.3, -63.5) * mm, "mid": v(-96.74, -63.4) * mm, "end": v(-96.4, -62.93) * mm});
            skLineSegment(sketch, "E2392", {"start": v(-97.3, -63.5) * mm, "end": v(-97.71, -63.41) * mm});
            skLineSegment(sketch, "E2393", {"start": v(-97.71, -63.41) * mm, "end": v(-98, -63.4) * mm});
            skLineSegment(sketch, "E2394", {"start": v(-98, -63.4) * mm, "end": v(-98.36, -63.4) * mm});
            skLineSegment(sketch, "E2395", {"start": v(-98.36, -63.4) * mm, "end": v(-98.78, -63.43) * mm});
            skLineSegment(sketch, "E2396", {"start": v(-98.78, -63.43) * mm, "end": v(-99.22, -63.5) * mm});
            skLineSegment(sketch, "E2397", {"start": v(-99.22, -63.5) * mm, "end": v(-100.19, -63.71) * mm});
            skLineSegment(sketch, "E2398", {"start": v(-100.19, -63.71) * mm, "end": v(-101.22, -64.06) * mm});
            skArc(sketch, "E2399", {"start": v(-101.22, -64.06) * mm, "mid": v(-101.33, -64.76) * mm, "end": v(-101.41, -65.47) * mm});
            skLineSegment(sketch, "E2400", {"start": v(-97.77, -67.04) * mm, "end": v(-98.18, -67) * mm});
            skLineSegment(sketch, "E2401", {"start": v(-98.18, -67) * mm, "end": v(-98.47, -66.95) * mm});
            skLineSegment(sketch, "E2402", {"start": v(-98.47, -66.95) * mm, "end": v(-98.82, -66.85) * mm});
            skLineSegment(sketch, "E2403", {"start": v(-98.82, -66.85) * mm, "end": v(-99.2, -66.7) * mm});
            skLineSegment(sketch, "E2404", {"start": v(-99.2, -66.7) * mm, "end": v(-99.62, -66.53) * mm});
            skLineSegment(sketch, "E2405", {"start": v(-99.62, -66.53) * mm, "end": v(-100.5, -66.07) * mm});
            skLineSegment(sketch, "E2406", {"start": v(-100.5, -66.07) * mm, "end": v(-101.41, -65.47) * mm});
            skArc(sketch, "E2407", {"start": v(-97.05, -67.81) * mm, "mid": v(-97.25, -67.28) * mm, "end": v(-97.77, -67.04) * mm});
            skArc(sketch, "E2408", {"start": v(-97.05, -67.81) * mm, "mid": v(-97.05, -68.16) * mm, "end": v(-97.05, -68.5) * mm});
            skArc(sketch, "E2409", {"start": v(-97.77, -69.28) * mm, "mid": v(-97.25, -69.04) * mm, "end": v(-97.05, -68.5) * mm});
            skLineSegment(sketch, "E2410", {"start": v(-97.77, -69.28) * mm, "end": v(-98.18, -69.31) * mm});
            skLineSegment(sketch, "E2411", {"start": v(-98.18, -69.31) * mm, "end": v(-98.47, -69.37) * mm});
            skLineSegment(sketch, "E2412", {"start": v(-98.47, -69.37) * mm, "end": v(-98.82, -69.47) * mm});
            skLineSegment(sketch, "E2413", {"start": v(-98.82, -69.47) * mm, "end": v(-99.2, -69.6) * mm});
            skLineSegment(sketch, "E2414", {"start": v(-99.2, -69.6) * mm, "end": v(-99.62, -69.78) * mm});
            skLineSegment(sketch, "E2415", {"start": v(-99.62, -69.78) * mm, "end": v(-100.5, -70.24) * mm});
            skLineSegment(sketch, "E2416", {"start": v(-100.5, -70.24) * mm, "end": v(-101.41, -70.84) * mm});
            skArc(sketch, "E2417", {"start": v(-101.41, -70.84) * mm, "mid": v(-101.33, -71.55) * mm, "end": v(-101.22, -72.26) * mm});
            skLineSegment(sketch, "E2418", {"start": v(-97.3, -72.83) * mm, "end": v(-97.71, -72.9) * mm});
            skLineSegment(sketch, "E2419", {"start": v(-97.71, -72.9) * mm, "end": v(-98, -72.92) * mm});
            skLineSegment(sketch, "E2420", {"start": v(-98, -72.92) * mm, "end": v(-98.36, -72.92) * mm});
            skLineSegment(sketch, "E2421", {"start": v(-98.36, -72.92) * mm, "end": v(-98.78, -72.88) * mm});
            skLineSegment(sketch, "E2422", {"start": v(-98.78, -72.88) * mm, "end": v(-99.22, -72.82) * mm});
            skLineSegment(sketch, "E2423", {"start": v(-99.22, -72.82) * mm, "end": v(-100.19, -72.6) * mm});
            skLineSegment(sketch, "E2424", {"start": v(-100.19, -72.6) * mm, "end": v(-101.22, -72.26) * mm});
            skArc(sketch, "E2425", {"start": v(-96.4, -73.39) * mm, "mid": v(-96.74, -72.92) * mm, "end": v(-97.3, -72.83) * mm});
            skArc(sketch, "E2426", {"start": v(-96.4, -73.39) * mm, "mid": v(-96.32, -73.72) * mm, "end": v(-96.22, -74.06) * mm});
            skArc(sketch, "E2427", {"start": v(10.04, -15.16) * mm, "mid": v(10.3, -14.65) * mm, "end": v(10.11, -14.1) * mm});
            skLineSegment(sketch, "E2428", {"start": v(10.04, -15.16) * mm, "end": v(9.73, -15.45) * mm});
            skLineSegment(sketch, "E2429", {"start": v(9.73, -15.45) * mm, "end": v(9.6, -15.6) * mm});
            skLineSegment(sketch, "E2430", {"start": v(9.6, -15.6) * mm, "end": v(9.43, -15.83) * mm});
            skLineSegment(sketch, "E2431", {"start": v(9.43, -15.83) * mm, "end": v(9.26, -16.1) * mm});
            skLineSegment(sketch, "E2432", {"start": v(9.26, -16.1) * mm, "end": v(9.08, -16.4) * mm});
            skLineSegment(sketch, "E2433", {"start": v(9.08, -16.4) * mm, "end": v(8.91, -16.73) * mm});
            skLineSegment(sketch, "E2434", {"start": v(8.91, -16.73) * mm, "end": v(8.53, -17.63) * mm});
            skLineSegment(sketch, "E2435", {"start": v(8.53, -17.63) * mm, "end": v(8.22, -18.67) * mm});
            skArc(sketch, "E2436", {"start": v(8.22, -18.67) * mm, "mid": v(8.73, -19.16) * mm, "end": v(9.25, -19.64) * mm});
            skLineSegment(sketch, "E2437", {"start": v(12.63, -17.58) * mm, "end": v(12.36, -17.9) * mm});
            skLineSegment(sketch, "E2438", {"start": v(12.36, -17.9) * mm, "end": v(12.21, -18.05) * mm});
            skLineSegment(sketch, "E2439", {"start": v(12.21, -18.05) * mm, "end": v(12, -18.23) * mm});
            skLineSegment(sketch, "E2440", {"start": v(12, -18.23) * mm, "end": v(11.75, -18.42) * mm});
            skLineSegment(sketch, "E2441", {"start": v(11.75, -18.42) * mm, "end": v(11.46, -18.62) * mm});
            skLineSegment(sketch, "E2442", {"start": v(11.46, -18.62) * mm, "end": v(11.14, -18.81) * mm});
            skLineSegment(sketch, "E2443", {"start": v(11.14, -18.81) * mm, "end": v(10.26, -19.25) * mm});
            skLineSegment(sketch, "E2444", {"start": v(10.26, -19.25) * mm, "end": v(9.25, -19.64) * mm});
            skArc(sketch, "E2445", {"start": v(13.69, -17.43) * mm, "mid": v(13.13, -17.3) * mm, "end": v(12.63, -17.58) * mm});
            skArc(sketch, "E2446", {"start": v(13.69, -17.43) * mm, "mid": v(13.97, -17.64) * mm, "end": v(14.26, -17.84) * mm});
            skArc(sketch, "E2447", {"start": v(14.48, -18.88) * mm, "mid": v(14.58, -18.32) * mm, "end": v(14.26, -17.84) * mm});
            skLineSegment(sketch, "E2448", {"start": v(14.48, -18.88) * mm, "end": v(14.25, -19.25) * mm});
            skLineSegment(sketch, "E2449", {"start": v(14.25, -19.25) * mm, "end": v(14.17, -19.43) * mm});
            skLineSegment(sketch, "E2450", {"start": v(14.17, -19.43) * mm, "end": v(14.07, -19.69) * mm});
            skLineSegment(sketch, "E2451", {"start": v(14.07, -19.69) * mm, "end": v(13.97, -20) * mm});
            skLineSegment(sketch, "E2452", {"start": v(13.97, -20) * mm, "end": v(13.89, -20.33) * mm});
            skLineSegment(sketch, "E2453", {"start": v(13.89, -20.33) * mm, "end": v(13.81, -20.7) * mm});
            skLineSegment(sketch, "E2454", {"start": v(13.81, -20.7) * mm, "end": v(13.7, -21.67) * mm});
            skLineSegment(sketch, "E2455", {"start": v(13.7, -21.67) * mm, "end": v(13.66, -22.75) * mm});
            skArc(sketch, "E2456", {"start": v(13.66, -22.75) * mm, "mid": v(14.29, -23.09) * mm, "end": v(14.92, -23.4) * mm});
            skLineSegment(sketch, "E2457", {"start": v(17.62, -20.51) * mm, "end": v(17.45, -20.9) * mm});
            skLineSegment(sketch, "E2458", {"start": v(17.45, -20.9) * mm, "end": v(17.35, -21.08) * mm});
            skLineSegment(sketch, "E2459", {"start": v(17.35, -21.08) * mm, "end": v(17.2, -21.3) * mm});
            skLineSegment(sketch, "E2460", {"start": v(17.2, -21.3) * mm, "end": v(17, -21.56) * mm});
            skLineSegment(sketch, "E2461", {"start": v(17, -21.56) * mm, "end": v(16.78, -21.83) * mm});
            skLineSegment(sketch, "E2462", {"start": v(16.78, -21.83) * mm, "end": v(16.52, -22.1) * mm});
            skLineSegment(sketch, "E2463", {"start": v(16.52, -22.1) * mm, "end": v(15.8, -22.76) * mm});
            skLineSegment(sketch, "E2464", {"start": v(15.8, -22.76) * mm, "end": v(14.92, -23.4) * mm});
            skArc(sketch, "E2465", {"start": v(18.6, -20.09) * mm, "mid": v(18.02, -20.1) * mm, "end": v(17.62, -20.51) * mm});
            skArc(sketch, "E2466", {"start": v(18.6, -20.09) * mm, "mid": v(18.93, -20.2) * mm, "end": v(19.26, -20.32) * mm});
            skArc(sketch, "E2467", {"start": v(19.75, -21.27) * mm, "mid": v(19.7, -20.7) * mm, "end": v(19.26, -20.32) * mm});
            skLineSegment(sketch, "E2468", {"start": v(19.75, -21.27) * mm, "end": v(19.63, -21.68) * mm});
            skLineSegment(sketch, "E2469", {"start": v(19.63, -21.68) * mm, "end": v(19.6, -21.88) * mm});
            skLineSegment(sketch, "E2470", {"start": v(19.6, -21.88) * mm, "end": v(19.58, -22.15) * mm});
            skLineSegment(sketch, "E2471", {"start": v(19.58, -22.15) * mm, "end": v(19.57, -22.47) * mm});
            skLineSegment(sketch, "E2472", {"start": v(19.57, -22.47) * mm, "end": v(19.57, -22.82) * mm});
            skLineSegment(sketch, "E2473", {"start": v(19.57, -22.82) * mm, "end": v(19.6, -23.2) * mm});
            skLineSegment(sketch, "E2474", {"start": v(19.6, -23.2) * mm, "end": v(19.75, -24.16) * mm});
            skLineSegment(sketch, "E2475", {"start": v(19.75, -24.16) * mm, "end": v(20.01, -25.21) * mm});
            skArc(sketch, "E2476", {"start": v(20.01, -25.21) * mm, "mid": v(20.7, -25.37) * mm, "end": v(21.4, -25.5) * mm});
            skLineSegment(sketch, "E2477", {"start": v(23.21, -21.99) * mm, "end": v(23.16, -22.4) * mm});
            skLineSegment(sketch, "E2478", {"start": v(23.16, -22.4) * mm, "end": v(23.1, -22.61) * mm});
            skLineSegment(sketch, "E2479", {"start": v(23.1, -22.61) * mm, "end": v(23.02, -22.87) * mm});
            skLineSegment(sketch, "E2480", {"start": v(23.02, -22.87) * mm, "end": v(22.9, -23.17) * mm});
            skLineSegment(sketch, "E2481", {"start": v(22.9, -23.17) * mm, "end": v(22.76, -23.48) * mm});
            skLineSegment(sketch, "E2482", {"start": v(22.76, -23.48) * mm, "end": v(22.58, -23.82) * mm});
            skLineSegment(sketch, "E2483", {"start": v(22.58, -23.82) * mm, "end": v(22.06, -24.65) * mm});
            skLineSegment(sketch, "E2484", {"start": v(22.06, -24.65) * mm, "end": v(21.4, -25.5) * mm});
            skArc(sketch, "E2485", {"start": v(24.04, -21.32) * mm, "mid": v(23.5, -21.49) * mm, "end": v(23.21, -21.99) * mm});
            skArc(sketch, "E2486", {"start": v(24.04, -21.32) * mm, "mid": v(24.4, -21.34) * mm, "end": v(24.74, -21.36) * mm});
            skArc(sketch, "E2487", {"start": v(25.47, -22.14) * mm, "mid": v(25.26, -21.6) * mm, "end": v(24.74, -21.36) * mm});
            skLineSegment(sketch, "E2488", {"start": v(25.47, -22.14) * mm, "end": v(25.47, -22.57) * mm});
            skLineSegment(sketch, "E2489", {"start": v(25.47, -22.57) * mm, "end": v(25.5, -22.77) * mm});
            skLineSegment(sketch, "E2490", {"start": v(25.5, -22.77) * mm, "end": v(25.54, -23.04) * mm});
            skLineSegment(sketch, "E2491", {"start": v(25.54, -23.04) * mm, "end": v(25.62, -23.35) * mm});
            skLineSegment(sketch, "E2492", {"start": v(25.62, -23.35) * mm, "end": v(25.72, -23.69) * mm});
            skLineSegment(sketch, "E2493", {"start": v(25.72, -23.69) * mm, "end": v(25.85, -24.04) * mm});
            skLineSegment(sketch, "E2494", {"start": v(25.85, -24.04) * mm, "end": v(26.25, -24.93) * mm});
            skLineSegment(sketch, "E2495", {"start": v(26.25, -24.93) * mm, "end": v(26.79, -25.87) * mm});
            skArc(sketch, "E2496", {"start": v(26.79, -25.87) * mm, "mid": v(27.5, -25.83) * mm, "end": v(28.2, -25.77) * mm});
            skLineSegment(sketch, "E2497", {"start": v(29, -21.9) * mm, "end": v(29.06, -22.32) * mm});
            skLineSegment(sketch, "E2498", {"start": v(29.06, -22.32) * mm, "end": v(29.07, -22.53) * mm});
            skLineSegment(sketch, "E2499", {"start": v(29.07, -22.53) * mm, "end": v(29.05, -22.8) * mm});
            skLineSegment(sketch, "E2500", {"start": v(29.05, -22.8) * mm, "end": v(29.02, -23.12) * mm});
            skLineSegment(sketch, "E2501", {"start": v(29.02, -23.12) * mm, "end": v(28.97, -23.46) * mm});
            skLineSegment(sketch, "E2502", {"start": v(28.97, -23.46) * mm, "end": v(28.89, -23.83) * mm});
            skLineSegment(sketch, "E2503", {"start": v(28.89, -23.83) * mm, "end": v(28.61, -24.77) * mm});
            skLineSegment(sketch, "E2504", {"start": v(28.61, -24.77) * mm, "end": v(28.2, -25.77) * mm});
            skArc(sketch, "E2505", {"start": v(29.62, -21.03) * mm, "mid": v(29.13, -21.34) * mm, "end": v(29, -21.9) * mm});
            skArc(sketch, "E2506", {"start": v(29.62, -21.03) * mm, "mid": v(29.96, -20.96) * mm, "end": v(30.3, -20.89) * mm});
            skArc(sketch, "E2507", {"start": v(31.22, -21.44) * mm, "mid": v(30.87, -20.98) * mm, "end": v(30.3, -20.89) * mm});
            skLineSegment(sketch, "E2508", {"start": v(31.22, -21.44) * mm, "end": v(31.33, -21.85) * mm});
            skLineSegment(sketch, "E2509", {"start": v(31.33, -21.85) * mm, "end": v(31.4, -22.04) * mm});
            skLineSegment(sketch, "E2510", {"start": v(31.4, -22.04) * mm, "end": v(31.53, -22.29) * mm});
            skLineSegment(sketch, "E2511", {"start": v(31.53, -22.29) * mm, "end": v(31.68, -22.57) * mm});
            skLineSegment(sketch, "E2512", {"start": v(31.68, -22.57) * mm, "end": v(31.87, -22.86) * mm});
            skLineSegment(sketch, "E2513", {"start": v(31.87, -22.86) * mm, "end": v(32.1, -23.17) * mm});
            skLineSegment(sketch, "E2514", {"start": v(32.1, -23.17) * mm, "end": v(32.72, -23.92) * mm});
            skLineSegment(sketch, "E2515", {"start": v(32.72, -23.92) * mm, "end": v(33.5, -24.68) * mm});
            skArc(sketch, "E2516", {"start": v(33.5, -24.68) * mm, "mid": v(34.16, -24.45) * mm, "end": v(34.83, -24.2) * mm});
            skLineSegment(sketch, "E2517", {"start": v(34.55, -20.26) * mm, "end": v(34.72, -20.65) * mm});
            skLineSegment(sketch, "E2518", {"start": v(34.72, -20.65) * mm, "end": v(34.78, -20.84) * mm});
            skLineSegment(sketch, "E2519", {"start": v(34.78, -20.84) * mm, "end": v(34.84, -21.11) * mm});
            skLineSegment(sketch, "E2520", {"start": v(34.84, -21.11) * mm, "end": v(34.9, -21.42) * mm});
            skLineSegment(sketch, "E2521", {"start": v(34.9, -21.42) * mm, "end": v(34.94, -21.77) * mm});
            skLineSegment(sketch, "E2522", {"start": v(34.94, -21.77) * mm, "end": v(34.96, -22.15) * mm});
            skLineSegment(sketch, "E2523", {"start": v(34.96, -22.15) * mm, "end": v(34.95, -23.12) * mm});
            skLineSegment(sketch, "E2524", {"start": v(34.95, -23.12) * mm, "end": v(34.83, -24.2) * mm});
            skArc(sketch, "E2525", {"start": v(34.91, -19.25) * mm, "mid": v(34.53, -19.68) * mm, "end": v(34.55, -20.26) * mm});
            skArc(sketch, "E2526", {"start": v(34.91, -19.25) * mm, "mid": v(35.22, -19.1) * mm, "end": v(35.53, -18.93) * mm});
            skArc(sketch, "E2527", {"start": v(36.56, -19.22) * mm, "mid": v(36.1, -18.86) * mm, "end": v(35.53, -18.93) * mm});
            skLineSegment(sketch, "E2528", {"start": v(36.56, -19.22) * mm, "end": v(36.78, -19.58) * mm});
            skLineSegment(sketch, "E2529", {"start": v(36.78, -19.58) * mm, "end": v(36.9, -19.74) * mm});
            skLineSegment(sketch, "E2530", {"start": v(36.9, -19.74) * mm, "end": v(37.09, -19.95) * mm});
            skLineSegment(sketch, "E2531", {"start": v(37.09, -19.95) * mm, "end": v(37.31, -20.17) * mm});
            skLineSegment(sketch, "E2532", {"start": v(37.31, -20.17) * mm, "end": v(37.57, -20.4) * mm});
            skLineSegment(sketch, "E2533", {"start": v(37.57, -20.4) * mm, "end": v(37.87, -20.64) * mm});
            skLineSegment(sketch, "E2534", {"start": v(37.87, -20.64) * mm, "end": v(38.67, -21.2) * mm});
            skLineSegment(sketch, "E2535", {"start": v(38.67, -21.2) * mm, "end": v(39.62, -21.72) * mm});
            skArc(sketch, "E2536", {"start": v(39.62, -21.72) * mm, "mid": v(40.2, -21.31) * mm, "end": v(40.78, -20.9) * mm});
            skLineSegment(sketch, "E2537", {"start": v(39.45, -17.18) * mm, "end": v(39.72, -17.5) * mm});
            skLineSegment(sketch, "E2538", {"start": v(39.72, -17.5) * mm, "end": v(39.83, -17.68) * mm});
            skLineSegment(sketch, "E2539", {"start": v(39.83, -17.68) * mm, "end": v(39.96, -17.92) * mm});
            skLineSegment(sketch, "E2540", {"start": v(39.96, -17.92) * mm, "end": v(40.1, -18.2) * mm});
            skLineSegment(sketch, "E2541", {"start": v(40.1, -18.2) * mm, "end": v(40.23, -18.53) * mm});
            skLineSegment(sketch, "E2542", {"start": v(40.23, -18.53) * mm, "end": v(40.36, -18.88) * mm});
            skLineSegment(sketch, "E2543", {"start": v(40.36, -18.88) * mm, "end": v(40.6, -19.83) * mm});
            skLineSegment(sketch, "E2544", {"start": v(40.6, -19.83) * mm, "end": v(40.78, -20.9) * mm});
            skArc(sketch, "E2545", {"start": v(39.53, -16.1) * mm, "mid": v(39.27, -16.63) * mm, "end": v(39.45, -17.18) * mm});
            skArc(sketch, "E2546", {"start": v(39.53, -16.1) * mm, "mid": v(39.78, -15.87) * mm, "end": v(40.04, -15.63) * mm});
            skArc(sketch, "E2547", {"start": v(41.1, -15.63) * mm, "mid": v(40.57, -15.42) * mm, "end": v(40.04, -15.63) * mm});
            skLineSegment(sketch, "E2548", {"start": v(41.1, -15.63) * mm, "end": v(41.42, -15.92) * mm});
            skLineSegment(sketch, "E2549", {"start": v(41.42, -15.92) * mm, "end": v(41.58, -16.04) * mm});
            skLineSegment(sketch, "E2550", {"start": v(41.58, -16.04) * mm, "end": v(41.81, -16.2) * mm});
            skLineSegment(sketch, "E2551", {"start": v(41.81, -16.2) * mm, "end": v(42.09, -16.35) * mm});
            skLineSegment(sketch, "E2552", {"start": v(42.09, -16.35) * mm, "end": v(42.4, -16.5) * mm});
            skLineSegment(sketch, "E2553", {"start": v(42.4, -16.5) * mm, "end": v(42.75, -16.65) * mm});
            skLineSegment(sketch, "E2554", {"start": v(42.75, -16.65) * mm, "end": v(43.67, -16.97) * mm});
            skLineSegment(sketch, "E2555", {"start": v(43.67, -16.97) * mm, "end": v(44.73, -17.21) * mm});
            skArc(sketch, "E2556", {"start": v(44.73, -17.21) * mm, "mid": v(45.18, -16.67) * mm, "end": v(45.62, -16.11) * mm});
            skLineSegment(sketch, "E2557", {"start": v(43.34, -12.89) * mm, "end": v(43.69, -13.13) * mm});
            skLineSegment(sketch, "E2558", {"start": v(43.69, -13.13) * mm, "end": v(43.84, -13.27) * mm});
            skLineSegment(sketch, "E2559", {"start": v(43.84, -13.27) * mm, "end": v(44.03, -13.46) * mm});
            skLineSegment(sketch, "E2560", {"start": v(44.03, -13.46) * mm, "end": v(44.24, -13.7) * mm});
            skLineSegment(sketch, "E2561", {"start": v(44.24, -13.7) * mm, "end": v(44.46, -13.98) * mm});
            skLineSegment(sketch, "E2562", {"start": v(44.46, -13.98) * mm, "end": v(44.67, -14.29) * mm});
            skLineSegment(sketch, "E2563", {"start": v(44.67, -14.29) * mm, "end": v(45.17, -15.13) * mm});
            skLineSegment(sketch, "E2564", {"start": v(45.17, -15.13) * mm, "end": v(45.62, -16.11) * mm});
            skArc(sketch, "E2565", {"start": v(43.12, -11.84) * mm, "mid": v(43.02, -12.4) * mm, "end": v(43.34, -12.89) * mm});
            skArc(sketch, "E2566", {"start": v(43.12, -11.84) * mm, "mid": v(43.3, -11.54) * mm, "end": v(43.49, -11.24) * mm});
            skArc(sketch, "E2567", {"start": v(44.52, -10.95) * mm, "mid": v(43.94, -10.89) * mm, "end": v(43.49, -11.24) * mm});
            skLineSegment(sketch, "E2568", {"start": v(44.52, -10.95) * mm, "end": v(44.9, -11.15) * mm});
            skLineSegment(sketch, "E2569", {"start": v(44.9, -11.15) * mm, "end": v(45.08, -11.22) * mm});
            skLineSegment(sketch, "E2570", {"start": v(45.08, -11.22) * mm, "end": v(45.35, -11.3) * mm});
            skLineSegment(sketch, "E2571", {"start": v(45.35, -11.3) * mm, "end": v(45.65, -11.38) * mm});
            skLineSegment(sketch, "E2572", {"start": v(45.65, -11.38) * mm, "end": v(46, -11.44) * mm});
            skLineSegment(sketch, "E2573", {"start": v(46, -11.44) * mm, "end": v(46.37, -11.5) * mm});
            skLineSegment(sketch, "E2574", {"start": v(46.37, -11.5) * mm, "end": v(47.35, -11.54) * mm});
            skLineSegment(sketch, "E2575", {"start": v(47.35, -11.54) * mm, "end": v(48.43, -11.5) * mm});
            skArc(sketch, "E2576", {"start": v(48.43, -11.5) * mm, "mid": v(48.72, -10.85) * mm, "end": v(49, -10.2) * mm});
            skLineSegment(sketch, "E2577", {"start": v(45.93, -7.7) * mm, "end": v(46.32, -7.85) * mm});
            skLineSegment(sketch, "E2578", {"start": v(46.32, -7.85) * mm, "end": v(46.51, -7.94) * mm});
            skLineSegment(sketch, "E2579", {"start": v(46.51, -7.94) * mm, "end": v(46.75, -8.08) * mm});
            skLineSegment(sketch, "E2580", {"start": v(46.75, -8.08) * mm, "end": v(47.01, -8.25) * mm});
            skLineSegment(sketch, "E2581", {"start": v(47.01, -8.25) * mm, "end": v(47.3, -8.46) * mm});
            skLineSegment(sketch, "E2582", {"start": v(47.3, -8.46) * mm, "end": v(47.59, -8.7) * mm});
            skLineSegment(sketch, "E2583", {"start": v(47.59, -8.7) * mm, "end": v(48.3, -9.37) * mm});
            skLineSegment(sketch, "E2584", {"start": v(48.3, -9.37) * mm, "end": v(49, -10.2) * mm});
            skArc(sketch, "E2585", {"start": v(45.43, -6.76) * mm, "mid": v(45.49, -7.33) * mm, "end": v(45.93, -7.7) * mm});
            skArc(sketch, "E2586", {"start": v(45.43, -6.76) * mm, "mid": v(45.53, -6.42) * mm, "end": v(45.62, -6.08) * mm});
            skArc(sketch, "E2587", {"start": v(46.54, -5.53) * mm, "mid": v(45.97, -5.62) * mm, "end": v(45.62, -6.08) * mm});
            skLineSegment(sketch, "E2588", {"start": v(46.54, -5.53) * mm, "end": v(46.95, -5.61) * mm});
            skLineSegment(sketch, "E2589", {"start": v(46.95, -5.61) * mm, "end": v(47.16, -5.63) * mm});
            skLineSegment(sketch, "E2590", {"start": v(47.16, -5.63) * mm, "end": v(47.43, -5.64) * mm});
            skLineSegment(sketch, "E2591", {"start": v(47.43, -5.64) * mm, "end": v(47.75, -5.63) * mm});
            skLineSegment(sketch, "E2592", {"start": v(47.75, -5.63) * mm, "end": v(48.1, -5.6) * mm});
            skLineSegment(sketch, "E2593", {"start": v(48.1, -5.6) * mm, "end": v(48.47, -5.55) * mm});
            skLineSegment(sketch, "E2594", {"start": v(48.47, -5.55) * mm, "end": v(49.42, -5.33) * mm});
            skLineSegment(sketch, "E2595", {"start": v(49.42, -5.33) * mm, "end": v(50.45, -5) * mm});
            skArc(sketch, "E2596", {"start": v(50.45, -5) * mm, "mid": v(50.56, -4.3) * mm, "end": v(50.65, -3.6) * mm});
            skLineSegment(sketch, "E2597", {"start": v(47.02, -2.02) * mm, "end": v(47.44, -2.05) * mm});
            skLineSegment(sketch, "E2598", {"start": v(47.44, -2.05) * mm, "end": v(47.64, -2.09) * mm});
            skLineSegment(sketch, "E2599", {"start": v(47.64, -2.09) * mm, "end": v(47.9, -2.15) * mm});
            skLineSegment(sketch, "E2600", {"start": v(47.9, -2.15) * mm, "end": v(48.21, -2.25) * mm});
            skLineSegment(sketch, "E2601", {"start": v(48.21, -2.25) * mm, "end": v(48.54, -2.37) * mm});
            skLineSegment(sketch, "E2602", {"start": v(48.54, -2.37) * mm, "end": v(48.88, -2.53) * mm});
            skLineSegment(sketch, "E2603", {"start": v(48.88, -2.53) * mm, "end": v(49.75, -2.99) * mm});
            skLineSegment(sketch, "E2604", {"start": v(49.75, -2.99) * mm, "end": v(50.65, -3.6) * mm});
            skArc(sketch, "E2605", {"start": v(46.29, -1.24) * mm, "mid": v(46.5, -1.78) * mm, "end": v(47.02, -2.02) * mm});
            skArc(sketch, "E2606", {"start": v(46.29, -1.24) * mm, "mid": v(46.3, -0.9) * mm, "end": v(46.29, -0.54) * mm});
            skArc(sketch, "E2607", {"start": v(47.02, 0.24) * mm, "mid": v(46.5, 0) * mm, "end": v(46.29, -0.54) * mm});
            skLineSegment(sketch, "E2608", {"start": v(47.02, 0.24) * mm, "end": v(47.44, 0.27) * mm});
            skLineSegment(sketch, "E2609", {"start": v(47.44, 0.27) * mm, "end": v(47.64, 0.3) * mm});
            skLineSegment(sketch, "E2610", {"start": v(47.64, 0.3) * mm, "end": v(47.9, 0.37) * mm});
            skLineSegment(sketch, "E2611", {"start": v(47.9, 0.37) * mm, "end": v(48.21, 0.47) * mm});
            skLineSegment(sketch, "E2612", {"start": v(48.21, 0.47) * mm, "end": v(48.54, 0.6) * mm});
            skLineSegment(sketch, "E2613", {"start": v(48.54, 0.6) * mm, "end": v(48.88, 0.75) * mm});
            skLineSegment(sketch, "E2614", {"start": v(48.88, 0.75) * mm, "end": v(49.75, 1.2) * mm});
            skLineSegment(sketch, "E2615", {"start": v(49.75, 1.2) * mm, "end": v(50.65, 1.8) * mm});
            skArc(sketch, "E2616", {"start": v(50.65, 1.8) * mm, "mid": v(50.56, 2.51) * mm, "end": v(50.45, 3.21) * mm});
            skLineSegment(sketch, "E2617", {"start": v(46.54, 3.75) * mm, "end": v(46.95, 3.83) * mm});
            skLineSegment(sketch, "E2618", {"start": v(46.95, 3.83) * mm, "end": v(47.16, 3.85) * mm});
            skLineSegment(sketch, "E2619", {"start": v(47.16, 3.85) * mm, "end": v(47.43, 3.86) * mm});
            skLineSegment(sketch, "E2620", {"start": v(47.43, 3.86) * mm, "end": v(47.75, 3.85) * mm});
            skLineSegment(sketch, "E2621", {"start": v(47.75, 3.85) * mm, "end": v(48.1, 3.82) * mm});
            skLineSegment(sketch, "E2622", {"start": v(48.1, 3.82) * mm, "end": v(48.47, 3.76) * mm});
            skLineSegment(sketch, "E2623", {"start": v(48.47, 3.76) * mm, "end": v(49.42, 3.55) * mm});
            skLineSegment(sketch, "E2624", {"start": v(49.42, 3.55) * mm, "end": v(50.45, 3.21) * mm});
            skArc(sketch, "E2625", {"start": v(45.62, 4.3) * mm, "mid": v(45.97, 3.84) * mm, "end": v(46.54, 3.75) * mm});
            skArc(sketch, "E2626", {"start": v(45.62, 4.3) * mm, "mid": v(45.53, 4.64) * mm, "end": v(45.43, 4.98) * mm});
            skArc(sketch, "E2627", {"start": v(45.93, 5.93) * mm, "mid": v(45.49, 5.55) * mm, "end": v(45.43, 4.98) * mm});
            skLineSegment(sketch, "E2628", {"start": v(45.93, 5.93) * mm, "end": v(46.32, 6.07) * mm});
            skLineSegment(sketch, "E2629", {"start": v(46.32, 6.07) * mm, "end": v(46.51, 6.16) * mm});
            skLineSegment(sketch, "E2630", {"start": v(46.51, 6.16) * mm, "end": v(46.75, 6.3) * mm});
            skLineSegment(sketch, "E2631", {"start": v(46.75, 6.3) * mm, "end": v(47.01, 6.47) * mm});
            skLineSegment(sketch, "E2632", {"start": v(47.01, 6.47) * mm, "end": v(47.3, 6.68) * mm});
            skLineSegment(sketch, "E2633", {"start": v(47.3, 6.68) * mm, "end": v(47.59, 6.91) * mm});
            skLineSegment(sketch, "E2634", {"start": v(47.59, 6.91) * mm, "end": v(48.3, 7.6) * mm});
            skLineSegment(sketch, "E2635", {"start": v(48.3, 7.6) * mm, "end": v(49, 8.42) * mm});
            skArc(sketch, "E2636", {"start": v(49, 8.42) * mm, "mid": v(48.72, 9.07) * mm, "end": v(48.43, 9.72) * mm});
            skLineSegment(sketch, "E2637", {"start": v(44.52, 9.17) * mm, "end": v(44.9, 9.37) * mm});
            skLineSegment(sketch, "E2638", {"start": v(44.9, 9.37) * mm, "end": v(45.08, 9.44) * mm});
            skLineSegment(sketch, "E2639", {"start": v(45.08, 9.44) * mm, "end": v(45.35, 9.52) * mm});
            skLineSegment(sketch, "E2640", {"start": v(45.35, 9.52) * mm, "end": v(45.65, 9.6) * mm});
            skLineSegment(sketch, "E2641", {"start": v(45.65, 9.6) * mm, "end": v(46, 9.66) * mm});
            skLineSegment(sketch, "E2642", {"start": v(46, 9.66) * mm, "end": v(46.37, 9.7) * mm});
            skLineSegment(sketch, "E2643", {"start": v(46.37, 9.7) * mm, "end": v(47.35, 9.76) * mm});
            skLineSegment(sketch, "E2644", {"start": v(47.35, 9.76) * mm, "end": v(48.43, 9.72) * mm});
            skArc(sketch, "E2645", {"start": v(43.49, 9.46) * mm, "mid": v(43.94, 9.1) * mm, "end": v(44.52, 9.17) * mm});
            skArc(sketch, "E2646", {"start": v(43.49, 9.46) * mm, "mid": v(43.3, 9.76) * mm, "end": v(43.12, 10.06) * mm});
            skArc(sketch, "E2647", {"start": v(43.34, 11.1) * mm, "mid": v(43.02, 10.63) * mm, "end": v(43.12, 10.06) * mm});
            skLineSegment(sketch, "E2648", {"start": v(43.34, 11.1) * mm, "end": v(43.69, 11.35) * mm});
            skLineSegment(sketch, "E2649", {"start": v(43.69, 11.35) * mm, "end": v(43.84, 11.49) * mm});
            skLineSegment(sketch, "E2650", {"start": v(43.84, 11.49) * mm, "end": v(44.03, 11.68) * mm});
            skLineSegment(sketch, "E2651", {"start": v(44.03, 11.68) * mm, "end": v(44.24, 11.92) * mm});
            skLineSegment(sketch, "E2652", {"start": v(44.24, 11.92) * mm, "end": v(44.46, 12.2) * mm});
            skLineSegment(sketch, "E2653", {"start": v(44.46, 12.2) * mm, "end": v(44.67, 12.5) * mm});
            skLineSegment(sketch, "E2654", {"start": v(44.67, 12.5) * mm, "end": v(45.17, 13.35) * mm});
            skLineSegment(sketch, "E2655", {"start": v(45.17, 13.35) * mm, "end": v(45.62, 14.33) * mm});
            skArc(sketch, "E2656", {"start": v(45.62, 14.33) * mm, "mid": v(45.18, 14.89) * mm, "end": v(44.73, 15.43) * mm});
            skLineSegment(sketch, "E2657", {"start": v(41.1, 13.85) * mm, "end": v(41.42, 14.14) * mm});
            skLineSegment(sketch, "E2658", {"start": v(41.42, 14.14) * mm, "end": v(41.58, 14.26) * mm});
            skLineSegment(sketch, "E2659", {"start": v(41.58, 14.26) * mm, "end": v(41.81, 14.41) * mm});
            skLineSegment(sketch, "E2660", {"start": v(41.81, 14.41) * mm, "end": v(42.09, 14.57) * mm});
            skLineSegment(sketch, "E2661", {"start": v(42.09, 14.57) * mm, "end": v(42.4, 14.72) * mm});
            skLineSegment(sketch, "E2662", {"start": v(42.4, 14.72) * mm, "end": v(42.75, 14.87) * mm});
            skLineSegment(sketch, "E2663", {"start": v(42.75, 14.87) * mm, "end": v(43.67, 15.18) * mm});
            skLineSegment(sketch, "E2664", {"start": v(43.67, 15.18) * mm, "end": v(44.73, 15.43) * mm});
            skArc(sketch, "E2665", {"start": v(40.04, 13.85) * mm, "mid": v(40.57, 13.63) * mm, "end": v(41.1, 13.85) * mm});
            skArc(sketch, "E2666", {"start": v(40.04, 13.85) * mm, "mid": v(39.78, 14.1) * mm, "end": v(39.53, 14.33) * mm});
            skArc(sketch, "E2667", {"start": v(39.45, 15.4) * mm, "mid": v(39.27, 14.85) * mm, "end": v(39.53, 14.33) * mm});
            skLineSegment(sketch, "E2668", {"start": v(39.45, 15.4) * mm, "end": v(39.72, 15.72) * mm});
            skLineSegment(sketch, "E2669", {"start": v(39.72, 15.72) * mm, "end": v(39.83, 15.9) * mm});
            skLineSegment(sketch, "E2670", {"start": v(39.83, 15.9) * mm, "end": v(39.96, 16.14) * mm});
            skLineSegment(sketch, "E2671", {"start": v(39.96, 16.14) * mm, "end": v(40.1, 16.42) * mm});
            skLineSegment(sketch, "E2672", {"start": v(40.1, 16.42) * mm, "end": v(40.23, 16.75) * mm});
            skLineSegment(sketch, "E2673", {"start": v(40.23, 16.75) * mm, "end": v(40.36, 17.1) * mm});
            skLineSegment(sketch, "E2674", {"start": v(40.36, 17.1) * mm, "end": v(40.6, 18.05) * mm});
            skLineSegment(sketch, "E2675", {"start": v(40.6, 18.05) * mm, "end": v(40.78, 19.12) * mm});
            skArc(sketch, "E2676", {"start": v(40.78, 19.12) * mm, "mid": v(40.2, 19.53) * mm, "end": v(39.62, 19.93) * mm});
            skLineSegment(sketch, "E2677", {"start": v(36.56, 17.44) * mm, "end": v(36.78, 17.8) * mm});
            skLineSegment(sketch, "E2678", {"start": v(36.78, 17.8) * mm, "end": v(36.9, 17.96) * mm});
            skLineSegment(sketch, "E2679", {"start": v(36.9, 17.96) * mm, "end": v(37.09, 18.17) * mm});
            skLineSegment(sketch, "E2680", {"start": v(37.09, 18.17) * mm, "end": v(37.31, 18.4) * mm});
            skLineSegment(sketch, "E2681", {"start": v(37.31, 18.4) * mm, "end": v(37.57, 18.62) * mm});
            skLineSegment(sketch, "E2682", {"start": v(37.57, 18.62) * mm, "end": v(37.87, 18.86) * mm});
            skLineSegment(sketch, "E2683", {"start": v(37.87, 18.86) * mm, "end": v(38.67, 19.41) * mm});
            skLineSegment(sketch, "E2684", {"start": v(38.67, 19.41) * mm, "end": v(39.62, 19.93) * mm});
            skArc(sketch, "E2685", {"start": v(35.53, 17.15) * mm, "mid": v(36.1, 17.08) * mm, "end": v(36.56, 17.44) * mm});
            skArc(sketch, "E2686", {"start": v(35.53, 17.15) * mm, "mid": v(35.22, 17.31) * mm, "end": v(34.91, 17.47) * mm});
            skArc(sketch, "E2687", {"start": v(34.55, 18.48) * mm, "mid": v(34.53, 17.9) * mm, "end": v(34.91, 17.47) * mm});
            skLineSegment(sketch, "E2688", {"start": v(34.55, 18.48) * mm, "end": v(34.72, 18.87) * mm});
            skLineSegment(sketch, "E2689", {"start": v(34.72, 18.87) * mm, "end": v(34.78, 19.06) * mm});
            skLineSegment(sketch, "E2690", {"start": v(34.78, 19.06) * mm, "end": v(34.84, 19.33) * mm});
            skLineSegment(sketch, "E2691", {"start": v(34.84, 19.33) * mm, "end": v(34.9, 19.64) * mm});
            skLineSegment(sketch, "E2692", {"start": v(34.9, 19.64) * mm, "end": v(34.94, 19.99) * mm});
            skLineSegment(sketch, "E2693", {"start": v(34.94, 19.99) * mm, "end": v(34.96, 20.36) * mm});
            skLineSegment(sketch, "E2694", {"start": v(34.96, 20.36) * mm, "end": v(34.95, 21.34) * mm});
            skLineSegment(sketch, "E2695", {"start": v(34.95, 21.34) * mm, "end": v(34.83, 22.42) * mm});
            skArc(sketch, "E2696", {"start": v(34.83, 22.42) * mm, "mid": v(34.16, 22.67) * mm, "end": v(33.5, 22.9) * mm});
            skLineSegment(sketch, "E2697", {"start": v(31.22, 19.66) * mm, "end": v(31.33, 20.07) * mm});
            skLineSegment(sketch, "E2698", {"start": v(31.33, 20.07) * mm, "end": v(31.4, 20.26) * mm});
            skLineSegment(sketch, "E2699", {"start": v(31.4, 20.26) * mm, "end": v(31.53, 20.5) * mm});
            skLineSegment(sketch, "E2700", {"start": v(31.53, 20.5) * mm, "end": v(31.68, 20.78) * mm});
            skLineSegment(sketch, "E2701", {"start": v(31.68, 20.78) * mm, "end": v(31.87, 21.08) * mm});
            skLineSegment(sketch, "E2702", {"start": v(31.87, 21.08) * mm, "end": v(32.1, 21.39) * mm});
            skLineSegment(sketch, "E2703", {"start": v(32.1, 21.39) * mm, "end": v(32.72, 22.14) * mm});
            skLineSegment(sketch, "E2704", {"start": v(32.72, 22.14) * mm, "end": v(33.5, 22.9) * mm});
            skArc(sketch, "E2705", {"start": v(30.3, 19.1) * mm, "mid": v(30.87, 19.2) * mm, "end": v(31.22, 19.66) * mm});
            skArc(sketch, "E2706", {"start": v(30.3, 19.1) * mm, "mid": v(29.96, 19.18) * mm, "end": v(29.62, 19.25) * mm});
            skArc(sketch, "E2707", {"start": v(29, 20.12) * mm, "mid": v(29.13, 19.56) * mm, "end": v(29.62, 19.25) * mm});
            skLineSegment(sketch, "E2708", {"start": v(29, 20.12) * mm, "end": v(29.06, 20.54) * mm});
            skLineSegment(sketch, "E2709", {"start": v(29.06, 20.54) * mm, "end": v(29.07, 20.75) * mm});
            skLineSegment(sketch, "E2710", {"start": v(29.07, 20.75) * mm, "end": v(29.05, 21.02) * mm});
            skLineSegment(sketch, "E2711", {"start": v(29.05, 21.02) * mm, "end": v(29.02, 21.34) * mm});
            skLineSegment(sketch, "E2712", {"start": v(29.02, 21.34) * mm, "end": v(28.97, 21.68) * mm});
            skLineSegment(sketch, "E2713", {"start": v(28.97, 21.68) * mm, "end": v(28.89, 22.05) * mm});
            skLineSegment(sketch, "E2714", {"start": v(28.89, 22.05) * mm, "end": v(28.61, 22.99) * mm});
            skLineSegment(sketch, "E2715", {"start": v(28.61, 22.99) * mm, "end": v(28.2, 24) * mm});
            skArc(sketch, "E2716", {"start": v(28.2, 24) * mm, "mid": v(27.5, 24.05) * mm, "end": v(26.79, 24.09) * mm});
            skLineSegment(sketch, "E2717", {"start": v(25.47, 20.36) * mm, "end": v(25.47, 20.79) * mm});
            skLineSegment(sketch, "E2718", {"start": v(25.47, 20.79) * mm, "end": v(25.5, 21) * mm});
            skLineSegment(sketch, "E2719", {"start": v(25.5, 21) * mm, "end": v(25.54, 21.26) * mm});
            skLineSegment(sketch, "E2720", {"start": v(25.54, 21.26) * mm, "end": v(25.62, 21.57) * mm});
            skLineSegment(sketch, "E2721", {"start": v(25.62, 21.57) * mm, "end": v(25.72, 21.9) * mm});
            skLineSegment(sketch, "E2722", {"start": v(25.72, 21.9) * mm, "end": v(25.85, 22.26) * mm});
            skLineSegment(sketch, "E2723", {"start": v(25.85, 22.26) * mm, "end": v(26.25, 23.15) * mm});
            skLineSegment(sketch, "E2724", {"start": v(26.25, 23.15) * mm, "end": v(26.79, 24.09) * mm});
            skArc(sketch, "E2725", {"start": v(24.74, 19.58) * mm, "mid": v(25.26, 19.83) * mm, "end": v(25.47, 20.36) * mm});
            skArc(sketch, "E2726", {"start": v(24.74, 19.58) * mm, "mid": v(24.4, 19.56) * mm, "end": v(24.04, 19.53) * mm});
            skArc(sketch, "E2727", {"start": v(23.21, 20.2) * mm, "mid": v(23.5, 19.7) * mm, "end": v(24.04, 19.53) * mm});
            skLineSegment(sketch, "E2728", {"start": v(23.21, 20.2) * mm, "end": v(23.16, 20.63) * mm});
            skLineSegment(sketch, "E2729", {"start": v(23.16, 20.63) * mm, "end": v(23.1, 20.83) * mm});
            skLineSegment(sketch, "E2730", {"start": v(23.1, 20.83) * mm, "end": v(23.02, 21.09) * mm});
            skLineSegment(sketch, "E2731", {"start": v(23.02, 21.09) * mm, "end": v(22.9, 21.38) * mm});
            skLineSegment(sketch, "E2732", {"start": v(22.9, 21.38) * mm, "end": v(22.76, 21.7) * mm});
            skLineSegment(sketch, "E2733", {"start": v(22.76, 21.7) * mm, "end": v(22.58, 22.04) * mm});
            skLineSegment(sketch, "E2734", {"start": v(22.58, 22.04) * mm, "end": v(22.06, 22.86) * mm});
            skLineSegment(sketch, "E2735", {"start": v(22.06, 22.86) * mm, "end": v(21.4, 23.72) * mm});
            skArc(sketch, "E2736", {"start": v(21.4, 23.72) * mm, "mid": v(20.7, 23.59) * mm, "end": v(20.01, 23.43) * mm});
            skLineSegment(sketch, "E2737", {"start": v(19.75, 19.49) * mm, "end": v(19.63, 19.9) * mm});
            skLineSegment(sketch, "E2738", {"start": v(19.63, 19.9) * mm, "end": v(19.6, 20.1) * mm});
            skLineSegment(sketch, "E2739", {"start": v(19.6, 20.1) * mm, "end": v(19.58, 20.37) * mm});
            skLineSegment(sketch, "E2740", {"start": v(19.58, 20.37) * mm, "end": v(19.57, 20.7) * mm});
            skLineSegment(sketch, "E2741", {"start": v(19.57, 20.7) * mm, "end": v(19.57, 21.04) * mm});
            skLineSegment(sketch, "E2742", {"start": v(19.57, 21.04) * mm, "end": v(19.6, 21.42) * mm});
            skLineSegment(sketch, "E2743", {"start": v(19.6, 21.42) * mm, "end": v(19.75, 22.38) * mm});
            skLineSegment(sketch, "E2744", {"start": v(19.75, 22.38) * mm, "end": v(20.01, 23.43) * mm});
            skArc(sketch, "E2745", {"start": v(19.26, 18.54) * mm, "mid": v(19.7, 18.92) * mm, "end": v(19.75, 19.49) * mm});
            skArc(sketch, "E2746", {"start": v(19.26, 18.54) * mm, "mid": v(18.93, 18.43) * mm, "end": v(18.6, 18.3) * mm});
            skArc(sketch, "E2747", {"start": v(17.62, 18.73) * mm, "mid": v(18.02, 18.32) * mm, "end": v(18.6, 18.3) * mm});
            skLineSegment(sketch, "E2748", {"start": v(17.62, 18.73) * mm, "end": v(17.45, 19.12) * mm});
            skLineSegment(sketch, "E2749", {"start": v(17.45, 19.12) * mm, "end": v(17.35, 19.3) * mm});
            skLineSegment(sketch, "E2750", {"start": v(17.35, 19.3) * mm, "end": v(17.2, 19.53) * mm});
            skLineSegment(sketch, "E2751", {"start": v(17.2, 19.53) * mm, "end": v(17, 19.78) * mm});
            skLineSegment(sketch, "E2752", {"start": v(17, 19.78) * mm, "end": v(16.78, 20.05) * mm});
            skLineSegment(sketch, "E2753", {"start": v(16.78, 20.05) * mm, "end": v(16.52, 20.32) * mm});
            skLineSegment(sketch, "E2754", {"start": v(16.52, 20.32) * mm, "end": v(15.8, 20.98) * mm});
            skLineSegment(sketch, "E2755", {"start": v(15.8, 20.98) * mm, "end": v(14.92, 21.62) * mm});
            skArc(sketch, "E2756", {"start": v(14.92, 21.62) * mm, "mid": v(14.29, 21.3) * mm, "end": v(13.66, 20.97) * mm});
            skLineSegment(sketch, "E2757", {"start": v(14.48, 17.1) * mm, "end": v(14.25, 17.47) * mm});
            skLineSegment(sketch, "E2758", {"start": v(14.25, 17.47) * mm, "end": v(14.17, 17.65) * mm});
            skLineSegment(sketch, "E2759", {"start": v(14.17, 17.65) * mm, "end": v(14.07, 17.9) * mm});
            skLineSegment(sketch, "E2760", {"start": v(14.07, 17.9) * mm, "end": v(13.97, 18.21) * mm});
            skLineSegment(sketch, "E2761", {"start": v(13.97, 18.21) * mm, "end": v(13.89, 18.55) * mm});
            skLineSegment(sketch, "E2762", {"start": v(13.89, 18.55) * mm, "end": v(13.81, 18.92) * mm});
            skLineSegment(sketch, "E2763", {"start": v(13.81, 18.92) * mm, "end": v(13.7, 19.89) * mm});
            skLineSegment(sketch, "E2764", {"start": v(13.7, 19.89) * mm, "end": v(13.66, 20.97) * mm});
            skArc(sketch, "E2765", {"start": v(14.26, 16.06) * mm, "mid": v(14.58, 16.54) * mm, "end": v(14.48, 17.1) * mm});
            skArc(sketch, "E2766", {"start": v(14.26, 16.06) * mm, "mid": v(13.97, 15.86) * mm, "end": v(13.69, 15.65) * mm});
            skArc(sketch, "E2767", {"start": v(12.63, 15.8) * mm, "mid": v(13.13, 15.51) * mm, "end": v(13.69, 15.65) * mm});
            skLineSegment(sketch, "E2768", {"start": v(12.63, 15.8) * mm, "end": v(12.36, 16.13) * mm});
            skLineSegment(sketch, "E2769", {"start": v(12.36, 16.13) * mm, "end": v(12.21, 16.27) * mm});
            skLineSegment(sketch, "E2770", {"start": v(12.21, 16.27) * mm, "end": v(12, 16.45) * mm});
            skLineSegment(sketch, "E2771", {"start": v(12, 16.45) * mm, "end": v(11.75, 16.64) * mm});
            skLineSegment(sketch, "E2772", {"start": v(11.75, 16.64) * mm, "end": v(11.46, 16.84) * mm});
            skLineSegment(sketch, "E2773", {"start": v(11.46, 16.84) * mm, "end": v(11.14, 17.03) * mm});
            skLineSegment(sketch, "E2774", {"start": v(11.14, 17.03) * mm, "end": v(10.26, 17.47) * mm});
            skLineSegment(sketch, "E2775", {"start": v(10.26, 17.47) * mm, "end": v(9.25, 17.86) * mm});
            skArc(sketch, "E2776", {"start": v(9.25, 17.86) * mm, "mid": v(8.73, 17.38) * mm, "end": v(8.22, 16.89) * mm});
            skLineSegment(sketch, "E2777", {"start": v(10.04, 13.38) * mm, "end": v(9.73, 13.67) * mm});
            skLineSegment(sketch, "E2778", {"start": v(9.73, 13.67) * mm, "end": v(9.6, 13.83) * mm});
            skLineSegment(sketch, "E2779", {"start": v(9.6, 13.83) * mm, "end": v(9.43, 14.05) * mm});
            skLineSegment(sketch, "E2780", {"start": v(9.43, 14.05) * mm, "end": v(9.26, 14.31) * mm});
            skLineSegment(sketch, "E2781", {"start": v(9.26, 14.31) * mm, "end": v(9.08, 14.62) * mm});
            skLineSegment(sketch, "E2782", {"start": v(9.08, 14.62) * mm, "end": v(8.91, 14.95) * mm});
            skLineSegment(sketch, "E2783", {"start": v(8.91, 14.95) * mm, "end": v(8.53, 15.85) * mm});
            skLineSegment(sketch, "E2784", {"start": v(8.53, 15.85) * mm, "end": v(8.22, 16.89) * mm});
            skArc(sketch, "E2785", {"start": v(10.11, 12.32) * mm, "mid": v(10.3, 12.86) * mm, "end": v(10.04, 13.38) * mm});
            skArc(sketch, "E2786", {"start": v(10.11, 12.32) * mm, "mid": v(9.89, 12.05) * mm, "end": v(9.67, 11.77) * mm});
            skArc(sketch, "E2787", {"start": v(8.61, 11.63) * mm, "mid": v(9.17, 11.49) * mm, "end": v(9.67, 11.77) * mm});
            skLineSegment(sketch, "E2788", {"start": v(8.61, 11.63) * mm, "end": v(8.27, 11.87) * mm});
            skLineSegment(sketch, "E2789", {"start": v(8.27, 11.87) * mm, "end": v(8.09, 11.97) * mm});
            skLineSegment(sketch, "E2790", {"start": v(8.09, 11.97) * mm, "end": v(7.84, 12.09) * mm});
            skLineSegment(sketch, "E2791", {"start": v(7.84, 12.09) * mm, "end": v(7.54, 12.2) * mm});
            skLineSegment(sketch, "E2792", {"start": v(7.54, 12.2) * mm, "end": v(7.2, 12.31) * mm});
            skLineSegment(sketch, "E2793", {"start": v(7.2, 12.31) * mm, "end": v(6.85, 12.41) * mm});
            skLineSegment(sketch, "E2794", {"start": v(6.85, 12.41) * mm, "end": v(5.89, 12.6) * mm});
            skLineSegment(sketch, "E2795", {"start": v(5.89, 12.6) * mm, "end": v(4.8, 12.7) * mm});
            skArc(sketch, "E2796", {"start": v(4.8, 12.7) * mm, "mid": v(4.43, 12.1) * mm, "end": v(4.07, 11.49) * mm});
            skLineSegment(sketch, "E2797", {"start": v(6.77, 8.6) * mm, "end": v(6.4, 8.8) * mm});
            skLineSegment(sketch, "E2798", {"start": v(6.4, 8.8) * mm, "end": v(6.22, 8.91) * mm});
            skLineSegment(sketch, "E2799", {"start": v(6.22, 8.91) * mm, "end": v(6, 9.08) * mm});
            skLineSegment(sketch, "E2800", {"start": v(6, 9.08) * mm, "end": v(5.77, 9.29) * mm});
            skLineSegment(sketch, "E2801", {"start": v(5.77, 9.29) * mm, "end": v(5.52, 9.53) * mm});
            skLineSegment(sketch, "E2802", {"start": v(5.52, 9.53) * mm, "end": v(5.26, 9.8) * mm});
            skLineSegment(sketch, "E2803", {"start": v(5.26, 9.8) * mm, "end": v(4.66, 10.58) * mm});
            skLineSegment(sketch, "E2804", {"start": v(4.66, 10.58) * mm, "end": v(4.07, 11.49) * mm});
            skArc(sketch, "E2805", {"start": v(7.13, 7.6) * mm, "mid": v(7.16, 8.17) * mm, "end": v(6.77, 8.6) * mm});
            skArc(sketch, "E2806", {"start": v(7.13, 7.6) * mm, "mid": v(6.99, 7.28) * mm, "end": v(6.85, 6.95) * mm});
            skArc(sketch, "E2807", {"start": v(5.87, 6.53) * mm, "mid": v(6.45, 6.54) * mm, "end": v(6.85, 6.95) * mm});
            skLineSegment(sketch, "E2808", {"start": v(5.87, 6.53) * mm, "end": v(5.47, 6.67) * mm});
            skLineSegment(sketch, "E2809", {"start": v(5.47, 6.67) * mm, "end": v(5.27, 6.72) * mm});
            skLineSegment(sketch, "E2810", {"start": v(5.27, 6.72) * mm, "end": v(5, 6.76) * mm});
            skLineSegment(sketch, "E2811", {"start": v(5, 6.76) * mm, "end": v(4.69, 6.8) * mm});
            skLineSegment(sketch, "E2812", {"start": v(4.69, 6.8) * mm, "end": v(4.34, 6.81) * mm});
            skLineSegment(sketch, "E2813", {"start": v(4.34, 6.81) * mm, "end": v(3.96, 6.8) * mm});
            skLineSegment(sketch, "E2814", {"start": v(3.96, 6.8) * mm, "end": v(2.99, 6.73) * mm});
            skLineSegment(sketch, "E2815", {"start": v(2.99, 6.73) * mm, "end": v(1.92, 6.53) * mm});
            skArc(sketch, "E2816", {"start": v(1.92, 6.53) * mm, "mid": v(1.72, 5.85) * mm, "end": v(1.54, 5.17) * mm});
            skLineSegment(sketch, "E2817", {"start": v(4.92, 3.12) * mm, "end": v(4.5, 3.2) * mm});
            skLineSegment(sketch, "E2818", {"start": v(4.5, 3.2) * mm, "end": v(4.3, 3.27) * mm});
            skLineSegment(sketch, "E2819", {"start": v(4.3, 3.27) * mm, "end": v(4.05, 3.37) * mm});
            skLineSegment(sketch, "E2820", {"start": v(4.05, 3.37) * mm, "end": v(3.77, 3.51) * mm});
            skLineSegment(sketch, "E2821", {"start": v(3.77, 3.51) * mm, "end": v(3.46, 3.68) * mm});
            skLineSegment(sketch, "E2822", {"start": v(3.46, 3.68) * mm, "end": v(3.14, 3.87) * mm});
            skLineSegment(sketch, "E2823", {"start": v(3.14, 3.87) * mm, "end": v(2.35, 4.45) * mm});
            skLineSegment(sketch, "E2824", {"start": v(2.35, 4.45) * mm, "end": v(1.54, 5.17) * mm});
            skArc(sketch, "E2825", {"start": v(5.53, 2.25) * mm, "mid": v(5.4, 2.8) * mm, "end": v(4.92, 3.12) * mm});
            skArc(sketch, "E2826", {"start": v(5.53, 2.25) * mm, "mid": v(5.48, 1.9) * mm, "end": v(5.44, 1.55) * mm});
            skArc(sketch, "E2827", {"start": v(4.6, 0.88) * mm, "mid": v(5.16, 1.05) * mm, "end": v(5.44, 1.55) * mm});
            skLineSegment(sketch, "E2828", {"start": v(4.6, 0.88) * mm, "end": v(4.19, 0.9) * mm});
            skLineSegment(sketch, "E2829", {"start": v(4.19, 0.9) * mm, "end": v(3.98, 0.9) * mm});
            skLineSegment(sketch, "E2830", {"start": v(3.98, 0.9) * mm, "end": v(3.7, 0.87) * mm});
            skLineSegment(sketch, "E2831", {"start": v(3.7, 0.87) * mm, "end": v(3.4, 0.81) * mm});
            skLineSegment(sketch, "E2832", {"start": v(3.4, 0.81) * mm, "end": v(3.05, 0.74) * mm});
            skLineSegment(sketch, "E2833", {"start": v(3.05, 0.74) * mm, "end": v(2.7, 0.63) * mm});
            skLineSegment(sketch, "E2834", {"start": v(2.7, 0.63) * mm, "end": v(1.78, 0.3) * mm});
            skCircle(sketch, "E2835", {"center": v(93.75, -43.1) * mm, "radius": 4.5 * mm});
            skArc(sketch, "E2836", {"start": v(92.37, -42.3) * mm, "mid": v(92.15, -43.1) * mm, "end": v(92.37, -43.9) * mm});
            skArc(sketch, "E2837", {"start": v(93.75, -41.7) * mm, "mid": v(93.05, -41.9) * mm, "end": v(92.54, -42.4) * mm});
            skLineSegment(sketch, "E2838", {"start": v(93.75, -41.7) * mm, "end": v(93.75, -41.5) * mm});
            skLineSegment(sketch, "E2839.1.0", {"start": v(92.54, -42.4) * mm, "end": v(92.37, -42.3) * mm});
            skLineSegment(sketch, "E2839.2.0", {"start": v(92.54, -43.8) * mm, "end": v(92.37, -43.9) * mm});
            skLineSegment(sketch, "E2839.3.0", {"start": v(93.75, -44.5) * mm, "end": v(93.75, -44.7) * mm});
            skLineSegment(sketch, "E2839.4.0", {"start": v(94.97, -43.8) * mm, "end": v(95.14, -43.9) * mm});
            skLineSegment(sketch, "E2839.5.0", {"start": v(94.97, -42.4) * mm, "end": v(95.14, -42.3) * mm});
            skArc(sketch, "E2840.trimOffspring", {"start": v(94.97, -43.8) * mm, "mid": v(95.15, -43.1) * mm, "end": v(94.97, -42.4) * mm});
            skArc(sketch, "E2841.trimOffspring", {"start": v(92.54, -43.8) * mm, "mid": v(93.05, -44.32) * mm, "end": v(93.75, -44.5) * mm});
            skArc(sketch, "E2842.trimOffspring", {"start": v(93.75, -44.7) * mm, "mid": v(94.55, -44.5) * mm, "end": v(95.14, -43.9) * mm});
            skArc(sketch, "E2843.trimOffspring", {"start": v(95.14, -42.3) * mm, "mid": v(94.55, -41.72) * mm, "end": v(93.75, -41.5) * mm});
            skCircle(sketch, "E2844", {"center": v(93.22, -57.27) * mm, "radius": 4.5 * mm});
            skArc(sketch, "E2845", {"start": v(91.83, -56.47) * mm, "mid": v(91.62, -57.27) * mm, "end": v(91.83, -58.07) * mm});
            skArc(sketch, "E2846", {"start": v(93.22, -55.87) * mm, "mid": v(92.52, -56.06) * mm, "end": v(92, -56.57) * mm});
            skLineSegment(sketch, "E2847", {"start": v(93.22, -55.87) * mm, "end": v(93.22, -55.67) * mm});
            skLineSegment(sketch, "E2848.1.0", {"start": v(92, -56.57) * mm, "end": v(91.83, -56.47) * mm});
            skLineSegment(sketch, "E2848.2.0", {"start": v(92, -57.97) * mm, "end": v(91.83, -58.07) * mm});
            skLineSegment(sketch, "E2848.3.0", {"start": v(93.22, -58.67) * mm, "end": v(93.22, -58.87) * mm});
            skLineSegment(sketch, "E2848.4.0", {"start": v(94.43, -57.97) * mm, "end": v(94.6, -58.07) * mm});
            skLineSegment(sketch, "E2848.5.0", {"start": v(94.43, -56.57) * mm, "end": v(94.6, -56.47) * mm});
            skArc(sketch, "E2849.trimOffspring", {"start": v(94.43, -57.97) * mm, "mid": v(94.62, -57.27) * mm, "end": v(94.43, -56.57) * mm});
            skArc(sketch, "E2850.trimOffspring", {"start": v(92, -57.97) * mm, "mid": v(92.52, -58.48) * mm, "end": v(93.22, -58.67) * mm});
            skArc(sketch, "E2851.trimOffspring", {"start": v(93.22, -58.87) * mm, "mid": v(94.02, -58.65) * mm, "end": v(94.6, -58.07) * mm});
            skArc(sketch, "E2852.trimOffspring", {"start": v(94.6, -56.47) * mm, "mid": v(94.02, -55.88) * mm, "end": v(93.22, -55.67) * mm});
            skCircle(sketch, "E2853", {"center": v(93.83, -71.3) * mm, "radius": 4.5 * mm});
            skArc(sketch, "E2854", {"start": v(92.45, -70.5) * mm, "mid": v(92.23, -71.3) * mm, "end": v(92.45, -72.1) * mm});
            skArc(sketch, "E2855", {"start": v(93.83, -69.9) * mm, "mid": v(93.13, -70.1) * mm, "end": v(92.62, -70.6) * mm});
            skLineSegment(sketch, "E2856", {"start": v(93.83, -69.9) * mm, "end": v(93.83, -69.7) * mm});
            skLineSegment(sketch, "E2857.1.0", {"start": v(92.62, -70.6) * mm, "end": v(92.45, -70.5) * mm});
            skLineSegment(sketch, "E2857.2.0", {"start": v(92.62, -72) * mm, "end": v(92.45, -72.1) * mm});
            skLineSegment(sketch, "E2857.3.0", {"start": v(93.83, -72.7) * mm, "end": v(93.83, -72.9) * mm});
            skLineSegment(sketch, "E2857.4.0", {"start": v(95.05, -72) * mm, "end": v(95.22, -72.1) * mm});
            skLineSegment(sketch, "E2857.5.0", {"start": v(95.05, -70.6) * mm, "end": v(95.22, -70.5) * mm});
            skArc(sketch, "E2858.trimOffspring", {"start": v(95.05, -72) * mm, "mid": v(95.23, -71.3) * mm, "end": v(95.05, -70.6) * mm});
            skArc(sketch, "E2859.trimOffspring", {"start": v(92.62, -72) * mm, "mid": v(93.13, -72.52) * mm, "end": v(93.83, -72.7) * mm});
            skArc(sketch, "E2860.trimOffspring", {"start": v(93.83, -72.9) * mm, "mid": v(94.63, -72.7) * mm, "end": v(95.22, -72.1) * mm});
            skArc(sketch, "E2861.trimOffspring", {"start": v(95.22, -70.5) * mm, "mid": v(94.63, -69.92) * mm, "end": v(93.83, -69.7) * mm});
            skCircle(sketch, "E2862", {"center": v(93.3, -86.76) * mm, "radius": 4.5 * mm});
            skArc(sketch, "E2863", {"start": v(91.92, -85.96) * mm, "mid": v(91.7, -86.76) * mm, "end": v(91.92, -87.56) * mm});
            skArc(sketch, "E2864", {"start": v(93.3, -85.36) * mm, "mid": v(92.6, -85.55) * mm, "end": v(92.1, -86.06) * mm});
            skLineSegment(sketch, "E2865", {"start": v(93.3, -85.36) * mm, "end": v(93.3, -85.16) * mm});
            skLineSegment(sketch, "E2866.1.0", {"start": v(92.1, -86.06) * mm, "end": v(91.92, -85.96) * mm});
            skLineSegment(sketch, "E2866.2.0", {"start": v(92.1, -87.46) * mm, "end": v(91.92, -87.56) * mm});
            skLineSegment(sketch, "E2866.3.0", {"start": v(93.3, -88.16) * mm, "end": v(93.3, -88.36) * mm});
            skLineSegment(sketch, "E2866.4.0", {"start": v(94.52, -87.46) * mm, "end": v(94.69, -87.56) * mm});
            skLineSegment(sketch, "E2866.5.0", {"start": v(94.52, -86.06) * mm, "end": v(94.69, -85.96) * mm});
            skArc(sketch, "E2867.trimOffspring", {"start": v(94.52, -87.46) * mm, "mid": v(94.7, -86.76) * mm, "end": v(94.52, -86.06) * mm});
            skArc(sketch, "E2868.trimOffspring", {"start": v(92.1, -87.46) * mm, "mid": v(92.6, -87.98) * mm, "end": v(93.3, -88.16) * mm});
            skArc(sketch, "E2869.trimOffspring", {"start": v(93.3, -88.36) * mm, "mid": v(94.1, -88.15) * mm, "end": v(94.69, -87.56) * mm});
            skArc(sketch, "E2870.trimOffspring", {"start": v(94.69, -85.96) * mm, "mid": v(94.1, -85.38) * mm, "end": v(93.3, -85.16) * mm});
            skArc(sketch, "E2871", {"start": v(94.2, 50.51) * mm, "mid": v(93.4, 50.4) * mm, "end": v(92.65, 50.1) * mm});
            skArc(sketch, "E2872", {"start": v(96.89, 48.96) * mm, "mid": v(96.4, 49.6) * mm, "end": v(95.75, 50.1) * mm});
            skArc(sketch, "E2873", {"start": v(96.89, 45.86) * mm, "mid": v(97.2, 46.61) * mm, "end": v(97.3, 47.41) * mm});
            skArc(sketch, "E2874", {"start": v(94.2, 44.31) * mm, "mid": v(95, 44.42) * mm, "end": v(95.75, 44.73) * mm});
            skArc(sketch, "E2875", {"start": v(91.52, 45.86) * mm, "mid": v(92.01, 45.22) * mm, "end": v(92.65, 44.73) * mm});
            skArc(sketch, "E2876", {"start": v(91.3, 47.41) * mm, "mid": v(91.4, 46.66) * mm, "end": v(91.7, 45.96) * mm});
            skArc(sketch, "E2877", {"start": v(92.75, 44.9) * mm, "mid": v(93.45, 44.61) * mm, "end": v(94.2, 44.51) * mm});
            skArc(sketch, "E2878", {"start": v(95.65, 44.9) * mm, "mid": v(96.25, 45.36) * mm, "end": v(96.71, 45.96) * mm});
            skArc(sketch, "E2879", {"start": v(97.1, 47.41) * mm, "mid": v(97, 48.17) * mm, "end": v(96.71, 48.86) * mm});
            skArc(sketch, "E2880", {"start": v(95.65, 49.93) * mm, "mid": v(94.95, 50.22) * mm, "end": v(94.2, 50.31) * mm});
            skLineSegment(sketch, "E2881", {"start": v(95.65, 49.93) * mm, "end": v(95.75, 50.1) * mm});
            skLineSegment(sketch, "E2882", {"start": v(96.71, 48.86) * mm, "end": v(96.89, 48.96) * mm});
            skLineSegment(sketch, "E2883", {"start": v(97.1, 47.41) * mm, "end": v(97.3, 47.41) * mm});
            skLineSegment(sketch, "E2884", {"start": v(96.71, 45.96) * mm, "end": v(96.89, 45.86) * mm});
            skLineSegment(sketch, "E2885", {"start": v(95.65, 44.9) * mm, "end": v(95.75, 44.73) * mm});
            skLineSegment(sketch, "E2886", {"start": v(94.2, 44.51) * mm, "end": v(94.2, 44.31) * mm});
            skLineSegment(sketch, "E2887", {"start": v(92.75, 44.9) * mm, "end": v(92.65, 44.73) * mm});
            skLineSegment(sketch, "E2888", {"start": v(91.7, 45.96) * mm, "end": v(91.52, 45.86) * mm});
            skLineSegment(sketch, "E2889", {"start": v(91.3, 47.41) * mm, "end": v(91.1, 47.41) * mm});
            skLineSegment(sketch, "E2890", {"start": v(91.7, 48.86) * mm, "end": v(91.52, 48.96) * mm});
            skLineSegment(sketch, "E2891", {"start": v(92.75, 49.93) * mm, "end": v(92.65, 50.1) * mm});
            skLineSegment(sketch, "E2892", {"start": v(94.2, 50.31) * mm, "end": v(94.2, 50.51) * mm});
            skArc(sketch, "E2893", {"start": v(92.75, 49.93) * mm, "mid": v(92.15, 49.47) * mm, "end": v(91.7, 48.86) * mm});
            skArc(sketch, "E2894", {"start": v(91.52, 48.96) * mm, "mid": v(91.2, 48.22) * mm, "end": v(91.1, 47.41) * mm});
            skCircle(sketch, "E2895", {"center": v(94.2, 47.41) * mm, "radius": 6 * mm});
            skSolve(sketch);
        }
        {
            var Q0;
            Q0 = qSketchRegion(id + "F0", true);
            extrude(context, id + "F1", {"entities" : qUnion([Q0]), "depth" : 5 * mm, "offsetDistance" : 25 * mm});
        }
    });
